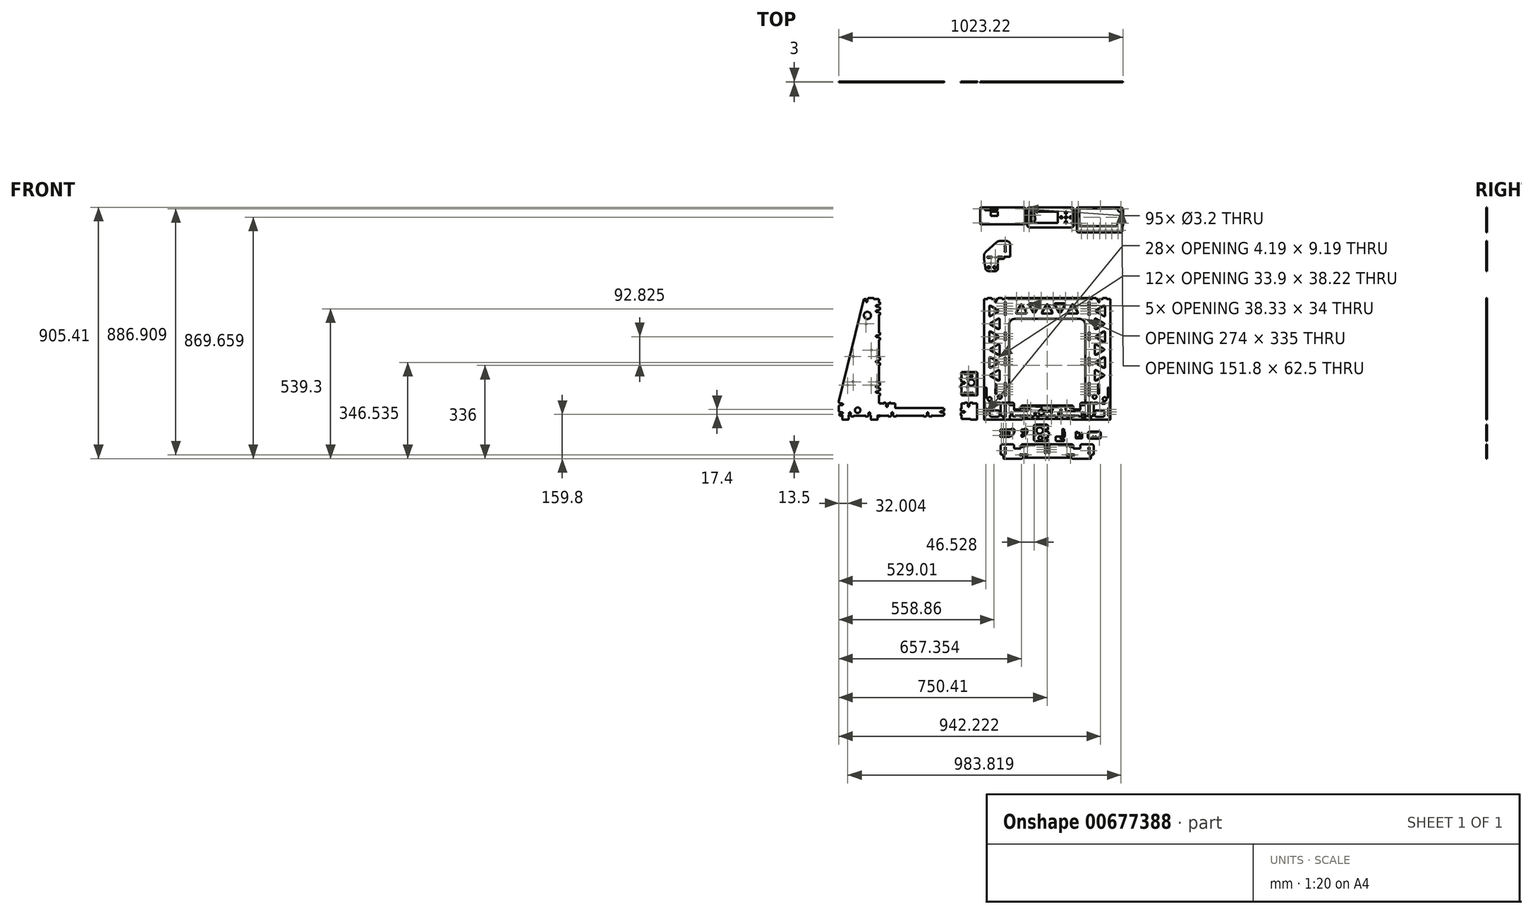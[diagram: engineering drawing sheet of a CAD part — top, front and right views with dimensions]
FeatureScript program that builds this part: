
annotation { "Feature Type Name" : "Feature", "Feature Type Description" : "" }
export const myFeature = defineFeature(function(context is Context, id is Id, definition is map)
    precondition{}
    {
        {
            var Q0;
            Q0=qCreatedBy(makeId("Front.planeOp"),FACE);
            var sketch = newSketch(context, id + "F0", { "sketchPlane" : qUnion([Q0])});
            skLineSegment(sketch, "E0", {"start": v(-153.6, 431.37) * mm, "end": v(-153.6, 433) * mm});
            skLineSegment(sketch, "E1", {"start": v(-177.67, 430.5) * mm, "end": v(-184.25, 430.5) * mm});
            skLineSegment(sketch, "E2", {"start": v(-153.1, 433.5) * mm, "end": v(153.1, 433.5) * mm});
            skLineSegment(sketch, "E3", {"start": v(153.6, 433) * mm, "end": v(153.6, 431.37) * mm});
            skLineSegment(sketch, "E4", {"start": v(177.67, 430.5) * mm, "end": v(184.25, 430.5) * mm});
            skLineSegment(sketch, "E5", {"start": v(-187.75, 430.5) * mm, "end": v(-199.13, 430.5) * mm});
            skLineSegment(sketch, "E6", {"start": v(-200, 433) * mm, "end": v(-200, 431.37) * mm});
            skLineSegment(sketch, "E7", {"start": v(-214.5, 433.5) * mm, "end": v(-200.5, 433.5) * mm});
            skLineSegment(sketch, "E8", {"start": v(187.75, 430.5) * mm, "end": v(199.13, 430.5) * mm});
            skLineSegment(sketch, "E9", {"start": v(-215, 431.37) * mm, "end": v(-215, 433) * mm});
            skLineSegment(sketch, "E10", {"start": v(200, 431.37) * mm, "end": v(200, 433) * mm});
            skLineSegment(sketch, "E11", {"start": v(-227.5, 430.5) * mm, "end": v(-215.87, 430.5) * mm});
            skLineSegment(sketch, "E12", {"start": v(200.5, 433.5) * mm, "end": v(214.5, 433.5) * mm});
            skLineSegment(sketch, "E13", {"start": v(-227.5, -3) * mm, "end": v(-227.5, 430.5) * mm});
            skLineSegment(sketch, "E14", {"start": v(215, 433) * mm, "end": v(215, 431.37) * mm});
            skLineSegment(sketch, "E15", {"start": v(-136.15, -5) * mm, "end": v(-225.5, -5) * mm});
            skLineSegment(sketch, "E16", {"start": v(215.87, 430.5) * mm, "end": v(227.5, 430.5) * mm});
            skLineSegment(sketch, "E17", {"start": v(227.5, 430.5) * mm, "end": v(227.5, -3) * mm});
            skLineSegment(sketch, "E18", {"start": v(112.48, 10) * mm, "end": v(58.52, 10) * mm});
            skLineSegment(sketch, "E19", {"start": v(225.5, -5) * mm, "end": v(136.15, -5) * mm});
            skArc(sketch, "E20", {"start": v(-186.8, 90) * mm, "mid": v(-185, 88.2) * mm, "end": v(-183.2, 90) * mm});
            skLineSegment(sketch, "E21", {"start": v(-183.2, 90) * mm, "end": v(-183.2, 122) * mm});
            skArc(sketch, "E22", {"start": v(-183.2, 122) * mm, "mid": v(-185, 123.8) * mm, "end": v(-186.8, 122) * mm});
            skLineSegment(sketch, "E23", {"start": v(-186.8, 90) * mm, "end": v(-186.8, 122) * mm});
            skCircle(sketch, "E24", {"center": v(-170.5, 78) * mm, "radius": 7 * mm});
            skCircle(sketch, "E25", {"center": v(151, 405.2) * mm, "radius": 1.6 * mm});
            skLineSegment(sketch, "E26", {"start": v(-221.8, 77) * mm, "end": v(-221.8, 109) * mm});
            skArc(sketch, "E27", {"start": v(-221.8, 77) * mm, "mid": v(-220, 75.2) * mm, "end": v(-218.2, 77) * mm});
            skLineSegment(sketch, "E28", {"start": v(-218.2, 77) * mm, "end": v(-218.2, 109) * mm});
            skArc(sketch, "E29", {"start": v(-218.2, 109) * mm, "mid": v(-220, 110.8) * mm, "end": v(-221.8, 109) * mm});
            skCircle(sketch, "E30", {"center": v(-207, 69.5) * mm, "radius": 7 * mm});
            skCircle(sketch, "E31", {"center": v(-54.75, 23) * mm, "radius": 1.6 * mm, "construction": true});
            skLineSegment(sketch, "E32", {"start": v(-137, 52.12) * mm, "end": v(-137, 338.5) * mm});
            skArc(sketch, "E33", {"start": v(-117, 358.5) * mm, "mid": v(-131.14, 352.64) * mm, "end": v(-137, 338.5) * mm});
            skLineSegment(sketch, "E34", {"start": v(-121.9, 47.12) * mm, "end": v(-132, 47.12) * mm});
            skLineSegment(sketch, "E35", {"start": v(-117, 358.5) * mm, "end": v(117, 358.5) * mm});
            skLineSegment(sketch, "E36", {"start": v(-118.9, 44.12) * mm, "end": v(-118.9, 33.5) * mm});
            skArc(sketch, "E37", {"start": v(137, 338.5) * mm, "mid": v(131.14, 352.64) * mm, "end": v(117, 358.5) * mm});
            skArc(sketch, "E38", {"start": v(-118.9, 33.5) * mm, "mid": v(-116.85, 28.55) * mm, "end": v(-111.9, 26.5) * mm});
            skLineSegment(sketch, "E39", {"start": v(137, 338.5) * mm, "end": v(137, 52.12) * mm});
            skLineSegment(sketch, "E40", {"start": v(118.9, 44.12) * mm, "end": v(118.9, 33.5) * mm});
            skArc(sketch, "E41", {"start": v(111.9, 26.5) * mm, "mid": v(116.85, 28.55) * mm, "end": v(118.9, 33.5) * mm});
            skLineSegment(sketch, "E42", {"start": v(-73, 26.5) * mm, "end": v(-111.9, 26.5) * mm});
            skArc(sketch, "E43", {"start": v(-73, 26.5) * mm, "mid": v(-68.05, 28.55) * mm, "end": v(-66, 33.5) * mm});
            skLineSegment(sketch, "E44", {"start": v(-66, 39.5) * mm, "end": v(-66, 33.5) * mm});
            skLineSegment(sketch, "E45", {"start": v(-23, 42.5) * mm, "end": v(-63, 42.5) * mm});
            skLineSegment(sketch, "E46", {"start": v(-20, 31.5) * mm, "end": v(-20, 39.5) * mm});
            skLineSegment(sketch, "E47", {"start": v(73, 26.5) * mm, "end": v(111.9, 26.5) * mm});
            skLineSegment(sketch, "E48", {"start": v(-17, 28.5) * mm, "end": v(-5, 28.5) * mm});
            skArc(sketch, "E49", {"start": v(66, 33.5) * mm, "mid": v(68.05, 28.55) * mm, "end": v(73, 26.5) * mm});
            skLineSegment(sketch, "E50", {"start": v(20, 31.5) * mm, "end": v(20, 39.5) * mm});
            skLineSegment(sketch, "E51", {"start": v(66, 39.5) * mm, "end": v(66, 33.5) * mm});
            skLineSegment(sketch, "E52", {"start": v(23, 42.5) * mm, "end": v(63, 42.5) * mm});
            skCircle(sketch, "E53", {"center": v(54.75, 23) * mm, "radius": 1.6 * mm, "construction": true});
            skCircle(sketch, "E54", {"center": v(-151, 95.5) * mm, "radius": 1.6 * mm});
            skCircle(sketch, "E55", {"center": v(-190.05, 271.15) * mm, "radius": 1.6 * mm});
            skCircle(sketch, "E56", {"center": v(-151, 295.7) * mm, "radius": 1.6 * mm});
            skLineSegment(sketch, "E57", {"start": v(-176.5, 28.4) * mm, "end": v(-201.5, 28.4) * mm});
            skArc(sketch, "E58", {"start": v(-201.5, 28.4) * mm, "mid": v(-205.04, 26.94) * mm, "end": v(-206.5, 23.4) * mm});
            skLineSegment(sketch, "E59", {"start": v(-206.5, 11.4) * mm, "end": v(-206.5, 23.4) * mm});
            skArc(sketch, "E60", {"start": v(-206.5, 11.4) * mm, "mid": v(-205.04, 7.86) * mm, "end": v(-201.5, 6.4) * mm});
            skLineSegment(sketch, "E61", {"start": v(-176.5, 6.4) * mm, "end": v(-201.5, 6.4) * mm});
            skArc(sketch, "E62", {"start": v(-176.5, 6.4) * mm, "mid": v(-172.96, 7.86) * mm, "end": v(-171.5, 11.4) * mm});
            skLineSegment(sketch, "E63", {"start": v(-171.5, 23.4) * mm, "end": v(-171.5, 11.4) * mm});
            skArc(sketch, "E64", {"start": v(-171.5, 23.4) * mm, "mid": v(-172.96, 26.94) * mm, "end": v(-176.5, 28.4) * mm});
            skCircle(sketch, "E65", {"center": v(170.5, 78) * mm, "radius": 7 * mm});
            skCircle(sketch, "E66", {"center": v(151, 247.95) * mm, "radius": 1.6 * mm, "construction": true});
            skCircle(sketch, "E67", {"center": v(-110, 427.5) * mm, "radius": 1.6 * mm});
            skCircle(sketch, "E68", {"center": v(-66, 427.5) * mm, "radius": 1.6 * mm});
            skCircle(sketch, "E69", {"center": v(-22, 427.5) * mm, "radius": 1.6 * mm});
            skCircle(sketch, "E70", {"center": v(110, 427.5) * mm, "radius": 1.6 * mm});
            skCircle(sketch, "E71", {"center": v(22, 427.5) * mm, "radius": 1.6 * mm});
            skCircle(sketch, "E72", {"center": v(66, 427.5) * mm, "radius": 1.6 * mm});
            skLineSegment(sketch, "E73", {"start": v(206.5, 11.4) * mm, "end": v(206.5, 23.4) * mm});
            skArc(sketch, "E74", {"start": v(206.5, 23.4) * mm, "mid": v(205.04, 26.94) * mm, "end": v(201.5, 28.4) * mm});
            skLineSegment(sketch, "E75", {"start": v(201.5, 28.4) * mm, "end": v(176.5, 28.4) * mm});
            skArc(sketch, "E76", {"start": v(176.5, 28.4) * mm, "mid": v(172.96, 26.94) * mm, "end": v(171.5, 23.4) * mm});
            skLineSegment(sketch, "E77", {"start": v(171.5, 23.4) * mm, "end": v(171.5, 11.4) * mm});
            skArc(sketch, "E78", {"start": v(171.5, 11.4) * mm, "mid": v(172.96, 7.86) * mm, "end": v(176.5, 6.4) * mm});
            skLineSegment(sketch, "E79", {"start": v(176.5, 6.4) * mm, "end": v(201.5, 6.4) * mm});
            skArc(sketch, "E80", {"start": v(201.5, 6.4) * mm, "mid": v(205.04, 7.86) * mm, "end": v(206.5, 11.4) * mm});
            skCircle(sketch, "E81", {"center": v(207, 69.5) * mm, "radius": 7 * mm});
            skLineSegment(sketch, "E82", {"start": v(221.8, 77) * mm, "end": v(221.8, 109) * mm});
            skArc(sketch, "E83", {"start": v(221.8, 109) * mm, "mid": v(220, 110.8) * mm, "end": v(218.2, 109) * mm});
            skLineSegment(sketch, "E84", {"start": v(218.2, 77) * mm, "end": v(218.2, 109) * mm});
            skArc(sketch, "E85", {"start": v(218.2, 77) * mm, "mid": v(220, 75.2) * mm, "end": v(221.8, 77) * mm});
            skLineSegment(sketch, "E86", {"start": v(183.2, 90) * mm, "end": v(183.2, 122) * mm});
            skArc(sketch, "E87", {"start": v(183.2, 90) * mm, "mid": v(185, 88.2) * mm, "end": v(186.8, 90) * mm});
            skLineSegment(sketch, "E88", {"start": v(186.8, 90) * mm, "end": v(186.8, 122) * mm});
            skArc(sketch, "E89", {"start": v(186.8, 122) * mm, "mid": v(185, 123.8) * mm, "end": v(183.2, 122) * mm});
            skPoint(sketch, "E90", {"position": v(149.4, 119.6) * mm});
            skPoint(sketch, "E91", {"position": v(149.4, 100.8) * mm});
            skPoint(sketch, "E92", {"position": v(-151, 418.7) * mm});
            skLineSegment(sketch, "E93.bottom", {"start": v(-151.73, 290.4) * mm, "end": v(-150.27, 290.4) * mm});
            skLineSegment(sketch, "E93.top", {"start": v(-151.73, 282.2) * mm, "end": v(-150.27, 282.2) * mm});
            skLineSegment(sketch, "E93.left", {"start": v(-152.6, 289.53) * mm, "end": v(-152.6, 283.07) * mm});
            skLineSegment(sketch, "E93.right", {"start": v(-149.4, 289.53) * mm, "end": v(-149.4, 283.07) * mm});
            skLineSegment(sketch, "E94", {"start": v(0, 526.3) * mm, "end": v(0, -105) * mm, "construction": true});
            skLineSegment(sketch, "E95", {"start": v(-134.15, -3) * mm, "end": v(-134.15, 9.13) * mm});
            skLineSegment(sketch, "E96", {"start": v(134.15, -3) * mm, "end": v(134.15, 9.13) * mm});
            skArc(sketch, "E97", {"start": v(-133, 625.46) * mm, "mid": v(-137.07, 635.28) * mm, "end": v(-146.9, 639.36) * mm});
            skLineSegment(sketch, "E98", {"start": v(-133, 582.36) * mm, "end": v(-133, 625.46) * mm});
            skLineSegment(sketch, "E99", {"start": v(-133, 582.36) * mm, "end": v(-152.84, 582.36) * mm});
            skArc(sketch, "E100", {"start": v(-189.5, 529.87) * mm, "mid": v(-180.7, 533.2) * mm, "end": v(-177, 541.86) * mm});
            skLineSegment(sketch, "E101", {"start": v(-189.5, 529.87) * mm, "end": v(-211.45, 530.76) * mm});
            skArc(sketch, "E102", {"start": v(-221.96, 540.12) * mm, "mid": v(-218.38, 533.56) * mm, "end": v(-211.45, 530.76) * mm});
            skLineSegment(sketch, "E103", {"start": v(-221.96, 540.12) * mm, "end": v(-227.25, 573.53) * mm});
            skArc(sketch, "E104", {"start": v(-227.5, 576.66) * mm, "mid": v(-227.44, 575.09) * mm, "end": v(-227.25, 573.53) * mm});
            skLineSegment(sketch, "E105", {"start": v(-227.5, 584.86) * mm, "end": v(-227.5, 576.66) * mm});
            skArc(sketch, "E106", {"start": v(-220.9, 599.7) * mm, "mid": v(-225.78, 592.98) * mm, "end": v(-227.5, 584.86) * mm});
            skLineSegment(sketch, "E107", {"start": v(-182.71, 634.2) * mm, "end": v(-220.9, 599.7) * mm});
            skArc(sketch, "E108", {"start": v(-169.3, 639.36) * mm, "mid": v(-176.49, 638.02) * mm, "end": v(-182.71, 634.2) * mm});
            skLineSegment(sketch, "E109", {"start": v(-146.9, 639.36) * mm, "end": v(-169.3, 639.36) * mm});
            skLineSegment(sketch, "E110", {"start": v(-149.4, 620.6) * mm, "end": v(-149.4, 601.92) * mm});
            skLineSegment(sketch, "E111", {"start": v(-152.6, 601.92) * mm, "end": v(-152.6, 620.59) * mm});
            skCircle(sketch, "E112", {"center": v(-189, 544.26) * mm, "radius": 5 * mm});
            skCircle(sketch, "E113", {"center": v(-211, 544.26) * mm, "radius": 4.1 * mm});
            skCircle(sketch, "E114", {"center": v(-186, 580.76) * mm, "radius": 1.6 * mm});
            skCircle(sketch, "E115", {"center": v(-151, 626.86) * mm, "radius": 1.6 * mm});
            skCircle(sketch, "E116", {"center": v(-202, 559.26) * mm, "radius": 1.6 * mm});
            skPoint(sketch, "E117", {"position": v(-207.5, 433.5) * mm});
            skLineSegment(sketch, "E118", {"start": v(-214.23, 579.16) * mm, "end": v(-200.77, 579.16) * mm});
            skLineSegment(sketch, "E119", {"start": v(-200.77, 582.36) * mm, "end": v(-214.23, 582.36) * mm});
            skCircle(sketch, "E120.cCircle", {"center": v(-183.9, 155.12) * mm, "radius": 12.3 * mm, "construction": true});
            skLineSegment(sketch, "E120.0", {"start": v(-171.6, 171.23) * mm, "end": v(-171.6, 139.01) * mm});
            skLineSegment(sketch, "E120.1", {"start": v(-176.1, 136.42) * mm, "end": v(-204, 152.52) * mm});
            skLineSegment(sketch, "E120.2", {"start": v(-204, 157.72) * mm, "end": v(-176.1, 173.83) * mm});
            skPoint(sketch, "E120.0.midPoint", {"position": v(-171.6, 155.12) * mm});
            skPoint(sketch, "E121.visualSharp", {"position": v(-208.5, 155.12) * mm});
            skArc(sketch, "E121.filletArc", {"start": v(-204, 157.72) * mm, "mid": v(-205.5, 155.12) * mm, "end": v(-204, 152.52) * mm});
            skPoint(sketch, "E122.visualSharp", {"position": v(-171.6, 176.43) * mm});
            skArc(sketch, "E122.filletArc", {"start": v(-171.6, 171.23) * mm, "mid": v(-173.1, 173.83) * mm, "end": v(-176.1, 173.83) * mm});
            skPoint(sketch, "E123.visualSharp", {"position": v(-171.6, 133.82) * mm});
            skArc(sketch, "E123.filletArc", {"start": v(-176.1, 136.42) * mm, "mid": v(-173.1, 136.42) * mm, "end": v(-171.6, 139.01) * mm});
            skCircle(sketch, "E124.cCircle", {"center": v(0, 389.63) * mm, "radius": 12.33 * mm, "construction": true});
            skLineSegment(sketch, "E124.0", {"start": v(16.17, 377.3) * mm, "end": v(-16.17, 377.3) * mm});
            skLineSegment(sketch, "E124.1", {"start": v(-18.76, 381.8) * mm, "end": v(-2.6, 409.8) * mm});
            skLineSegment(sketch, "E124.2", {"start": v(2.6, 409.8) * mm, "end": v(18.76, 381.8) * mm});
            skPoint(sketch, "E124.0.midPoint", {"position": v(0, 377.3) * mm});
            skCircle(sketch, "E125.cCircle", {"center": v(-196.2, 201.54) * mm, "radius": 12.3 * mm, "construction": true});
            skLineSegment(sketch, "E125.0", {"start": v(-208.5, 185.43) * mm, "end": v(-208.5, 217.64) * mm});
            skLineSegment(sketch, "E125.1", {"start": v(-204, 220.24) * mm, "end": v(-176.1, 204.13) * mm});
            skLineSegment(sketch, "E125.2", {"start": v(-176.1, 198.94) * mm, "end": v(-204, 182.83) * mm});
            skPoint(sketch, "E125.0.midPoint", {"position": v(-208.5, 201.54) * mm});
            skPoint(sketch, "E126.visualSharp", {"position": v(-171.6, 201.54) * mm});
            skArc(sketch, "E126.filletArc", {"start": v(-176.1, 198.94) * mm, "mid": v(-174.6, 201.54) * mm, "end": v(-176.1, 204.13) * mm});
            skPoint(sketch, "E127.visualSharp", {"position": v(-208.5, 180.23) * mm});
            skArc(sketch, "E127.filletArc", {"start": v(-208.5, 185.43) * mm, "mid": v(-207, 182.83) * mm, "end": v(-204, 182.83) * mm});
            skPoint(sketch, "E128.visualSharp", {"position": v(-208.5, 222.84) * mm});
            skArc(sketch, "E128.filletArc", {"start": v(-204, 220.24) * mm, "mid": v(-207, 220.24) * mm, "end": v(-208.5, 217.64) * mm});
            skCircle(sketch, "E129.cCircle", {"center": v(-183.9, 247.95) * mm, "radius": 12.3 * mm, "construction": true});
            skLineSegment(sketch, "E129.0", {"start": v(-171.6, 264.06) * mm, "end": v(-171.6, 231.84) * mm});
            skLineSegment(sketch, "E129.1", {"start": v(-176.1, 229.24) * mm, "end": v(-204, 245.35) * mm});
            skLineSegment(sketch, "E129.2", {"start": v(-204, 250.55) * mm, "end": v(-176.1, 266.65) * mm});
            skPoint(sketch, "E129.0.midPoint", {"position": v(-171.6, 247.95) * mm});
            skPoint(sketch, "E130.visualSharp", {"position": v(-208.5, 247.95) * mm});
            skArc(sketch, "E130.filletArc", {"start": v(-204, 250.55) * mm, "mid": v(-205.5, 247.95) * mm, "end": v(-204, 245.35) * mm});
            skPoint(sketch, "E131.visualSharp", {"position": v(-171.6, 269.25) * mm});
            skArc(sketch, "E131.filletArc", {"start": v(-171.6, 264.06) * mm, "mid": v(-173.1, 266.65) * mm, "end": v(-176.1, 266.65) * mm});
            skPoint(sketch, "E132.visualSharp", {"position": v(-171.6, 226.64) * mm});
            skArc(sketch, "E132.filletArc", {"start": v(-176.1, 229.24) * mm, "mid": v(-173.1, 229.24) * mm, "end": v(-171.6, 231.84) * mm});
            skCircle(sketch, "E133.cCircle", {"center": v(-196.2, 294.36) * mm, "radius": 12.3 * mm, "construction": true});
            skLineSegment(sketch, "E133.0", {"start": v(-208.5, 278.25) * mm, "end": v(-208.5, 310.47) * mm});
            skLineSegment(sketch, "E133.1", {"start": v(-204, 313.07) * mm, "end": v(-176.1, 296.96) * mm});
            skLineSegment(sketch, "E133.2", {"start": v(-176.1, 291.76) * mm, "end": v(-204, 275.65) * mm});
            skPoint(sketch, "E133.0.midPoint", {"position": v(-208.5, 294.36) * mm});
            skPoint(sketch, "E134.visualSharp", {"position": v(-171.6, 294.36) * mm});
            skArc(sketch, "E134.filletArc", {"start": v(-176.1, 291.76) * mm, "mid": v(-174.6, 294.36) * mm, "end": v(-176.1, 296.96) * mm});
            skPoint(sketch, "E135.visualSharp", {"position": v(-208.5, 273.06) * mm});
            skArc(sketch, "E135.filletArc", {"start": v(-208.5, 278.25) * mm, "mid": v(-207, 275.65) * mm, "end": v(-204, 275.65) * mm});
            skPoint(sketch, "E136.visualSharp", {"position": v(-208.5, 315.66) * mm});
            skArc(sketch, "E136.filletArc", {"start": v(-204, 313.07) * mm, "mid": v(-207, 313.07) * mm, "end": v(-208.5, 310.47) * mm});
            skCircle(sketch, "E137.cCircle", {"center": v(-183.9, 340.77) * mm, "radius": 12.3 * mm, "construction": true});
            skLineSegment(sketch, "E137.0", {"start": v(-171.6, 356.88) * mm, "end": v(-171.6, 324.66) * mm});
            skLineSegment(sketch, "E137.1", {"start": v(-176.1, 322.07) * mm, "end": v(-204, 338.17) * mm});
            skLineSegment(sketch, "E137.2", {"start": v(-204, 343.37) * mm, "end": v(-176.1, 359.48) * mm});
            skPoint(sketch, "E137.0.midPoint", {"position": v(-171.6, 340.77) * mm});
            skPoint(sketch, "E138.visualSharp", {"position": v(-208.5, 340.77) * mm});
            skArc(sketch, "E138.filletArc", {"start": v(-204, 343.37) * mm, "mid": v(-205.5, 340.77) * mm, "end": v(-204, 338.17) * mm});
            skPoint(sketch, "E139.visualSharp", {"position": v(-171.6, 362.08) * mm});
            skArc(sketch, "E139.filletArc", {"start": v(-171.6, 356.88) * mm, "mid": v(-173.1, 359.48) * mm, "end": v(-176.1, 359.48) * mm});
            skPoint(sketch, "E140.visualSharp", {"position": v(-171.6, 319.47) * mm});
            skArc(sketch, "E140.filletArc", {"start": v(-176.1, 322.07) * mm, "mid": v(-173.1, 322.07) * mm, "end": v(-171.6, 324.66) * mm});
            skLineSegment(sketch, "E141.0", {"start": v(-176.7, 414.3) * mm, "end": v(176.7, 414.3) * mm, "construction": true});
            skPoint(sketch, "E142.visualSharp", {"position": v(-21.36, 377.3) * mm});
            skArc(sketch, "E142.filletArc", {"start": v(-18.76, 381.8) * mm, "mid": v(-18.76, 378.8) * mm, "end": v(-16.17, 377.3) * mm});
            skPoint(sketch, "E143.visualSharp", {"position": v(0, 414.3) * mm});
            skArc(sketch, "E143.filletArc", {"start": v(2.6, 409.8) * mm, "mid": v(0, 411.3) * mm, "end": v(-2.6, 409.8) * mm});
            skPoint(sketch, "E144.visualSharp", {"position": v(21.36, 377.3) * mm});
            skArc(sketch, "E144.filletArc", {"start": v(16.17, 377.3) * mm, "mid": v(18.76, 378.8) * mm, "end": v(18.76, 381.8) * mm});
            skCircle(sketch, "E145.cCircle", {"center": v(-46.53, 401.97) * mm, "radius": 12.33 * mm, "construction": true});
            skLineSegment(sketch, "E145.0", {"start": v(-62.7, 414.3) * mm, "end": v(-30.36, 414.3) * mm});
            skLineSegment(sketch, "E145.1", {"start": v(-27.76, 409.8) * mm, "end": v(-43.93, 381.8) * mm});
            skLineSegment(sketch, "E145.2", {"start": v(-49.13, 381.8) * mm, "end": v(-65.3, 409.8) * mm});
            skPoint(sketch, "E145.0.midPoint", {"position": v(-46.53, 414.3) * mm});
            skPoint(sketch, "E146.visualSharp", {"position": v(-46.53, 377.3) * mm});
            skArc(sketch, "E146.filletArc", {"start": v(-49.13, 381.8) * mm, "mid": v(-46.53, 380.3) * mm, "end": v(-43.93, 381.8) * mm});
            skPoint(sketch, "E147.visualSharp", {"position": v(-67.89, 414.3) * mm});
            skArc(sketch, "E147.filletArc", {"start": v(-62.7, 414.3) * mm, "mid": v(-65.3, 412.8) * mm, "end": v(-65.3, 409.8) * mm});
            skPoint(sketch, "E148.visualSharp", {"position": v(-25.17, 414.3) * mm});
            skArc(sketch, "E148.filletArc", {"start": v(-27.76, 409.8) * mm, "mid": v(-27.76, 412.8) * mm, "end": v(-30.36, 414.3) * mm});
            skCircle(sketch, "E149.cCircle", {"center": v(45.53, 401.97) * mm, "radius": 12.33 * mm, "construction": true});
            skLineSegment(sketch, "E149.0", {"start": v(29.36, 414.3) * mm, "end": v(61.7, 414.3) * mm});
            skLineSegment(sketch, "E149.1", {"start": v(64.3, 409.8) * mm, "end": v(48.13, 381.8) * mm});
            skLineSegment(sketch, "E149.2", {"start": v(42.93, 381.8) * mm, "end": v(26.76, 409.8) * mm});
            skPoint(sketch, "E149.0.midPoint", {"position": v(45.53, 414.3) * mm});
            skPoint(sketch, "E150.visualSharp", {"position": v(45.53, 377.3) * mm});
            skArc(sketch, "E150.filletArc", {"start": v(42.93, 381.8) * mm, "mid": v(45.53, 380.3) * mm, "end": v(48.13, 381.8) * mm});
            skPoint(sketch, "E151.visualSharp", {"position": v(24.17, 414.3) * mm});
            skArc(sketch, "E151.filletArc", {"start": v(29.36, 414.3) * mm, "mid": v(26.76, 412.8) * mm, "end": v(26.76, 409.8) * mm});
            skPoint(sketch, "E152.visualSharp", {"position": v(66.89, 414.3) * mm});
            skArc(sketch, "E152.filletArc", {"start": v(64.3, 409.8) * mm, "mid": v(64.3, 412.8) * mm, "end": v(61.7, 414.3) * mm});
            skCircle(sketch, "E153.cCircle", {"center": v(92.06, 389.63) * mm, "radius": 12.33 * mm, "construction": true});
            skLineSegment(sketch, "E153.0", {"start": v(108.22, 377.3) * mm, "end": v(75.89, 377.3) * mm});
            skLineSegment(sketch, "E153.1", {"start": v(73.3, 381.8) * mm, "end": v(89.46, 409.8) * mm});
            skLineSegment(sketch, "E153.2", {"start": v(94.65, 409.8) * mm, "end": v(110.82, 381.8) * mm});
            skPoint(sketch, "E153.0.midPoint", {"position": v(92.06, 377.3) * mm});
            skPoint(sketch, "E154.visualSharp", {"position": v(70.7, 377.3) * mm});
            skArc(sketch, "E154.filletArc", {"start": v(73.3, 381.8) * mm, "mid": v(73.3, 378.8) * mm, "end": v(75.89, 377.3) * mm});
            skPoint(sketch, "E155.visualSharp", {"position": v(92.06, 414.3) * mm});
            skArc(sketch, "E155.filletArc", {"start": v(94.65, 409.8) * mm, "mid": v(92.06, 411.3) * mm, "end": v(89.46, 409.8) * mm});
            skPoint(sketch, "E156.visualSharp", {"position": v(113.42, 377.3) * mm});
            skArc(sketch, "E156.filletArc", {"start": v(108.22, 377.3) * mm, "mid": v(110.82, 378.8) * mm, "end": v(110.82, 381.8) * mm});
            skCircle(sketch, "E157.cCircle", {"center": v(-93.06, 389.63) * mm, "radius": 12.33 * mm, "construction": true});
            skLineSegment(sketch, "E157.0", {"start": v(-76.89, 377.3) * mm, "end": v(-109.22, 377.3) * mm});
            skLineSegment(sketch, "E157.1", {"start": v(-111.82, 381.8) * mm, "end": v(-95.65, 409.8) * mm});
            skLineSegment(sketch, "E157.2", {"start": v(-90.46, 409.8) * mm, "end": v(-74.3, 381.8) * mm});
            skPoint(sketch, "E157.0.midPoint", {"position": v(-93.06, 377.3) * mm});
            skPoint(sketch, "E158.visualSharp", {"position": v(-114.42, 377.3) * mm});
            skArc(sketch, "E158.filletArc", {"start": v(-111.82, 381.8) * mm, "mid": v(-111.82, 378.8) * mm, "end": v(-109.22, 377.3) * mm});
            skPoint(sketch, "E159.visualSharp", {"position": v(-93.06, 414.3) * mm});
            skArc(sketch, "E159.filletArc", {"start": v(-90.46, 409.8) * mm, "mid": v(-93.06, 411.3) * mm, "end": v(-95.65, 409.8) * mm});
            skPoint(sketch, "E160.visualSharp", {"position": v(-71.7, 377.3) * mm});
            skArc(sketch, "E160.filletArc", {"start": v(-76.89, 377.3) * mm, "mid": v(-74.3, 378.8) * mm, "end": v(-74.3, 381.8) * mm});
            skLineSegment(sketch, "E161", {"start": v(-294.24, 247.95) * mm, "end": v(257.8, 247.95) * mm, "construction": true});
            skCircle(sketch, "E162.cCircle", {"center": v(196.2, 294.36) * mm, "radius": 12.3 * mm, "construction": true});
            skLineSegment(sketch, "E162.0", {"start": v(208.5, 310.47) * mm, "end": v(208.5, 278.25) * mm});
            skLineSegment(sketch, "E162.1", {"start": v(204, 275.65) * mm, "end": v(176.1, 291.76) * mm});
            skLineSegment(sketch, "E162.2", {"start": v(176.1, 296.96) * mm, "end": v(204, 313.07) * mm});
            skPoint(sketch, "E162.0.midPoint", {"position": v(208.5, 294.36) * mm});
            skPoint(sketch, "E163.visualSharp", {"position": v(171.6, 294.36) * mm});
            skArc(sketch, "E163.filletArc", {"start": v(176.1, 296.96) * mm, "mid": v(174.6, 294.36) * mm, "end": v(176.1, 291.76) * mm});
            skPoint(sketch, "E164.visualSharp", {"position": v(208.5, 315.66) * mm});
            skArc(sketch, "E164.filletArc", {"start": v(208.5, 310.47) * mm, "mid": v(207, 313.07) * mm, "end": v(204, 313.07) * mm});
            skPoint(sketch, "E165.visualSharp", {"position": v(208.5, 273.06) * mm});
            skArc(sketch, "E165.filletArc", {"start": v(204, 275.65) * mm, "mid": v(207, 275.65) * mm, "end": v(208.5, 278.25) * mm});
            skCircle(sketch, "E166.cCircle", {"center": v(183.9, 340.77) * mm, "radius": 12.3 * mm, "construction": true});
            skLineSegment(sketch, "E166.0", {"start": v(171.6, 324.66) * mm, "end": v(171.6, 356.88) * mm});
            skLineSegment(sketch, "E166.1", {"start": v(176.1, 359.48) * mm, "end": v(204, 343.37) * mm});
            skLineSegment(sketch, "E166.2", {"start": v(204, 338.17) * mm, "end": v(176.1, 322.07) * mm});
            skPoint(sketch, "E166.0.midPoint", {"position": v(171.6, 340.77) * mm});
            skPoint(sketch, "E167.visualSharp", {"position": v(208.5, 340.77) * mm});
            skArc(sketch, "E167.filletArc", {"start": v(204, 338.17) * mm, "mid": v(205.5, 340.77) * mm, "end": v(204, 343.37) * mm});
            skPoint(sketch, "E168.visualSharp", {"position": v(171.6, 319.47) * mm});
            skArc(sketch, "E168.filletArc", {"start": v(171.6, 324.66) * mm, "mid": v(173.1, 322.07) * mm, "end": v(176.1, 322.07) * mm});
            skPoint(sketch, "E169.visualSharp", {"position": v(171.6, 362.08) * mm});
            skArc(sketch, "E169.filletArc", {"start": v(176.1, 359.48) * mm, "mid": v(173.1, 359.48) * mm, "end": v(171.6, 356.88) * mm});
            skCircle(sketch, "E170.cCircle", {"center": v(196.2, 201.54) * mm, "radius": 12.3 * mm, "construction": true});
            skLineSegment(sketch, "E170.0", {"start": v(208.5, 217.64) * mm, "end": v(208.5, 185.43) * mm});
            skLineSegment(sketch, "E170.1", {"start": v(204, 182.83) * mm, "end": v(176.1, 198.94) * mm});
            skLineSegment(sketch, "E170.2", {"start": v(176.1, 204.13) * mm, "end": v(204, 220.24) * mm});
            skPoint(sketch, "E170.0.midPoint", {"position": v(208.5, 201.54) * mm});
            skPoint(sketch, "E171.visualSharp", {"position": v(171.6, 201.54) * mm});
            skArc(sketch, "E171.filletArc", {"start": v(176.1, 204.13) * mm, "mid": v(174.6, 201.54) * mm, "end": v(176.1, 198.94) * mm});
            skPoint(sketch, "E172.visualSharp", {"position": v(208.5, 222.84) * mm});
            skArc(sketch, "E172.filletArc", {"start": v(208.5, 217.64) * mm, "mid": v(207, 220.24) * mm, "end": v(204, 220.24) * mm});
            skPoint(sketch, "E173.visualSharp", {"position": v(208.5, 180.23) * mm});
            skArc(sketch, "E173.filletArc", {"start": v(204, 182.83) * mm, "mid": v(207, 182.83) * mm, "end": v(208.5, 185.43) * mm});
            skCircle(sketch, "E174.cCircle", {"center": v(183.9, 247.95) * mm, "radius": 12.3 * mm, "construction": true});
            skLineSegment(sketch, "E174.0", {"start": v(171.6, 231.84) * mm, "end": v(171.6, 264.06) * mm});
            skLineSegment(sketch, "E174.1", {"start": v(176.1, 266.65) * mm, "end": v(204, 250.55) * mm});
            skLineSegment(sketch, "E174.2", {"start": v(204, 245.35) * mm, "end": v(176.1, 229.24) * mm});
            skPoint(sketch, "E174.0.midPoint", {"position": v(171.6, 247.95) * mm});
            skPoint(sketch, "E175.visualSharp", {"position": v(208.5, 247.95) * mm});
            skArc(sketch, "E175.filletArc", {"start": v(204, 245.35) * mm, "mid": v(205.5, 247.95) * mm, "end": v(204, 250.55) * mm});
            skPoint(sketch, "E176.visualSharp", {"position": v(171.6, 226.64) * mm});
            skArc(sketch, "E176.filletArc", {"start": v(171.6, 231.84) * mm, "mid": v(173.1, 229.24) * mm, "end": v(176.1, 229.24) * mm});
            skPoint(sketch, "E177.visualSharp", {"position": v(171.6, 269.25) * mm});
            skArc(sketch, "E177.filletArc", {"start": v(176.1, 266.65) * mm, "mid": v(173.1, 266.65) * mm, "end": v(171.6, 264.06) * mm});
            skCircle(sketch, "E178.cCircle", {"center": v(183.9, 155.12) * mm, "radius": 12.3 * mm, "construction": true});
            skLineSegment(sketch, "E178.0", {"start": v(171.6, 139.01) * mm, "end": v(171.6, 171.23) * mm});
            skLineSegment(sketch, "E178.1", {"start": v(176.1, 173.83) * mm, "end": v(204, 157.72) * mm});
            skLineSegment(sketch, "E178.2", {"start": v(204, 152.52) * mm, "end": v(176.1, 136.42) * mm});
            skPoint(sketch, "E178.0.midPoint", {"position": v(171.6, 155.12) * mm});
            skPoint(sketch, "E179.visualSharp", {"position": v(208.5, 155.12) * mm});
            skArc(sketch, "E179.filletArc", {"start": v(204, 152.52) * mm, "mid": v(205.5, 155.12) * mm, "end": v(204, 157.72) * mm});
            skPoint(sketch, "E180.visualSharp", {"position": v(171.6, 133.82) * mm});
            skArc(sketch, "E180.filletArc", {"start": v(171.6, 139.01) * mm, "mid": v(173.1, 136.42) * mm, "end": v(176.1, 136.42) * mm});
            skPoint(sketch, "E181.visualSharp", {"position": v(171.6, 176.43) * mm});
            skArc(sketch, "E181.filletArc", {"start": v(176.1, 173.83) * mm, "mid": v(173.1, 173.83) * mm, "end": v(171.6, 171.23) * mm});
            skPoint(sketch, "E182.visualSharp", {"position": v(171.6, 387.18) * mm});
            skLineSegment(sketch, "E183", {"start": v(121.9, 47.12) * mm, "end": v(132, 47.12) * mm});
            skArc(sketch, "E184.filletArc", {"start": v(-63, 42.5) * mm, "mid": v(-65.12, 41.62) * mm, "end": v(-66, 39.5) * mm});
            skArc(sketch, "E185.filletArc", {"start": v(-20, 39.5) * mm, "mid": v(-20.88, 41.62) * mm, "end": v(-23, 42.5) * mm});
            skArc(sketch, "E186.filletArc", {"start": v(23, 42.5) * mm, "mid": v(20.88, 41.62) * mm, "end": v(20, 39.5) * mm});
            skArc(sketch, "E187.filletArc", {"start": v(-20, 31.5) * mm, "mid": v(-19.12, 29.38) * mm, "end": v(-17, 28.5) * mm});
            skArc(sketch, "E188.filletArc", {"start": v(17, 28.5) * mm, "mid": v(19.12, 29.38) * mm, "end": v(20, 31.5) * mm});
            skArc(sketch, "E189.filletArc", {"start": v(66, 39.5) * mm, "mid": v(65.12, 41.62) * mm, "end": v(63, 42.5) * mm});
            skArc(sketch, "E190.filletArc", {"start": v(-118.9, 44.12) * mm, "mid": v(-119.78, 46.24) * mm, "end": v(-121.9, 47.12) * mm});
            skArc(sketch, "E191.filletArc", {"start": v(121.9, 47.12) * mm, "mid": v(119.78, 46.24) * mm, "end": v(118.9, 44.12) * mm});
            skLineSegment(sketch, "E192", {"start": v(-610.4, -3) * mm, "end": v(-610.4, 9.13) * mm});
            skLineSegment(sketch, "E193", {"start": v(-605.4, 97.25) * mm, "end": v(-605.4, 100.03) * mm});
            skLineSegment(sketch, "E194", {"start": v(-604.54, 100.9) * mm, "end": v(-602.9, 100.9) * mm});
            skLineSegment(sketch, "E195", {"start": v(-602.4, 101.4) * mm, "end": v(-602.4, 108.4) * mm});
            skLineSegment(sketch, "E196", {"start": v(-602.9, 108.9) * mm, "end": v(-604.54, 108.9) * mm});
            skLineSegment(sketch, "E197", {"start": v(-605.4, 109.76) * mm, "end": v(-605.4, 112.55) * mm});
            skLineSegment(sketch, "E198", {"start": v(-605.4, 116.05) * mm, "end": v(-605.4, 118.83) * mm});
            skLineSegment(sketch, "E199", {"start": v(-604.54, 119.7) * mm, "end": v(-602.9, 119.7) * mm});
            skLineSegment(sketch, "E200", {"start": v(-602.4, 120.2) * mm, "end": v(-602.4, 127.2) * mm});
            skLineSegment(sketch, "E201", {"start": v(-602.9, 127.7) * mm, "end": v(-604.54, 127.7) * mm});
            skLineSegment(sketch, "E202", {"start": v(-605.4, 128.56) * mm, "end": v(-605.4, 190.73) * mm});
            skLineSegment(sketch, "E203", {"start": v(-604.54, 191.6) * mm, "end": v(-602.9, 191.6) * mm});
            skLineSegment(sketch, "E204", {"start": v(-602.4, 192.1) * mm, "end": v(-602.4, 199.1) * mm});
            skLineSegment(sketch, "E205", {"start": v(-602.9, 199.6) * mm, "end": v(-604.54, 199.6) * mm});
            skLineSegment(sketch, "E206", {"start": v(-605.4, 200.46) * mm, "end": v(-605.4, 203.25) * mm});
            skLineSegment(sketch, "E207", {"start": v(-605.4, 206.75) * mm, "end": v(-605.4, 209.53) * mm});
            skLineSegment(sketch, "E208", {"start": v(-604.54, 210.4) * mm, "end": v(-602.9, 210.4) * mm});
            skLineSegment(sketch, "E209", {"start": v(-602.4, 210.9) * mm, "end": v(-602.4, 217.9) * mm});
            skLineSegment(sketch, "E210", {"start": v(-602.9, 218.4) * mm, "end": v(-604.54, 218.4) * mm});
            skLineSegment(sketch, "E211", {"start": v(-605.4, 219.26) * mm, "end": v(-605.4, 281.43) * mm});
            skLineSegment(sketch, "E212", {"start": v(-604.54, 282.3) * mm, "end": v(-602.9, 282.3) * mm});
            skLineSegment(sketch, "E213", {"start": v(-602.4, 282.8) * mm, "end": v(-602.4, 289.8) * mm});
            skLineSegment(sketch, "E214", {"start": v(-602.9, 290.3) * mm, "end": v(-604.54, 290.3) * mm});
            skLineSegment(sketch, "E215", {"start": v(-605.4, 291.16) * mm, "end": v(-605.4, 293.95) * mm});
            skLineSegment(sketch, "E216", {"start": v(-605.4, 297.45) * mm, "end": v(-605.4, 300.23) * mm});
            skLineSegment(sketch, "E217", {"start": v(-604.54, 301.1) * mm, "end": v(-602.9, 301.1) * mm});
            skLineSegment(sketch, "E218", {"start": v(-602.4, 301.6) * mm, "end": v(-602.4, 308.6) * mm});
            skLineSegment(sketch, "E219", {"start": v(-602.9, 309.1) * mm, "end": v(-604.54, 309.1) * mm});
            skLineSegment(sketch, "E220", {"start": v(-605.4, 372.13) * mm, "end": v(-605.4, 309.97) * mm});
            skLineSegment(sketch, "E221", {"start": v(-604.54, 373) * mm, "end": v(-602.9, 373) * mm});
            skLineSegment(sketch, "E222", {"start": v(-602.4, 373.5) * mm, "end": v(-602.4, 380.5) * mm});
            skLineSegment(sketch, "E223", {"start": v(-602.9, 381) * mm, "end": v(-604.54, 381) * mm});
            skLineSegment(sketch, "E224", {"start": v(-605.4, 381.87) * mm, "end": v(-605.4, 384.65) * mm});
            skLineSegment(sketch, "E225", {"start": v(-605.4, 388.15) * mm, "end": v(-605.4, 390.93) * mm});
            skLineSegment(sketch, "E226", {"start": v(-604.54, 391.8) * mm, "end": v(-602.9, 391.8) * mm});
            skLineSegment(sketch, "E227", {"start": v(-602.4, 392.3) * mm, "end": v(-602.4, 399.3) * mm});
            skLineSegment(sketch, "E228", {"start": v(-602.9, 399.8) * mm, "end": v(-604.54, 399.8) * mm});
            skLineSegment(sketch, "E229", {"start": v(-605.4, 400.67) * mm, "end": v(-605.4, 403.45) * mm});
            skLineSegment(sketch, "E230", {"start": v(-605.4, 406.95) * mm, "end": v(-605.4, 409.73) * mm});
            skLineSegment(sketch, "E231", {"start": v(-604.54, 410.6) * mm, "end": v(-602.9, 410.6) * mm});
            skLineSegment(sketch, "E232", {"start": v(-602.4, 411.1) * mm, "end": v(-602.4, 418.1) * mm});
            skLineSegment(sketch, "E233", {"start": v(-602.9, 418.6) * mm, "end": v(-604.54, 418.6) * mm});
            skLineSegment(sketch, "E234", {"start": v(-605.4, 419.47) * mm, "end": v(-605.4, 430.5) * mm});
            skLineSegment(sketch, "E235", {"start": v(-623.54, 430.5) * mm, "end": v(-605.4, 430.5) * mm});
            skLineSegment(sketch, "E236", {"start": v(-624.4, 431.37) * mm, "end": v(-624.4, 433) * mm});
            skLineSegment(sketch, "E237", {"start": v(-624.9, 433.5) * mm, "end": v(-643.9, 433.5) * mm});
            skLineSegment(sketch, "E238", {"start": v(-644.4, 433) * mm, "end": v(-644.4, 431.37) * mm});
            skLineSegment(sketch, "E239", {"start": v(-645.27, 430.5) * mm, "end": v(-648.26, 430.5) * mm});
            skLineSegment(sketch, "E240", {"start": v(-651.76, 430.5) * mm, "end": v(-659.9, 430.5) * mm});
            skLineSegment(sketch, "E241", {"start": v(-748.27, 45.7) * mm, "end": v(-749.9, 45.7) * mm});
            skLineSegment(sketch, "E242", {"start": v(-749.9, 25.3) * mm, "end": v(-748.27, 25.3) * mm});
            skLineSegment(sketch, "E243", {"start": v(-735.4, -5) * mm, "end": v(-717.4, -5) * mm});
            skCircle(sketch, "E244", {"center": v(-647.4, 371) * mm, "radius": 13 * mm});
            skCircle(sketch, "E245", {"center": v(-682.4, 29.5) * mm, "radius": 10 * mm});
            skCircle(sketch, "E246", {"center": v(-698.9, 223.3) * mm, "radius": 1.6 * mm});
            skCircle(sketch, "E247", {"center": v(-698.9, 132) * mm, "radius": 1.6 * mm});
            skCircle(sketch, "E248", {"center": v(-718.4, 120) * mm, "radius": 1.6 * mm});
            skCircle(sketch, "E249", {"center": v(-633.4, 120) * mm, "radius": 1.6 * mm});
            skCircle(sketch, "E250", {"center": v(-612.9, 132) * mm, "radius": 1.6 * mm});
            skCircle(sketch, "E251", {"center": v(-612.9, 223.3) * mm, "radius": 1.6 * mm});
            skCircle(sketch, "E252", {"center": v(-633.4, 246) * mm, "radius": 1.6 * mm});
            skCircle(sketch, "E253", {"center": v(-652.4, 340.5) * mm, "radius": 1.6 * mm});
            skLineSegment(sketch, "E254", {"start": v(-747.4, 57.1) * mm, "end": v(-750.4, 57.1) * mm});
            skLineSegment(sketch, "E255", {"start": v(-747.4, 18.05) * mm, "end": v(-747.4, 10) * mm});
            skLineSegment(sketch, "E256", {"start": v(-747.4, 24.43) * mm, "end": v(-747.4, 21.55) * mm});
            skLineSegment(sketch, "E257", {"start": v(-750.4, 25.8) * mm, "end": v(-750.4, 45.2) * mm});
            skLineSegment(sketch, "E258", {"start": v(-747.4, 52.95) * mm, "end": v(-747.4, 57.1) * mm});
            skLineSegment(sketch, "E259", {"start": v(-747.4, 49.45) * mm, "end": v(-747.4, 46.57) * mm});
            skLineSegment(sketch, "E260", {"start": v(-750.4, 57.1) * mm, "end": v(-750.4, 61.9) * mm});
            skLineSegment(sketch, "E261", {"start": v(-372.54, 12.65) * mm, "end": v(-370.9, 12.65) * mm});
            skLineSegment(sketch, "E262", {"start": v(-370.4, 13.15) * mm, "end": v(-370.4, 18.15) * mm});
            skLineSegment(sketch, "E263", {"start": v(-370.9, 18.65) * mm, "end": v(-372.54, 18.65) * mm});
            skLineSegment(sketch, "E264", {"start": v(-373.4, 19.52) * mm, "end": v(-373.4, 21.75) * mm});
            skLineSegment(sketch, "E265", {"start": v(-373.4, 25.25) * mm, "end": v(-373.4, 27.48) * mm});
            skLineSegment(sketch, "E266", {"start": v(-372.54, 28.35) * mm, "end": v(-370.9, 28.35) * mm});
            skLineSegment(sketch, "E267", {"start": v(-370.4, 28.85) * mm, "end": v(-370.4, 33.85) * mm});
            skLineSegment(sketch, "E268", {"start": v(-370.9, 34.35) * mm, "end": v(-372.54, 34.35) * mm});
            skLineSegment(sketch, "E269", {"start": v(-612.4, -5) * mm, "end": v(-633.2, -5) * mm});
            skLineSegment(sketch, "E270", {"start": v(-373.4, 37) * mm, "end": v(-373.4, 35.22) * mm});
            skLineSegment(sketch, "E271", {"start": v(-373.4, 11.78) * mm, "end": v(-373.4, 10) * mm});
            skLineSegment(sketch, "E272.0", {"start": v(-373.4, 37) * mm, "end": v(-545.4, 37) * mm});
            skLineSegment(sketch, "E273.0", {"start": v(-373.4, 10) * mm, "end": v(-414.9, 10) * mm});
            skLineSegment(sketch, "E274", {"start": v(-255.18, -5) * mm, "end": v(-274.17, -5) * mm});
            skLineSegment(sketch, "E275", {"start": v(-276.68, -2) * mm, "end": v(-308.18, -2) * mm});
            skLineSegment(sketch, "E276", {"start": v(-308.18, -2) * mm, "end": v(-308.18, 9.93) * mm});
            skLineSegment(sketch, "E277", {"start": v(-309.05, 10.8) * mm, "end": v(-310.68, 10.8) * mm});
            skLineSegment(sketch, "E278", {"start": v(-311.18, 11.3) * mm, "end": v(-311.18, 18.3) * mm});
            skLineSegment(sketch, "E279", {"start": v(-310.68, 18.8) * mm, "end": v(-309.05, 18.8) * mm});
            skLineSegment(sketch, "E280", {"start": v(-308.18, 19.67) * mm, "end": v(-308.18, 21.75) * mm});
            skLineSegment(sketch, "E281", {"start": v(-308.18, 25.25) * mm, "end": v(-308.18, 27.33) * mm});
            skLineSegment(sketch, "E282", {"start": v(-309.05, 28.2) * mm, "end": v(-310.68, 28.2) * mm});
            skLineSegment(sketch, "E283", {"start": v(-311.18, 28.7) * mm, "end": v(-311.18, 35.7) * mm});
            skLineSegment(sketch, "E284", {"start": v(-310.68, 36.2) * mm, "end": v(-309.05, 36.2) * mm});
            skLineSegment(sketch, "E285", {"start": v(-308.18, 37.07) * mm, "end": v(-308.18, 53) * mm});
            skLineSegment(sketch, "E286", {"start": v(-307.68, 53.5) * mm, "end": v(-298.45, 53.5) * mm});
            skLineSegment(sketch, "E287", {"start": v(-297.58, 54.37) * mm, "end": v(-297.58, 56) * mm});
            skLineSegment(sketch, "E288", {"start": v(-297.08, 56.5) * mm, "end": v(-288.28, 56.5) * mm});
            skLineSegment(sketch, "E289", {"start": v(-287.78, 56) * mm, "end": v(-287.78, 54.37) * mm});
            skLineSegment(sketch, "E290", {"start": v(-286.92, 53.5) * mm, "end": v(-284.68, 53.5) * mm});
            skLineSegment(sketch, "E291", {"start": v(-281.18, 53.5) * mm, "end": v(-278.95, 53.5) * mm});
            skLineSegment(sketch, "E292", {"start": v(-278.08, 54.37) * mm, "end": v(-278.08, 56) * mm});
            skLineSegment(sketch, "E293", {"start": v(-277.58, 56.5) * mm, "end": v(-268.78, 56.5) * mm});
            skLineSegment(sketch, "E294", {"start": v(-268.28, 56) * mm, "end": v(-268.28, 54.37) * mm});
            skLineSegment(sketch, "E295", {"start": v(-267.42, 53.5) * mm, "end": v(-253.18, 53.5) * mm});
            skLineSegment(sketch, "E296", {"start": v(-253.18, 53.5) * mm, "end": v(-253.18, -3) * mm});
            skArc(sketch, "E297", {"start": v(-255.18, -5) * mm, "mid": v(-253.77, -4.41) * mm, "end": v(-253.18, -3) * mm});
            skLineSegment(sketch, "E298", {"start": v(-602.4, 100.9) * mm, "end": v(-602.4, 7.5) * mm, "construction": true});
            skLineSegment(sketch, "E299", {"start": v(-601.55, 53.5) * mm, "end": v(-589.47, 53.5) * mm});
            skLineSegment(sketch, "E300", {"start": v(-588.6, 54.37) * mm, "end": v(-588.6, 56) * mm});
            skLineSegment(sketch, "E301", {"start": v(-588.1, 56.5) * mm, "end": v(-582.5, 56.5) * mm});
            skLineSegment(sketch, "E302", {"start": v(-582, 56) * mm, "end": v(-582, 54.37) * mm});
            skLineSegment(sketch, "E303", {"start": v(-581.14, 53.5) * mm, "end": v(-578.9, 53.5) * mm});
            skLineSegment(sketch, "E304", {"start": v(-575.4, 53.5) * mm, "end": v(-569.97, 53.5) * mm});
            skLineSegment(sketch, "E305", {"start": v(-569.1, 54.37) * mm, "end": v(-569.1, 56) * mm});
            skLineSegment(sketch, "E306", {"start": v(-568.6, 56.5) * mm, "end": v(-563, 56.5) * mm});
            skLineSegment(sketch, "E307", {"start": v(-562.5, 56) * mm, "end": v(-562.5, 54.36) * mm});
            skLineSegment(sketch, "E308", {"start": v(-561.64, 53.5) * mm, "end": v(-547.4, 53.5) * mm});
            skLineSegment(sketch, "E309", {"start": v(-602.4, 54.37) * mm, "end": v(-602.4, 56) * mm});
            skLineSegment(sketch, "E310", {"start": v(-602.9, 56.5) * mm, "end": v(-604.55, 56.5) * mm});
            skLineSegment(sketch, "E311", {"start": v(-547.4, 53.5) * mm, "end": v(-547.4, 39) * mm});
            skArc(sketch, "E312", {"start": v(-250.93, 161.3) * mm, "mid": v(-252.69, 165.54) * mm, "end": v(-256.93, 167.3) * mm});
            skLineSegment(sketch, "E313", {"start": v(-308.18, 167.3) * mm, "end": v(-256.93, 167.3) * mm});
            skLineSegment(sketch, "E314", {"start": v(-308.18, 148.27) * mm, "end": v(-308.18, 167.3) * mm});
            skLineSegment(sketch, "E315", {"start": v(-310.68, 147.4) * mm, "end": v(-309.05, 147.4) * mm});
            skLineSegment(sketch, "E316", {"start": v(-311.18, 138.1) * mm, "end": v(-311.18, 146.9) * mm});
            skLineSegment(sketch, "E317", {"start": v(-309.05, 137.6) * mm, "end": v(-310.68, 137.6) * mm});
            skLineSegment(sketch, "E318", {"start": v(-308.18, 130.55) * mm, "end": v(-308.18, 136.73) * mm});
            skLineSegment(sketch, "E319", {"start": v(-308.18, 120.87) * mm, "end": v(-308.18, 127.05) * mm});
            skLineSegment(sketch, "E320", {"start": v(-310.68, 120) * mm, "end": v(-309.05, 120) * mm});
            skLineSegment(sketch, "E321", {"start": v(-311.18, 110.7) * mm, "end": v(-311.18, 119.5) * mm});
            skLineSegment(sketch, "E322", {"start": v(-309.05, 110.2) * mm, "end": v(-310.68, 110.2) * mm});
            skLineSegment(sketch, "E323", {"start": v(-308.18, 83.5) * mm, "end": v(-252.93, 83.5) * mm});
            skLineSegment(sketch, "E324", {"start": v(-250.93, 161.3) * mm, "end": v(-250.93, 85.5) * mm});
            skCircle(sketch, "E325", {"center": v(-273.18, 128.8) * mm, "radius": 11.5 * mm});
            skCircle(sketch, "E326", {"center": v(-273.18, 150.8) * mm, "radius": 4.1 * mm});
            skCircle(sketch, "E327", {"center": v(-257.68, 144.3) * mm, "radius": 1.6 * mm});
            skCircle(sketch, "E328", {"center": v(-257.68, 113.3) * mm, "radius": 1.6 * mm});
            skCircle(sketch, "E329", {"center": v(-288.68, 144.3) * mm, "radius": 1.6 * mm});
            skCircle(sketch, "E330", {"center": v(-288.68, 113.3) * mm, "radius": 1.6 * mm});
            skLineSegment(sketch, "E331", {"start": v(-308.18, 83.5) * mm, "end": v(-308.18, 109.33) * mm});
            skLineSegment(sketch, "E332", {"start": v(-149.4, 55.73) * mm, "end": v(-149.4, 7.77) * mm});
            skLineSegment(sketch, "E333", {"start": v(-152.6, 55.73) * mm, "end": v(-152.6, 7.77) * mm});
            skLineSegment(sketch, "E334", {"start": v(-543.1, 9.13) * mm, "end": v(-543.1, 7.5) * mm});
            skLineSegment(sketch, "E335", {"start": v(-543.6, 7) * mm, "end": v(-552.4, 7) * mm});
            skLineSegment(sketch, "E336", {"start": v(-552.9, 7.5) * mm, "end": v(-552.9, 9.13) * mm});
            skLineSegment(sketch, "E337", {"start": v(-553.77, 10) * mm, "end": v(-556, 10) * mm});
            skLineSegment(sketch, "E338", {"start": v(-562.6, 9.13) * mm, "end": v(-562.6, 7.5) * mm});
            skLineSegment(sketch, "E339", {"start": v(-563.1, 7) * mm, "end": v(-571.9, 7) * mm});
            skLineSegment(sketch, "E340", {"start": v(-572.4, 7.5) * mm, "end": v(-572.4, 9.13) * mm});
            skLineSegment(sketch, "E341", {"start": v(-113.35, 9.13) * mm, "end": v(-113.35, 7.5) * mm});
            skLineSegment(sketch, "E342", {"start": v(-113.85, 7) * mm, "end": v(-122.65, 7) * mm});
            skLineSegment(sketch, "E343", {"start": v(-123.15, 7.5) * mm, "end": v(-123.15, 9.13) * mm});
            skLineSegment(sketch, "E344", {"start": v(-715.4, -3) * mm, "end": v(-715.4, 9.13) * mm});
            skLineSegment(sketch, "E345", {"start": v(-635.2, -3) * mm, "end": v(-635.2, 9.13) * mm});
            skLineSegment(sketch, "E346", {"start": v(-636.07, 10) * mm, "end": v(-638.3, 10) * mm});
            skLineSegment(sketch, "E347", {"start": v(-644.9, 9.13) * mm, "end": v(-644.9, 7.5) * mm});
            skLineSegment(sketch, "E348", {"start": v(-645.4, 7) * mm, "end": v(-654.2, 7) * mm});
            skLineSegment(sketch, "E349", {"start": v(-654.7, 7.5) * mm, "end": v(-654.7, 9.13) * mm});
            skLineSegment(sketch, "E350", {"start": v(-644.04, 10) * mm, "end": v(-641.8, 10) * mm});
            skLineSegment(sketch, "E351", {"start": v(-695.9, 9.13) * mm, "end": v(-695.9, 7.5) * mm});
            skLineSegment(sketch, "E352", {"start": v(-696.4, 7) * mm, "end": v(-705.2, 7) * mm});
            skLineSegment(sketch, "E353", {"start": v(-705.7, 7.5) * mm, "end": v(-705.7, 9.13) * mm});
            skLineSegment(sketch, "E354", {"start": v(-706.57, 10) * mm, "end": v(-708.8, 10) * mm});
            skLineSegment(sketch, "E355", {"start": v(-714.54, 10) * mm, "end": v(-712.3, 10) * mm});
            skLineSegment(sketch, "E356", {"start": v(-695.04, 10) * mm, "end": v(-655.57, 10) * mm});
            skLineSegment(sketch, "E357", {"start": v(-415.76, 9.13) * mm, "end": v(-415.76, 7.5) * mm});
            skLineSegment(sketch, "E358", {"start": v(-416.26, 7) * mm, "end": v(-425.06, 7) * mm});
            skLineSegment(sketch, "E359", {"start": v(-425.56, 7.5) * mm, "end": v(-425.56, 9.13) * mm});
            skLineSegment(sketch, "E360", {"start": v(-435.26, 9.13) * mm, "end": v(-435.26, 7.5) * mm});
            skLineSegment(sketch, "E361", {"start": v(-435.76, 7) * mm, "end": v(-444.56, 7) * mm});
            skLineSegment(sketch, "E362", {"start": v(-445.06, 7.5) * mm, "end": v(-445.06, 9.13) * mm});
            skLineSegment(sketch, "E363", {"start": v(-737.4, 9.13) * mm, "end": v(-737.4, -3) * mm});
            skLineSegment(sketch, "E364", {"start": v(-738.27, 10) * mm, "end": v(-747.4, 10) * mm});
            skPoint(sketch, "E365", {"position": v(-128, 22) * mm});
            skLineSegment(sketch, "E366", {"start": v(-28.35, 9.13) * mm, "end": v(-28.35, 7.5) * mm});
            skLineSegment(sketch, "E367", {"start": v(-28.85, 7) * mm, "end": v(-37.65, 7) * mm});
            skLineSegment(sketch, "E368", {"start": v(-38.15, 7.5) * mm, "end": v(-38.15, 9.13) * mm});
            skLineSegment(sketch, "E369", {"start": v(-46.98, 10) * mm, "end": v(-44.75, 10) * mm});
            skPoint(sketch, "E370", {"position": v(-43, 22) * mm});
            skLineSegment(sketch, "E371", {"start": v(-47.85, 9.13) * mm, "end": v(-47.85, 7.5) * mm});
            skLineSegment(sketch, "E372", {"start": v(-48.35, 7) * mm, "end": v(-57.15, 7) * mm});
            skLineSegment(sketch, "E373", {"start": v(-57.65, 7.5) * mm, "end": v(-57.65, 9.13) * mm});
            skLineSegment(sketch, "E374", {"start": v(57.65, 9.13) * mm, "end": v(57.65, 7.5) * mm});
            skLineSegment(sketch, "E375", {"start": v(57.15, 7) * mm, "end": v(48.35, 7) * mm});
            skLineSegment(sketch, "E376", {"start": v(47.85, 7.5) * mm, "end": v(47.85, 9.13) * mm});
            skLineSegment(sketch, "E377", {"start": v(46.98, 10) * mm, "end": v(44.75, 10) * mm});
            skPoint(sketch, "E378", {"position": v(43, 22) * mm});
            skLineSegment(sketch, "E379", {"start": v(38.15, 9.13) * mm, "end": v(38.15, 7.5) * mm});
            skLineSegment(sketch, "E380", {"start": v(37.65, 7) * mm, "end": v(28.85, 7) * mm});
            skLineSegment(sketch, "E381", {"start": v(28.35, 7.5) * mm, "end": v(28.35, 9.13) * mm});
            skArc(sketch, "E382", {"start": v(-150.27, 290.4) * mm, "mid": v(-150.02, 290.47) * mm, "end": v(-149.83, 290.65) * mm});
            skArc(sketch, "E383", {"start": v(-149.15, 289.97) * mm, "mid": v(-149.05, 290.75) * mm, "end": v(-149.83, 290.65) * mm});
            skArc(sketch, "E384", {"start": v(-149.15, 289.97) * mm, "mid": v(-149.33, 289.78) * mm, "end": v(-149.4, 289.53) * mm});
            skArc(sketch, "E385", {"start": v(-152.6, 289.53) * mm, "mid": v(-152.67, 289.78) * mm, "end": v(-152.85, 289.97) * mm});
            skArc(sketch, "E386", {"start": v(-152.17, 290.65) * mm, "mid": v(-152.95, 290.75) * mm, "end": v(-152.85, 289.97) * mm});
            skArc(sketch, "E387", {"start": v(-152.17, 290.65) * mm, "mid": v(-151.98, 290.47) * mm, "end": v(-151.73, 290.4) * mm});
            skArc(sketch, "E388", {"start": v(-149.4, 283.07) * mm, "mid": v(-149.33, 282.82) * mm, "end": v(-149.15, 282.63) * mm});
            skArc(sketch, "E389", {"start": v(-149.83, 281.95) * mm, "mid": v(-149.05, 281.85) * mm, "end": v(-149.15, 282.63) * mm});
            skArc(sketch, "E390", {"start": v(-149.83, 281.95) * mm, "mid": v(-150.02, 282.13) * mm, "end": v(-150.27, 282.2) * mm});
            skArc(sketch, "E391", {"start": v(-151.73, 282.2) * mm, "mid": v(-151.98, 282.13) * mm, "end": v(-152.17, 281.95) * mm});
            skArc(sketch, "E392", {"start": v(-152.85, 282.63) * mm, "mid": v(-152.95, 281.85) * mm, "end": v(-152.17, 281.95) * mm});
            skArc(sketch, "E393", {"start": v(-152.85, 282.63) * mm, "mid": v(-152.67, 282.82) * mm, "end": v(-152.6, 283.07) * mm});
            skLineSegment(sketch, "E394.bottom", {"start": v(-151.73, 309.2) * mm, "end": v(-150.27, 309.2) * mm});
            skLineSegment(sketch, "E394.top", {"start": v(-151.73, 301) * mm, "end": v(-150.27, 301) * mm});
            skLineSegment(sketch, "E394.left", {"start": v(-152.6, 308.33) * mm, "end": v(-152.6, 301.87) * mm});
            skLineSegment(sketch, "E394.right", {"start": v(-149.4, 308.33) * mm, "end": v(-149.4, 301.87) * mm});
            skArc(sketch, "E395", {"start": v(-150.27, 309.2) * mm, "mid": v(-150.02, 309.27) * mm, "end": v(-149.83, 309.45) * mm});
            skArc(sketch, "E396", {"start": v(-149.15, 308.77) * mm, "mid": v(-149.05, 309.55) * mm, "end": v(-149.83, 309.45) * mm});
            skArc(sketch, "E397", {"start": v(-149.15, 308.77) * mm, "mid": v(-149.33, 308.58) * mm, "end": v(-149.4, 308.33) * mm});
            skArc(sketch, "E398", {"start": v(-152.6, 308.33) * mm, "mid": v(-152.67, 308.58) * mm, "end": v(-152.85, 308.77) * mm});
            skArc(sketch, "E399", {"start": v(-152.17, 309.45) * mm, "mid": v(-152.95, 309.55) * mm, "end": v(-152.85, 308.77) * mm});
            skArc(sketch, "E400", {"start": v(-152.17, 309.45) * mm, "mid": v(-151.98, 309.27) * mm, "end": v(-151.73, 309.2) * mm});
            skArc(sketch, "E401", {"start": v(-149.4, 301.87) * mm, "mid": v(-149.33, 301.62) * mm, "end": v(-149.15, 301.43) * mm});
            skArc(sketch, "E402", {"start": v(-149.83, 300.75) * mm, "mid": v(-149.05, 300.65) * mm, "end": v(-149.15, 301.43) * mm});
            skArc(sketch, "E403", {"start": v(-149.83, 300.75) * mm, "mid": v(-150.02, 300.93) * mm, "end": v(-150.27, 301) * mm});
            skArc(sketch, "E404", {"start": v(-151.73, 301) * mm, "mid": v(-151.98, 300.93) * mm, "end": v(-152.17, 300.75) * mm});
            skArc(sketch, "E405", {"start": v(-152.85, 301.43) * mm, "mid": v(-152.95, 300.65) * mm, "end": v(-152.17, 300.75) * mm});
            skArc(sketch, "E406", {"start": v(-152.85, 301.43) * mm, "mid": v(-152.67, 301.62) * mm, "end": v(-152.6, 301.87) * mm});
            skCircle(sketch, "E407", {"center": v(-151, 205) * mm, "radius": 1.6 * mm});
            skLineSegment(sketch, "E408.bottom", {"start": v(-151.73, 199.7) * mm, "end": v(-150.27, 199.7) * mm});
            skLineSegment(sketch, "E408.top", {"start": v(-151.73, 191.5) * mm, "end": v(-150.27, 191.5) * mm});
            skLineSegment(sketch, "E408.left", {"start": v(-152.6, 198.83) * mm, "end": v(-152.6, 192.37) * mm});
            skLineSegment(sketch, "E408.right", {"start": v(-149.4, 198.83) * mm, "end": v(-149.4, 192.37) * mm});
            skArc(sketch, "E409", {"start": v(-150.27, 199.7) * mm, "mid": v(-150.02, 199.77) * mm, "end": v(-149.83, 199.95) * mm});
            skArc(sketch, "E410", {"start": v(-149.15, 199.27) * mm, "mid": v(-149.05, 200.05) * mm, "end": v(-149.83, 199.95) * mm});
            skArc(sketch, "E411", {"start": v(-149.15, 199.27) * mm, "mid": v(-149.33, 199.08) * mm, "end": v(-149.4, 198.83) * mm});
            skArc(sketch, "E412", {"start": v(-152.6, 198.83) * mm, "mid": v(-152.67, 199.08) * mm, "end": v(-152.85, 199.27) * mm});
            skArc(sketch, "E413", {"start": v(-152.17, 199.95) * mm, "mid": v(-152.95, 200.05) * mm, "end": v(-152.85, 199.27) * mm});
            skArc(sketch, "E414", {"start": v(-152.17, 199.95) * mm, "mid": v(-151.98, 199.77) * mm, "end": v(-151.73, 199.7) * mm});
            skArc(sketch, "E415", {"start": v(-149.4, 192.37) * mm, "mid": v(-149.33, 192.12) * mm, "end": v(-149.15, 191.93) * mm});
            skArc(sketch, "E416", {"start": v(-149.83, 191.25) * mm, "mid": v(-149.05, 191.15) * mm, "end": v(-149.15, 191.93) * mm});
            skArc(sketch, "E417", {"start": v(-149.83, 191.25) * mm, "mid": v(-150.02, 191.43) * mm, "end": v(-150.27, 191.5) * mm});
            skArc(sketch, "E418", {"start": v(-151.73, 191.5) * mm, "mid": v(-151.98, 191.43) * mm, "end": v(-152.17, 191.25) * mm});
            skArc(sketch, "E419", {"start": v(-152.85, 191.93) * mm, "mid": v(-152.95, 191.15) * mm, "end": v(-152.17, 191.25) * mm});
            skArc(sketch, "E420", {"start": v(-152.85, 191.93) * mm, "mid": v(-152.67, 192.12) * mm, "end": v(-152.6, 192.37) * mm});
            skLineSegment(sketch, "E421.bottom", {"start": v(-151.73, 218.5) * mm, "end": v(-150.27, 218.5) * mm});
            skLineSegment(sketch, "E421.top", {"start": v(-151.73, 210.3) * mm, "end": v(-150.27, 210.3) * mm});
            skLineSegment(sketch, "E421.left", {"start": v(-152.6, 217.63) * mm, "end": v(-152.6, 211.17) * mm});
            skLineSegment(sketch, "E421.right", {"start": v(-149.4, 217.63) * mm, "end": v(-149.4, 211.17) * mm});
            skArc(sketch, "E422", {"start": v(-150.27, 218.5) * mm, "mid": v(-150.02, 218.57) * mm, "end": v(-149.83, 218.75) * mm});
            skArc(sketch, "E423", {"start": v(-149.15, 218.07) * mm, "mid": v(-149.05, 218.85) * mm, "end": v(-149.83, 218.75) * mm});
            skArc(sketch, "E424", {"start": v(-149.15, 218.07) * mm, "mid": v(-149.33, 217.88) * mm, "end": v(-149.4, 217.63) * mm});
            skArc(sketch, "E425", {"start": v(-152.6, 217.63) * mm, "mid": v(-152.67, 217.88) * mm, "end": v(-152.85, 218.07) * mm});
            skArc(sketch, "E426", {"start": v(-152.17, 218.75) * mm, "mid": v(-152.95, 218.85) * mm, "end": v(-152.85, 218.07) * mm});
            skArc(sketch, "E427", {"start": v(-152.17, 218.75) * mm, "mid": v(-151.98, 218.57) * mm, "end": v(-151.73, 218.5) * mm});
            skArc(sketch, "E428", {"start": v(-149.4, 211.17) * mm, "mid": v(-149.33, 210.92) * mm, "end": v(-149.15, 210.73) * mm});
            skArc(sketch, "E429", {"start": v(-149.83, 210.05) * mm, "mid": v(-149.05, 209.95) * mm, "end": v(-149.15, 210.73) * mm});
            skArc(sketch, "E430", {"start": v(-149.83, 210.05) * mm, "mid": v(-150.02, 210.23) * mm, "end": v(-150.27, 210.3) * mm});
            skArc(sketch, "E431", {"start": v(-151.73, 210.3) * mm, "mid": v(-151.98, 210.23) * mm, "end": v(-152.17, 210.05) * mm});
            skArc(sketch, "E432", {"start": v(-152.85, 210.73) * mm, "mid": v(-152.95, 209.95) * mm, "end": v(-152.17, 210.05) * mm});
            skArc(sketch, "E433", {"start": v(-152.85, 210.73) * mm, "mid": v(-152.67, 210.92) * mm, "end": v(-152.6, 211.17) * mm});
            skCircle(sketch, "E434", {"center": v(-151, 114.3) * mm, "radius": 1.6 * mm});
            skLineSegment(sketch, "E435.bottom", {"start": v(-151.73, 109) * mm, "end": v(-150.27, 109) * mm});
            skLineSegment(sketch, "E435.top", {"start": v(-151.73, 100.8) * mm, "end": v(-150.27, 100.8) * mm});
            skLineSegment(sketch, "E435.left", {"start": v(-152.6, 108.13) * mm, "end": v(-152.6, 101.67) * mm});
            skLineSegment(sketch, "E435.right", {"start": v(-149.4, 108.13) * mm, "end": v(-149.4, 101.67) * mm});
            skArc(sketch, "E436", {"start": v(-150.27, 109) * mm, "mid": v(-150.02, 109.07) * mm, "end": v(-149.83, 109.25) * mm});
            skArc(sketch, "E437", {"start": v(-149.15, 108.57) * mm, "mid": v(-149.05, 109.35) * mm, "end": v(-149.83, 109.25) * mm});
            skArc(sketch, "E438", {"start": v(-149.15, 108.57) * mm, "mid": v(-149.33, 108.38) * mm, "end": v(-149.4, 108.13) * mm});
            skArc(sketch, "E439", {"start": v(-152.6, 108.13) * mm, "mid": v(-152.67, 108.38) * mm, "end": v(-152.85, 108.57) * mm});
            skArc(sketch, "E440", {"start": v(-152.17, 109.25) * mm, "mid": v(-152.95, 109.35) * mm, "end": v(-152.85, 108.57) * mm});
            skArc(sketch, "E441", {"start": v(-152.17, 109.25) * mm, "mid": v(-151.98, 109.07) * mm, "end": v(-151.73, 109) * mm});
            skArc(sketch, "E442", {"start": v(-149.4, 101.67) * mm, "mid": v(-149.33, 101.42) * mm, "end": v(-149.15, 101.23) * mm});
            skArc(sketch, "E443", {"start": v(-149.83, 100.55) * mm, "mid": v(-149.05, 100.45) * mm, "end": v(-149.15, 101.23) * mm});
            skArc(sketch, "E444", {"start": v(-149.83, 100.55) * mm, "mid": v(-150.02, 100.73) * mm, "end": v(-150.27, 100.8) * mm});
            skArc(sketch, "E445", {"start": v(-151.73, 100.8) * mm, "mid": v(-151.98, 100.73) * mm, "end": v(-152.17, 100.55) * mm});
            skArc(sketch, "E446", {"start": v(-152.85, 101.23) * mm, "mid": v(-152.95, 100.45) * mm, "end": v(-152.17, 100.55) * mm});
            skArc(sketch, "E447", {"start": v(-152.85, 101.23) * mm, "mid": v(-152.67, 101.42) * mm, "end": v(-152.6, 101.67) * mm});
            skLineSegment(sketch, "E448.bottom", {"start": v(-151.73, 127.8) * mm, "end": v(-150.27, 127.8) * mm});
            skLineSegment(sketch, "E448.top", {"start": v(-151.73, 119.6) * mm, "end": v(-150.27, 119.6) * mm});
            skLineSegment(sketch, "E448.left", {"start": v(-152.6, 126.93) * mm, "end": v(-152.6, 120.47) * mm});
            skLineSegment(sketch, "E448.right", {"start": v(-149.4, 126.93) * mm, "end": v(-149.4, 120.47) * mm});
            skArc(sketch, "E449", {"start": v(-150.27, 127.8) * mm, "mid": v(-150.02, 127.87) * mm, "end": v(-149.83, 128.05) * mm});
            skArc(sketch, "E450", {"start": v(-149.15, 127.37) * mm, "mid": v(-149.05, 128.15) * mm, "end": v(-149.83, 128.05) * mm});
            skArc(sketch, "E451", {"start": v(-149.15, 127.37) * mm, "mid": v(-149.33, 127.18) * mm, "end": v(-149.4, 126.93) * mm});
            skArc(sketch, "E452", {"start": v(-152.6, 126.93) * mm, "mid": v(-152.67, 127.18) * mm, "end": v(-152.85, 127.37) * mm});
            skArc(sketch, "E453", {"start": v(-152.17, 128.05) * mm, "mid": v(-152.95, 128.15) * mm, "end": v(-152.85, 127.37) * mm});
            skArc(sketch, "E454", {"start": v(-152.17, 128.05) * mm, "mid": v(-151.98, 127.87) * mm, "end": v(-151.73, 127.8) * mm});
            skArc(sketch, "E455", {"start": v(-149.4, 120.47) * mm, "mid": v(-149.33, 120.22) * mm, "end": v(-149.15, 120.03) * mm});
            skArc(sketch, "E456", {"start": v(-149.83, 119.35) * mm, "mid": v(-149.05, 119.25) * mm, "end": v(-149.15, 120.03) * mm});
            skArc(sketch, "E457", {"start": v(-149.83, 119.35) * mm, "mid": v(-150.02, 119.53) * mm, "end": v(-150.27, 119.6) * mm});
            skArc(sketch, "E458", {"start": v(-151.73, 119.6) * mm, "mid": v(-151.98, 119.53) * mm, "end": v(-152.17, 119.35) * mm});
            skArc(sketch, "E459", {"start": v(-152.85, 120.03) * mm, "mid": v(-152.95, 119.25) * mm, "end": v(-152.17, 119.35) * mm});
            skArc(sketch, "E460", {"start": v(-152.85, 120.03) * mm, "mid": v(-152.67, 120.22) * mm, "end": v(-152.6, 120.47) * mm});
            skCircle(sketch, "E461", {"center": v(151, 205) * mm, "radius": 1.6 * mm});
            skLineSegment(sketch, "E462.bottom", {"start": v(150.27, 199.7) * mm, "end": v(151.73, 199.7) * mm});
            skLineSegment(sketch, "E462.top", {"start": v(150.27, 191.5) * mm, "end": v(151.73, 191.5) * mm});
            skLineSegment(sketch, "E462.left", {"start": v(149.4, 198.83) * mm, "end": v(149.4, 192.37) * mm});
            skLineSegment(sketch, "E462.right", {"start": v(152.6, 198.83) * mm, "end": v(152.6, 192.37) * mm});
            skArc(sketch, "E463", {"start": v(151.73, 199.7) * mm, "mid": v(151.98, 199.77) * mm, "end": v(152.17, 199.95) * mm});
            skArc(sketch, "E464", {"start": v(152.85, 199.27) * mm, "mid": v(152.95, 200.05) * mm, "end": v(152.17, 199.95) * mm});
            skArc(sketch, "E465", {"start": v(152.85, 199.27) * mm, "mid": v(152.67, 199.08) * mm, "end": v(152.6, 198.83) * mm});
            skArc(sketch, "E466", {"start": v(149.4, 198.83) * mm, "mid": v(149.33, 199.08) * mm, "end": v(149.15, 199.27) * mm});
            skArc(sketch, "E467", {"start": v(149.83, 199.95) * mm, "mid": v(149.05, 200.05) * mm, "end": v(149.15, 199.27) * mm});
            skArc(sketch, "E468", {"start": v(149.83, 199.95) * mm, "mid": v(150.02, 199.77) * mm, "end": v(150.27, 199.7) * mm});
            skArc(sketch, "E469", {"start": v(152.6, 192.37) * mm, "mid": v(152.67, 192.12) * mm, "end": v(152.85, 191.93) * mm});
            skArc(sketch, "E470", {"start": v(152.17, 191.25) * mm, "mid": v(152.95, 191.15) * mm, "end": v(152.85, 191.93) * mm});
            skArc(sketch, "E471", {"start": v(152.17, 191.25) * mm, "mid": v(151.98, 191.43) * mm, "end": v(151.73, 191.5) * mm});
            skArc(sketch, "E472", {"start": v(150.27, 191.5) * mm, "mid": v(150.02, 191.43) * mm, "end": v(149.83, 191.25) * mm});
            skArc(sketch, "E473", {"start": v(149.15, 191.93) * mm, "mid": v(149.05, 191.15) * mm, "end": v(149.83, 191.25) * mm});
            skArc(sketch, "E474", {"start": v(149.15, 191.93) * mm, "mid": v(149.33, 192.12) * mm, "end": v(149.4, 192.37) * mm});
            skLineSegment(sketch, "E475.bottom", {"start": v(150.27, 218.5) * mm, "end": v(151.73, 218.5) * mm});
            skLineSegment(sketch, "E475.top", {"start": v(150.27, 210.3) * mm, "end": v(151.73, 210.3) * mm});
            skLineSegment(sketch, "E475.left", {"start": v(149.4, 217.63) * mm, "end": v(149.4, 211.17) * mm});
            skLineSegment(sketch, "E475.right", {"start": v(152.6, 217.63) * mm, "end": v(152.6, 211.17) * mm});
            skArc(sketch, "E476", {"start": v(151.73, 218.5) * mm, "mid": v(151.98, 218.57) * mm, "end": v(152.17, 218.75) * mm});
            skArc(sketch, "E477", {"start": v(152.85, 218.07) * mm, "mid": v(152.95, 218.85) * mm, "end": v(152.17, 218.75) * mm});
            skArc(sketch, "E478", {"start": v(152.85, 218.07) * mm, "mid": v(152.67, 217.88) * mm, "end": v(152.6, 217.63) * mm});
            skArc(sketch, "E479", {"start": v(149.4, 217.63) * mm, "mid": v(149.33, 217.88) * mm, "end": v(149.15, 218.07) * mm});
            skArc(sketch, "E480", {"start": v(149.83, 218.75) * mm, "mid": v(149.05, 218.85) * mm, "end": v(149.15, 218.07) * mm});
            skArc(sketch, "E481", {"start": v(149.83, 218.75) * mm, "mid": v(150.02, 218.57) * mm, "end": v(150.27, 218.5) * mm});
            skArc(sketch, "E482", {"start": v(152.6, 211.17) * mm, "mid": v(152.67, 210.92) * mm, "end": v(152.85, 210.73) * mm});
            skArc(sketch, "E483", {"start": v(152.17, 210.05) * mm, "mid": v(152.95, 209.95) * mm, "end": v(152.85, 210.73) * mm});
            skArc(sketch, "E484", {"start": v(152.17, 210.05) * mm, "mid": v(151.98, 210.23) * mm, "end": v(151.73, 210.3) * mm});
            skArc(sketch, "E485", {"start": v(150.27, 210.3) * mm, "mid": v(150.02, 210.23) * mm, "end": v(149.83, 210.05) * mm});
            skArc(sketch, "E486", {"start": v(149.15, 210.73) * mm, "mid": v(149.05, 209.95) * mm, "end": v(149.83, 210.05) * mm});
            skArc(sketch, "E487", {"start": v(149.15, 210.73) * mm, "mid": v(149.33, 210.92) * mm, "end": v(149.4, 211.17) * mm});
            skCircle(sketch, "E488", {"center": v(151, 295.7) * mm, "radius": 1.6 * mm});
            skLineSegment(sketch, "E489.bottom", {"start": v(150.27, 290.4) * mm, "end": v(151.73, 290.4) * mm});
            skLineSegment(sketch, "E489.top", {"start": v(150.27, 282.2) * mm, "end": v(151.73, 282.2) * mm});
            skLineSegment(sketch, "E489.left", {"start": v(149.4, 289.53) * mm, "end": v(149.4, 283.07) * mm});
            skLineSegment(sketch, "E489.right", {"start": v(152.6, 289.53) * mm, "end": v(152.6, 283.07) * mm});
            skArc(sketch, "E490", {"start": v(151.73, 290.4) * mm, "mid": v(151.98, 290.47) * mm, "end": v(152.17, 290.65) * mm});
            skArc(sketch, "E491", {"start": v(152.85, 289.97) * mm, "mid": v(152.95, 290.75) * mm, "end": v(152.17, 290.65) * mm});
            skArc(sketch, "E492", {"start": v(152.85, 289.97) * mm, "mid": v(152.67, 289.78) * mm, "end": v(152.6, 289.53) * mm});
            skArc(sketch, "E493", {"start": v(149.4, 289.53) * mm, "mid": v(149.33, 289.78) * mm, "end": v(149.15, 289.97) * mm});
            skArc(sketch, "E494", {"start": v(149.83, 290.65) * mm, "mid": v(149.05, 290.75) * mm, "end": v(149.15, 289.97) * mm});
            skArc(sketch, "E495", {"start": v(149.83, 290.65) * mm, "mid": v(150.02, 290.47) * mm, "end": v(150.27, 290.4) * mm});
            skArc(sketch, "E496", {"start": v(152.6, 283.07) * mm, "mid": v(152.67, 282.82) * mm, "end": v(152.85, 282.63) * mm});
            skArc(sketch, "E497", {"start": v(152.17, 281.95) * mm, "mid": v(152.95, 281.85) * mm, "end": v(152.85, 282.63) * mm});
            skArc(sketch, "E498", {"start": v(152.17, 281.95) * mm, "mid": v(151.98, 282.13) * mm, "end": v(151.73, 282.2) * mm});
            skArc(sketch, "E499", {"start": v(150.27, 282.2) * mm, "mid": v(150.02, 282.13) * mm, "end": v(149.83, 281.95) * mm});
            skArc(sketch, "E500", {"start": v(149.15, 282.63) * mm, "mid": v(149.05, 281.85) * mm, "end": v(149.83, 281.95) * mm});
            skArc(sketch, "E501", {"start": v(149.15, 282.63) * mm, "mid": v(149.33, 282.82) * mm, "end": v(149.4, 283.07) * mm});
            skLineSegment(sketch, "E502.bottom", {"start": v(150.27, 309.2) * mm, "end": v(151.73, 309.2) * mm});
            skLineSegment(sketch, "E502.top", {"start": v(150.27, 301) * mm, "end": v(151.73, 301) * mm});
            skLineSegment(sketch, "E502.left", {"start": v(149.4, 308.33) * mm, "end": v(149.4, 301.87) * mm});
            skLineSegment(sketch, "E502.right", {"start": v(152.6, 308.33) * mm, "end": v(152.6, 301.87) * mm});
            skArc(sketch, "E503", {"start": v(151.73, 309.2) * mm, "mid": v(151.98, 309.27) * mm, "end": v(152.17, 309.45) * mm});
            skArc(sketch, "E504", {"start": v(152.85, 308.77) * mm, "mid": v(152.95, 309.55) * mm, "end": v(152.17, 309.45) * mm});
            skArc(sketch, "E505", {"start": v(152.85, 308.77) * mm, "mid": v(152.67, 308.58) * mm, "end": v(152.6, 308.33) * mm});
            skArc(sketch, "E506", {"start": v(149.4, 308.33) * mm, "mid": v(149.33, 308.58) * mm, "end": v(149.15, 308.77) * mm});
            skArc(sketch, "E507", {"start": v(149.83, 309.45) * mm, "mid": v(149.05, 309.55) * mm, "end": v(149.15, 308.77) * mm});
            skArc(sketch, "E508", {"start": v(149.83, 309.45) * mm, "mid": v(150.02, 309.27) * mm, "end": v(150.27, 309.2) * mm});
            skArc(sketch, "E509", {"start": v(152.6, 301.87) * mm, "mid": v(152.67, 301.62) * mm, "end": v(152.85, 301.43) * mm});
            skArc(sketch, "E510", {"start": v(152.17, 300.75) * mm, "mid": v(152.95, 300.65) * mm, "end": v(152.85, 301.43) * mm});
            skArc(sketch, "E511", {"start": v(152.17, 300.75) * mm, "mid": v(151.98, 300.93) * mm, "end": v(151.73, 301) * mm});
            skArc(sketch, "E512", {"start": v(150.27, 301) * mm, "mid": v(150.02, 300.93) * mm, "end": v(149.83, 300.75) * mm});
            skArc(sketch, "E513", {"start": v(149.15, 301.43) * mm, "mid": v(149.05, 300.65) * mm, "end": v(149.83, 300.75) * mm});
            skArc(sketch, "E514", {"start": v(149.15, 301.43) * mm, "mid": v(149.33, 301.62) * mm, "end": v(149.4, 301.87) * mm});
            skCircle(sketch, "E515", {"center": v(151, 386.4) * mm, "radius": 1.6 * mm});
            skLineSegment(sketch, "E516.bottom", {"start": v(150.27, 381.1) * mm, "end": v(151.73, 381.1) * mm});
            skLineSegment(sketch, "E516.top", {"start": v(150.27, 372.9) * mm, "end": v(151.73, 372.9) * mm});
            skLineSegment(sketch, "E516.left", {"start": v(149.4, 380.23) * mm, "end": v(149.4, 373.77) * mm});
            skLineSegment(sketch, "E516.right", {"start": v(152.6, 380.23) * mm, "end": v(152.6, 373.77) * mm});
            skArc(sketch, "E517", {"start": v(151.73, 381.1) * mm, "mid": v(151.98, 381.17) * mm, "end": v(152.17, 381.35) * mm});
            skArc(sketch, "E518", {"start": v(152.85, 380.67) * mm, "mid": v(152.95, 381.45) * mm, "end": v(152.17, 381.35) * mm});
            skArc(sketch, "E519", {"start": v(152.85, 380.67) * mm, "mid": v(152.67, 380.48) * mm, "end": v(152.6, 380.23) * mm});
            skArc(sketch, "E520", {"start": v(149.4, 380.23) * mm, "mid": v(149.33, 380.48) * mm, "end": v(149.15, 380.67) * mm});
            skArc(sketch, "E521", {"start": v(149.83, 381.35) * mm, "mid": v(149.05, 381.45) * mm, "end": v(149.15, 380.67) * mm});
            skArc(sketch, "E522", {"start": v(149.83, 381.35) * mm, "mid": v(150.02, 381.17) * mm, "end": v(150.27, 381.1) * mm});
            skArc(sketch, "E523", {"start": v(152.6, 373.77) * mm, "mid": v(152.67, 373.52) * mm, "end": v(152.85, 373.33) * mm});
            skArc(sketch, "E524", {"start": v(152.17, 372.65) * mm, "mid": v(152.95, 372.55) * mm, "end": v(152.85, 373.33) * mm});
            skArc(sketch, "E525", {"start": v(152.17, 372.65) * mm, "mid": v(151.98, 372.83) * mm, "end": v(151.73, 372.9) * mm});
            skArc(sketch, "E526", {"start": v(150.27, 372.9) * mm, "mid": v(150.02, 372.83) * mm, "end": v(149.83, 372.65) * mm});
            skArc(sketch, "E527", {"start": v(149.15, 373.33) * mm, "mid": v(149.05, 372.55) * mm, "end": v(149.83, 372.65) * mm});
            skArc(sketch, "E528", {"start": v(149.15, 373.33) * mm, "mid": v(149.33, 373.52) * mm, "end": v(149.4, 373.77) * mm});
            skLineSegment(sketch, "E529.bottom", {"start": v(150.27, 399.9) * mm, "end": v(151.73, 399.9) * mm});
            skLineSegment(sketch, "E529.top", {"start": v(150.27, 391.7) * mm, "end": v(151.73, 391.7) * mm});
            skLineSegment(sketch, "E529.left", {"start": v(149.4, 399.03) * mm, "end": v(149.4, 392.57) * mm});
            skLineSegment(sketch, "E529.right", {"start": v(152.6, 399.03) * mm, "end": v(152.6, 392.57) * mm});
            skArc(sketch, "E530", {"start": v(151.73, 399.9) * mm, "mid": v(151.98, 399.97) * mm, "end": v(152.17, 400.15) * mm});
            skArc(sketch, "E531", {"start": v(152.85, 399.47) * mm, "mid": v(152.95, 400.25) * mm, "end": v(152.17, 400.15) * mm});
            skArc(sketch, "E532", {"start": v(152.85, 399.47) * mm, "mid": v(152.67, 399.28) * mm, "end": v(152.6, 399.03) * mm});
            skArc(sketch, "E533", {"start": v(149.4, 399.03) * mm, "mid": v(149.33, 399.28) * mm, "end": v(149.15, 399.47) * mm});
            skArc(sketch, "E534", {"start": v(149.83, 400.15) * mm, "mid": v(149.05, 400.25) * mm, "end": v(149.15, 399.47) * mm});
            skArc(sketch, "E535", {"start": v(149.83, 400.15) * mm, "mid": v(150.02, 399.97) * mm, "end": v(150.27, 399.9) * mm});
            skArc(sketch, "E536", {"start": v(152.6, 392.57) * mm, "mid": v(152.67, 392.32) * mm, "end": v(152.85, 392.13) * mm});
            skArc(sketch, "E537", {"start": v(152.17, 391.45) * mm, "mid": v(152.95, 391.35) * mm, "end": v(152.85, 392.13) * mm});
            skArc(sketch, "E538", {"start": v(152.17, 391.45) * mm, "mid": v(151.98, 391.63) * mm, "end": v(151.73, 391.7) * mm});
            skArc(sketch, "E539", {"start": v(150.27, 391.7) * mm, "mid": v(150.02, 391.63) * mm, "end": v(149.83, 391.45) * mm});
            skArc(sketch, "E540", {"start": v(149.15, 392.13) * mm, "mid": v(149.05, 391.35) * mm, "end": v(149.83, 391.45) * mm});
            skArc(sketch, "E541", {"start": v(149.15, 392.13) * mm, "mid": v(149.33, 392.32) * mm, "end": v(149.4, 392.57) * mm});
            skLineSegment(sketch, "E542.bottom", {"start": v(150.27, 418.7) * mm, "end": v(151.73, 418.7) * mm});
            skLineSegment(sketch, "E542.top", {"start": v(150.27, 410.5) * mm, "end": v(151.73, 410.5) * mm});
            skLineSegment(sketch, "E542.left", {"start": v(149.4, 417.83) * mm, "end": v(149.4, 411.37) * mm});
            skLineSegment(sketch, "E542.right", {"start": v(152.6, 417.83) * mm, "end": v(152.6, 411.37) * mm});
            skArc(sketch, "E543", {"start": v(151.73, 418.7) * mm, "mid": v(151.98, 418.77) * mm, "end": v(152.17, 418.95) * mm});
            skArc(sketch, "E544", {"start": v(152.85, 418.27) * mm, "mid": v(152.95, 419.05) * mm, "end": v(152.17, 418.95) * mm});
            skArc(sketch, "E545", {"start": v(152.85, 418.27) * mm, "mid": v(152.67, 418.08) * mm, "end": v(152.6, 417.83) * mm});
            skArc(sketch, "E546", {"start": v(149.4, 417.83) * mm, "mid": v(149.33, 418.08) * mm, "end": v(149.15, 418.27) * mm});
            skArc(sketch, "E547", {"start": v(149.83, 418.95) * mm, "mid": v(149.05, 419.05) * mm, "end": v(149.15, 418.27) * mm});
            skArc(sketch, "E548", {"start": v(149.83, 418.95) * mm, "mid": v(150.02, 418.77) * mm, "end": v(150.27, 418.7) * mm});
            skArc(sketch, "E549", {"start": v(152.6, 411.37) * mm, "mid": v(152.67, 411.12) * mm, "end": v(152.85, 410.93) * mm});
            skArc(sketch, "E550", {"start": v(152.17, 410.25) * mm, "mid": v(152.95, 410.15) * mm, "end": v(152.85, 410.93) * mm});
            skArc(sketch, "E551", {"start": v(152.17, 410.25) * mm, "mid": v(151.98, 410.43) * mm, "end": v(151.73, 410.5) * mm});
            skArc(sketch, "E552", {"start": v(150.27, 410.5) * mm, "mid": v(150.02, 410.43) * mm, "end": v(149.83, 410.25) * mm});
            skArc(sketch, "E553", {"start": v(149.15, 410.93) * mm, "mid": v(149.05, 410.15) * mm, "end": v(149.83, 410.25) * mm});
            skArc(sketch, "E554", {"start": v(149.15, 410.93) * mm, "mid": v(149.33, 411.12) * mm, "end": v(149.4, 411.37) * mm});
            skCircle(sketch, "E555", {"center": v(-151, 405.2) * mm, "radius": 1.6 * mm});
            skCircle(sketch, "E556", {"center": v(-151, 386.4) * mm, "radius": 1.6 * mm});
            skLineSegment(sketch, "E557.bottom", {"start": v(-151.73, 381.1) * mm, "end": v(-150.27, 381.1) * mm});
            skLineSegment(sketch, "E557.top", {"start": v(-151.73, 372.9) * mm, "end": v(-150.27, 372.9) * mm});
            skLineSegment(sketch, "E557.left", {"start": v(-152.6, 380.23) * mm, "end": v(-152.6, 373.77) * mm});
            skLineSegment(sketch, "E557.right", {"start": v(-149.4, 380.23) * mm, "end": v(-149.4, 373.77) * mm});
            skArc(sketch, "E558", {"start": v(-150.27, 381.1) * mm, "mid": v(-150.02, 381.17) * mm, "end": v(-149.83, 381.35) * mm});
            skArc(sketch, "E559", {"start": v(-149.15, 380.67) * mm, "mid": v(-149.05, 381.45) * mm, "end": v(-149.83, 381.35) * mm});
            skArc(sketch, "E560", {"start": v(-149.15, 380.67) * mm, "mid": v(-149.33, 380.48) * mm, "end": v(-149.4, 380.23) * mm});
            skArc(sketch, "E561", {"start": v(-152.6, 380.23) * mm, "mid": v(-152.67, 380.48) * mm, "end": v(-152.85, 380.67) * mm});
            skArc(sketch, "E562", {"start": v(-152.17, 381.35) * mm, "mid": v(-152.95, 381.45) * mm, "end": v(-152.85, 380.67) * mm});
            skArc(sketch, "E563", {"start": v(-152.17, 381.35) * mm, "mid": v(-151.98, 381.17) * mm, "end": v(-151.73, 381.1) * mm});
            skArc(sketch, "E564", {"start": v(-149.4, 373.77) * mm, "mid": v(-149.33, 373.52) * mm, "end": v(-149.15, 373.33) * mm});
            skArc(sketch, "E565", {"start": v(-149.83, 372.65) * mm, "mid": v(-149.05, 372.55) * mm, "end": v(-149.15, 373.33) * mm});
            skArc(sketch, "E566", {"start": v(-149.83, 372.65) * mm, "mid": v(-150.02, 372.83) * mm, "end": v(-150.27, 372.9) * mm});
            skArc(sketch, "E567", {"start": v(-151.73, 372.9) * mm, "mid": v(-151.98, 372.83) * mm, "end": v(-152.17, 372.65) * mm});
            skArc(sketch, "E568", {"start": v(-152.85, 373.33) * mm, "mid": v(-152.95, 372.55) * mm, "end": v(-152.17, 372.65) * mm});
            skArc(sketch, "E569", {"start": v(-152.85, 373.33) * mm, "mid": v(-152.67, 373.52) * mm, "end": v(-152.6, 373.77) * mm});
            skLineSegment(sketch, "E570.bottom", {"start": v(-151.73, 399.9) * mm, "end": v(-150.27, 399.9) * mm});
            skLineSegment(sketch, "E570.top", {"start": v(-151.73, 391.7) * mm, "end": v(-150.27, 391.7) * mm});
            skLineSegment(sketch, "E570.left", {"start": v(-152.6, 399.03) * mm, "end": v(-152.6, 392.57) * mm});
            skLineSegment(sketch, "E570.right", {"start": v(-149.4, 399.03) * mm, "end": v(-149.4, 392.57) * mm});
            skArc(sketch, "E571", {"start": v(-150.27, 399.9) * mm, "mid": v(-150.02, 399.97) * mm, "end": v(-149.83, 400.15) * mm});
            skArc(sketch, "E572", {"start": v(-149.15, 399.47) * mm, "mid": v(-149.05, 400.25) * mm, "end": v(-149.83, 400.15) * mm});
            skArc(sketch, "E573", {"start": v(-149.15, 399.47) * mm, "mid": v(-149.33, 399.28) * mm, "end": v(-149.4, 399.03) * mm});
            skArc(sketch, "E574", {"start": v(-152.6, 399.03) * mm, "mid": v(-152.67, 399.28) * mm, "end": v(-152.85, 399.47) * mm});
            skArc(sketch, "E575", {"start": v(-152.17, 400.15) * mm, "mid": v(-152.95, 400.25) * mm, "end": v(-152.85, 399.47) * mm});
            skArc(sketch, "E576", {"start": v(-152.17, 400.15) * mm, "mid": v(-151.98, 399.97) * mm, "end": v(-151.73, 399.9) * mm});
            skArc(sketch, "E577", {"start": v(-149.4, 392.57) * mm, "mid": v(-149.33, 392.32) * mm, "end": v(-149.15, 392.13) * mm});
            skArc(sketch, "E578", {"start": v(-149.83, 391.45) * mm, "mid": v(-149.05, 391.35) * mm, "end": v(-149.15, 392.13) * mm});
            skArc(sketch, "E579", {"start": v(-149.83, 391.45) * mm, "mid": v(-150.02, 391.63) * mm, "end": v(-150.27, 391.7) * mm});
            skArc(sketch, "E580", {"start": v(-151.73, 391.7) * mm, "mid": v(-151.98, 391.63) * mm, "end": v(-152.17, 391.45) * mm});
            skArc(sketch, "E581", {"start": v(-152.85, 392.13) * mm, "mid": v(-152.95, 391.35) * mm, "end": v(-152.17, 391.45) * mm});
            skArc(sketch, "E582", {"start": v(-152.85, 392.13) * mm, "mid": v(-152.67, 392.32) * mm, "end": v(-152.6, 392.57) * mm});
            skLineSegment(sketch, "E583.bottom", {"start": v(-151.73, 418.7) * mm, "end": v(-150.27, 418.7) * mm});
            skLineSegment(sketch, "E583.top", {"start": v(-151.73, 410.5) * mm, "end": v(-150.27, 410.5) * mm});
            skLineSegment(sketch, "E583.left", {"start": v(-152.6, 417.83) * mm, "end": v(-152.6, 411.37) * mm});
            skLineSegment(sketch, "E583.right", {"start": v(-149.4, 417.83) * mm, "end": v(-149.4, 411.37) * mm});
            skArc(sketch, "E584", {"start": v(-150.27, 418.7) * mm, "mid": v(-150.02, 418.77) * mm, "end": v(-149.83, 418.95) * mm});
            skArc(sketch, "E585", {"start": v(-149.15, 418.27) * mm, "mid": v(-149.05, 419.05) * mm, "end": v(-149.83, 418.95) * mm});
            skArc(sketch, "E586", {"start": v(-149.15, 418.27) * mm, "mid": v(-149.33, 418.08) * mm, "end": v(-149.4, 417.83) * mm});
            skArc(sketch, "E587", {"start": v(-152.6, 417.83) * mm, "mid": v(-152.67, 418.08) * mm, "end": v(-152.85, 418.27) * mm});
            skArc(sketch, "E588", {"start": v(-152.17, 418.95) * mm, "mid": v(-152.95, 419.05) * mm, "end": v(-152.85, 418.27) * mm});
            skArc(sketch, "E589", {"start": v(-152.17, 418.95) * mm, "mid": v(-151.98, 418.77) * mm, "end": v(-151.73, 418.7) * mm});
            skArc(sketch, "E590", {"start": v(-149.4, 411.37) * mm, "mid": v(-149.33, 411.12) * mm, "end": v(-149.15, 410.93) * mm});
            skArc(sketch, "E591", {"start": v(-149.83, 410.25) * mm, "mid": v(-149.05, 410.15) * mm, "end": v(-149.15, 410.93) * mm});
            skArc(sketch, "E592", {"start": v(-149.83, 410.25) * mm, "mid": v(-150.02, 410.43) * mm, "end": v(-150.27, 410.5) * mm});
            skArc(sketch, "E593", {"start": v(-151.73, 410.5) * mm, "mid": v(-151.98, 410.43) * mm, "end": v(-152.17, 410.25) * mm});
            skArc(sketch, "E594", {"start": v(-152.85, 410.93) * mm, "mid": v(-152.95, 410.15) * mm, "end": v(-152.17, 410.25) * mm});
            skArc(sketch, "E595", {"start": v(-152.85, 410.93) * mm, "mid": v(-152.67, 411.12) * mm, "end": v(-152.6, 411.37) * mm});
            skCircle(sketch, "E596", {"center": v(-221.4, 23.5) * mm, "radius": 1.6 * mm});
            skLineSegment(sketch, "E597.bottom", {"start": v(-222.13, 18.9) * mm, "end": v(-220.67, 18.9) * mm});
            skLineSegment(sketch, "E597.top", {"start": v(-222.13, 10.7) * mm, "end": v(-220.67, 10.7) * mm});
            skLineSegment(sketch, "E597.left", {"start": v(-223, 18.03) * mm, "end": v(-223, 11.57) * mm});
            skLineSegment(sketch, "E597.right", {"start": v(-219.8, 18.03) * mm, "end": v(-219.8, 11.57) * mm});
            skArc(sketch, "E598", {"start": v(-220.67, 18.9) * mm, "mid": v(-220.42, 18.97) * mm, "end": v(-220.23, 19.15) * mm});
            skArc(sketch, "E599", {"start": v(-219.55, 18.47) * mm, "mid": v(-219.45, 19.25) * mm, "end": v(-220.23, 19.15) * mm});
            skArc(sketch, "E600", {"start": v(-219.55, 18.47) * mm, "mid": v(-219.73, 18.28) * mm, "end": v(-219.8, 18.03) * mm});
            skArc(sketch, "E601", {"start": v(-223, 18.03) * mm, "mid": v(-223.07, 18.28) * mm, "end": v(-223.25, 18.47) * mm});
            skArc(sketch, "E602", {"start": v(-222.57, 19.15) * mm, "mid": v(-223.35, 19.25) * mm, "end": v(-223.25, 18.47) * mm});
            skArc(sketch, "E603", {"start": v(-222.57, 19.15) * mm, "mid": v(-222.38, 18.97) * mm, "end": v(-222.13, 18.9) * mm});
            skArc(sketch, "E604", {"start": v(-219.8, 11.57) * mm, "mid": v(-219.73, 11.32) * mm, "end": v(-219.55, 11.13) * mm});
            skArc(sketch, "E605", {"start": v(-220.23, 10.45) * mm, "mid": v(-219.45, 10.35) * mm, "end": v(-219.55, 11.13) * mm});
            skArc(sketch, "E606", {"start": v(-220.23, 10.45) * mm, "mid": v(-220.42, 10.63) * mm, "end": v(-220.67, 10.7) * mm});
            skArc(sketch, "E607", {"start": v(-222.13, 10.7) * mm, "mid": v(-222.38, 10.63) * mm, "end": v(-222.57, 10.45) * mm});
            skArc(sketch, "E608", {"start": v(-223.25, 11.13) * mm, "mid": v(-223.35, 10.35) * mm, "end": v(-222.57, 10.45) * mm});
            skArc(sketch, "E609", {"start": v(-223.25, 11.13) * mm, "mid": v(-223.07, 11.32) * mm, "end": v(-223, 11.57) * mm});
            skLineSegment(sketch, "E610.bottom", {"start": v(-222.13, 36.3) * mm, "end": v(-220.67, 36.3) * mm});
            skLineSegment(sketch, "E610.top", {"start": v(-222.13, 28.1) * mm, "end": v(-220.67, 28.1) * mm});
            skLineSegment(sketch, "E610.left", {"start": v(-223, 35.58) * mm, "end": v(-223, 28.97) * mm});
            skLineSegment(sketch, "E610.right", {"start": v(-219.8, 35.58) * mm, "end": v(-219.8, 28.97) * mm});
            skArc(sketch, "E611", {"start": v(-220.67, 36.3) * mm, "mid": v(-220.42, 36.37) * mm, "end": v(-220.23, 36.55) * mm});
            skArc(sketch, "E612", {"start": v(-219.55, 35.87) * mm, "mid": v(-219.45, 36.65) * mm, "end": v(-220.23, 36.55) * mm});
            skArc(sketch, "E613", {"start": v(-219.55, 35.87) * mm, "mid": v(-219.73, 35.68) * mm, "end": v(-219.8, 35.43) * mm});
            skArc(sketch, "E614", {"start": v(-223, 35.43) * mm, "mid": v(-223.07, 35.68) * mm, "end": v(-223.25, 35.87) * mm});
            skArc(sketch, "E615", {"start": v(-222.57, 36.55) * mm, "mid": v(-223.35, 36.65) * mm, "end": v(-223.25, 35.87) * mm});
            skArc(sketch, "E616", {"start": v(-222.57, 36.55) * mm, "mid": v(-222.38, 36.37) * mm, "end": v(-222.13, 36.3) * mm});
            skArc(sketch, "E617", {"start": v(-219.8, 28.97) * mm, "mid": v(-219.73, 28.72) * mm, "end": v(-219.55, 28.53) * mm});
            skArc(sketch, "E618", {"start": v(-220.23, 27.85) * mm, "mid": v(-219.45, 27.75) * mm, "end": v(-219.55, 28.53) * mm});
            skArc(sketch, "E619", {"start": v(-220.23, 27.85) * mm, "mid": v(-220.42, 28.03) * mm, "end": v(-220.67, 28.1) * mm});
            skArc(sketch, "E620", {"start": v(-222.13, 28.1) * mm, "mid": v(-222.38, 28.03) * mm, "end": v(-222.57, 27.85) * mm});
            skArc(sketch, "E621", {"start": v(-223.25, 28.53) * mm, "mid": v(-223.35, 27.75) * mm, "end": v(-222.57, 27.85) * mm});
            skArc(sketch, "E622", {"start": v(-223.25, 28.53) * mm, "mid": v(-223.07, 28.72) * mm, "end": v(-223, 28.97) * mm});
            skCircle(sketch, "E623", {"center": v(151, 95.5) * mm, "radius": 1.6 * mm});
            skCircle(sketch, "E624", {"center": v(151, 114.3) * mm, "radius": 1.6 * mm});
            skLineSegment(sketch, "E625.bottom", {"start": v(150.27, 109) * mm, "end": v(151.73, 109) * mm});
            skLineSegment(sketch, "E625.top", {"start": v(150.27, 100.8) * mm, "end": v(151.73, 100.8) * mm});
            skLineSegment(sketch, "E625.left", {"start": v(149.4, 108.13) * mm, "end": v(149.4, 101.67) * mm});
            skLineSegment(sketch, "E625.right", {"start": v(152.6, 108.13) * mm, "end": v(152.6, 101.67) * mm});
            skArc(sketch, "E626", {"start": v(151.73, 109) * mm, "mid": v(151.98, 109.07) * mm, "end": v(152.17, 109.25) * mm});
            skArc(sketch, "E627", {"start": v(152.85, 108.57) * mm, "mid": v(152.95, 109.35) * mm, "end": v(152.17, 109.25) * mm});
            skArc(sketch, "E628", {"start": v(152.85, 108.57) * mm, "mid": v(152.67, 108.38) * mm, "end": v(152.6, 108.13) * mm});
            skArc(sketch, "E629", {"start": v(149.4, 108.13) * mm, "mid": v(149.33, 108.38) * mm, "end": v(149.15, 108.57) * mm});
            skArc(sketch, "E630", {"start": v(149.83, 109.25) * mm, "mid": v(149.05, 109.35) * mm, "end": v(149.15, 108.57) * mm});
            skArc(sketch, "E631", {"start": v(149.83, 109.25) * mm, "mid": v(150.02, 109.07) * mm, "end": v(150.27, 109) * mm});
            skArc(sketch, "E632", {"start": v(152.6, 101.67) * mm, "mid": v(152.67, 101.42) * mm, "end": v(152.85, 101.23) * mm});
            skArc(sketch, "E633", {"start": v(152.17, 100.55) * mm, "mid": v(152.95, 100.45) * mm, "end": v(152.85, 101.23) * mm});
            skArc(sketch, "E634", {"start": v(152.17, 100.55) * mm, "mid": v(151.98, 100.73) * mm, "end": v(151.73, 100.8) * mm});
            skArc(sketch, "E635", {"start": v(150.27, 100.8) * mm, "mid": v(150.02, 100.73) * mm, "end": v(149.83, 100.55) * mm});
            skArc(sketch, "E636", {"start": v(149.15, 101.23) * mm, "mid": v(149.05, 100.45) * mm, "end": v(149.83, 100.55) * mm});
            skArc(sketch, "E637", {"start": v(149.15, 101.23) * mm, "mid": v(149.33, 101.42) * mm, "end": v(149.4, 101.67) * mm});
            skLineSegment(sketch, "E638.bottom", {"start": v(150.27, 127.8) * mm, "end": v(151.73, 127.8) * mm});
            skLineSegment(sketch, "E638.top", {"start": v(150.27, 119.6) * mm, "end": v(151.73, 119.6) * mm});
            skLineSegment(sketch, "E638.left", {"start": v(149.4, 126.93) * mm, "end": v(149.4, 120.47) * mm});
            skLineSegment(sketch, "E638.right", {"start": v(152.6, 126.93) * mm, "end": v(152.6, 120.47) * mm});
            skArc(sketch, "E639", {"start": v(151.73, 127.8) * mm, "mid": v(151.98, 127.87) * mm, "end": v(152.17, 128.05) * mm});
            skArc(sketch, "E640", {"start": v(152.85, 127.37) * mm, "mid": v(152.95, 128.15) * mm, "end": v(152.17, 128.05) * mm});
            skArc(sketch, "E641", {"start": v(152.85, 127.37) * mm, "mid": v(152.67, 127.18) * mm, "end": v(152.6, 126.93) * mm});
            skArc(sketch, "E642", {"start": v(149.4, 126.93) * mm, "mid": v(149.33, 127.18) * mm, "end": v(149.15, 127.37) * mm});
            skArc(sketch, "E643", {"start": v(149.83, 128.05) * mm, "mid": v(149.05, 128.15) * mm, "end": v(149.15, 127.37) * mm});
            skArc(sketch, "E644", {"start": v(149.83, 128.05) * mm, "mid": v(150.02, 127.87) * mm, "end": v(150.27, 127.8) * mm});
            skArc(sketch, "E645", {"start": v(152.6, 120.47) * mm, "mid": v(152.67, 120.22) * mm, "end": v(152.85, 120.03) * mm});
            skArc(sketch, "E646", {"start": v(152.17, 119.35) * mm, "mid": v(152.95, 119.25) * mm, "end": v(152.85, 120.03) * mm});
            skArc(sketch, "E647", {"start": v(152.17, 119.35) * mm, "mid": v(151.98, 119.53) * mm, "end": v(151.73, 119.6) * mm});
            skArc(sketch, "E648", {"start": v(150.27, 119.6) * mm, "mid": v(150.02, 119.53) * mm, "end": v(149.83, 119.35) * mm});
            skArc(sketch, "E649", {"start": v(149.15, 120.03) * mm, "mid": v(149.05, 119.25) * mm, "end": v(149.83, 119.35) * mm});
            skArc(sketch, "E650", {"start": v(149.15, 120.03) * mm, "mid": v(149.33, 120.22) * mm, "end": v(149.4, 120.47) * mm});
            skLineSegment(sketch, "E651.trimOffspring", {"start": v(-129.75, 10) * mm, "end": v(-133.28, 10) * mm});
            skLineSegment(sketch, "E652.trimOffspring", {"start": v(-124.02, 10) * mm, "end": v(-126.25, 10) * mm});
            skLineSegment(sketch, "E653.trimOffspring", {"start": v(-58.52, 10) * mm, "end": v(-112.48, 10) * mm});
            skLineSegment(sketch, "E654.trimOffspring", {"start": v(-39.02, 10) * mm, "end": v(-41.25, 10) * mm});
            skLineSegment(sketch, "E655.trimOffspring", {"start": v(27.48, 10) * mm, "end": v(5.37, 10) * mm});
            skLineSegment(sketch, "E656.trimOffspring", {"start": v(41.25, 10) * mm, "end": v(39.02, 10) * mm});
            skCircle(sketch, "E657", {"center": v(-189, 55) * mm, "radius": 1.6 * mm});
            skLineSegment(sketch, "E658.bottom", {"start": v(-180.3, 54.27) * mm, "end": v(-180.3, 55.73) * mm});
            skLineSegment(sketch, "E658.top", {"start": v(-170.3, 54.27) * mm, "end": v(-170.3, 55.73) * mm});
            skLineSegment(sketch, "E658.left", {"start": v(-179.43, 53.4) * mm, "end": v(-171.17, 53.4) * mm});
            skLineSegment(sketch, "E658.right", {"start": v(-179.43, 56.6) * mm, "end": v(-171.17, 56.6) * mm});
            skArc(sketch, "E659", {"start": v(-180.3, 55.73) * mm, "mid": v(-180.37, 55.98) * mm, "end": v(-180.55, 56.17) * mm});
            skArc(sketch, "E660", {"start": v(-179.87, 56.85) * mm, "mid": v(-180.65, 56.95) * mm, "end": v(-180.55, 56.17) * mm});
            skArc(sketch, "E661", {"start": v(-179.87, 56.85) * mm, "mid": v(-179.68, 56.67) * mm, "end": v(-179.43, 56.6) * mm});
            skArc(sketch, "E662", {"start": v(-179.43, 53.4) * mm, "mid": v(-179.68, 53.33) * mm, "end": v(-179.87, 53.15) * mm});
            skArc(sketch, "E663", {"start": v(-180.55, 53.83) * mm, "mid": v(-180.65, 53.05) * mm, "end": v(-179.87, 53.15) * mm});
            skArc(sketch, "E664", {"start": v(-180.55, 53.83) * mm, "mid": v(-180.37, 54.02) * mm, "end": v(-180.3, 54.27) * mm});
            skArc(sketch, "E665", {"start": v(-171.17, 56.6) * mm, "mid": v(-170.92, 56.67) * mm, "end": v(-170.73, 56.85) * mm});
            skArc(sketch, "E666", {"start": v(-170.05, 56.17) * mm, "mid": v(-169.95, 56.95) * mm, "end": v(-170.73, 56.85) * mm});
            skArc(sketch, "E667", {"start": v(-170.05, 56.17) * mm, "mid": v(-170.23, 55.98) * mm, "end": v(-170.3, 55.73) * mm});
            skArc(sketch, "E668", {"start": v(-170.3, 54.27) * mm, "mid": v(-170.23, 54.02) * mm, "end": v(-170.05, 53.83) * mm});
            skArc(sketch, "E669", {"start": v(-170.73, 53.15) * mm, "mid": v(-169.95, 53.05) * mm, "end": v(-170.05, 53.83) * mm});
            skArc(sketch, "E670", {"start": v(-170.73, 53.15) * mm, "mid": v(-170.92, 53.33) * mm, "end": v(-171.17, 53.4) * mm});
            skLineSegment(sketch, "E671.bottom", {"start": v(-207.7, 54.27) * mm, "end": v(-207.7, 55.73) * mm});
            skLineSegment(sketch, "E671.top", {"start": v(-197.7, 54.27) * mm, "end": v(-197.7, 55.73) * mm});
            skLineSegment(sketch, "E671.left", {"start": v(-206.83, 53.4) * mm, "end": v(-198.57, 53.4) * mm});
            skLineSegment(sketch, "E671.right", {"start": v(-206.83, 56.6) * mm, "end": v(-198.57, 56.6) * mm});
            skArc(sketch, "E672", {"start": v(-207.7, 55.73) * mm, "mid": v(-207.77, 55.98) * mm, "end": v(-207.95, 56.17) * mm});
            skArc(sketch, "E673", {"start": v(-207.27, 56.85) * mm, "mid": v(-208.05, 56.95) * mm, "end": v(-207.95, 56.17) * mm});
            skArc(sketch, "E674", {"start": v(-207.27, 56.85) * mm, "mid": v(-207.08, 56.67) * mm, "end": v(-206.83, 56.6) * mm});
            skArc(sketch, "E675", {"start": v(-206.83, 53.4) * mm, "mid": v(-207.08, 53.33) * mm, "end": v(-207.27, 53.15) * mm});
            skArc(sketch, "E676", {"start": v(-207.95, 53.83) * mm, "mid": v(-208.05, 53.05) * mm, "end": v(-207.27, 53.15) * mm});
            skArc(sketch, "E677", {"start": v(-207.95, 53.83) * mm, "mid": v(-207.77, 54.02) * mm, "end": v(-207.7, 54.27) * mm});
            skArc(sketch, "E678", {"start": v(-198.57, 56.6) * mm, "mid": v(-198.32, 56.67) * mm, "end": v(-198.13, 56.85) * mm});
            skArc(sketch, "E679", {"start": v(-197.45, 56.17) * mm, "mid": v(-197.35, 56.95) * mm, "end": v(-198.13, 56.85) * mm});
            skArc(sketch, "E680", {"start": v(-197.45, 56.17) * mm, "mid": v(-197.63, 55.98) * mm, "end": v(-197.7, 55.73) * mm});
            skArc(sketch, "E681", {"start": v(-197.7, 54.27) * mm, "mid": v(-197.63, 54.02) * mm, "end": v(-197.45, 53.83) * mm});
            skArc(sketch, "E682", {"start": v(-198.13, 53.15) * mm, "mid": v(-197.35, 53.05) * mm, "end": v(-197.45, 53.83) * mm});
            skArc(sketch, "E683", {"start": v(-198.13, 53.15) * mm, "mid": v(-198.32, 53.33) * mm, "end": v(-198.57, 53.4) * mm});
            skPoint(sketch, "E684", {"position": v(-221.4, 28.1) * mm});
            skLineSegment(sketch, "E685", {"start": v(-221.4, 28.25) * mm, "end": v(-221.4, 20.71) * mm, "construction": true});
            skCircle(sketch, "E686", {"center": v(189, 55) * mm, "radius": 1.6 * mm});
            skCircle(sketch, "E687", {"center": v(221.4, 23.5) * mm, "radius": 1.6 * mm});
            skLineSegment(sketch, "E688.bottom", {"start": v(220.67, 18.9) * mm, "end": v(222.13, 18.9) * mm});
            skLineSegment(sketch, "E688.top", {"start": v(220.67, 10.7) * mm, "end": v(222.13, 10.7) * mm});
            skLineSegment(sketch, "E688.left", {"start": v(219.8, 18.03) * mm, "end": v(219.8, 11.57) * mm});
            skLineSegment(sketch, "E688.right", {"start": v(223, 18.03) * mm, "end": v(223, 11.57) * mm});
            skArc(sketch, "E689", {"start": v(222.13, 18.9) * mm, "mid": v(222.38, 18.97) * mm, "end": v(222.57, 19.15) * mm});
            skArc(sketch, "E690", {"start": v(223.25, 18.47) * mm, "mid": v(223.35, 19.25) * mm, "end": v(222.57, 19.15) * mm});
            skArc(sketch, "E691", {"start": v(223.25, 18.47) * mm, "mid": v(223.07, 18.28) * mm, "end": v(223, 18.03) * mm});
            skArc(sketch, "E692", {"start": v(219.8, 18.03) * mm, "mid": v(219.73, 18.28) * mm, "end": v(219.55, 18.47) * mm});
            skArc(sketch, "E693", {"start": v(220.23, 19.15) * mm, "mid": v(219.45, 19.25) * mm, "end": v(219.55, 18.47) * mm});
            skArc(sketch, "E694", {"start": v(220.23, 19.15) * mm, "mid": v(220.42, 18.97) * mm, "end": v(220.67, 18.9) * mm});
            skArc(sketch, "E695", {"start": v(223, 11.57) * mm, "mid": v(223.07, 11.32) * mm, "end": v(223.25, 11.13) * mm});
            skArc(sketch, "E696", {"start": v(222.57, 10.45) * mm, "mid": v(223.35, 10.35) * mm, "end": v(223.25, 11.13) * mm});
            skArc(sketch, "E697", {"start": v(222.57, 10.45) * mm, "mid": v(222.38, 10.63) * mm, "end": v(222.13, 10.7) * mm});
            skArc(sketch, "E698", {"start": v(220.67, 10.7) * mm, "mid": v(220.42, 10.63) * mm, "end": v(220.23, 10.45) * mm});
            skArc(sketch, "E699", {"start": v(219.55, 11.13) * mm, "mid": v(219.45, 10.35) * mm, "end": v(220.23, 10.45) * mm});
            skArc(sketch, "E700", {"start": v(219.55, 11.13) * mm, "mid": v(219.73, 11.32) * mm, "end": v(219.8, 11.57) * mm});
            skLineSegment(sketch, "E701.bottom", {"start": v(220.67, 36.3) * mm, "end": v(222.13, 36.3) * mm});
            skLineSegment(sketch, "E701.top", {"start": v(220.67, 28.1) * mm, "end": v(222.13, 28.1) * mm});
            skLineSegment(sketch, "E701.left", {"start": v(219.8, 35.58) * mm, "end": v(219.8, 28.97) * mm});
            skLineSegment(sketch, "E701.right", {"start": v(223, 35.58) * mm, "end": v(223, 28.97) * mm});
            skArc(sketch, "E702", {"start": v(222.13, 36.3) * mm, "mid": v(222.38, 36.37) * mm, "end": v(222.57, 36.55) * mm});
            skArc(sketch, "E703", {"start": v(223.25, 35.87) * mm, "mid": v(223.35, 36.65) * mm, "end": v(222.57, 36.55) * mm});
            skArc(sketch, "E704", {"start": v(223.25, 35.87) * mm, "mid": v(223.07, 35.68) * mm, "end": v(223, 35.43) * mm});
            skArc(sketch, "E705", {"start": v(219.8, 35.43) * mm, "mid": v(219.73, 35.68) * mm, "end": v(219.55, 35.87) * mm});
            skArc(sketch, "E706", {"start": v(220.23, 36.55) * mm, "mid": v(219.45, 36.65) * mm, "end": v(219.55, 35.87) * mm});
            skArc(sketch, "E707", {"start": v(220.23, 36.55) * mm, "mid": v(220.42, 36.37) * mm, "end": v(220.67, 36.3) * mm});
            skArc(sketch, "E708", {"start": v(223, 28.97) * mm, "mid": v(223.07, 28.72) * mm, "end": v(223.25, 28.53) * mm});
            skArc(sketch, "E709", {"start": v(222.57, 27.85) * mm, "mid": v(223.35, 27.75) * mm, "end": v(223.25, 28.53) * mm});
            skArc(sketch, "E710", {"start": v(222.57, 27.85) * mm, "mid": v(222.38, 28.03) * mm, "end": v(222.13, 28.1) * mm});
            skArc(sketch, "E711", {"start": v(220.67, 28.1) * mm, "mid": v(220.42, 28.03) * mm, "end": v(220.23, 27.85) * mm});
            skArc(sketch, "E712", {"start": v(219.55, 28.53) * mm, "mid": v(219.45, 27.75) * mm, "end": v(220.23, 27.85) * mm});
            skArc(sketch, "E713", {"start": v(219.55, 28.53) * mm, "mid": v(219.73, 28.72) * mm, "end": v(219.8, 28.97) * mm});
            skCircle(sketch, "E714", {"center": v(-282.93, 90.8) * mm, "radius": 1.6 * mm});
            skLineSegment(sketch, "E715.bottom", {"start": v(-287.68, 91.53) * mm, "end": v(-287.68, 90.07) * mm});
            skLineSegment(sketch, "E715.top", {"start": v(-297.68, 91.53) * mm, "end": v(-297.68, 90.07) * mm});
            skLineSegment(sketch, "E715.left", {"start": v(-288.55, 92.4) * mm, "end": v(-296.82, 92.4) * mm});
            skLineSegment(sketch, "E715.right", {"start": v(-288.55, 89.2) * mm, "end": v(-296.82, 89.2) * mm});
            skArc(sketch, "E716", {"start": v(-287.68, 90.07) * mm, "mid": v(-287.62, 89.82) * mm, "end": v(-287.43, 89.63) * mm});
            skArc(sketch, "E717", {"start": v(-288.12, 88.95) * mm, "mid": v(-287.33, 88.85) * mm, "end": v(-287.43, 89.63) * mm});
            skArc(sketch, "E718", {"start": v(-288.12, 88.95) * mm, "mid": v(-288.3, 89.13) * mm, "end": v(-288.55, 89.2) * mm});
            skArc(sketch, "E719", {"start": v(-288.55, 92.4) * mm, "mid": v(-288.3, 92.47) * mm, "end": v(-288.12, 92.65) * mm});
            skArc(sketch, "E720", {"start": v(-287.43, 91.97) * mm, "mid": v(-287.33, 92.75) * mm, "end": v(-288.12, 92.65) * mm});
            skArc(sketch, "E721", {"start": v(-287.43, 91.97) * mm, "mid": v(-287.62, 91.78) * mm, "end": v(-287.68, 91.53) * mm});
            skArc(sketch, "E722", {"start": v(-296.82, 89.2) * mm, "mid": v(-297.07, 89.13) * mm, "end": v(-297.25, 88.95) * mm});
            skArc(sketch, "E723", {"start": v(-297.93, 89.63) * mm, "mid": v(-298.04, 88.85) * mm, "end": v(-297.25, 88.95) * mm});
            skArc(sketch, "E724", {"start": v(-297.93, 89.63) * mm, "mid": v(-297.75, 89.82) * mm, "end": v(-297.68, 90.07) * mm});
            skArc(sketch, "E725", {"start": v(-297.68, 91.53) * mm, "mid": v(-297.75, 91.78) * mm, "end": v(-297.93, 91.97) * mm});
            skArc(sketch, "E726", {"start": v(-297.25, 92.65) * mm, "mid": v(-298.04, 92.75) * mm, "end": v(-297.93, 91.97) * mm});
            skArc(sketch, "E727", {"start": v(-297.25, 92.65) * mm, "mid": v(-297.07, 92.47) * mm, "end": v(-296.82, 92.4) * mm});
            skLineSegment(sketch, "E728.bottom", {"start": v(-268.18, 91.53) * mm, "end": v(-268.18, 90.07) * mm});
            skLineSegment(sketch, "E728.top", {"start": v(-278.18, 91.53) * mm, "end": v(-278.18, 90.07) * mm});
            skLineSegment(sketch, "E728.left", {"start": v(-269.05, 92.4) * mm, "end": v(-277.32, 92.4) * mm});
            skLineSegment(sketch, "E728.right", {"start": v(-269.05, 89.2) * mm, "end": v(-277.32, 89.2) * mm});
            skArc(sketch, "E729", {"start": v(-268.18, 90.07) * mm, "mid": v(-268.12, 89.82) * mm, "end": v(-267.93, 89.63) * mm});
            skArc(sketch, "E730", {"start": v(-268.62, 88.95) * mm, "mid": v(-267.83, 88.85) * mm, "end": v(-267.93, 89.63) * mm});
            skArc(sketch, "E731", {"start": v(-268.62, 88.95) * mm, "mid": v(-268.8, 89.13) * mm, "end": v(-269.05, 89.2) * mm});
            skArc(sketch, "E732", {"start": v(-269.05, 92.4) * mm, "mid": v(-268.8, 92.47) * mm, "end": v(-268.62, 92.65) * mm});
            skArc(sketch, "E733", {"start": v(-267.93, 91.97) * mm, "mid": v(-267.83, 92.75) * mm, "end": v(-268.62, 92.65) * mm});
            skArc(sketch, "E734", {"start": v(-267.93, 91.97) * mm, "mid": v(-268.12, 91.78) * mm, "end": v(-268.18, 91.53) * mm});
            skArc(sketch, "E735", {"start": v(-277.32, 89.2) * mm, "mid": v(-277.57, 89.13) * mm, "end": v(-277.75, 88.95) * mm});
            skArc(sketch, "E736", {"start": v(-278.43, 89.63) * mm, "mid": v(-278.54, 88.85) * mm, "end": v(-277.75, 88.95) * mm});
            skArc(sketch, "E737", {"start": v(-278.43, 89.63) * mm, "mid": v(-278.25, 89.82) * mm, "end": v(-278.18, 90.07) * mm});
            skArc(sketch, "E738", {"start": v(-278.18, 91.53) * mm, "mid": v(-278.25, 91.78) * mm, "end": v(-278.43, 91.97) * mm});
            skArc(sketch, "E739", {"start": v(-277.75, 92.65) * mm, "mid": v(-278.54, 92.75) * mm, "end": v(-278.43, 91.97) * mm});
            skArc(sketch, "E740", {"start": v(-277.75, 92.65) * mm, "mid": v(-277.57, 92.47) * mm, "end": v(-277.32, 92.4) * mm});
            skPoint(sketch, "E741", {"position": v(-278.18, 90.8) * mm});
            skPoint(sketch, "E742", {"position": v(-296.18, 128.8) * mm});
            skLineSegment(sketch, "E743.bottom", {"start": v(197.7, 54.27) * mm, "end": v(197.7, 55.73) * mm});
            skLineSegment(sketch, "E743.top", {"start": v(207.7, 54.27) * mm, "end": v(207.7, 55.73) * mm});
            skLineSegment(sketch, "E743.left", {"start": v(198.57, 53.4) * mm, "end": v(206.83, 53.4) * mm});
            skLineSegment(sketch, "E743.right", {"start": v(198.57, 56.6) * mm, "end": v(206.83, 56.6) * mm});
            skArc(sketch, "E744", {"start": v(197.7, 55.73) * mm, "mid": v(197.63, 55.98) * mm, "end": v(197.45, 56.17) * mm});
            skArc(sketch, "E745", {"start": v(198.13, 56.85) * mm, "mid": v(197.35, 56.95) * mm, "end": v(197.45, 56.17) * mm});
            skArc(sketch, "E746", {"start": v(198.13, 56.85) * mm, "mid": v(198.32, 56.67) * mm, "end": v(198.57, 56.6) * mm});
            skArc(sketch, "E747", {"start": v(198.57, 53.4) * mm, "mid": v(198.32, 53.33) * mm, "end": v(198.13, 53.15) * mm});
            skArc(sketch, "E748", {"start": v(197.45, 53.83) * mm, "mid": v(197.35, 53.05) * mm, "end": v(198.13, 53.15) * mm});
            skArc(sketch, "E749", {"start": v(197.45, 53.83) * mm, "mid": v(197.63, 54.02) * mm, "end": v(197.7, 54.27) * mm});
            skArc(sketch, "E750", {"start": v(206.83, 56.6) * mm, "mid": v(207.08, 56.67) * mm, "end": v(207.27, 56.85) * mm});
            skArc(sketch, "E751", {"start": v(207.95, 56.17) * mm, "mid": v(208.05, 56.95) * mm, "end": v(207.27, 56.85) * mm});
            skArc(sketch, "E752", {"start": v(207.95, 56.17) * mm, "mid": v(207.77, 55.98) * mm, "end": v(207.7, 55.73) * mm});
            skArc(sketch, "E753", {"start": v(207.7, 54.27) * mm, "mid": v(207.77, 54.02) * mm, "end": v(207.95, 53.83) * mm});
            skArc(sketch, "E754", {"start": v(207.27, 53.15) * mm, "mid": v(208.05, 53.05) * mm, "end": v(207.95, 53.83) * mm});
            skArc(sketch, "E755", {"start": v(207.27, 53.15) * mm, "mid": v(207.08, 53.33) * mm, "end": v(206.83, 53.4) * mm});
            skLineSegment(sketch, "E756.bottom", {"start": v(170.3, 54.27) * mm, "end": v(170.3, 55.73) * mm});
            skLineSegment(sketch, "E756.top", {"start": v(180.3, 54.27) * mm, "end": v(180.3, 55.73) * mm});
            skLineSegment(sketch, "E756.left", {"start": v(171.17, 53.4) * mm, "end": v(179.43, 53.4) * mm});
            skLineSegment(sketch, "E756.right", {"start": v(171.17, 56.6) * mm, "end": v(179.43, 56.6) * mm});
            skArc(sketch, "E757", {"start": v(170.3, 55.73) * mm, "mid": v(170.23, 55.98) * mm, "end": v(170.05, 56.17) * mm});
            skArc(sketch, "E758", {"start": v(170.73, 56.85) * mm, "mid": v(169.95, 56.95) * mm, "end": v(170.05, 56.17) * mm});
            skArc(sketch, "E759", {"start": v(170.73, 56.85) * mm, "mid": v(170.92, 56.67) * mm, "end": v(171.17, 56.6) * mm});
            skArc(sketch, "E760", {"start": v(171.17, 53.4) * mm, "mid": v(170.92, 53.33) * mm, "end": v(170.73, 53.15) * mm});
            skArc(sketch, "E761", {"start": v(170.05, 53.83) * mm, "mid": v(169.95, 53.05) * mm, "end": v(170.73, 53.15) * mm});
            skArc(sketch, "E762", {"start": v(170.05, 53.83) * mm, "mid": v(170.23, 54.02) * mm, "end": v(170.3, 54.27) * mm});
            skArc(sketch, "E763", {"start": v(179.43, 56.6) * mm, "mid": v(179.68, 56.67) * mm, "end": v(179.87, 56.85) * mm});
            skArc(sketch, "E764", {"start": v(180.55, 56.17) * mm, "mid": v(180.65, 56.95) * mm, "end": v(179.87, 56.85) * mm});
            skArc(sketch, "E765", {"start": v(180.55, 56.17) * mm, "mid": v(180.37, 55.98) * mm, "end": v(180.3, 55.73) * mm});
            skArc(sketch, "E766", {"start": v(180.3, 54.27) * mm, "mid": v(180.37, 54.02) * mm, "end": v(180.55, 53.83) * mm});
            skArc(sketch, "E767", {"start": v(179.87, 53.15) * mm, "mid": v(180.65, 53.05) * mm, "end": v(180.55, 53.83) * mm});
            skArc(sketch, "E768", {"start": v(179.87, 53.15) * mm, "mid": v(179.68, 53.33) * mm, "end": v(179.43, 53.4) * mm});
            skCircle(sketch, "E769", {"center": v(-282.93, 161.2) * mm, "radius": 1.6 * mm});
            skLineSegment(sketch, "E770.bottom", {"start": v(-287.68, 161.93) * mm, "end": v(-287.68, 160.47) * mm});
            skLineSegment(sketch, "E770.top", {"start": v(-297.68, 161.93) * mm, "end": v(-297.68, 160.47) * mm});
            skLineSegment(sketch, "E770.left", {"start": v(-288.55, 162.8) * mm, "end": v(-296.82, 162.8) * mm});
            skLineSegment(sketch, "E770.right", {"start": v(-288.55, 159.6) * mm, "end": v(-296.82, 159.6) * mm});
            skArc(sketch, "E771", {"start": v(-287.68, 160.47) * mm, "mid": v(-287.62, 160.22) * mm, "end": v(-287.43, 160.03) * mm});
            skArc(sketch, "E772", {"start": v(-288.12, 159.35) * mm, "mid": v(-287.33, 159.25) * mm, "end": v(-287.43, 160.03) * mm});
            skArc(sketch, "E773", {"start": v(-288.12, 159.35) * mm, "mid": v(-288.3, 159.53) * mm, "end": v(-288.55, 159.6) * mm});
            skArc(sketch, "E774", {"start": v(-288.55, 162.8) * mm, "mid": v(-288.3, 162.87) * mm, "end": v(-288.12, 163.05) * mm});
            skArc(sketch, "E775", {"start": v(-287.43, 162.37) * mm, "mid": v(-287.33, 163.15) * mm, "end": v(-288.12, 163.05) * mm});
            skArc(sketch, "E776", {"start": v(-287.43, 162.37) * mm, "mid": v(-287.62, 162.18) * mm, "end": v(-287.68, 161.93) * mm});
            skArc(sketch, "E777", {"start": v(-296.82, 159.6) * mm, "mid": v(-297.07, 159.53) * mm, "end": v(-297.25, 159.35) * mm});
            skArc(sketch, "E778", {"start": v(-297.93, 160.03) * mm, "mid": v(-298.04, 159.25) * mm, "end": v(-297.25, 159.35) * mm});
            skArc(sketch, "E779", {"start": v(-297.93, 160.03) * mm, "mid": v(-297.75, 160.22) * mm, "end": v(-297.68, 160.47) * mm});
            skArc(sketch, "E780", {"start": v(-297.68, 161.93) * mm, "mid": v(-297.75, 162.18) * mm, "end": v(-297.93, 162.37) * mm});
            skArc(sketch, "E781", {"start": v(-297.25, 163.05) * mm, "mid": v(-298.04, 163.15) * mm, "end": v(-297.93, 162.37) * mm});
            skArc(sketch, "E782", {"start": v(-297.25, 163.05) * mm, "mid": v(-297.07, 162.87) * mm, "end": v(-296.82, 162.8) * mm});
            skLineSegment(sketch, "E783.bottom", {"start": v(-268.18, 161.93) * mm, "end": v(-268.18, 160.47) * mm});
            skLineSegment(sketch, "E783.top", {"start": v(-278.18, 161.93) * mm, "end": v(-278.18, 160.47) * mm});
            skLineSegment(sketch, "E783.left", {"start": v(-269.05, 162.8) * mm, "end": v(-277.32, 162.8) * mm});
            skLineSegment(sketch, "E783.right", {"start": v(-269.05, 159.6) * mm, "end": v(-277.32, 159.6) * mm});
            skArc(sketch, "E784", {"start": v(-268.18, 160.47) * mm, "mid": v(-268.12, 160.22) * mm, "end": v(-267.93, 160.03) * mm});
            skArc(sketch, "E785", {"start": v(-268.62, 159.35) * mm, "mid": v(-267.83, 159.25) * mm, "end": v(-267.93, 160.03) * mm});
            skArc(sketch, "E786", {"start": v(-268.62, 159.35) * mm, "mid": v(-268.8, 159.53) * mm, "end": v(-269.05, 159.6) * mm});
            skArc(sketch, "E787", {"start": v(-269.05, 162.8) * mm, "mid": v(-268.8, 162.87) * mm, "end": v(-268.62, 163.05) * mm});
            skArc(sketch, "E788", {"start": v(-267.93, 162.37) * mm, "mid": v(-267.83, 163.15) * mm, "end": v(-268.62, 163.05) * mm});
            skArc(sketch, "E789", {"start": v(-267.93, 162.37) * mm, "mid": v(-268.12, 162.18) * mm, "end": v(-268.18, 161.93) * mm});
            skArc(sketch, "E790", {"start": v(-277.32, 159.6) * mm, "mid": v(-277.57, 159.53) * mm, "end": v(-277.75, 159.35) * mm});
            skArc(sketch, "E791", {"start": v(-278.43, 160.03) * mm, "mid": v(-278.54, 159.25) * mm, "end": v(-277.75, 159.35) * mm});
            skArc(sketch, "E792", {"start": v(-278.43, 160.03) * mm, "mid": v(-278.25, 160.22) * mm, "end": v(-278.18, 160.47) * mm});
            skArc(sketch, "E793", {"start": v(-278.18, 161.93) * mm, "mid": v(-278.25, 162.18) * mm, "end": v(-278.43, 162.37) * mm});
            skArc(sketch, "E794", {"start": v(-277.75, 163.05) * mm, "mid": v(-278.54, 163.15) * mm, "end": v(-278.43, 162.37) * mm});
            skArc(sketch, "E795", {"start": v(-277.75, 163.05) * mm, "mid": v(-277.57, 162.87) * mm, "end": v(-277.32, 162.8) * mm});
            skPoint(sketch, "E796", {"position": v(-278.18, 161.2) * mm});
            skLineSegment(sketch, "E797", {"start": v(123.15, 9.13) * mm, "end": v(123.15, 7.5) * mm});
            skLineSegment(sketch, "E798", {"start": v(122.65, 7) * mm, "end": v(113.85, 7) * mm});
            skLineSegment(sketch, "E799", {"start": v(113.35, 7.5) * mm, "end": v(113.35, 9.13) * mm});
            skPoint(sketch, "E800", {"position": v(128, 22) * mm});
            skLineSegment(sketch, "E801.trimOffspring", {"start": v(133.28, 10) * mm, "end": v(129.75, 10) * mm});
            skLineSegment(sketch, "E802.trimOffspring", {"start": v(126.25, 10) * mm, "end": v(124.02, 10) * mm});
            skLineSegment(sketch, "E803.bottom", {"start": v(-151.73, 621.46) * mm, "end": v(-150.27, 621.46) * mm});
            skLineSegment(sketch, "E803.top", {"start": v(-151.73, 601.06) * mm, "end": v(-150.27, 601.06) * mm});
            skArc(sketch, "E804", {"start": v(-150.27, 621.46) * mm, "mid": v(-150.02, 621.52) * mm, "end": v(-149.83, 621.7) * mm});
            skArc(sketch, "E805", {"start": v(-149.15, 621.02) * mm, "mid": v(-149.05, 621.8) * mm, "end": v(-149.83, 621.7) * mm});
            skArc(sketch, "E806", {"start": v(-149.15, 621.02) * mm, "mid": v(-149.33, 620.84) * mm, "end": v(-149.4, 620.59) * mm});
            skArc(sketch, "E807", {"start": v(-152.6, 620.59) * mm, "mid": v(-152.67, 620.84) * mm, "end": v(-152.85, 621.02) * mm});
            skArc(sketch, "E808", {"start": v(-152.17, 621.7) * mm, "mid": v(-152.95, 621.8) * mm, "end": v(-152.85, 621.02) * mm});
            skArc(sketch, "E809", {"start": v(-152.17, 621.7) * mm, "mid": v(-151.98, 621.52) * mm, "end": v(-151.73, 621.46) * mm});
            skArc(sketch, "E810", {"start": v(-149.4, 601.92) * mm, "mid": v(-149.33, 601.67) * mm, "end": v(-149.15, 601.49) * mm});
            skArc(sketch, "E811", {"start": v(-149.83, 600.8) * mm, "mid": v(-149.05, 600.7) * mm, "end": v(-149.15, 601.49) * mm});
            skArc(sketch, "E812", {"start": v(-149.83, 600.8) * mm, "mid": v(-150.02, 600.99) * mm, "end": v(-150.27, 601.06) * mm});
            skArc(sketch, "E813", {"start": v(-151.73, 601.06) * mm, "mid": v(-151.98, 600.99) * mm, "end": v(-152.17, 600.8) * mm});
            skArc(sketch, "E814", {"start": v(-152.85, 601.49) * mm, "mid": v(-152.95, 600.7) * mm, "end": v(-152.17, 600.8) * mm});
            skArc(sketch, "E815", {"start": v(-152.85, 601.49) * mm, "mid": v(-152.67, 601.67) * mm, "end": v(-152.6, 601.92) * mm});
            skLineSegment(sketch, "E816.bottom", {"start": v(-199.9, 581.49) * mm, "end": v(-199.9, 580.02) * mm});
            skLineSegment(sketch, "E816.top", {"start": v(-215.1, 581.49) * mm, "end": v(-215.1, 580.02) * mm});
            skArc(sketch, "E817", {"start": v(-199.9, 580.02) * mm, "mid": v(-199.83, 579.77) * mm, "end": v(-199.65, 579.59) * mm});
            skArc(sketch, "E818", {"start": v(-200.33, 578.9) * mm, "mid": v(-199.55, 578.8) * mm, "end": v(-199.65, 579.59) * mm});
            skArc(sketch, "E819", {"start": v(-200.33, 578.9) * mm, "mid": v(-200.52, 579.09) * mm, "end": v(-200.77, 579.16) * mm});
            skArc(sketch, "E820", {"start": v(-200.77, 582.36) * mm, "mid": v(-200.52, 582.42) * mm, "end": v(-200.33, 582.6) * mm});
            skArc(sketch, "E821", {"start": v(-199.65, 581.92) * mm, "mid": v(-199.55, 582.7) * mm, "end": v(-200.33, 582.6) * mm});
            skArc(sketch, "E822", {"start": v(-199.65, 581.92) * mm, "mid": v(-199.83, 581.74) * mm, "end": v(-199.9, 581.49) * mm});
            skArc(sketch, "E823", {"start": v(-214.23, 579.16) * mm, "mid": v(-214.48, 579.09) * mm, "end": v(-214.67, 578.9) * mm});
            skArc(sketch, "E824", {"start": v(-215.35, 579.59) * mm, "mid": v(-215.45, 578.8) * mm, "end": v(-214.67, 578.9) * mm});
            skArc(sketch, "E825", {"start": v(-215.35, 579.59) * mm, "mid": v(-215.17, 579.77) * mm, "end": v(-215.1, 580.02) * mm});
            skArc(sketch, "E826", {"start": v(-215.1, 581.49) * mm, "mid": v(-215.17, 581.74) * mm, "end": v(-215.35, 581.92) * mm});
            skArc(sketch, "E827", {"start": v(-214.67, 582.6) * mm, "mid": v(-215.45, 582.7) * mm, "end": v(-215.35, 581.92) * mm});
            skArc(sketch, "E828", {"start": v(-214.67, 582.6) * mm, "mid": v(-214.48, 582.42) * mm, "end": v(-214.23, 582.36) * mm});
            skLineSegment(sketch, "E829", {"start": v(-297.58, 56.5) * mm, "end": v(-559.8, 56.5) * mm, "construction": true});
            skLineSegment(sketch, "E830", {"start": v(-602.4, 9.14) * mm, "end": v(-602.4, 7.5) * mm});
            skLineSegment(sketch, "E831.trimOffspring", {"start": v(-432.16, 10) * mm, "end": v(-434.4, 10) * mm});
            skLineSegment(sketch, "E832.trimOffspring", {"start": v(-559.5, 10) * mm, "end": v(-561.74, 10) * mm});
            skLineSegment(sketch, "E833.trimOffspring", {"start": v(-445.92, 10) * mm, "end": v(-542.24, 10) * mm});
            skLineSegment(sketch, "E834.trimOffspring", {"start": v(-426.42, 10) * mm, "end": v(-428.66, 10) * mm});
            skLineSegment(sketch, "E835", {"start": v(-276.18, -2.5) * mm, "end": v(-276.17, -3.02) * mm});
            skPoint(sketch, "E836.visualSharp", {"position": v(-276.15, -5) * mm});
            skArc(sketch, "E836.filletArc", {"start": v(-276.17, -3.02) * mm, "mid": v(-275.58, -4.42) * mm, "end": v(-274.17, -5) * mm});
            skPoint(sketch, "E837.visualSharp", {"position": v(-737.4, -5) * mm});
            skArc(sketch, "E837.filletArc", {"start": v(-737.4, -3) * mm, "mid": v(-736.82, -4.41) * mm, "end": v(-735.4, -5) * mm});
            skPoint(sketch, "E838.visualSharp", {"position": v(-715.4, -5) * mm});
            skArc(sketch, "E838.filletArc", {"start": v(-717.4, -5) * mm, "mid": v(-716, -4.41) * mm, "end": v(-715.4, -3) * mm});
            skPoint(sketch, "E839.visualSharp", {"position": v(-635.2, -5) * mm});
            skArc(sketch, "E839.filletArc", {"start": v(-635.2, -3) * mm, "mid": v(-634.62, -4.41) * mm, "end": v(-633.2, -5) * mm});
            skPoint(sketch, "E840.visualSharp", {"position": v(-605.4, -5) * mm});
            skArc(sketch, "E840.filletArc", {"start": v(-612.4, -5) * mm, "mid": v(-611, -4.41) * mm, "end": v(-610.4, -3) * mm});
            skPoint(sketch, "E841.visualSharp", {"position": v(-227.5, -5) * mm});
            skArc(sketch, "E841.filletArc", {"start": v(-227.5, -3) * mm, "mid": v(-226.91, -4.41) * mm, "end": v(-225.5, -5) * mm});
            skPoint(sketch, "E842.visualSharp", {"position": v(-134.15, -5) * mm});
            skArc(sketch, "E842.filletArc", {"start": v(-136.15, -5) * mm, "mid": v(-134.74, -4.41) * mm, "end": v(-134.15, -3) * mm});
            skPoint(sketch, "E843.visualSharp", {"position": v(134.15, -5) * mm});
            skArc(sketch, "E843.filletArc", {"start": v(134.15, -3) * mm, "mid": v(134.74, -4.41) * mm, "end": v(136.15, -5) * mm});
            skPoint(sketch, "E844.visualSharp", {"position": v(227.5, -5) * mm});
            skArc(sketch, "E844.filletArc", {"start": v(225.5, -5) * mm, "mid": v(226.91, -4.41) * mm, "end": v(227.5, -3) * mm});
            skPoint(sketch, "E845.visualSharp", {"position": v(-250.93, 83.5) * mm});
            skArc(sketch, "E845.filletArc", {"start": v(-252.93, 83.5) * mm, "mid": v(-251.52, 84.09) * mm, "end": v(-250.93, 85.5) * mm});
            skLineSegment(sketch, "E846.bottom", {"start": v(-151.73, 56.6) * mm, "end": v(-150.27, 56.6) * mm});
            skArc(sketch, "E847", {"start": v(-150.27, 56.6) * mm, "mid": v(-150.02, 56.67) * mm, "end": v(-149.83, 56.85) * mm});
            skArc(sketch, "E848", {"start": v(-149.15, 56.17) * mm, "mid": v(-149.05, 56.95) * mm, "end": v(-149.83, 56.85) * mm});
            skArc(sketch, "E849", {"start": v(-149.15, 56.17) * mm, "mid": v(-149.33, 55.98) * mm, "end": v(-149.4, 55.73) * mm});
            skArc(sketch, "E850", {"start": v(-152.6, 55.73) * mm, "mid": v(-152.67, 55.98) * mm, "end": v(-152.85, 56.17) * mm});
            skArc(sketch, "E851", {"start": v(-152.17, 56.85) * mm, "mid": v(-152.95, 56.95) * mm, "end": v(-152.85, 56.17) * mm});
            skArc(sketch, "E852", {"start": v(-152.17, 56.85) * mm, "mid": v(-151.98, 56.67) * mm, "end": v(-151.73, 56.6) * mm});
            skLineSegment(sketch, "E853.top", {"start": v(-151.73, 6.9) * mm, "end": v(-150.27, 6.9) * mm});
            skArc(sketch, "E854", {"start": v(-149.4, 7.77) * mm, "mid": v(-149.33, 7.52) * mm, "end": v(-149.15, 7.33) * mm});
            skArc(sketch, "E855", {"start": v(-149.83, 6.65) * mm, "mid": v(-149.05, 6.55) * mm, "end": v(-149.15, 7.33) * mm});
            skArc(sketch, "E856", {"start": v(-149.83, 6.65) * mm, "mid": v(-150.02, 6.83) * mm, "end": v(-150.27, 6.9) * mm});
            skArc(sketch, "E857", {"start": v(-151.73, 6.9) * mm, "mid": v(-151.98, 6.83) * mm, "end": v(-152.17, 6.65) * mm});
            skArc(sketch, "E858", {"start": v(-152.85, 7.33) * mm, "mid": v(-152.95, 6.55) * mm, "end": v(-152.17, 6.65) * mm});
            skArc(sketch, "E859", {"start": v(-152.85, 7.33) * mm, "mid": v(-152.67, 7.52) * mm, "end": v(-152.6, 7.77) * mm});
            skLineSegment(sketch, "E860", {"start": v(152.6, 55.73) * mm, "end": v(152.6, 7.77) * mm});
            skLineSegment(sketch, "E861", {"start": v(149.4, 55.73) * mm, "end": v(149.4, 7.77) * mm});
            skLineSegment(sketch, "E862.bottom", {"start": v(150.27, 56.6) * mm, "end": v(151.73, 56.6) * mm});
            skArc(sketch, "E863", {"start": v(151.73, 56.6) * mm, "mid": v(151.98, 56.67) * mm, "end": v(152.17, 56.85) * mm});
            skArc(sketch, "E864", {"start": v(152.85, 56.17) * mm, "mid": v(152.95, 56.95) * mm, "end": v(152.17, 56.85) * mm});
            skArc(sketch, "E865", {"start": v(152.85, 56.17) * mm, "mid": v(152.67, 55.98) * mm, "end": v(152.6, 55.73) * mm});
            skArc(sketch, "E866", {"start": v(149.4, 55.73) * mm, "mid": v(149.33, 55.98) * mm, "end": v(149.15, 56.17) * mm});
            skArc(sketch, "E867", {"start": v(149.83, 56.85) * mm, "mid": v(149.05, 56.95) * mm, "end": v(149.15, 56.17) * mm});
            skArc(sketch, "E868", {"start": v(149.83, 56.85) * mm, "mid": v(150.02, 56.67) * mm, "end": v(150.27, 56.6) * mm});
            skLineSegment(sketch, "E869.top", {"start": v(150.27, 6.9) * mm, "end": v(151.73, 6.9) * mm});
            skArc(sketch, "E870", {"start": v(152.6, 7.77) * mm, "mid": v(152.67, 7.52) * mm, "end": v(152.85, 7.33) * mm});
            skArc(sketch, "E871", {"start": v(152.17, 6.65) * mm, "mid": v(152.95, 6.55) * mm, "end": v(152.85, 7.33) * mm});
            skArc(sketch, "E872", {"start": v(152.17, 6.65) * mm, "mid": v(151.98, 6.83) * mm, "end": v(151.73, 6.9) * mm});
            skArc(sketch, "E873", {"start": v(150.27, 6.9) * mm, "mid": v(150.02, 6.83) * mm, "end": v(149.83, 6.65) * mm});
            skArc(sketch, "E874", {"start": v(149.15, 7.33) * mm, "mid": v(149.05, 6.55) * mm, "end": v(149.83, 6.65) * mm});
            skArc(sketch, "E875", {"start": v(149.15, 7.33) * mm, "mid": v(149.33, 7.52) * mm, "end": v(149.4, 7.77) * mm});
            skCircle(sketch, "E876", {"center": v(190.05, 271.15) * mm, "radius": 1.6 * mm});
            skLineSegment(sketch, "E877", {"start": v(-605.4, 57.37) * mm, "end": v(-605.4, 81.23) * mm});
            skLineSegment(sketch, "E878.trimOffspring", {"start": v(-573.27, 10) * mm, "end": v(-601.54, 10) * mm});
            skLineSegment(sketch, "E879", {"start": v(-605.4, 9.13) * mm, "end": v(-605.4, 7.5) * mm});
            skLineSegment(sketch, "E880", {"start": v(-609.54, 10) * mm, "end": v(-606.27, 10) * mm});
            skLineSegment(sketch, "E881", {"start": v(-604.9, 7) * mm, "end": v(-602.9, 7) * mm});
            skPoint(sketch, "E882.visualSharp", {"position": v(-123.15, 7) * mm});
            skArc(sketch, "E882.filletArc", {"start": v(-123.15, 7.5) * mm, "mid": v(-123, 7.15) * mm, "end": v(-122.65, 7) * mm});
            skPoint(sketch, "E883.visualSharp", {"position": v(-113.35, 7) * mm});
            skArc(sketch, "E883.filletArc", {"start": v(-113.85, 7) * mm, "mid": v(-113.5, 7.15) * mm, "end": v(-113.35, 7.5) * mm});
            skPoint(sketch, "E884.visualSharp", {"position": v(-47.85, 7) * mm});
            skArc(sketch, "E884.filletArc", {"start": v(-48.35, 7) * mm, "mid": v(-48, 7.15) * mm, "end": v(-47.85, 7.5) * mm});
            skPoint(sketch, "E885.visualSharp", {"position": v(-57.65, 7) * mm});
            skArc(sketch, "E885.filletArc", {"start": v(-57.65, 7.5) * mm, "mid": v(-57.5, 7.15) * mm, "end": v(-57.15, 7) * mm});
            skPoint(sketch, "E886.visualSharp", {"position": v(-38.15, 7) * mm});
            skArc(sketch, "E886.filletArc", {"start": v(-38.15, 7.5) * mm, "mid": v(-38, 7.15) * mm, "end": v(-37.65, 7) * mm});
            skPoint(sketch, "E887.visualSharp", {"position": v(-28.35, 7) * mm});
            skArc(sketch, "E887.filletArc", {"start": v(-28.85, 7) * mm, "mid": v(-28.5, 7.15) * mm, "end": v(-28.35, 7.5) * mm});
            skPoint(sketch, "E888.visualSharp", {"position": v(28.35, 7) * mm});
            skArc(sketch, "E888.filletArc", {"start": v(28.35, 7.5) * mm, "mid": v(28.5, 7.15) * mm, "end": v(28.85, 7) * mm});
            skPoint(sketch, "E889.visualSharp", {"position": v(38.15, 7) * mm});
            skArc(sketch, "E889.filletArc", {"start": v(37.65, 7) * mm, "mid": v(38, 7.15) * mm, "end": v(38.15, 7.5) * mm});
            skPoint(sketch, "E890.visualSharp", {"position": v(47.85, 7) * mm});
            skArc(sketch, "E890.filletArc", {"start": v(47.85, 7.5) * mm, "mid": v(48, 7.15) * mm, "end": v(48.35, 7) * mm});
            skPoint(sketch, "E891.visualSharp", {"position": v(57.65, 7) * mm});
            skArc(sketch, "E891.filletArc", {"start": v(57.15, 7) * mm, "mid": v(57.5, 7.15) * mm, "end": v(57.65, 7.5) * mm});
            skPoint(sketch, "E892.visualSharp", {"position": v(113.35, 7) * mm});
            skArc(sketch, "E892.filletArc", {"start": v(113.35, 7.5) * mm, "mid": v(113.5, 7.15) * mm, "end": v(113.85, 7) * mm});
            skPoint(sketch, "E893.visualSharp", {"position": v(123.15, 7) * mm});
            skArc(sketch, "E893.filletArc", {"start": v(122.65, 7) * mm, "mid": v(123, 7.15) * mm, "end": v(123.15, 7.5) * mm});
            skPoint(sketch, "E894.visualSharp", {"position": v(-215, 433.5) * mm});
            skArc(sketch, "E894.filletArc", {"start": v(-214.5, 433.5) * mm, "mid": v(-214.85, 433.35) * mm, "end": v(-215, 433) * mm});
            skPoint(sketch, "E895.visualSharp", {"position": v(-200, 433.5) * mm});
            skArc(sketch, "E895.filletArc", {"start": v(-200, 433) * mm, "mid": v(-200.15, 433.35) * mm, "end": v(-200.5, 433.5) * mm});
            skPoint(sketch, "E896.visualSharp", {"position": v(-176.8, 433.5) * mm});
            skArc(sketch, "E896.filletArc", {"start": v(-153.1, 433.5) * mm, "mid": v(-153.45, 433.35) * mm, "end": v(-153.6, 433) * mm});
            skPoint(sketch, "E897.visualSharp", {"position": v(153.6, 433.5) * mm});
            skArc(sketch, "E897.filletArc", {"start": v(153.6, 433) * mm, "mid": v(153.45, 433.35) * mm, "end": v(153.1, 433.5) * mm});
            skPoint(sketch, "E898.visualSharp", {"position": v(200, 433.5) * mm});
            skArc(sketch, "E898.filletArc", {"start": v(200.5, 433.5) * mm, "mid": v(200.15, 433.35) * mm, "end": v(200, 433) * mm});
            skPoint(sketch, "E899.visualSharp", {"position": v(215, 433.5) * mm});
            skArc(sketch, "E899.filletArc", {"start": v(215, 433) * mm, "mid": v(214.85, 433.35) * mm, "end": v(214.5, 433.5) * mm});
            skArc(sketch, "E900", {"start": v(-112.92, 10.25) * mm, "mid": v(-112.73, 10.07) * mm, "end": v(-112.48, 10) * mm});
            skArc(sketch, "E901", {"start": v(-112.92, 10.25) * mm, "mid": v(-113.7, 10.35) * mm, "end": v(-113.6, 9.57) * mm});
            skArc(sketch, "E902", {"start": v(-113.35, 9.13) * mm, "mid": v(-113.42, 9.38) * mm, "end": v(-113.6, 9.57) * mm});
            skArc(sketch, "E903", {"start": v(-122.9, 9.57) * mm, "mid": v(-123.08, 9.38) * mm, "end": v(-123.15, 9.13) * mm});
            skArc(sketch, "E904", {"start": v(-122.9, 9.57) * mm, "mid": v(-122.8, 10.35) * mm, "end": v(-123.58, 10.25) * mm});
            skArc(sketch, "E905", {"start": v(-124.02, 10) * mm, "mid": v(-123.77, 10.07) * mm, "end": v(-123.58, 10.25) * mm});
            skArc(sketch, "E906", {"start": v(-47.42, 10.25) * mm, "mid": v(-47.23, 10.07) * mm, "end": v(-46.98, 10) * mm});
            skArc(sketch, "E907", {"start": v(-47.42, 10.25) * mm, "mid": v(-48.2, 10.35) * mm, "end": v(-48.1, 9.57) * mm});
            skArc(sketch, "E908", {"start": v(-47.85, 9.13) * mm, "mid": v(-47.92, 9.38) * mm, "end": v(-48.1, 9.57) * mm});
            skArc(sketch, "E909", {"start": v(-57.4, 9.57) * mm, "mid": v(-57.58, 9.38) * mm, "end": v(-57.65, 9.13) * mm});
            skArc(sketch, "E910", {"start": v(-57.4, 9.57) * mm, "mid": v(-57.3, 10.35) * mm, "end": v(-58.08, 10.25) * mm});
            skArc(sketch, "E911", {"start": v(-58.52, 10) * mm, "mid": v(-58.27, 10.07) * mm, "end": v(-58.08, 10.25) * mm});
            skArc(sketch, "E912", {"start": v(-133.72, 10.25) * mm, "mid": v(-133.53, 10.07) * mm, "end": v(-133.28, 10) * mm});
            skArc(sketch, "E913", {"start": v(-133.72, 10.25) * mm, "mid": v(-134.5, 10.35) * mm, "end": v(-134.4, 9.57) * mm});
            skArc(sketch, "E914", {"start": v(-134.15, 9.13) * mm, "mid": v(-134.22, 9.38) * mm, "end": v(-134.4, 9.57) * mm});
            skArc(sketch, "E915", {"start": v(-27.92, 10.25) * mm, "mid": v(-27.73, 10.07) * mm, "end": v(-27.48, 10) * mm});
            skArc(sketch, "E916", {"start": v(-27.92, 10.25) * mm, "mid": v(-28.7, 10.35) * mm, "end": v(-28.6, 9.57) * mm});
            skArc(sketch, "E917", {"start": v(-28.35, 9.13) * mm, "mid": v(-28.42, 9.38) * mm, "end": v(-28.6, 9.57) * mm});
            skArc(sketch, "E918", {"start": v(38.58, 10.25) * mm, "mid": v(38.77, 10.07) * mm, "end": v(39.02, 10) * mm});
            skArc(sketch, "E919", {"start": v(38.58, 10.25) * mm, "mid": v(37.8, 10.35) * mm, "end": v(37.9, 9.57) * mm});
            skArc(sketch, "E920", {"start": v(38.15, 9.13) * mm, "mid": v(38.08, 9.38) * mm, "end": v(37.9, 9.57) * mm});
            skArc(sketch, "E921", {"start": v(28.6, 9.57) * mm, "mid": v(28.42, 9.38) * mm, "end": v(28.35, 9.13) * mm});
            skArc(sketch, "E922", {"start": v(28.6, 9.57) * mm, "mid": v(28.7, 10.35) * mm, "end": v(27.92, 10.25) * mm});
            skArc(sketch, "E923", {"start": v(27.48, 10) * mm, "mid": v(27.73, 10.07) * mm, "end": v(27.92, 10.25) * mm});
            skArc(sketch, "E924", {"start": v(58.08, 10.25) * mm, "mid": v(58.27, 10.07) * mm, "end": v(58.52, 10) * mm});
            skArc(sketch, "E925", {"start": v(58.08, 10.25) * mm, "mid": v(57.3, 10.35) * mm, "end": v(57.4, 9.57) * mm});
            skArc(sketch, "E926", {"start": v(57.65, 9.13) * mm, "mid": v(57.58, 9.38) * mm, "end": v(57.4, 9.57) * mm});
            skArc(sketch, "E927", {"start": v(48.1, 9.57) * mm, "mid": v(47.92, 9.38) * mm, "end": v(47.85, 9.13) * mm});
            skArc(sketch, "E928", {"start": v(48.1, 9.57) * mm, "mid": v(48.2, 10.35) * mm, "end": v(47.42, 10.25) * mm});
            skArc(sketch, "E929", {"start": v(46.98, 10) * mm, "mid": v(47.23, 10.07) * mm, "end": v(47.42, 10.25) * mm});
            skArc(sketch, "E930", {"start": v(-37.9, 9.57) * mm, "mid": v(-38.08, 9.38) * mm, "end": v(-38.15, 9.13) * mm});
            skArc(sketch, "E931", {"start": v(-37.9, 9.57) * mm, "mid": v(-37.8, 10.35) * mm, "end": v(-38.58, 10.25) * mm});
            skArc(sketch, "E932", {"start": v(-39.02, 10) * mm, "mid": v(-38.77, 10.07) * mm, "end": v(-38.58, 10.25) * mm});
            skArc(sketch, "E933", {"start": v(134.4, 9.57) * mm, "mid": v(134.22, 9.38) * mm, "end": v(134.15, 9.13) * mm});
            skArc(sketch, "E934", {"start": v(134.4, 9.57) * mm, "mid": v(134.5, 10.35) * mm, "end": v(133.72, 10.25) * mm});
            skArc(sketch, "E935", {"start": v(133.28, 10) * mm, "mid": v(133.53, 10.07) * mm, "end": v(133.72, 10.25) * mm});
            skArc(sketch, "E936", {"start": v(123.58, 10.25) * mm, "mid": v(123.77, 10.07) * mm, "end": v(124.02, 10) * mm});
            skArc(sketch, "E937", {"start": v(123.58, 10.25) * mm, "mid": v(122.8, 10.35) * mm, "end": v(122.9, 9.57) * mm});
            skArc(sketch, "E938", {"start": v(123.15, 9.13) * mm, "mid": v(123.08, 9.38) * mm, "end": v(122.9, 9.57) * mm});
            skArc(sketch, "E939", {"start": v(113.6, 9.57) * mm, "mid": v(113.42, 9.38) * mm, "end": v(113.35, 9.13) * mm});
            skArc(sketch, "E940", {"start": v(113.6, 9.57) * mm, "mid": v(113.7, 10.35) * mm, "end": v(112.92, 10.25) * mm});
            skArc(sketch, "E941", {"start": v(112.48, 10) * mm, "mid": v(112.73, 10.07) * mm, "end": v(112.92, 10.25) * mm});
            skArc(sketch, "E942", {"start": v(199.57, 430.25) * mm, "mid": v(199.38, 430.43) * mm, "end": v(199.13, 430.5) * mm});
            skArc(sketch, "E943", {"start": v(199.57, 430.25) * mm, "mid": v(200.35, 430.15) * mm, "end": v(200.25, 430.93) * mm});
            skArc(sketch, "E944", {"start": v(200, 431.37) * mm, "mid": v(200.07, 431.12) * mm, "end": v(200.25, 430.93) * mm});
            skArc(sketch, "E945", {"start": v(214.75, 430.93) * mm, "mid": v(214.93, 431.12) * mm, "end": v(215, 431.37) * mm});
            skArc(sketch, "E946", {"start": v(214.75, 430.93) * mm, "mid": v(214.65, 430.15) * mm, "end": v(215.43, 430.25) * mm});
            skArc(sketch, "E947", {"start": v(215.87, 430.5) * mm, "mid": v(215.62, 430.43) * mm, "end": v(215.43, 430.25) * mm});
            skArc(sketch, "E948", {"start": v(-154.03, 430.25) * mm, "mid": v(-154.22, 430.43) * mm, "end": v(-154.47, 430.5) * mm});
            skArc(sketch, "E949", {"start": v(-154.03, 430.25) * mm, "mid": v(-153.25, 430.15) * mm, "end": v(-153.35, 430.93) * mm});
            skArc(sketch, "E950", {"start": v(-153.6, 431.37) * mm, "mid": v(-153.53, 431.12) * mm, "end": v(-153.35, 430.93) * mm});
            skArc(sketch, "E951", {"start": v(153.35, 430.93) * mm, "mid": v(153.53, 431.12) * mm, "end": v(153.6, 431.37) * mm});
            skArc(sketch, "E952", {"start": v(153.35, 430.93) * mm, "mid": v(153.25, 430.15) * mm, "end": v(154.03, 430.25) * mm});
            skArc(sketch, "E953", {"start": v(154.47, 430.5) * mm, "mid": v(154.22, 430.43) * mm, "end": v(154.03, 430.25) * mm});
            skArc(sketch, "E954", {"start": v(-215.43, 430.25) * mm, "mid": v(-215.62, 430.43) * mm, "end": v(-215.87, 430.5) * mm});
            skArc(sketch, "E955", {"start": v(-215.43, 430.25) * mm, "mid": v(-214.65, 430.15) * mm, "end": v(-214.75, 430.93) * mm});
            skArc(sketch, "E956", {"start": v(-215, 431.37) * mm, "mid": v(-214.93, 431.12) * mm, "end": v(-214.75, 430.93) * mm});
            skArc(sketch, "E957", {"start": v(-200.25, 430.93) * mm, "mid": v(-200.07, 431.12) * mm, "end": v(-200, 431.37) * mm});
            skArc(sketch, "E958", {"start": v(-200.25, 430.93) * mm, "mid": v(-200.35, 430.15) * mm, "end": v(-199.57, 430.25) * mm});
            skArc(sketch, "E959", {"start": v(-199.13, 430.5) * mm, "mid": v(-199.38, 430.43) * mm, "end": v(-199.57, 430.25) * mm});
            skPoint(sketch, "E960.visualSharp", {"position": v(-370.4, 34.35) * mm});
            skArc(sketch, "E960.filletArc", {"start": v(-370.4, 33.85) * mm, "mid": v(-370.55, 34.2) * mm, "end": v(-370.9, 34.35) * mm});
            skPoint(sketch, "E961.visualSharp", {"position": v(-370.4, 28.35) * mm});
            skArc(sketch, "E961.filletArc", {"start": v(-370.9, 28.35) * mm, "mid": v(-370.55, 28.5) * mm, "end": v(-370.4, 28.85) * mm});
            skPoint(sketch, "E962.visualSharp", {"position": v(-370.4, 12.65) * mm});
            skArc(sketch, "E962.filletArc", {"start": v(-370.9, 12.65) * mm, "mid": v(-370.55, 12.8) * mm, "end": v(-370.4, 13.15) * mm});
            skPoint(sketch, "E963.visualSharp", {"position": v(-370.4, 18.65) * mm});
            skArc(sketch, "E963.filletArc", {"start": v(-370.4, 18.15) * mm, "mid": v(-370.55, 18.5) * mm, "end": v(-370.9, 18.65) * mm});
            skPoint(sketch, "E964.visualSharp", {"position": v(-425.56, 7) * mm});
            skArc(sketch, "E964.filletArc", {"start": v(-425.56, 7.5) * mm, "mid": v(-425.4, 7.15) * mm, "end": v(-425.06, 7) * mm});
            skPoint(sketch, "E965.visualSharp", {"position": v(-435.26, 7) * mm});
            skArc(sketch, "E965.filletArc", {"start": v(-435.76, 7) * mm, "mid": v(-435.4, 7.15) * mm, "end": v(-435.26, 7.5) * mm});
            skPoint(sketch, "E966.visualSharp", {"position": v(-445.06, 7) * mm});
            skArc(sketch, "E966.filletArc", {"start": v(-445.06, 7.5) * mm, "mid": v(-444.9, 7.15) * mm, "end": v(-444.56, 7) * mm});
            skPoint(sketch, "E967.visualSharp", {"position": v(-415.76, 7) * mm});
            skArc(sketch, "E967.filletArc", {"start": v(-416.26, 7) * mm, "mid": v(-415.9, 7.15) * mm, "end": v(-415.76, 7.5) * mm});
            skPoint(sketch, "E968.visualSharp", {"position": v(-572.4, 7) * mm});
            skArc(sketch, "E968.filletArc", {"start": v(-572.4, 7.5) * mm, "mid": v(-572.26, 7.15) * mm, "end": v(-571.9, 7) * mm});
            skPoint(sketch, "E969.visualSharp", {"position": v(-562.6, 7) * mm});
            skArc(sketch, "E969.filletArc", {"start": v(-563.1, 7) * mm, "mid": v(-562.75, 7.15) * mm, "end": v(-562.6, 7.5) * mm});
            skPoint(sketch, "E970.visualSharp", {"position": v(-552.9, 7) * mm});
            skArc(sketch, "E970.filletArc", {"start": v(-552.9, 7.5) * mm, "mid": v(-552.76, 7.15) * mm, "end": v(-552.4, 7) * mm});
            skPoint(sketch, "E971.visualSharp", {"position": v(-543.1, 7) * mm});
            skArc(sketch, "E971.filletArc", {"start": v(-543.6, 7) * mm, "mid": v(-543.25, 7.15) * mm, "end": v(-543.1, 7.5) * mm});
            skPoint(sketch, "E972.visualSharp", {"position": v(-705.7, 7) * mm});
            skArc(sketch, "E972.filletArc", {"start": v(-705.7, 7.5) * mm, "mid": v(-705.56, 7.15) * mm, "end": v(-705.2, 7) * mm});
            skPoint(sketch, "E973.visualSharp", {"position": v(-695.9, 7) * mm});
            skArc(sketch, "E973.filletArc", {"start": v(-696.4, 7) * mm, "mid": v(-696.05, 7.15) * mm, "end": v(-695.9, 7.5) * mm});
            skPoint(sketch, "E974.visualSharp", {"position": v(-654.7, 7) * mm});
            skArc(sketch, "E974.filletArc", {"start": v(-654.7, 7.5) * mm, "mid": v(-654.56, 7.15) * mm, "end": v(-654.2, 7) * mm});
            skPoint(sketch, "E975.visualSharp", {"position": v(-644.9, 7) * mm});
            skArc(sketch, "E975.filletArc", {"start": v(-645.4, 7) * mm, "mid": v(-645.05, 7.15) * mm, "end": v(-644.9, 7.5) * mm});
            skPoint(sketch, "E976.visualSharp", {"position": v(-750.4, 45.7) * mm});
            skArc(sketch, "E976.filletArc", {"start": v(-749.9, 45.7) * mm, "mid": v(-750.26, 45.55) * mm, "end": v(-750.4, 45.2) * mm});
            skPoint(sketch, "E977.newPointA", {"position": v(-750.4, 25.3) * mm});
            skArc(sketch, "E977.filletArc", {"start": v(-750.4, 25.8) * mm, "mid": v(-750.26, 25.45) * mm, "end": v(-749.9, 25.3) * mm});
            skPoint(sketch, "E978.visualSharp", {"position": v(-644.4, 433.5) * mm});
            skArc(sketch, "E978.filletArc", {"start": v(-643.9, 433.5) * mm, "mid": v(-644.26, 433.35) * mm, "end": v(-644.4, 433) * mm});
            skPoint(sketch, "E979.visualSharp", {"position": v(-624.4, 433.5) * mm});
            skArc(sketch, "E979.filletArc", {"start": v(-624.4, 433) * mm, "mid": v(-624.55, 433.35) * mm, "end": v(-624.9, 433.5) * mm});
            skPoint(sketch, "E980.visualSharp", {"position": v(-602.4, 418.6) * mm});
            skArc(sketch, "E980.filletArc", {"start": v(-602.4, 418.1) * mm, "mid": v(-602.55, 418.45) * mm, "end": v(-602.9, 418.6) * mm});
            skPoint(sketch, "E981.visualSharp", {"position": v(-602.4, 410.6) * mm});
            skArc(sketch, "E981.filletArc", {"start": v(-602.9, 410.6) * mm, "mid": v(-602.55, 410.75) * mm, "end": v(-602.4, 411.1) * mm});
            skPoint(sketch, "E982.visualSharp", {"position": v(-602.4, 399.8) * mm});
            skArc(sketch, "E982.filletArc", {"start": v(-602.4, 399.3) * mm, "mid": v(-602.55, 399.65) * mm, "end": v(-602.9, 399.8) * mm});
            skPoint(sketch, "E983.visualSharp", {"position": v(-602.4, 373) * mm});
            skArc(sketch, "E983.filletArc", {"start": v(-602.9, 373) * mm, "mid": v(-602.55, 373.15) * mm, "end": v(-602.4, 373.5) * mm});
            skPoint(sketch, "E984.visualSharp", {"position": v(-602.4, 391.8) * mm});
            skArc(sketch, "E984.filletArc", {"start": v(-602.9, 391.8) * mm, "mid": v(-602.55, 391.95) * mm, "end": v(-602.4, 392.3) * mm});
            skPoint(sketch, "E985.visualSharp", {"position": v(-602.4, 381) * mm});
            skArc(sketch, "E985.filletArc", {"start": v(-602.4, 380.5) * mm, "mid": v(-602.55, 380.85) * mm, "end": v(-602.9, 381) * mm});
            skPoint(sketch, "E986.visualSharp", {"position": v(-602.4, 309.1) * mm});
            skArc(sketch, "E986.filletArc", {"start": v(-602.4, 308.6) * mm, "mid": v(-602.55, 308.95) * mm, "end": v(-602.9, 309.1) * mm});
            skPoint(sketch, "E987.visualSharp", {"position": v(-602.4, 301.1) * mm});
            skArc(sketch, "E987.filletArc", {"start": v(-602.9, 301.1) * mm, "mid": v(-602.55, 301.25) * mm, "end": v(-602.4, 301.6) * mm});
            skPoint(sketch, "E988.visualSharp", {"position": v(-602.4, 290.3) * mm});
            skArc(sketch, "E988.filletArc", {"start": v(-602.4, 289.8) * mm, "mid": v(-602.55, 290.15) * mm, "end": v(-602.9, 290.3) * mm});
            skPoint(sketch, "E989.visualSharp", {"position": v(-602.4, 282.3) * mm});
            skArc(sketch, "E989.filletArc", {"start": v(-602.9, 282.3) * mm, "mid": v(-602.55, 282.45) * mm, "end": v(-602.4, 282.8) * mm});
            skPoint(sketch, "E990.visualSharp", {"position": v(-602.4, 218.4) * mm});
            skArc(sketch, "E990.filletArc", {"start": v(-602.4, 217.9) * mm, "mid": v(-602.55, 218.25) * mm, "end": v(-602.9, 218.4) * mm});
            skPoint(sketch, "E991.visualSharp", {"position": v(-602.4, 199.6) * mm});
            skArc(sketch, "E991.filletArc", {"start": v(-602.4, 199.1) * mm, "mid": v(-602.55, 199.45) * mm, "end": v(-602.9, 199.6) * mm});
            skPoint(sketch, "E992.visualSharp", {"position": v(-602.4, 210.4) * mm});
            skArc(sketch, "E992.filletArc", {"start": v(-602.9, 210.4) * mm, "mid": v(-602.55, 210.55) * mm, "end": v(-602.4, 210.9) * mm});
            skPoint(sketch, "E993.visualSharp", {"position": v(-602.4, 191.6) * mm});
            skArc(sketch, "E993.filletArc", {"start": v(-602.9, 191.6) * mm, "mid": v(-602.55, 191.75) * mm, "end": v(-602.4, 192.1) * mm});
            skPoint(sketch, "E994.visualSharp", {"position": v(-602.4, 127.7) * mm});
            skArc(sketch, "E994.filletArc", {"start": v(-602.4, 127.2) * mm, "mid": v(-602.55, 127.55) * mm, "end": v(-602.9, 127.7) * mm});
            skPoint(sketch, "E995.visualSharp", {"position": v(-602.4, 108.9) * mm});
            skArc(sketch, "E995.filletArc", {"start": v(-602.4, 108.4) * mm, "mid": v(-602.55, 108.75) * mm, "end": v(-602.9, 108.9) * mm});
            skPoint(sketch, "E996.visualSharp", {"position": v(-602.4, 119.7) * mm});
            skArc(sketch, "E996.filletArc", {"start": v(-602.9, 119.7) * mm, "mid": v(-602.55, 119.85) * mm, "end": v(-602.4, 120.2) * mm});
            skPoint(sketch, "E997.visualSharp", {"position": v(-602.4, 100.9) * mm});
            skArc(sketch, "E997.filletArc", {"start": v(-602.9, 100.9) * mm, "mid": v(-602.55, 101.05) * mm, "end": v(-602.4, 101.4) * mm});
            skPoint(sketch, "E998.visualSharp", {"position": v(-588.6, 56.5) * mm});
            skArc(sketch, "E998.filletArc", {"start": v(-588.1, 56.5) * mm, "mid": v(-588.46, 56.35) * mm, "end": v(-588.6, 56) * mm});
            skPoint(sketch, "E999.visualSharp", {"position": v(-569.1, 56.5) * mm});
            skArc(sketch, "E999.filletArc", {"start": v(-568.6, 56.5) * mm, "mid": v(-568.96, 56.35) * mm, "end": v(-569.1, 56) * mm});
            skArc(sketch, "E1000.filletArc", {"start": v(-562.5, 56) * mm, "mid": v(-562.65, 56.35) * mm, "end": v(-563, 56.5) * mm});
            skArc(sketch, "E1001.filletArc", {"start": v(-582, 56) * mm, "mid": v(-582.15, 56.35) * mm, "end": v(-582.5, 56.5) * mm});
            skArc(sketch, "E1002", {"start": v(-562.17, 10.25) * mm, "mid": v(-562, 10.07) * mm, "end": v(-561.74, 10) * mm});
            skArc(sketch, "E1003", {"start": v(-562.17, 10.25) * mm, "mid": v(-562.96, 10.35) * mm, "end": v(-562.86, 9.57) * mm});
            skArc(sketch, "E1004", {"start": v(-562.6, 9.13) * mm, "mid": v(-562.67, 9.38) * mm, "end": v(-562.86, 9.57) * mm});
            skArc(sketch, "E1005", {"start": v(-572.16, 9.57) * mm, "mid": v(-572.34, 9.38) * mm, "end": v(-572.4, 9.13) * mm});
            skArc(sketch, "E1006", {"start": v(-572.16, 9.57) * mm, "mid": v(-572.05, 10.35) * mm, "end": v(-572.84, 10.25) * mm});
            skArc(sketch, "E1007", {"start": v(-573.27, 10) * mm, "mid": v(-573.02, 10.07) * mm, "end": v(-572.84, 10.25) * mm});
            skArc(sketch, "E1008", {"start": v(-542.67, 10.25) * mm, "mid": v(-542.5, 10.07) * mm, "end": v(-542.24, 10) * mm});
            skArc(sketch, "E1009", {"start": v(-542.67, 10.25) * mm, "mid": v(-543.46, 10.35) * mm, "end": v(-543.36, 9.57) * mm});
            skArc(sketch, "E1010", {"start": v(-543.1, 9.13) * mm, "mid": v(-543.17, 9.38) * mm, "end": v(-543.36, 9.57) * mm});
            skArc(sketch, "E1011", {"start": v(-552.66, 9.57) * mm, "mid": v(-552.84, 9.38) * mm, "end": v(-552.9, 9.13) * mm});
            skArc(sketch, "E1012", {"start": v(-552.66, 9.57) * mm, "mid": v(-552.55, 10.35) * mm, "end": v(-553.34, 10.25) * mm});
            skArc(sketch, "E1013", {"start": v(-553.77, 10) * mm, "mid": v(-553.52, 10.07) * mm, "end": v(-553.34, 10.25) * mm});
            skArc(sketch, "E1014", {"start": v(-434.82, 10.25) * mm, "mid": v(-434.64, 10.07) * mm, "end": v(-434.4, 10) * mm});
            skArc(sketch, "E1015", {"start": v(-434.82, 10.25) * mm, "mid": v(-435.6, 10.35) * mm, "end": v(-435.5, 9.57) * mm});
            skArc(sketch, "E1016", {"start": v(-435.26, 9.13) * mm, "mid": v(-435.32, 9.38) * mm, "end": v(-435.5, 9.57) * mm});
            skArc(sketch, "E1017", {"start": v(-444.8, 9.57) * mm, "mid": v(-444.99, 9.38) * mm, "end": v(-445.06, 9.13) * mm});
            skArc(sketch, "E1018", {"start": v(-444.8, 9.57) * mm, "mid": v(-444.7, 10.35) * mm, "end": v(-445.49, 10.25) * mm});
            skArc(sketch, "E1019", {"start": v(-445.92, 10) * mm, "mid": v(-445.67, 10.07) * mm, "end": v(-445.49, 10.25) * mm});
            skArc(sketch, "E1020", {"start": v(-415.32, 10.25) * mm, "mid": v(-415.14, 10.07) * mm, "end": v(-414.9, 10) * mm});
            skArc(sketch, "E1021", {"start": v(-415.32, 10.25) * mm, "mid": v(-416.1, 10.35) * mm, "end": v(-416, 9.57) * mm});
            skArc(sketch, "E1022", {"start": v(-415.76, 9.13) * mm, "mid": v(-415.82, 9.38) * mm, "end": v(-416, 9.57) * mm});
            skArc(sketch, "E1023", {"start": v(-425.3, 9.57) * mm, "mid": v(-425.49, 9.38) * mm, "end": v(-425.56, 9.13) * mm});
            skArc(sketch, "E1024", {"start": v(-425.3, 9.57) * mm, "mid": v(-425.2, 10.35) * mm, "end": v(-425.99, 10.25) * mm});
            skArc(sketch, "E1025", {"start": v(-426.42, 10) * mm, "mid": v(-426.17, 10.07) * mm, "end": v(-425.99, 10.25) * mm});
            skArc(sketch, "E1026", {"start": v(-695.47, 10.25) * mm, "mid": v(-695.3, 10.07) * mm, "end": v(-695.04, 10) * mm});
            skArc(sketch, "E1027", {"start": v(-695.47, 10.25) * mm, "mid": v(-696.26, 10.35) * mm, "end": v(-696.16, 9.57) * mm});
            skArc(sketch, "E1028", {"start": v(-695.9, 9.13) * mm, "mid": v(-695.97, 9.38) * mm, "end": v(-696.16, 9.57) * mm});
            skArc(sketch, "E1029", {"start": v(-705.46, 9.57) * mm, "mid": v(-705.64, 9.38) * mm, "end": v(-705.7, 9.13) * mm});
            skArc(sketch, "E1030", {"start": v(-705.46, 9.57) * mm, "mid": v(-705.35, 10.35) * mm, "end": v(-706.14, 10.25) * mm});
            skArc(sketch, "E1031", {"start": v(-706.57, 10) * mm, "mid": v(-706.32, 10.07) * mm, "end": v(-706.14, 10.25) * mm});
            skArc(sketch, "E1032", {"start": v(-644.47, 10.25) * mm, "mid": v(-644.3, 10.07) * mm, "end": v(-644.04, 10) * mm});
            skArc(sketch, "E1033", {"start": v(-644.47, 10.25) * mm, "mid": v(-645.26, 10.35) * mm, "end": v(-645.16, 9.57) * mm});
            skArc(sketch, "E1034", {"start": v(-644.9, 9.13) * mm, "mid": v(-644.97, 9.38) * mm, "end": v(-645.16, 9.57) * mm});
            skArc(sketch, "E1035", {"start": v(-654.46, 9.57) * mm, "mid": v(-654.64, 9.38) * mm, "end": v(-654.7, 9.13) * mm});
            skArc(sketch, "E1036", {"start": v(-654.46, 9.57) * mm, "mid": v(-654.35, 10.35) * mm, "end": v(-655.14, 10.25) * mm});
            skArc(sketch, "E1037", {"start": v(-655.57, 10) * mm, "mid": v(-655.32, 10.07) * mm, "end": v(-655.14, 10.25) * mm});
            skArc(sketch, "E1038", {"start": v(-714.97, 10.25) * mm, "mid": v(-714.8, 10.07) * mm, "end": v(-714.54, 10) * mm});
            skArc(sketch, "E1039", {"start": v(-714.97, 10.25) * mm, "mid": v(-715.76, 10.35) * mm, "end": v(-715.66, 9.57) * mm});
            skArc(sketch, "E1040", {"start": v(-715.4, 9.13) * mm, "mid": v(-715.47, 9.38) * mm, "end": v(-715.66, 9.57) * mm});
            skArc(sketch, "E1041", {"start": v(-634.96, 9.57) * mm, "mid": v(-635.14, 9.38) * mm, "end": v(-635.2, 9.13) * mm});
            skArc(sketch, "E1042", {"start": v(-634.96, 9.57) * mm, "mid": v(-634.85, 10.35) * mm, "end": v(-635.64, 10.25) * mm});
            skArc(sketch, "E1043", {"start": v(-636.07, 10) * mm, "mid": v(-635.82, 10.07) * mm, "end": v(-635.64, 10.25) * mm});
            skArc(sketch, "E1044", {"start": v(-609.97, 10.25) * mm, "mid": v(-609.8, 10.07) * mm, "end": v(-609.54, 10) * mm});
            skArc(sketch, "E1045", {"start": v(-609.97, 10.25) * mm, "mid": v(-610.76, 10.35) * mm, "end": v(-610.66, 9.57) * mm});
            skArc(sketch, "E1046", {"start": v(-610.4, 9.13) * mm, "mid": v(-610.47, 9.38) * mm, "end": v(-610.66, 9.57) * mm});
            skArc(sketch, "E1047", {"start": v(-737.16, 9.57) * mm, "mid": v(-737.34, 9.38) * mm, "end": v(-737.4, 9.13) * mm});
            skArc(sketch, "E1048", {"start": v(-737.16, 9.57) * mm, "mid": v(-737.05, 10.35) * mm, "end": v(-737.84, 10.25) * mm});
            skArc(sketch, "E1049", {"start": v(-738.27, 10) * mm, "mid": v(-738.02, 10.07) * mm, "end": v(-737.84, 10.25) * mm});
            skArc(sketch, "E1050", {"start": v(-747.16, 24.87) * mm, "mid": v(-747.34, 24.68) * mm, "end": v(-747.4, 24.43) * mm});
            skArc(sketch, "E1051", {"start": v(-747.16, 24.87) * mm, "mid": v(-747.05, 25.65) * mm, "end": v(-747.84, 25.55) * mm});
            skArc(sketch, "E1052", {"start": v(-748.27, 25.3) * mm, "mid": v(-748.02, 25.37) * mm, "end": v(-747.84, 25.55) * mm});
            skArc(sketch, "E1053", {"start": v(-747.84, 45.45) * mm, "mid": v(-748.02, 45.63) * mm, "end": v(-748.27, 45.7) * mm});
            skArc(sketch, "E1054", {"start": v(-747.84, 45.45) * mm, "mid": v(-747.05, 45.35) * mm, "end": v(-747.16, 46.13) * mm});
            skArc(sketch, "E1055", {"start": v(-747.4, 46.57) * mm, "mid": v(-747.34, 46.32) * mm, "end": v(-747.16, 46.13) * mm});
            skArc(sketch, "E1056", {"start": v(-747.16, 56.67) * mm, "mid": v(-747.34, 56.48) * mm, "end": v(-747.4, 56.23) * mm});
            skArc(sketch, "E1057", {"start": v(-747.16, 56.67) * mm, "mid": v(-747.05, 57.45) * mm, "end": v(-747.84, 57.35) * mm});
            skArc(sketch, "E1058", {"start": v(-748.27, 57.1) * mm, "mid": v(-748.02, 57.17) * mm, "end": v(-747.84, 57.35) * mm});
            skArc(sketch, "E1059", {"start": v(-644.84, 430.25) * mm, "mid": v(-645.02, 430.43) * mm, "end": v(-645.27, 430.5) * mm});
            skArc(sketch, "E1060", {"start": v(-644.84, 430.25) * mm, "mid": v(-644.05, 430.15) * mm, "end": v(-644.16, 430.93) * mm});
            skArc(sketch, "E1061", {"start": v(-644.4, 431.37) * mm, "mid": v(-644.34, 431.12) * mm, "end": v(-644.16, 430.93) * mm});
            skArc(sketch, "E1062", {"start": v(-624.66, 430.93) * mm, "mid": v(-624.47, 431.12) * mm, "end": v(-624.4, 431.37) * mm});
            skArc(sketch, "E1063", {"start": v(-624.66, 430.93) * mm, "mid": v(-624.76, 430.15) * mm, "end": v(-623.97, 430.25) * mm});
            skArc(sketch, "E1064", {"start": v(-623.54, 430.5) * mm, "mid": v(-623.8, 430.43) * mm, "end": v(-623.97, 430.25) * mm});
            skArc(sketch, "E1065", {"start": v(-605.66, 419.03) * mm, "mid": v(-605.47, 419.22) * mm, "end": v(-605.4, 419.47) * mm});
            skArc(sketch, "E1066", {"start": v(-605.66, 419.03) * mm, "mid": v(-605.76, 418.25) * mm, "end": v(-604.97, 418.35) * mm});
            skArc(sketch, "E1067", {"start": v(-604.54, 418.6) * mm, "mid": v(-604.8, 418.53) * mm, "end": v(-604.97, 418.35) * mm});
            skArc(sketch, "E1068", {"start": v(-604.97, 410.85) * mm, "mid": v(-604.8, 410.67) * mm, "end": v(-604.54, 410.6) * mm});
            skArc(sketch, "E1069", {"start": v(-604.97, 410.85) * mm, "mid": v(-605.76, 410.95) * mm, "end": v(-605.66, 410.17) * mm});
            skArc(sketch, "E1070", {"start": v(-605.4, 409.73) * mm, "mid": v(-605.47, 409.98) * mm, "end": v(-605.66, 410.17) * mm});
            skArc(sketch, "E1071", {"start": v(-605.66, 400.23) * mm, "mid": v(-605.47, 400.42) * mm, "end": v(-605.4, 400.67) * mm});
            skArc(sketch, "E1072", {"start": v(-605.66, 400.23) * mm, "mid": v(-605.76, 399.45) * mm, "end": v(-604.97, 399.55) * mm});
            skArc(sketch, "E1073", {"start": v(-604.54, 399.8) * mm, "mid": v(-604.8, 399.73) * mm, "end": v(-604.97, 399.55) * mm});
            skArc(sketch, "E1074", {"start": v(-604.97, 392.05) * mm, "mid": v(-604.8, 391.87) * mm, "end": v(-604.54, 391.8) * mm});
            skArc(sketch, "E1075", {"start": v(-604.97, 392.05) * mm, "mid": v(-605.76, 392.15) * mm, "end": v(-605.66, 391.37) * mm});
            skArc(sketch, "E1076", {"start": v(-605.4, 390.93) * mm, "mid": v(-605.47, 391.18) * mm, "end": v(-605.66, 391.37) * mm});
            skArc(sketch, "E1077", {"start": v(-605.66, 381.43) * mm, "mid": v(-605.47, 381.62) * mm, "end": v(-605.4, 381.87) * mm});
            skArc(sketch, "E1078", {"start": v(-605.66, 381.43) * mm, "mid": v(-605.76, 380.65) * mm, "end": v(-604.97, 380.75) * mm});
            skArc(sketch, "E1079", {"start": v(-604.54, 381) * mm, "mid": v(-604.8, 380.93) * mm, "end": v(-604.97, 380.75) * mm});
            skArc(sketch, "E1080", {"start": v(-604.97, 373.25) * mm, "mid": v(-604.8, 373.07) * mm, "end": v(-604.54, 373) * mm});
            skArc(sketch, "E1081", {"start": v(-604.97, 373.25) * mm, "mid": v(-605.76, 373.35) * mm, "end": v(-605.66, 372.57) * mm});
            skArc(sketch, "E1082", {"start": v(-605.4, 372.13) * mm, "mid": v(-605.47, 372.38) * mm, "end": v(-605.66, 372.57) * mm});
            skArc(sketch, "E1083", {"start": v(-605.66, 309.53) * mm, "mid": v(-605.47, 309.72) * mm, "end": v(-605.4, 309.97) * mm});
            skArc(sketch, "E1084", {"start": v(-605.66, 309.53) * mm, "mid": v(-605.76, 308.75) * mm, "end": v(-604.97, 308.85) * mm});
            skArc(sketch, "E1085", {"start": v(-604.54, 309.1) * mm, "mid": v(-604.8, 309.03) * mm, "end": v(-604.97, 308.85) * mm});
            skArc(sketch, "E1086", {"start": v(-604.97, 301.35) * mm, "mid": v(-604.8, 301.17) * mm, "end": v(-604.54, 301.1) * mm});
            skArc(sketch, "E1087", {"start": v(-604.97, 301.35) * mm, "mid": v(-605.76, 301.45) * mm, "end": v(-605.66, 300.67) * mm});
            skArc(sketch, "E1088", {"start": v(-605.4, 300.23) * mm, "mid": v(-605.47, 300.48) * mm, "end": v(-605.66, 300.67) * mm});
            skArc(sketch, "E1089", {"start": v(-605.66, 290.73) * mm, "mid": v(-605.47, 290.92) * mm, "end": v(-605.4, 291.17) * mm});
            skArc(sketch, "E1090", {"start": v(-605.66, 290.73) * mm, "mid": v(-605.76, 289.95) * mm, "end": v(-604.97, 290.05) * mm});
            skArc(sketch, "E1091", {"start": v(-604.54, 290.3) * mm, "mid": v(-604.8, 290.23) * mm, "end": v(-604.97, 290.05) * mm});
            skArc(sketch, "E1092", {"start": v(-604.97, 282.55) * mm, "mid": v(-604.8, 282.37) * mm, "end": v(-604.54, 282.3) * mm});
            skArc(sketch, "E1093", {"start": v(-604.97, 282.55) * mm, "mid": v(-605.76, 282.65) * mm, "end": v(-605.66, 281.87) * mm});
            skArc(sketch, "E1094", {"start": v(-605.4, 281.43) * mm, "mid": v(-605.47, 281.68) * mm, "end": v(-605.66, 281.87) * mm});
            skArc(sketch, "E1095", {"start": v(-605.66, 218.83) * mm, "mid": v(-605.47, 219.02) * mm, "end": v(-605.4, 219.27) * mm});
            skArc(sketch, "E1096", {"start": v(-605.66, 218.83) * mm, "mid": v(-605.76, 218.05) * mm, "end": v(-604.97, 218.15) * mm});
            skArc(sketch, "E1097", {"start": v(-604.54, 218.4) * mm, "mid": v(-604.8, 218.33) * mm, "end": v(-604.97, 218.15) * mm});
            skArc(sketch, "E1098", {"start": v(-604.97, 210.65) * mm, "mid": v(-604.8, 210.47) * mm, "end": v(-604.54, 210.4) * mm});
            skArc(sketch, "E1099", {"start": v(-604.97, 210.65) * mm, "mid": v(-605.76, 210.75) * mm, "end": v(-605.66, 209.97) * mm});
            skArc(sketch, "E1100", {"start": v(-605.4, 209.53) * mm, "mid": v(-605.47, 209.78) * mm, "end": v(-605.66, 209.97) * mm});
            skArc(sketch, "E1101", {"start": v(-605.66, 200.03) * mm, "mid": v(-605.47, 200.22) * mm, "end": v(-605.4, 200.47) * mm});
            skArc(sketch, "E1102", {"start": v(-605.66, 200.03) * mm, "mid": v(-605.76, 199.25) * mm, "end": v(-604.97, 199.35) * mm});
            skArc(sketch, "E1103", {"start": v(-604.54, 199.6) * mm, "mid": v(-604.8, 199.53) * mm, "end": v(-604.97, 199.35) * mm});
            skArc(sketch, "E1104", {"start": v(-604.97, 191.85) * mm, "mid": v(-604.8, 191.67) * mm, "end": v(-604.54, 191.6) * mm});
            skArc(sketch, "E1105", {"start": v(-604.97, 191.85) * mm, "mid": v(-605.76, 191.95) * mm, "end": v(-605.66, 191.17) * mm});
            skArc(sketch, "E1106", {"start": v(-605.4, 190.73) * mm, "mid": v(-605.47, 190.98) * mm, "end": v(-605.66, 191.17) * mm});
            skArc(sketch, "E1107", {"start": v(-605.66, 128.13) * mm, "mid": v(-605.47, 128.32) * mm, "end": v(-605.4, 128.57) * mm});
            skArc(sketch, "E1108", {"start": v(-605.66, 128.13) * mm, "mid": v(-605.76, 127.35) * mm, "end": v(-604.97, 127.45) * mm});
            skArc(sketch, "E1109", {"start": v(-604.54, 127.7) * mm, "mid": v(-604.8, 127.63) * mm, "end": v(-604.97, 127.45) * mm});
            skArc(sketch, "E1110", {"start": v(-604.97, 119.95) * mm, "mid": v(-604.8, 119.77) * mm, "end": v(-604.54, 119.7) * mm});
            skArc(sketch, "E1111", {"start": v(-604.97, 119.95) * mm, "mid": v(-605.76, 120.05) * mm, "end": v(-605.66, 119.27) * mm});
            skArc(sketch, "E1112", {"start": v(-605.4, 118.83) * mm, "mid": v(-605.47, 119.08) * mm, "end": v(-605.66, 119.27) * mm});
            skArc(sketch, "E1113", {"start": v(-605.66, 109.33) * mm, "mid": v(-605.47, 109.52) * mm, "end": v(-605.4, 109.77) * mm});
            skArc(sketch, "E1114", {"start": v(-605.66, 109.33) * mm, "mid": v(-605.76, 108.55) * mm, "end": v(-604.97, 108.65) * mm});
            skArc(sketch, "E1115", {"start": v(-604.54, 108.9) * mm, "mid": v(-604.8, 108.83) * mm, "end": v(-604.97, 108.65) * mm});
            skArc(sketch, "E1116", {"start": v(-604.97, 101.15) * mm, "mid": v(-604.8, 100.97) * mm, "end": v(-604.54, 100.9) * mm});
            skArc(sketch, "E1117", {"start": v(-604.97, 101.15) * mm, "mid": v(-605.76, 101.25) * mm, "end": v(-605.66, 100.47) * mm});
            skArc(sketch, "E1118", {"start": v(-605.4, 100.03) * mm, "mid": v(-605.47, 100.28) * mm, "end": v(-605.66, 100.47) * mm});
            skArc(sketch, "E1119", {"start": v(-569.54, 53.25) * mm, "mid": v(-569.72, 53.43) * mm, "end": v(-569.97, 53.5) * mm});
            skArc(sketch, "E1120", {"start": v(-569.54, 53.25) * mm, "mid": v(-568.75, 53.15) * mm, "end": v(-568.86, 53.93) * mm});
            skArc(sketch, "E1121", {"start": v(-569.1, 54.37) * mm, "mid": v(-569.04, 54.12) * mm, "end": v(-568.86, 53.93) * mm});
            skArc(sketch, "E1122", {"start": v(-562.76, 53.93) * mm, "mid": v(-562.57, 54.12) * mm, "end": v(-562.5, 54.37) * mm});
            skArc(sketch, "E1123", {"start": v(-562.76, 53.93) * mm, "mid": v(-562.86, 53.15) * mm, "end": v(-562.07, 53.25) * mm});
            skArc(sketch, "E1124", {"start": v(-561.64, 53.5) * mm, "mid": v(-561.9, 53.43) * mm, "end": v(-562.07, 53.25) * mm});
            skArc(sketch, "E1125", {"start": v(-373.66, 34.78) * mm, "mid": v(-373.47, 34.97) * mm, "end": v(-373.4, 35.22) * mm});
            skArc(sketch, "E1126", {"start": v(-373.66, 34.78) * mm, "mid": v(-373.76, 34) * mm, "end": v(-372.97, 34.1) * mm});
            skArc(sketch, "E1127", {"start": v(-372.54, 34.35) * mm, "mid": v(-372.8, 34.28) * mm, "end": v(-372.97, 34.1) * mm});
            skArc(sketch, "E1128", {"start": v(-372.97, 28.6) * mm, "mid": v(-372.8, 28.42) * mm, "end": v(-372.54, 28.35) * mm});
            skArc(sketch, "E1129", {"start": v(-372.97, 28.6) * mm, "mid": v(-373.76, 28.7) * mm, "end": v(-373.66, 27.92) * mm});
            skArc(sketch, "E1130", {"start": v(-373.4, 27.48) * mm, "mid": v(-373.47, 27.73) * mm, "end": v(-373.66, 27.92) * mm});
            skArc(sketch, "E1131", {"start": v(-373.66, 19.08) * mm, "mid": v(-373.47, 19.27) * mm, "end": v(-373.4, 19.52) * mm});
            skArc(sketch, "E1132", {"start": v(-373.66, 19.08) * mm, "mid": v(-373.76, 18.3) * mm, "end": v(-372.97, 18.4) * mm});
            skArc(sketch, "E1133", {"start": v(-372.54, 18.65) * mm, "mid": v(-372.8, 18.58) * mm, "end": v(-372.97, 18.4) * mm});
            skArc(sketch, "E1134", {"start": v(-372.97, 12.9) * mm, "mid": v(-372.8, 12.72) * mm, "end": v(-372.54, 12.65) * mm});
            skArc(sketch, "E1135", {"start": v(-372.97, 12.9) * mm, "mid": v(-373.76, 13) * mm, "end": v(-373.66, 12.22) * mm});
            skArc(sketch, "E1136", {"start": v(-373.4, 11.78) * mm, "mid": v(-373.47, 12.03) * mm, "end": v(-373.66, 12.22) * mm});
            skArc(sketch, "E1137", {"start": v(-589.04, 53.25) * mm, "mid": v(-589.22, 53.43) * mm, "end": v(-589.47, 53.5) * mm});
            skArc(sketch, "E1138", {"start": v(-589.04, 53.25) * mm, "mid": v(-588.25, 53.15) * mm, "end": v(-588.36, 53.93) * mm});
            skArc(sketch, "E1139", {"start": v(-588.6, 54.37) * mm, "mid": v(-588.54, 54.12) * mm, "end": v(-588.36, 53.93) * mm});
            skArc(sketch, "E1140", {"start": v(-582.26, 53.93) * mm, "mid": v(-582.07, 54.12) * mm, "end": v(-582, 54.37) * mm});
            skArc(sketch, "E1141", {"start": v(-582.26, 53.93) * mm, "mid": v(-582.36, 53.15) * mm, "end": v(-581.57, 53.25) * mm});
            skArc(sketch, "E1142", {"start": v(-581.14, 53.5) * mm, "mid": v(-581.4, 53.43) * mm, "end": v(-581.57, 53.25) * mm});
            skArc(sketch, "E1143.filletArc", {"start": v(-547.4, 39) * mm, "mid": v(-546.82, 37.59) * mm, "end": v(-545.4, 37) * mm});
            skArc(sketch, "E1144", {"start": v(-307.93, 10.37) * mm, "mid": v(-308.12, 10.18) * mm, "end": v(-308.18, 9.93) * mm});
            skArc(sketch, "E1145", {"start": v(-307.93, 10.37) * mm, "mid": v(-307.83, 11.15) * mm, "end": v(-308.62, 11.05) * mm});
            skArc(sketch, "E1146", {"start": v(-309.05, 10.8) * mm, "mid": v(-308.8, 10.87) * mm, "end": v(-308.62, 11.05) * mm});
            skArc(sketch, "E1147", {"start": v(-308.62, 18.55) * mm, "mid": v(-308.8, 18.73) * mm, "end": v(-309.05, 18.8) * mm});
            skArc(sketch, "E1148", {"start": v(-308.62, 18.55) * mm, "mid": v(-307.83, 18.45) * mm, "end": v(-307.93, 19.23) * mm});
            skArc(sketch, "E1149", {"start": v(-308.18, 19.67) * mm, "mid": v(-308.12, 19.42) * mm, "end": v(-307.93, 19.23) * mm});
            skArc(sketch, "E1150", {"start": v(-307.93, 27.77) * mm, "mid": v(-308.12, 27.58) * mm, "end": v(-308.18, 27.33) * mm});
            skArc(sketch, "E1151", {"start": v(-307.93, 27.77) * mm, "mid": v(-307.83, 28.55) * mm, "end": v(-308.62, 28.45) * mm});
            skArc(sketch, "E1152", {"start": v(-309.05, 28.2) * mm, "mid": v(-308.8, 28.27) * mm, "end": v(-308.62, 28.45) * mm});
            skArc(sketch, "E1153", {"start": v(-308.62, 35.95) * mm, "mid": v(-308.8, 36.13) * mm, "end": v(-309.05, 36.2) * mm});
            skArc(sketch, "E1154", {"start": v(-308.62, 35.95) * mm, "mid": v(-307.83, 35.85) * mm, "end": v(-307.93, 36.63) * mm});
            skArc(sketch, "E1155", {"start": v(-308.18, 37.07) * mm, "mid": v(-308.12, 36.82) * mm, "end": v(-307.93, 36.63) * mm});
            skArc(sketch, "E1156", {"start": v(-307.93, 109.77) * mm, "mid": v(-308.12, 109.58) * mm, "end": v(-308.18, 109.33) * mm});
            skArc(sketch, "E1157", {"start": v(-307.93, 109.77) * mm, "mid": v(-307.83, 110.55) * mm, "end": v(-308.62, 110.45) * mm});
            skArc(sketch, "E1158", {"start": v(-309.05, 110.2) * mm, "mid": v(-308.8, 110.27) * mm, "end": v(-308.62, 110.45) * mm});
            skArc(sketch, "E1159", {"start": v(-308.62, 119.75) * mm, "mid": v(-308.8, 119.93) * mm, "end": v(-309.05, 120) * mm});
            skArc(sketch, "E1160", {"start": v(-308.62, 119.75) * mm, "mid": v(-307.83, 119.65) * mm, "end": v(-307.93, 120.43) * mm});
            skArc(sketch, "E1161", {"start": v(-308.18, 120.87) * mm, "mid": v(-308.12, 120.62) * mm, "end": v(-307.93, 120.43) * mm});
            skArc(sketch, "E1162", {"start": v(-307.93, 137.17) * mm, "mid": v(-308.12, 136.98) * mm, "end": v(-308.18, 136.73) * mm});
            skArc(sketch, "E1163", {"start": v(-307.93, 137.17) * mm, "mid": v(-307.83, 137.95) * mm, "end": v(-308.62, 137.85) * mm});
            skArc(sketch, "E1164", {"start": v(-309.05, 137.6) * mm, "mid": v(-308.8, 137.67) * mm, "end": v(-308.62, 137.85) * mm});
            skArc(sketch, "E1165", {"start": v(-308.62, 147.15) * mm, "mid": v(-308.8, 147.33) * mm, "end": v(-309.05, 147.4) * mm});
            skArc(sketch, "E1166", {"start": v(-308.62, 147.15) * mm, "mid": v(-307.83, 147.05) * mm, "end": v(-307.93, 147.83) * mm});
            skArc(sketch, "E1167", {"start": v(-308.18, 148.27) * mm, "mid": v(-308.12, 148.02) * mm, "end": v(-307.93, 147.83) * mm});
            skArc(sketch, "E1168", {"start": v(-298.02, 53.25) * mm, "mid": v(-298.2, 53.43) * mm, "end": v(-298.45, 53.5) * mm});
            skArc(sketch, "E1169", {"start": v(-298.02, 53.25) * mm, "mid": v(-297.23, 53.15) * mm, "end": v(-297.33, 53.93) * mm});
            skArc(sketch, "E1170", {"start": v(-297.58, 54.37) * mm, "mid": v(-297.52, 54.12) * mm, "end": v(-297.33, 53.93) * mm});
            skArc(sketch, "E1171", {"start": v(-288.03, 53.93) * mm, "mid": v(-287.85, 54.12) * mm, "end": v(-287.78, 54.37) * mm});
            skArc(sketch, "E1172", {"start": v(-288.03, 53.93) * mm, "mid": v(-288.14, 53.15) * mm, "end": v(-287.35, 53.25) * mm});
            skArc(sketch, "E1173", {"start": v(-286.92, 53.5) * mm, "mid": v(-287.17, 53.43) * mm, "end": v(-287.35, 53.25) * mm});
            skArc(sketch, "E1174", {"start": v(-278.52, 53.25) * mm, "mid": v(-278.7, 53.43) * mm, "end": v(-278.95, 53.5) * mm});
            skArc(sketch, "E1175", {"start": v(-278.52, 53.25) * mm, "mid": v(-277.73, 53.15) * mm, "end": v(-277.83, 53.93) * mm});
            skArc(sketch, "E1176", {"start": v(-278.08, 54.37) * mm, "mid": v(-278.02, 54.12) * mm, "end": v(-277.83, 53.93) * mm});
            skArc(sketch, "E1177", {"start": v(-268.53, 53.93) * mm, "mid": v(-268.35, 54.12) * mm, "end": v(-268.28, 54.37) * mm});
            skArc(sketch, "E1178", {"start": v(-268.53, 53.93) * mm, "mid": v(-268.64, 53.15) * mm, "end": v(-267.85, 53.25) * mm});
            skArc(sketch, "E1179", {"start": v(-267.42, 53.5) * mm, "mid": v(-267.67, 53.43) * mm, "end": v(-267.85, 53.25) * mm});
            skPoint(sketch, "E1180.visualSharp", {"position": v(-278.08, 56.5) * mm});
            skArc(sketch, "E1180.filletArc", {"start": v(-277.58, 56.5) * mm, "mid": v(-277.94, 56.35) * mm, "end": v(-278.08, 56) * mm});
            skPoint(sketch, "E1181.visualSharp", {"position": v(-287.78, 56.5) * mm});
            skArc(sketch, "E1181.filletArc", {"start": v(-287.78, 56) * mm, "mid": v(-287.93, 56.35) * mm, "end": v(-288.28, 56.5) * mm});
            skPoint(sketch, "E1182.visualSharp", {"position": v(-268.28, 56.5) * mm});
            skArc(sketch, "E1182.filletArc", {"start": v(-268.28, 56) * mm, "mid": v(-268.43, 56.35) * mm, "end": v(-268.78, 56.5) * mm});
            skPoint(sketch, "E1183.visualSharp", {"position": v(-297.58, 56.5) * mm});
            skArc(sketch, "E1183.filletArc", {"start": v(-297.08, 56.5) * mm, "mid": v(-297.44, 56.35) * mm, "end": v(-297.58, 56) * mm});
            skPoint(sketch, "E1184.visualSharp", {"position": v(-311.18, 120) * mm});
            skArc(sketch, "E1184.filletArc", {"start": v(-310.68, 120) * mm, "mid": v(-311.04, 119.85) * mm, "end": v(-311.18, 119.5) * mm});
            skPoint(sketch, "E1185.visualSharp", {"position": v(-311.18, 110.2) * mm});
            skArc(sketch, "E1185.filletArc", {"start": v(-311.18, 110.7) * mm, "mid": v(-311.04, 110.35) * mm, "end": v(-310.68, 110.2) * mm});
            skPoint(sketch, "E1186.visualSharp", {"position": v(-311.18, 147.4) * mm});
            skArc(sketch, "E1186.filletArc", {"start": v(-310.68, 147.4) * mm, "mid": v(-311.04, 147.25) * mm, "end": v(-311.18, 146.9) * mm});
            skPoint(sketch, "E1187.visualSharp", {"position": v(-311.18, 137.6) * mm});
            skArc(sketch, "E1187.filletArc", {"start": v(-311.18, 138.1) * mm, "mid": v(-311.04, 137.75) * mm, "end": v(-310.68, 137.6) * mm});
            skPoint(sketch, "E1188.visualSharp", {"position": v(-276.18, -2) * mm});
            skArc(sketch, "E1188.filletArc", {"start": v(-276.18, -2.5) * mm, "mid": v(-276.33, -2.14) * mm, "end": v(-276.68, -2) * mm});
            skPoint(sketch, "E1189.visualSharp", {"position": v(-311.18, 10.8) * mm});
            skArc(sketch, "E1189.filletArc", {"start": v(-311.18, 11.3) * mm, "mid": v(-311.04, 10.95) * mm, "end": v(-310.68, 10.8) * mm});
            skPoint(sketch, "E1190.visualSharp", {"position": v(-311.18, 18.8) * mm});
            skArc(sketch, "E1190.filletArc", {"start": v(-310.68, 18.8) * mm, "mid": v(-311.04, 18.65) * mm, "end": v(-311.18, 18.3) * mm});
            skPoint(sketch, "E1191.visualSharp", {"position": v(-311.18, 28.2) * mm});
            skArc(sketch, "E1191.filletArc", {"start": v(-311.18, 28.7) * mm, "mid": v(-311.04, 28.35) * mm, "end": v(-310.68, 28.2) * mm});
            skPoint(sketch, "E1192.visualSharp", {"position": v(-311.18, 36.2) * mm});
            skArc(sketch, "E1192.filletArc", {"start": v(-310.68, 36.2) * mm, "mid": v(-311.04, 36.05) * mm, "end": v(-311.18, 35.7) * mm});
            skPoint(sketch, "E1193.visualSharp", {"position": v(-137, 47.12) * mm});
            skArc(sketch, "E1193.filletArc", {"start": v(-137, 52.12) * mm, "mid": v(-135.54, 48.59) * mm, "end": v(-132, 47.12) * mm});
            skPoint(sketch, "E1194.visualSharp", {"position": v(137, 47.12) * mm});
            skArc(sketch, "E1194.filletArc", {"start": v(132, 47.12) * mm, "mid": v(135.54, 48.59) * mm, "end": v(137, 52.12) * mm});
            skCircle(sketch, "E1195.cCircle", {"center": v(-196.2, 387.18) * mm, "radius": 12.3 * mm, "construction": true});
            skLineSegment(sketch, "E1195.0", {"start": v(-208.5, 371.08) * mm, "end": v(-208.5, 403.3) * mm});
            skLineSegment(sketch, "E1195.1", {"start": v(-204, 405.9) * mm, "end": v(-176.1, 389.78) * mm});
            skLineSegment(sketch, "E1195.2", {"start": v(-176.1, 384.59) * mm, "end": v(-204, 368.48) * mm});
            skPoint(sketch, "E1195.0.midPoint", {"position": v(-208.5, 387.18) * mm});
            skPoint(sketch, "E1196.visualSharp", {"position": v(-171.6, 387.18) * mm});
            skArc(sketch, "E1196.filletArc", {"start": v(-176.1, 384.59) * mm, "mid": v(-174.6, 387.18) * mm, "end": v(-176.1, 389.78) * mm});
            skPoint(sketch, "E1197.visualSharp", {"position": v(-208.5, 365.88) * mm});
            skArc(sketch, "E1197.filletArc", {"start": v(-208.5, 371.08) * mm, "mid": v(-207, 368.48) * mm, "end": v(-204, 368.48) * mm});
            skPoint(sketch, "E1198.visualSharp", {"position": v(-208.5, 408.49) * mm});
            skArc(sketch, "E1198.filletArc", {"start": v(-204, 405.9) * mm, "mid": v(-207, 405.9) * mm, "end": v(-208.5, 403.3) * mm});
            skLineSegment(sketch, "E1199", {"start": v(332.58, 365.88) * mm, "end": v(-286.85, 365.88) * mm, "construction": true});
            skCircle(sketch, "E1200.cCircle", {"center": v(196.2, 387.18) * mm, "radius": 12.3 * mm, "construction": true});
            skLineSegment(sketch, "E1200.0", {"start": v(208.5, 403.3) * mm, "end": v(208.5, 371.08) * mm});
            skLineSegment(sketch, "E1200.1", {"start": v(204, 368.48) * mm, "end": v(176.1, 384.59) * mm});
            skLineSegment(sketch, "E1200.2", {"start": v(176.1, 389.78) * mm, "end": v(204, 405.9) * mm});
            skPoint(sketch, "E1200.0.midPoint", {"position": v(208.5, 387.18) * mm});
            skArc(sketch, "E1201.filletArc", {"start": v(176.1, 389.78) * mm, "mid": v(174.6, 387.18) * mm, "end": v(176.1, 384.59) * mm});
            skPoint(sketch, "E1202.visualSharp", {"position": v(208.5, 408.49) * mm});
            skArc(sketch, "E1202.filletArc", {"start": v(208.5, 403.3) * mm, "mid": v(207, 405.9) * mm, "end": v(204, 405.9) * mm});
            skPoint(sketch, "E1203.visualSharp", {"position": v(208.5, 365.88) * mm});
            skArc(sketch, "E1203.filletArc", {"start": v(204, 368.48) * mm, "mid": v(207, 368.48) * mm, "end": v(208.5, 371.08) * mm});
            skLineSegment(sketch, "E1204", {"start": v(-750.4, 61.9) * mm, "end": v(-659.9, 430.5) * mm});
            skArc(sketch, "E1205", {"start": v(-602.66, 53.93) * mm, "mid": v(-602.47, 54.12) * mm, "end": v(-602.4, 54.37) * mm});
            skArc(sketch, "E1206", {"start": v(-602.66, 53.93) * mm, "mid": v(-602.76, 53.15) * mm, "end": v(-601.97, 53.25) * mm});
            skArc(sketch, "E1207", {"start": v(-601.54, 53.5) * mm, "mid": v(-601.8, 53.43) * mm, "end": v(-601.97, 53.25) * mm});
            skArc(sketch, "E1208", {"start": v(-605.66, 56.93) * mm, "mid": v(-605.47, 57.12) * mm, "end": v(-605.4, 57.37) * mm});
            skArc(sketch, "E1209", {"start": v(-605.66, 56.93) * mm, "mid": v(-605.76, 56.15) * mm, "end": v(-604.97, 56.25) * mm});
            skArc(sketch, "E1210", {"start": v(-604.54, 56.5) * mm, "mid": v(-604.8, 56.43) * mm, "end": v(-604.97, 56.25) * mm});
            skArc(sketch, "E1211", {"start": v(-605.16, 9.57) * mm, "mid": v(-605.34, 9.38) * mm, "end": v(-605.4, 9.13) * mm});
            skArc(sketch, "E1212", {"start": v(-605.16, 9.57) * mm, "mid": v(-605.05, 10.35) * mm, "end": v(-605.84, 10.25) * mm});
            skArc(sketch, "E1213", {"start": v(-606.27, 10) * mm, "mid": v(-606.02, 10.07) * mm, "end": v(-605.84, 10.25) * mm});
            skArc(sketch, "E1214", {"start": v(-601.97, 10.25) * mm, "mid": v(-601.8, 10.07) * mm, "end": v(-601.54, 10) * mm});
            skArc(sketch, "E1215", {"start": v(-601.97, 10.25) * mm, "mid": v(-602.76, 10.35) * mm, "end": v(-602.66, 9.57) * mm});
            skArc(sketch, "E1216", {"start": v(-602.4, 9.13) * mm, "mid": v(-602.47, 9.38) * mm, "end": v(-602.66, 9.57) * mm});
            skPoint(sketch, "E1217.visualSharp", {"position": v(-605.4, 7) * mm});
            skArc(sketch, "E1217.filletArc", {"start": v(-605.4, 7.5) * mm, "mid": v(-605.26, 7.15) * mm, "end": v(-604.9, 7) * mm});
            skArc(sketch, "E1218.filletArc", {"start": v(-602.9, 7) * mm, "mid": v(-602.55, 7.15) * mm, "end": v(-602.4, 7.5) * mm});
            skPoint(sketch, "E1219.visualSharp", {"position": v(-602.4, 56.5) * mm});
            skArc(sketch, "E1219.filletArc", {"start": v(-602.4, 56) * mm, "mid": v(-602.55, 56.35) * mm, "end": v(-602.9, 56.5) * mm});
            skLineSegment(sketch, "E1220", {"start": v(-4, 23.5) * mm, "end": v(4, 23.5) * mm});
            skPoint(sketch, "E1221", {"position": v(0, 23.5) * mm});
            skLineSegment(sketch, "E1222", {"start": v(-4, 7) * mm, "end": v(4, 7) * mm});
            skPoint(sketch, "E1223", {"position": v(0, 7) * mm});
            skLineSegment(sketch, "E1224", {"start": v(-4.5, 24) * mm, "end": v(-4.5, 28) * mm});
            skLineSegment(sketch, "E1225", {"start": v(-4.5, 7.5) * mm, "end": v(-4.5, 9.13) * mm});
            skLineSegment(sketch, "E1226", {"start": v(4.5, 7.5) * mm, "end": v(4.5, 9.13) * mm});
            skLineSegment(sketch, "E1227", {"start": v(4.5, 24) * mm, "end": v(4.5, 28) * mm});
            skLineSegment(sketch, "E1228.trimOffspring", {"start": v(5, 28.5) * mm, "end": v(17, 28.5) * mm});
            skLineSegment(sketch, "E1229.trimOffspring", {"start": v(-5.37, 10) * mm, "end": v(-27.48, 10) * mm});
            skPoint(sketch, "E1230.visualSharp", {"position": v(-4.5, 28.5) * mm});
            skArc(sketch, "E1230.filletArc", {"start": v(-4.5, 28) * mm, "mid": v(-4.65, 28.35) * mm, "end": v(-5, 28.5) * mm});
            skPoint(sketch, "E1231.visualSharp", {"position": v(-4.5, 23.5) * mm});
            skArc(sketch, "E1231.filletArc", {"start": v(-4.5, 24) * mm, "mid": v(-4.35, 23.65) * mm, "end": v(-4, 23.5) * mm});
            skPoint(sketch, "E1232.visualSharp", {"position": v(4.5, 23.5) * mm});
            skArc(sketch, "E1232.filletArc", {"start": v(4, 23.5) * mm, "mid": v(4.35, 23.65) * mm, "end": v(4.5, 24) * mm});
            skPoint(sketch, "E1233.visualSharp", {"position": v(4.5, 28.5) * mm});
            skArc(sketch, "E1233.filletArc", {"start": v(5, 28.5) * mm, "mid": v(4.65, 28.35) * mm, "end": v(4.5, 28) * mm});
            skPoint(sketch, "E1234.visualSharp", {"position": v(4.5, 7) * mm});
            skArc(sketch, "E1234.filletArc", {"start": v(4, 7) * mm, "mid": v(4.35, 7.15) * mm, "end": v(4.5, 7.5) * mm});
            skPoint(sketch, "E1235.visualSharp", {"position": v(-4.5, 7) * mm});
            skArc(sketch, "E1235.filletArc", {"start": v(-4.5, 7.5) * mm, "mid": v(-4.35, 7.15) * mm, "end": v(-4, 7) * mm});
            skArc(sketch, "E1236", {"start": v(4.93, 10.25) * mm, "mid": v(5.12, 10.07) * mm, "end": v(5.37, 10) * mm});
            skArc(sketch, "E1237", {"start": v(4.93, 10.25) * mm, "mid": v(4.15, 10.35) * mm, "end": v(4.25, 9.57) * mm});
            skArc(sketch, "E1238", {"start": v(4.5, 9.13) * mm, "mid": v(4.43, 9.38) * mm, "end": v(4.25, 9.57) * mm});
            skArc(sketch, "E1239", {"start": v(-4.25, 9.57) * mm, "mid": v(-4.43, 9.38) * mm, "end": v(-4.5, 9.13) * mm});
            skArc(sketch, "E1240", {"start": v(-4.25, 9.57) * mm, "mid": v(-4.15, 10.35) * mm, "end": v(-4.93, 10.25) * mm});
            skArc(sketch, "E1241", {"start": v(-5.37, 10) * mm, "mid": v(-5.12, 10.07) * mm, "end": v(-4.93, 10.25) * mm});
            skArc(sketch, "E1242", {"start": v(-176.9, 581.49) * mm, "mid": v(-176.97, 581.74) * mm, "end": v(-177.15, 581.92) * mm});
            skArc(sketch, "E1243", {"start": v(-176.47, 582.6) * mm, "mid": v(-177.25, 582.7) * mm, "end": v(-177.15, 581.92) * mm});
            skArc(sketch, "E1244", {"start": v(-176.47, 582.6) * mm, "mid": v(-176.28, 582.42) * mm, "end": v(-176.03, 582.36) * mm});
            skPoint(sketch, "E1245.visualSharp", {"position": v(-308.18, 53.5) * mm});
            skArc(sketch, "E1245.filletArc", {"start": v(-307.68, 53.5) * mm, "mid": v(-308.04, 53.35) * mm, "end": v(-308.18, 53) * mm});
            skLineSegment(sketch, "E1246", {"start": v(-373.4, 25.25) * mm, "end": v(-377.7, 25.25) * mm});
            skLineSegment(sketch, "E1247", {"start": v(-377.7, 25.25) * mm, "end": v(-377.7, 26.5) * mm});
            skLineSegment(sketch, "E1248", {"start": v(-377.7, 26.5) * mm, "end": v(-382.7, 26.5) * mm});
            skLineSegment(sketch, "E1249", {"start": v(-382.7, 26.5) * mm, "end": v(-382.7, 25.25) * mm});
            skLineSegment(sketch, "E1250", {"start": v(-382.7, 25.25) * mm, "end": v(-385.4, 25.25) * mm});
            skLineSegment(sketch, "E1251", {"start": v(-385.4, 25.25) * mm, "end": v(-385.4, 21.75) * mm});
            skLineSegment(sketch, "E1252", {"start": v(-385.4, 21.75) * mm, "end": v(-382.7, 21.75) * mm});
            skLineSegment(sketch, "E1253", {"start": v(-382.7, 21.75) * mm, "end": v(-382.7, 20.5) * mm});
            skLineSegment(sketch, "E1254", {"start": v(-382.7, 20.5) * mm, "end": v(-377.7, 20.5) * mm});
            skLineSegment(sketch, "E1255", {"start": v(-377.7, 20.5) * mm, "end": v(-377.7, 21.75) * mm});
            skLineSegment(sketch, "E1256", {"start": v(-377.7, 21.75) * mm, "end": v(-373.4, 21.75) * mm});
            skLineSegment(sketch, "E1257", {"start": v(-605.4, 406.95) * mm, "end": v(-609.7, 406.95) * mm});
            skLineSegment(sketch, "E1258", {"start": v(-609.7, 406.95) * mm, "end": v(-609.7, 408.2) * mm});
            skLineSegment(sketch, "E1259", {"start": v(-609.7, 408.2) * mm, "end": v(-614.7, 408.2) * mm});
            skLineSegment(sketch, "E1260", {"start": v(-614.7, 408.2) * mm, "end": v(-614.7, 406.95) * mm});
            skLineSegment(sketch, "E1261", {"start": v(-614.7, 406.95) * mm, "end": v(-617.4, 406.95) * mm});
            skLineSegment(sketch, "E1262", {"start": v(-617.4, 406.95) * mm, "end": v(-617.4, 403.45) * mm});
            skLineSegment(sketch, "E1263", {"start": v(-617.4, 403.45) * mm, "end": v(-614.7, 403.45) * mm});
            skLineSegment(sketch, "E1264", {"start": v(-614.7, 403.45) * mm, "end": v(-614.7, 402.2) * mm});
            skLineSegment(sketch, "E1265", {"start": v(-614.7, 402.2) * mm, "end": v(-609.7, 402.2) * mm});
            skLineSegment(sketch, "E1266", {"start": v(-609.7, 402.2) * mm, "end": v(-609.7, 403.45) * mm});
            skLineSegment(sketch, "E1267", {"start": v(-609.7, 403.45) * mm, "end": v(-605.4, 403.45) * mm});
            skLineSegment(sketch, "E1268", {"start": v(-605.4, 388.15) * mm, "end": v(-609.7, 388.15) * mm});
            skLineSegment(sketch, "E1269", {"start": v(-609.7, 388.15) * mm, "end": v(-609.7, 389.4) * mm});
            skLineSegment(sketch, "E1270", {"start": v(-609.7, 389.4) * mm, "end": v(-614.7, 389.4) * mm});
            skLineSegment(sketch, "E1271", {"start": v(-614.7, 389.4) * mm, "end": v(-614.7, 388.15) * mm});
            skLineSegment(sketch, "E1272", {"start": v(-614.7, 388.15) * mm, "end": v(-617.4, 388.15) * mm});
            skLineSegment(sketch, "E1273", {"start": v(-617.4, 388.15) * mm, "end": v(-617.4, 384.65) * mm});
            skLineSegment(sketch, "E1274", {"start": v(-617.4, 384.65) * mm, "end": v(-614.7, 384.65) * mm});
            skLineSegment(sketch, "E1275", {"start": v(-614.7, 384.65) * mm, "end": v(-614.7, 383.4) * mm});
            skLineSegment(sketch, "E1276", {"start": v(-614.7, 383.4) * mm, "end": v(-609.7, 383.4) * mm});
            skLineSegment(sketch, "E1277", {"start": v(-609.7, 383.4) * mm, "end": v(-609.7, 384.65) * mm});
            skLineSegment(sketch, "E1278", {"start": v(-609.7, 384.65) * mm, "end": v(-605.4, 384.65) * mm});
            skLineSegment(sketch, "E1279", {"start": v(-605.4, 297.45) * mm, "end": v(-609.7, 297.45) * mm});
            skLineSegment(sketch, "E1280", {"start": v(-609.7, 297.45) * mm, "end": v(-609.7, 298.7) * mm});
            skLineSegment(sketch, "E1281", {"start": v(-609.7, 298.7) * mm, "end": v(-614.7, 298.7) * mm});
            skLineSegment(sketch, "E1282", {"start": v(-614.7, 298.7) * mm, "end": v(-614.7, 297.45) * mm});
            skLineSegment(sketch, "E1283", {"start": v(-614.7, 297.45) * mm, "end": v(-617.4, 297.45) * mm});
            skLineSegment(sketch, "E1284", {"start": v(-617.4, 297.45) * mm, "end": v(-617.4, 293.95) * mm});
            skLineSegment(sketch, "E1285", {"start": v(-617.4, 293.95) * mm, "end": v(-614.7, 293.95) * mm});
            skLineSegment(sketch, "E1286", {"start": v(-614.7, 293.95) * mm, "end": v(-614.7, 292.7) * mm});
            skLineSegment(sketch, "E1287", {"start": v(-614.7, 292.7) * mm, "end": v(-609.7, 292.7) * mm});
            skLineSegment(sketch, "E1288", {"start": v(-609.7, 292.7) * mm, "end": v(-609.7, 293.95) * mm});
            skLineSegment(sketch, "E1289", {"start": v(-609.7, 293.95) * mm, "end": v(-605.4, 293.95) * mm});
            skLineSegment(sketch, "E1290", {"start": v(-605.4, 206.75) * mm, "end": v(-609.7, 206.75) * mm});
            skLineSegment(sketch, "E1291", {"start": v(-609.7, 206.75) * mm, "end": v(-609.7, 208) * mm});
            skLineSegment(sketch, "E1292", {"start": v(-609.7, 208) * mm, "end": v(-614.7, 208) * mm});
            skLineSegment(sketch, "E1293", {"start": v(-614.7, 208) * mm, "end": v(-614.7, 206.75) * mm});
            skLineSegment(sketch, "E1294", {"start": v(-614.7, 206.75) * mm, "end": v(-617.4, 206.75) * mm});
            skLineSegment(sketch, "E1295", {"start": v(-617.4, 206.75) * mm, "end": v(-617.4, 203.25) * mm});
            skLineSegment(sketch, "E1296", {"start": v(-617.4, 203.25) * mm, "end": v(-614.7, 203.25) * mm});
            skLineSegment(sketch, "E1297", {"start": v(-614.7, 203.25) * mm, "end": v(-614.7, 202) * mm});
            skLineSegment(sketch, "E1298", {"start": v(-614.7, 202) * mm, "end": v(-609.7, 202) * mm});
            skLineSegment(sketch, "E1299", {"start": v(-609.7, 202) * mm, "end": v(-609.7, 203.25) * mm});
            skLineSegment(sketch, "E1300", {"start": v(-609.7, 203.25) * mm, "end": v(-605.4, 203.25) * mm});
            skLineSegment(sketch, "E1301", {"start": v(-605.4, 116.05) * mm, "end": v(-609.7, 116.05) * mm});
            skLineSegment(sketch, "E1302", {"start": v(-609.7, 116.05) * mm, "end": v(-609.7, 117.3) * mm});
            skLineSegment(sketch, "E1303", {"start": v(-609.7, 117.3) * mm, "end": v(-614.7, 117.3) * mm});
            skLineSegment(sketch, "E1304", {"start": v(-614.7, 117.3) * mm, "end": v(-614.7, 116.05) * mm});
            skLineSegment(sketch, "E1305", {"start": v(-614.7, 116.05) * mm, "end": v(-617.4, 116.05) * mm});
            skLineSegment(sketch, "E1306", {"start": v(-617.4, 116.05) * mm, "end": v(-617.4, 112.55) * mm});
            skLineSegment(sketch, "E1307", {"start": v(-617.4, 112.55) * mm, "end": v(-614.7, 112.55) * mm});
            skLineSegment(sketch, "E1308", {"start": v(-614.7, 112.55) * mm, "end": v(-614.7, 111.3) * mm});
            skLineSegment(sketch, "E1309", {"start": v(-614.7, 111.3) * mm, "end": v(-609.7, 111.3) * mm});
            skLineSegment(sketch, "E1310", {"start": v(-609.7, 111.3) * mm, "end": v(-609.7, 112.55) * mm});
            skLineSegment(sketch, "E1311", {"start": v(-609.7, 112.55) * mm, "end": v(-605.4, 112.55) * mm});
            skLineSegment(sketch, "E1312", {"start": v(-605.4, 97.25) * mm, "end": v(-609.7, 97.25) * mm});
            skLineSegment(sketch, "E1313", {"start": v(-609.7, 97.25) * mm, "end": v(-609.7, 98.5) * mm});
            skLineSegment(sketch, "E1314", {"start": v(-609.7, 98.5) * mm, "end": v(-614.7, 98.5) * mm});
            skLineSegment(sketch, "E1315", {"start": v(-614.7, 98.5) * mm, "end": v(-614.7, 97.25) * mm});
            skLineSegment(sketch, "E1316", {"start": v(-614.7, 97.25) * mm, "end": v(-617.4, 97.25) * mm});
            skLineSegment(sketch, "E1317", {"start": v(-617.4, 97.25) * mm, "end": v(-617.4, 93.75) * mm});
            skLineSegment(sketch, "E1318", {"start": v(-617.4, 93.75) * mm, "end": v(-614.7, 93.75) * mm});
            skLineSegment(sketch, "E1319", {"start": v(-614.7, 93.75) * mm, "end": v(-614.7, 92.5) * mm});
            skLineSegment(sketch, "E1320", {"start": v(-614.7, 92.5) * mm, "end": v(-609.7, 92.5) * mm});
            skLineSegment(sketch, "E1321", {"start": v(-609.7, 92.5) * mm, "end": v(-609.7, 93.75) * mm});
            skLineSegment(sketch, "E1322", {"start": v(-609.7, 93.75) * mm, "end": v(-605.4, 93.75) * mm});
            skLineSegment(sketch, "E1323", {"start": v(-428.66, 10) * mm, "end": v(-428.66, 14.3) * mm});
            skLineSegment(sketch, "E1324", {"start": v(-428.66, 14.3) * mm, "end": v(-427.4, 14.3) * mm});
            skLineSegment(sketch, "E1325", {"start": v(-427.4, 14.3) * mm, "end": v(-427.4, 19.3) * mm});
            skLineSegment(sketch, "E1326", {"start": v(-427.4, 19.3) * mm, "end": v(-428.66, 19.3) * mm});
            skLineSegment(sketch, "E1327", {"start": v(-428.66, 19.3) * mm, "end": v(-428.66, 22) * mm});
            skLineSegment(sketch, "E1328", {"start": v(-428.66, 22) * mm, "end": v(-432.16, 22) * mm});
            skLineSegment(sketch, "E1329", {"start": v(-432.16, 22) * mm, "end": v(-432.16, 19.3) * mm});
            skLineSegment(sketch, "E1330", {"start": v(-432.16, 19.3) * mm, "end": v(-433.4, 19.3) * mm});
            skLineSegment(sketch, "E1331", {"start": v(-433.4, 19.3) * mm, "end": v(-433.4, 14.3) * mm});
            skLineSegment(sketch, "E1332", {"start": v(-433.4, 14.3) * mm, "end": v(-432.16, 14.3) * mm});
            skLineSegment(sketch, "E1333", {"start": v(-432.16, 14.3) * mm, "end": v(-432.16, 10) * mm});
            skLineSegment(sketch, "E1334", {"start": v(-556, 10) * mm, "end": v(-556, 14.3) * mm});
            skLineSegment(sketch, "E1335", {"start": v(-556, 14.3) * mm, "end": v(-554.76, 14.3) * mm});
            skLineSegment(sketch, "E1336", {"start": v(-554.76, 14.3) * mm, "end": v(-554.76, 19.3) * mm});
            skLineSegment(sketch, "E1337", {"start": v(-554.76, 19.3) * mm, "end": v(-556, 19.3) * mm});
            skLineSegment(sketch, "E1338", {"start": v(-556, 19.3) * mm, "end": v(-556, 22) * mm});
            skLineSegment(sketch, "E1339", {"start": v(-556, 22) * mm, "end": v(-559.5, 22) * mm});
            skLineSegment(sketch, "E1340", {"start": v(-559.5, 22) * mm, "end": v(-559.5, 19.3) * mm});
            skLineSegment(sketch, "E1341", {"start": v(-559.5, 19.3) * mm, "end": v(-560.76, 19.3) * mm});
            skLineSegment(sketch, "E1342", {"start": v(-560.76, 19.3) * mm, "end": v(-560.76, 14.3) * mm});
            skLineSegment(sketch, "E1343", {"start": v(-560.76, 14.3) * mm, "end": v(-559.5, 14.3) * mm});
            skLineSegment(sketch, "E1344", {"start": v(-559.5, 14.3) * mm, "end": v(-559.5, 10) * mm});
            skLineSegment(sketch, "E1345", {"start": v(-578.9, 53.5) * mm, "end": v(-578.9, 49.2) * mm});
            skLineSegment(sketch, "E1346", {"start": v(-578.9, 49.2) * mm, "end": v(-580.16, 49.2) * mm});
            skLineSegment(sketch, "E1347", {"start": v(-580.16, 49.2) * mm, "end": v(-580.16, 44.2) * mm});
            skLineSegment(sketch, "E1348", {"start": v(-580.16, 44.2) * mm, "end": v(-578.9, 44.2) * mm});
            skLineSegment(sketch, "E1349", {"start": v(-578.9, 44.2) * mm, "end": v(-578.9, 41.5) * mm});
            skLineSegment(sketch, "E1350", {"start": v(-578.9, 41.5) * mm, "end": v(-575.4, 41.5) * mm});
            skLineSegment(sketch, "E1351", {"start": v(-575.4, 41.5) * mm, "end": v(-575.4, 44.2) * mm});
            skLineSegment(sketch, "E1352", {"start": v(-575.4, 44.2) * mm, "end": v(-574.16, 44.2) * mm});
            skLineSegment(sketch, "E1353", {"start": v(-574.16, 44.2) * mm, "end": v(-574.16, 49.2) * mm});
            skLineSegment(sketch, "E1354", {"start": v(-574.16, 49.2) * mm, "end": v(-575.4, 49.2) * mm});
            skLineSegment(sketch, "E1355", {"start": v(-575.4, 49.2) * mm, "end": v(-575.4, 53.5) * mm});
            skLineSegment(sketch, "E1356", {"start": v(-708.8, 10) * mm, "end": v(-708.8, 14.3) * mm});
            skLineSegment(sketch, "E1357", {"start": v(-708.8, 14.3) * mm, "end": v(-707.56, 14.3) * mm});
            skLineSegment(sketch, "E1358", {"start": v(-707.56, 14.3) * mm, "end": v(-707.56, 19.3) * mm});
            skLineSegment(sketch, "E1359", {"start": v(-707.56, 19.3) * mm, "end": v(-708.8, 19.3) * mm});
            skLineSegment(sketch, "E1360", {"start": v(-708.8, 19.3) * mm, "end": v(-708.8, 22) * mm});
            skLineSegment(sketch, "E1361", {"start": v(-708.8, 22) * mm, "end": v(-712.3, 22) * mm});
            skLineSegment(sketch, "E1362", {"start": v(-712.3, 22) * mm, "end": v(-712.3, 19.3) * mm});
            skLineSegment(sketch, "E1363", {"start": v(-712.3, 19.3) * mm, "end": v(-713.56, 19.3) * mm});
            skLineSegment(sketch, "E1364", {"start": v(-713.56, 19.3) * mm, "end": v(-713.56, 14.3) * mm});
            skLineSegment(sketch, "E1365", {"start": v(-713.56, 14.3) * mm, "end": v(-712.3, 14.3) * mm});
            skLineSegment(sketch, "E1366", {"start": v(-712.3, 14.3) * mm, "end": v(-712.3, 10) * mm});
            skLineSegment(sketch, "E1367", {"start": v(-638.3, 10) * mm, "end": v(-638.3, 14.3) * mm});
            skLineSegment(sketch, "E1368", {"start": v(-638.3, 14.3) * mm, "end": v(-637.06, 14.3) * mm});
            skLineSegment(sketch, "E1369", {"start": v(-637.06, 14.3) * mm, "end": v(-637.06, 19.3) * mm});
            skLineSegment(sketch, "E1370", {"start": v(-637.06, 19.3) * mm, "end": v(-638.3, 19.3) * mm});
            skLineSegment(sketch, "E1371", {"start": v(-638.3, 19.3) * mm, "end": v(-638.3, 22) * mm});
            skLineSegment(sketch, "E1372", {"start": v(-638.3, 22) * mm, "end": v(-641.8, 22) * mm});
            skLineSegment(sketch, "E1373", {"start": v(-641.8, 22) * mm, "end": v(-641.8, 19.3) * mm});
            skLineSegment(sketch, "E1374", {"start": v(-641.8, 19.3) * mm, "end": v(-643.06, 19.3) * mm});
            skLineSegment(sketch, "E1375", {"start": v(-643.06, 19.3) * mm, "end": v(-643.06, 14.3) * mm});
            skLineSegment(sketch, "E1376", {"start": v(-643.06, 14.3) * mm, "end": v(-641.8, 14.3) * mm});
            skLineSegment(sketch, "E1377", {"start": v(-641.8, 14.3) * mm, "end": v(-641.8, 10) * mm});
            skLineSegment(sketch, "E1378", {"start": v(-126.25, 10) * mm, "end": v(-126.25, 14.3) * mm});
            skLineSegment(sketch, "E1379", {"start": v(-126.25, 14.3) * mm, "end": v(-125, 14.3) * mm});
            skLineSegment(sketch, "E1380", {"start": v(-125, 14.3) * mm, "end": v(-125, 19.3) * mm});
            skLineSegment(sketch, "E1381", {"start": v(-125, 19.3) * mm, "end": v(-126.25, 19.3) * mm});
            skLineSegment(sketch, "E1382", {"start": v(-126.25, 19.3) * mm, "end": v(-126.25, 22) * mm});
            skLineSegment(sketch, "E1383", {"start": v(-126.25, 22) * mm, "end": v(-129.75, 22) * mm});
            skLineSegment(sketch, "E1384", {"start": v(-129.75, 22) * mm, "end": v(-129.75, 19.3) * mm});
            skLineSegment(sketch, "E1385", {"start": v(-129.75, 19.3) * mm, "end": v(-131, 19.3) * mm});
            skLineSegment(sketch, "E1386", {"start": v(-131, 19.3) * mm, "end": v(-131, 14.3) * mm});
            skLineSegment(sketch, "E1387", {"start": v(-131, 14.3) * mm, "end": v(-129.75, 14.3) * mm});
            skLineSegment(sketch, "E1388", {"start": v(-129.75, 14.3) * mm, "end": v(-129.75, 10) * mm});
            skLineSegment(sketch, "E1389", {"start": v(-41.25, 10) * mm, "end": v(-41.25, 14.3) * mm});
            skLineSegment(sketch, "E1390", {"start": v(-41.25, 14.3) * mm, "end": v(-40, 14.3) * mm});
            skLineSegment(sketch, "E1391", {"start": v(-40, 14.3) * mm, "end": v(-40, 19.3) * mm});
            skLineSegment(sketch, "E1392", {"start": v(-40, 19.3) * mm, "end": v(-41.25, 19.3) * mm});
            skLineSegment(sketch, "E1393", {"start": v(-41.25, 19.3) * mm, "end": v(-41.25, 22) * mm});
            skLineSegment(sketch, "E1394", {"start": v(-41.25, 22) * mm, "end": v(-44.75, 22) * mm});
            skLineSegment(sketch, "E1395", {"start": v(-44.75, 22) * mm, "end": v(-44.75, 19.3) * mm});
            skLineSegment(sketch, "E1396", {"start": v(-44.75, 19.3) * mm, "end": v(-46, 19.3) * mm});
            skLineSegment(sketch, "E1397", {"start": v(-46, 19.3) * mm, "end": v(-46, 14.3) * mm});
            skLineSegment(sketch, "E1398", {"start": v(-46, 14.3) * mm, "end": v(-44.75, 14.3) * mm});
            skLineSegment(sketch, "E1399", {"start": v(-44.75, 14.3) * mm, "end": v(-44.75, 10) * mm});
            skLineSegment(sketch, "E1400", {"start": v(44.75, 10) * mm, "end": v(44.75, 14.3) * mm});
            skLineSegment(sketch, "E1401", {"start": v(44.75, 14.3) * mm, "end": v(46, 14.3) * mm});
            skLineSegment(sketch, "E1402", {"start": v(46, 14.3) * mm, "end": v(46, 19.3) * mm});
            skLineSegment(sketch, "E1403", {"start": v(46, 19.3) * mm, "end": v(44.75, 19.3) * mm});
            skLineSegment(sketch, "E1404", {"start": v(44.75, 19.3) * mm, "end": v(44.75, 22) * mm});
            skLineSegment(sketch, "E1405", {"start": v(44.75, 22) * mm, "end": v(41.25, 22) * mm});
            skLineSegment(sketch, "E1406", {"start": v(41.25, 22) * mm, "end": v(41.25, 19.3) * mm});
            skLineSegment(sketch, "E1407", {"start": v(41.25, 19.3) * mm, "end": v(40, 19.3) * mm});
            skLineSegment(sketch, "E1408", {"start": v(40, 19.3) * mm, "end": v(40, 14.3) * mm});
            skLineSegment(sketch, "E1409", {"start": v(40, 14.3) * mm, "end": v(41.25, 14.3) * mm});
            skLineSegment(sketch, "E1410", {"start": v(41.25, 14.3) * mm, "end": v(41.25, 10) * mm});
            skLineSegment(sketch, "E1411", {"start": v(129.75, 10) * mm, "end": v(129.75, 14.3) * mm});
            skLineSegment(sketch, "E1412", {"start": v(129.75, 14.3) * mm, "end": v(131, 14.3) * mm});
            skLineSegment(sketch, "E1413", {"start": v(131, 14.3) * mm, "end": v(131, 19.3) * mm});
            skLineSegment(sketch, "E1414", {"start": v(131, 19.3) * mm, "end": v(129.75, 19.3) * mm});
            skLineSegment(sketch, "E1415", {"start": v(129.75, 19.3) * mm, "end": v(129.75, 22) * mm});
            skLineSegment(sketch, "E1416", {"start": v(129.75, 22) * mm, "end": v(126.25, 22) * mm});
            skLineSegment(sketch, "E1417", {"start": v(126.25, 22) * mm, "end": v(126.25, 19.3) * mm});
            skLineSegment(sketch, "E1418", {"start": v(126.25, 19.3) * mm, "end": v(125, 19.3) * mm});
            skLineSegment(sketch, "E1419", {"start": v(125, 19.3) * mm, "end": v(125, 14.3) * mm});
            skLineSegment(sketch, "E1420", {"start": v(125, 14.3) * mm, "end": v(126.25, 14.3) * mm});
            skLineSegment(sketch, "E1421", {"start": v(126.25, 14.3) * mm, "end": v(126.25, 10) * mm});
            skLineSegment(sketch, "E1422", {"start": v(-187.75, 430.5) * mm, "end": v(-187.75, 426.2) * mm});
            skLineSegment(sketch, "E1423", {"start": v(-187.75, 426.2) * mm, "end": v(-189, 426.2) * mm});
            skLineSegment(sketch, "E1424", {"start": v(-189, 426.2) * mm, "end": v(-189, 421.2) * mm});
            skLineSegment(sketch, "E1425", {"start": v(-189, 421.2) * mm, "end": v(-187.75, 421.2) * mm});
            skLineSegment(sketch, "E1426", {"start": v(-187.75, 421.2) * mm, "end": v(-187.75, 418.5) * mm});
            skLineSegment(sketch, "E1427", {"start": v(-187.75, 418.5) * mm, "end": v(-184.25, 418.5) * mm});
            skLineSegment(sketch, "E1428", {"start": v(-184.25, 418.5) * mm, "end": v(-184.25, 421.2) * mm});
            skLineSegment(sketch, "E1429", {"start": v(-184.25, 421.2) * mm, "end": v(-183, 421.2) * mm});
            skLineSegment(sketch, "E1430", {"start": v(-183, 421.2) * mm, "end": v(-183, 426.2) * mm});
            skLineSegment(sketch, "E1431", {"start": v(-183, 426.2) * mm, "end": v(-184.25, 426.2) * mm});
            skLineSegment(sketch, "E1432", {"start": v(-184.25, 426.2) * mm, "end": v(-184.25, 430.5) * mm});
            skLineSegment(sketch, "E1433", {"start": v(184.25, 430.5) * mm, "end": v(184.25, 426.2) * mm});
            skLineSegment(sketch, "E1434", {"start": v(184.25, 426.2) * mm, "end": v(183, 426.2) * mm});
            skLineSegment(sketch, "E1435", {"start": v(183, 426.2) * mm, "end": v(183, 421.2) * mm});
            skLineSegment(sketch, "E1436", {"start": v(183, 421.2) * mm, "end": v(184.25, 421.2) * mm});
            skLineSegment(sketch, "E1437", {"start": v(184.25, 421.2) * mm, "end": v(184.25, 418.5) * mm});
            skLineSegment(sketch, "E1438", {"start": v(184.25, 418.5) * mm, "end": v(187.75, 418.5) * mm});
            skLineSegment(sketch, "E1439", {"start": v(187.75, 418.5) * mm, "end": v(187.75, 421.2) * mm});
            skLineSegment(sketch, "E1440", {"start": v(187.75, 421.2) * mm, "end": v(189, 421.2) * mm});
            skLineSegment(sketch, "E1441", {"start": v(189, 421.2) * mm, "end": v(189, 426.2) * mm});
            skLineSegment(sketch, "E1442", {"start": v(189, 426.2) * mm, "end": v(187.75, 426.2) * mm});
            skLineSegment(sketch, "E1443", {"start": v(187.75, 426.2) * mm, "end": v(187.75, 430.5) * mm});
            skLineSegment(sketch, "E1444", {"start": v(-651.76, 430.5) * mm, "end": v(-651.76, 426.2) * mm});
            skLineSegment(sketch, "E1445", {"start": v(-651.76, 426.2) * mm, "end": v(-653, 426.2) * mm});
            skLineSegment(sketch, "E1446", {"start": v(-653, 426.2) * mm, "end": v(-653, 421.2) * mm});
            skLineSegment(sketch, "E1447", {"start": v(-653, 421.2) * mm, "end": v(-651.76, 421.2) * mm});
            skLineSegment(sketch, "E1448", {"start": v(-651.76, 421.2) * mm, "end": v(-651.76, 418.5) * mm});
            skLineSegment(sketch, "E1449", {"start": v(-651.76, 418.5) * mm, "end": v(-648.26, 418.5) * mm});
            skLineSegment(sketch, "E1450", {"start": v(-648.26, 418.5) * mm, "end": v(-648.26, 421.2) * mm});
            skLineSegment(sketch, "E1451", {"start": v(-648.26, 421.2) * mm, "end": v(-647, 421.2) * mm});
            skLineSegment(sketch, "E1452", {"start": v(-647, 421.2) * mm, "end": v(-647, 426.2) * mm});
            skLineSegment(sketch, "E1453", {"start": v(-647, 426.2) * mm, "end": v(-648.26, 426.2) * mm});
            skLineSegment(sketch, "E1454", {"start": v(-648.26, 426.2) * mm, "end": v(-648.26, 430.5) * mm});
            skLineSegment(sketch, "E1455", {"start": v(-747.4, 18.05) * mm, "end": v(-743.1, 18.05) * mm});
            skLineSegment(sketch, "E1456", {"start": v(-743.1, 18.05) * mm, "end": v(-743.1, 16.8) * mm});
            skLineSegment(sketch, "E1457", {"start": v(-743.1, 16.8) * mm, "end": v(-738.1, 16.8) * mm});
            skLineSegment(sketch, "E1458", {"start": v(-738.1, 16.8) * mm, "end": v(-738.1, 18.05) * mm});
            skLineSegment(sketch, "E1459", {"start": v(-738.1, 18.05) * mm, "end": v(-735.4, 18.05) * mm});
            skLineSegment(sketch, "E1460", {"start": v(-735.4, 18.05) * mm, "end": v(-735.4, 21.55) * mm});
            skLineSegment(sketch, "E1461", {"start": v(-735.4, 21.55) * mm, "end": v(-738.1, 21.55) * mm});
            skLineSegment(sketch, "E1462", {"start": v(-738.1, 21.55) * mm, "end": v(-738.1, 22.8) * mm});
            skLineSegment(sketch, "E1463", {"start": v(-738.1, 22.8) * mm, "end": v(-743.1, 22.8) * mm});
            skLineSegment(sketch, "E1464", {"start": v(-743.1, 22.8) * mm, "end": v(-743.1, 21.55) * mm});
            skLineSegment(sketch, "E1465", {"start": v(-743.1, 21.55) * mm, "end": v(-747.4, 21.55) * mm});
            skLineSegment(sketch, "E1466", {"start": v(-747.4, 49.45) * mm, "end": v(-743.1, 49.45) * mm});
            skLineSegment(sketch, "E1467", {"start": v(-743.1, 49.45) * mm, "end": v(-743.1, 48.2) * mm});
            skLineSegment(sketch, "E1468", {"start": v(-743.1, 48.2) * mm, "end": v(-738.1, 48.2) * mm});
            skLineSegment(sketch, "E1469", {"start": v(-738.1, 48.2) * mm, "end": v(-738.1, 49.45) * mm});
            skLineSegment(sketch, "E1470", {"start": v(-738.1, 49.45) * mm, "end": v(-735.4, 49.45) * mm});
            skLineSegment(sketch, "E1471", {"start": v(-735.4, 49.45) * mm, "end": v(-735.4, 52.95) * mm});
            skLineSegment(sketch, "E1472", {"start": v(-735.4, 52.95) * mm, "end": v(-738.1, 52.95) * mm});
            skLineSegment(sketch, "E1473", {"start": v(-738.1, 52.95) * mm, "end": v(-738.1, 54.2) * mm});
            skLineSegment(sketch, "E1474", {"start": v(-738.1, 54.2) * mm, "end": v(-743.1, 54.2) * mm});
            skLineSegment(sketch, "E1475", {"start": v(-743.1, 54.2) * mm, "end": v(-743.1, 52.95) * mm});
            skLineSegment(sketch, "E1476", {"start": v(-743.1, 52.95) * mm, "end": v(-747.4, 52.95) * mm});
            skLineSegment(sketch, "E1477", {"start": v(-284.68, 53.5) * mm, "end": v(-284.68, 49.2) * mm});
            skLineSegment(sketch, "E1478", {"start": v(-284.68, 49.2) * mm, "end": v(-285.93, 49.2) * mm});
            skLineSegment(sketch, "E1479", {"start": v(-285.93, 49.2) * mm, "end": v(-285.93, 44.2) * mm});
            skLineSegment(sketch, "E1480", {"start": v(-285.93, 44.2) * mm, "end": v(-284.68, 44.2) * mm});
            skLineSegment(sketch, "E1481", {"start": v(-284.68, 44.2) * mm, "end": v(-284.68, 41.5) * mm});
            skLineSegment(sketch, "E1482", {"start": v(-284.68, 41.5) * mm, "end": v(-281.18, 41.5) * mm});
            skLineSegment(sketch, "E1483", {"start": v(-281.18, 41.5) * mm, "end": v(-281.18, 44.2) * mm});
            skLineSegment(sketch, "E1484", {"start": v(-281.18, 44.2) * mm, "end": v(-279.93, 44.2) * mm});
            skLineSegment(sketch, "E1485", {"start": v(-279.93, 44.2) * mm, "end": v(-279.93, 49.2) * mm});
            skLineSegment(sketch, "E1486", {"start": v(-279.93, 49.2) * mm, "end": v(-281.18, 49.2) * mm});
            skLineSegment(sketch, "E1487", {"start": v(-281.18, 49.2) * mm, "end": v(-281.18, 53.5) * mm});
            skLineSegment(sketch, "E1488", {"start": v(-308.18, 127.05) * mm, "end": v(-303.88, 127.05) * mm});
            skLineSegment(sketch, "E1489", {"start": v(-303.88, 127.05) * mm, "end": v(-303.88, 125.8) * mm});
            skLineSegment(sketch, "E1490", {"start": v(-303.88, 125.8) * mm, "end": v(-298.88, 125.8) * mm});
            skLineSegment(sketch, "E1491", {"start": v(-298.88, 125.8) * mm, "end": v(-298.88, 127.05) * mm});
            skLineSegment(sketch, "E1492", {"start": v(-298.88, 127.05) * mm, "end": v(-296.18, 127.05) * mm});
            skLineSegment(sketch, "E1493", {"start": v(-296.18, 127.05) * mm, "end": v(-296.18, 130.55) * mm});
            skLineSegment(sketch, "E1494", {"start": v(-296.18, 130.55) * mm, "end": v(-298.88, 130.55) * mm});
            skLineSegment(sketch, "E1495", {"start": v(-298.88, 130.55) * mm, "end": v(-298.88, 131.8) * mm});
            skLineSegment(sketch, "E1496", {"start": v(-298.88, 131.8) * mm, "end": v(-303.88, 131.8) * mm});
            skLineSegment(sketch, "E1497", {"start": v(-303.88, 131.8) * mm, "end": v(-303.88, 130.55) * mm});
            skLineSegment(sketch, "E1498", {"start": v(-303.88, 130.55) * mm, "end": v(-308.18, 130.55) * mm});
            skLineSegment(sketch, "E1499", {"start": v(-308.18, 21.75) * mm, "end": v(-303.88, 21.75) * mm});
            skLineSegment(sketch, "E1500", {"start": v(-303.88, 21.75) * mm, "end": v(-303.88, 20.5) * mm});
            skLineSegment(sketch, "E1501", {"start": v(-303.88, 20.5) * mm, "end": v(-298.88, 20.5) * mm});
            skLineSegment(sketch, "E1502", {"start": v(-298.88, 20.5) * mm, "end": v(-298.88, 21.75) * mm});
            skLineSegment(sketch, "E1503", {"start": v(-298.88, 21.75) * mm, "end": v(-296.18, 21.75) * mm});
            skLineSegment(sketch, "E1504", {"start": v(-296.18, 21.75) * mm, "end": v(-296.18, 25.25) * mm});
            skLineSegment(sketch, "E1505", {"start": v(-296.18, 25.25) * mm, "end": v(-298.88, 25.25) * mm});
            skLineSegment(sketch, "E1506", {"start": v(-298.88, 25.25) * mm, "end": v(-298.88, 26.5) * mm});
            skLineSegment(sketch, "E1507", {"start": v(-298.88, 26.5) * mm, "end": v(-303.88, 26.5) * mm});
            skLineSegment(sketch, "E1508", {"start": v(-303.88, 26.5) * mm, "end": v(-303.88, 25.25) * mm});
            skLineSegment(sketch, "E1509", {"start": v(-303.88, 25.25) * mm, "end": v(-308.18, 25.25) * mm});
            skLineSegment(sketch, "E1510", {"start": v(-172, 574.16) * mm, "end": v(-158.7, 574.16) * mm});
            skLineSegment(sketch, "E1511", {"start": v(-176.03, 579.16) * mm, "end": v(-162.57, 579.16) * mm});
            skLineSegment(sketch, "E1512.bottom", {"start": v(-161.7, 581.49) * mm, "end": v(-161.7, 580.02) * mm});
            skLineSegment(sketch, "E1512.top", {"start": v(-176.9, 581.49) * mm, "end": v(-176.9, 580.02) * mm});
            skArc(sketch, "E1513", {"start": v(-161.7, 580.02) * mm, "mid": v(-161.63, 579.77) * mm, "end": v(-161.45, 579.59) * mm});
            skArc(sketch, "E1514", {"start": v(-162.13, 578.9) * mm, "mid": v(-161.35, 578.8) * mm, "end": v(-161.45, 579.59) * mm});
            skArc(sketch, "E1515", {"start": v(-162.13, 578.9) * mm, "mid": v(-162.32, 579.09) * mm, "end": v(-162.57, 579.16) * mm});
            skArc(sketch, "E1516", {"start": v(-176.03, 579.16) * mm, "mid": v(-176.28, 579.09) * mm, "end": v(-176.47, 578.9) * mm});
            skArc(sketch, "E1517", {"start": v(-177.15, 579.59) * mm, "mid": v(-177.25, 578.8) * mm, "end": v(-176.47, 578.9) * mm});
            skArc(sketch, "E1518", {"start": v(-177.15, 579.59) * mm, "mid": v(-176.97, 579.77) * mm, "end": v(-176.9, 580.02) * mm});
            skArc(sketch, "E1519", {"start": v(-162.57, 582.36) * mm, "mid": v(-162.32, 582.42) * mm, "end": v(-162.13, 582.6) * mm});
            skArc(sketch, "E1520", {"start": v(-161.45, 581.92) * mm, "mid": v(-161.35, 582.7) * mm, "end": v(-162.13, 582.6) * mm});
            skArc(sketch, "E1521", {"start": v(-161.45, 581.92) * mm, "mid": v(-161.63, 581.74) * mm, "end": v(-161.7, 581.49) * mm});
            skLineSegment(sketch, "E1522", {"start": v(-153.7, 581.49) * mm, "end": v(-153.7, 579.16) * mm});
            skArc(sketch, "E1523", {"start": v(-153.7, 581.49) * mm, "mid": v(-153.77, 581.74) * mm, "end": v(-153.95, 581.92) * mm});
            skArc(sketch, "E1524", {"start": v(-153.27, 582.6) * mm, "mid": v(-154.05, 582.7) * mm, "end": v(-153.95, 581.92) * mm});
            skArc(sketch, "E1525", {"start": v(-153.27, 582.6) * mm, "mid": v(-153.08, 582.42) * mm, "end": v(-152.83, 582.36) * mm});
            skLineSegment(sketch, "E1526", {"start": v(-177, 569.16) * mm, "end": v(-177, 541.86) * mm});
            skLineSegment(sketch, "E1527", {"start": v(-162.57, 582.36) * mm, "end": v(-176.03, 582.36) * mm});
            skArc(sketch, "E1528.filletArc", {"start": v(-172, 574.16) * mm, "mid": v(-175.54, 572.7) * mm, "end": v(-177, 569.16) * mm});
            skPoint(sketch, "E1529.visualSharp", {"position": v(-153.7, 574.16) * mm});
            skArc(sketch, "E1529.filletArc", {"start": v(-158.7, 574.16) * mm, "mid": v(-155.16, 575.62) * mm, "end": v(-153.7, 579.16) * mm});
            skLineSegment(sketch, "E1530", {"start": v(-161.8, 433) * mm, "end": v(-161.8, 431.37) * mm});
            skLineSegment(sketch, "E1531", {"start": v(-176.3, 433.5) * mm, "end": v(-162.3, 433.5) * mm});
            skLineSegment(sketch, "E1532", {"start": v(-176.8, 431.37) * mm, "end": v(-176.8, 433) * mm});
            skPoint(sketch, "E1533", {"position": v(-169.3, 433.5) * mm});
            skArc(sketch, "E1534.filletArc", {"start": v(-176.3, 433.5) * mm, "mid": v(-176.65, 433.35) * mm, "end": v(-176.8, 433) * mm});
            skPoint(sketch, "E1535.visualSharp", {"position": v(-161.8, 433.5) * mm});
            skArc(sketch, "E1535.filletArc", {"start": v(-161.8, 433) * mm, "mid": v(-161.95, 433.35) * mm, "end": v(-162.3, 433.5) * mm});
            skArc(sketch, "E1536", {"start": v(-177.23, 430.25) * mm, "mid": v(-177.42, 430.43) * mm, "end": v(-177.67, 430.5) * mm});
            skArc(sketch, "E1537", {"start": v(-177.23, 430.25) * mm, "mid": v(-176.45, 430.15) * mm, "end": v(-176.55, 430.93) * mm});
            skArc(sketch, "E1538", {"start": v(-176.8, 431.37) * mm, "mid": v(-176.73, 431.12) * mm, "end": v(-176.55, 430.93) * mm});
            skArc(sketch, "E1539", {"start": v(-162.05, 430.93) * mm, "mid": v(-161.87, 431.12) * mm, "end": v(-161.8, 431.37) * mm});
            skArc(sketch, "E1540", {"start": v(-162.05, 430.93) * mm, "mid": v(-162.15, 430.15) * mm, "end": v(-161.37, 430.25) * mm});
            skArc(sketch, "E1541", {"start": v(-160.93, 430.5) * mm, "mid": v(-161.18, 430.43) * mm, "end": v(-161.37, 430.25) * mm});
            skLineSegment(sketch, "E1542", {"start": v(-160.93, 430.5) * mm, "end": v(-154.47, 430.5) * mm});
            skLineSegment(sketch, "E1543", {"start": v(161.8, 431.37) * mm, "end": v(161.8, 433) * mm});
            skLineSegment(sketch, "E1544", {"start": v(162.3, 433.5) * mm, "end": v(176.3, 433.5) * mm});
            skLineSegment(sketch, "E1545", {"start": v(176.8, 433) * mm, "end": v(176.8, 431.37) * mm});
            skPoint(sketch, "E1546.visualSharp", {"position": v(161.8, 433.5) * mm});
            skArc(sketch, "E1546.filletArc", {"start": v(162.3, 433.5) * mm, "mid": v(161.95, 433.35) * mm, "end": v(161.8, 433) * mm});
            skPoint(sketch, "E1547.visualSharp", {"position": v(176.8, 433.5) * mm});
            skArc(sketch, "E1547.filletArc", {"start": v(176.8, 433) * mm, "mid": v(176.65, 433.35) * mm, "end": v(176.3, 433.5) * mm});
            skArc(sketch, "E1548", {"start": v(161.37, 430.25) * mm, "mid": v(161.18, 430.43) * mm, "end": v(160.93, 430.5) * mm});
            skArc(sketch, "E1549", {"start": v(161.37, 430.25) * mm, "mid": v(162.15, 430.15) * mm, "end": v(162.05, 430.93) * mm});
            skArc(sketch, "E1550", {"start": v(161.8, 431.37) * mm, "mid": v(161.87, 431.12) * mm, "end": v(162.05, 430.93) * mm});
            skArc(sketch, "E1551", {"start": v(176.55, 430.93) * mm, "mid": v(176.73, 431.12) * mm, "end": v(176.8, 431.37) * mm});
            skArc(sketch, "E1552", {"start": v(176.55, 430.93) * mm, "mid": v(176.45, 430.15) * mm, "end": v(177.23, 430.25) * mm});
            skArc(sketch, "E1553", {"start": v(177.67, 430.5) * mm, "mid": v(177.42, 430.43) * mm, "end": v(177.23, 430.25) * mm});
            skLineSegment(sketch, "E1554", {"start": v(154.47, 430.5) * mm, "end": v(160.93, 430.5) * mm});
            skLineSegment(sketch, "E1555", {"start": v(-171.6, 224.74) * mm, "end": v(-208.5, 224.74) * mm, "construction": true});
            skPoint(sketch, "E1556", {"position": v(-190.05, 224.74) * mm});
            skLineSegment(sketch, "E1557", {"start": v(-604.54, 82.1) * mm, "end": v(-602.9, 82.1) * mm});
            skLineSegment(sketch, "E1558", {"start": v(-602.4, 82.6) * mm, "end": v(-602.4, 89.6) * mm});
            skLineSegment(sketch, "E1559", {"start": v(-602.9, 90.1) * mm, "end": v(-604.54, 90.1) * mm});
            skLineSegment(sketch, "E1560", {"start": v(-605.4, 90.96) * mm, "end": v(-605.4, 93.75) * mm});
            skPoint(sketch, "E1561.visualSharp", {"position": v(-602.4, 90.1) * mm});
            skArc(sketch, "E1561.filletArc", {"start": v(-602.4, 89.6) * mm, "mid": v(-602.55, 89.95) * mm, "end": v(-602.9, 90.1) * mm});
            skPoint(sketch, "E1562.visualSharp", {"position": v(-602.4, 82.1) * mm});
            skArc(sketch, "E1562.filletArc", {"start": v(-602.9, 82.1) * mm, "mid": v(-602.55, 82.25) * mm, "end": v(-602.4, 82.6) * mm});
            skArc(sketch, "E1563", {"start": v(-605.66, 90.53) * mm, "mid": v(-605.47, 90.72) * mm, "end": v(-605.4, 90.97) * mm});
            skArc(sketch, "E1564", {"start": v(-605.66, 90.53) * mm, "mid": v(-605.76, 89.75) * mm, "end": v(-604.97, 89.85) * mm});
            skArc(sketch, "E1565", {"start": v(-604.54, 90.1) * mm, "mid": v(-604.8, 90.03) * mm, "end": v(-604.97, 89.85) * mm});
            skArc(sketch, "E1566", {"start": v(-604.97, 82.35) * mm, "mid": v(-604.8, 82.17) * mm, "end": v(-604.54, 82.1) * mm});
            skArc(sketch, "E1567", {"start": v(-604.97, 82.35) * mm, "mid": v(-605.76, 82.45) * mm, "end": v(-605.66, 81.67) * mm});
            skArc(sketch, "E1568", {"start": v(-605.4, 81.23) * mm, "mid": v(-605.47, 81.48) * mm, "end": v(-605.66, 81.67) * mm});
            skLineSegment(sketch, "E1569.bottom", {"start": v(-151.73, 90.2) * mm, "end": v(-150.27, 90.2) * mm});
            skLineSegment(sketch, "E1569.top", {"start": v(-151.73, 82) * mm, "end": v(-150.27, 82) * mm});
            skLineSegment(sketch, "E1569.left", {"start": v(-152.6, 89.33) * mm, "end": v(-152.6, 82.87) * mm});
            skLineSegment(sketch, "E1569.right", {"start": v(-149.4, 89.33) * mm, "end": v(-149.4, 82.87) * mm});
            skArc(sketch, "E1570", {"start": v(-150.27, 90.2) * mm, "mid": v(-150.02, 90.27) * mm, "end": v(-149.83, 90.45) * mm});
            skArc(sketch, "E1571", {"start": v(-149.15, 89.77) * mm, "mid": v(-149.05, 90.55) * mm, "end": v(-149.83, 90.45) * mm});
            skArc(sketch, "E1572", {"start": v(-149.15, 89.77) * mm, "mid": v(-149.33, 89.58) * mm, "end": v(-149.4, 89.33) * mm});
            skArc(sketch, "E1573", {"start": v(-152.6, 89.33) * mm, "mid": v(-152.67, 89.58) * mm, "end": v(-152.85, 89.77) * mm});
            skArc(sketch, "E1574", {"start": v(-152.17, 90.45) * mm, "mid": v(-152.95, 90.55) * mm, "end": v(-152.85, 89.77) * mm});
            skArc(sketch, "E1575", {"start": v(-152.17, 90.45) * mm, "mid": v(-151.98, 90.27) * mm, "end": v(-151.73, 90.2) * mm});
            skArc(sketch, "E1576", {"start": v(-149.4, 82.87) * mm, "mid": v(-149.33, 82.62) * mm, "end": v(-149.15, 82.43) * mm});
            skArc(sketch, "E1577", {"start": v(-149.83, 81.75) * mm, "mid": v(-149.05, 81.65) * mm, "end": v(-149.15, 82.43) * mm});
            skArc(sketch, "E1578", {"start": v(-149.83, 81.75) * mm, "mid": v(-150.02, 81.93) * mm, "end": v(-150.27, 82) * mm});
            skArc(sketch, "E1579", {"start": v(-151.73, 82) * mm, "mid": v(-151.98, 81.93) * mm, "end": v(-152.17, 81.75) * mm});
            skArc(sketch, "E1580", {"start": v(-152.85, 82.43) * mm, "mid": v(-152.95, 81.65) * mm, "end": v(-152.17, 81.75) * mm});
            skArc(sketch, "E1581", {"start": v(-152.85, 82.43) * mm, "mid": v(-152.67, 82.62) * mm, "end": v(-152.6, 82.87) * mm});
            skLineSegment(sketch, "E1582.bottom", {"start": v(150.27, 90.2) * mm, "end": v(151.73, 90.2) * mm});
            skLineSegment(sketch, "E1582.top", {"start": v(150.27, 82) * mm, "end": v(151.73, 82) * mm});
            skLineSegment(sketch, "E1582.left", {"start": v(149.4, 89.33) * mm, "end": v(149.4, 82.87) * mm});
            skLineSegment(sketch, "E1582.right", {"start": v(152.6, 89.33) * mm, "end": v(152.6, 82.87) * mm});
            skArc(sketch, "E1583", {"start": v(151.73, 90.2) * mm, "mid": v(151.98, 90.27) * mm, "end": v(152.17, 90.45) * mm});
            skArc(sketch, "E1584", {"start": v(152.85, 89.77) * mm, "mid": v(152.95, 90.55) * mm, "end": v(152.17, 90.45) * mm});
            skArc(sketch, "E1585", {"start": v(152.85, 89.77) * mm, "mid": v(152.67, 89.58) * mm, "end": v(152.6, 89.33) * mm});
            skArc(sketch, "E1586", {"start": v(149.4, 89.33) * mm, "mid": v(149.33, 89.58) * mm, "end": v(149.15, 89.77) * mm});
            skArc(sketch, "E1587", {"start": v(149.83, 90.45) * mm, "mid": v(149.05, 90.55) * mm, "end": v(149.15, 89.77) * mm});
            skArc(sketch, "E1588", {"start": v(149.83, 90.45) * mm, "mid": v(150.02, 90.27) * mm, "end": v(150.27, 90.2) * mm});
            skArc(sketch, "E1589", {"start": v(152.6, 82.87) * mm, "mid": v(152.67, 82.62) * mm, "end": v(152.85, 82.43) * mm});
            skArc(sketch, "E1590", {"start": v(152.17, 81.75) * mm, "mid": v(152.95, 81.65) * mm, "end": v(152.85, 82.43) * mm});
            skArc(sketch, "E1591", {"start": v(152.17, 81.75) * mm, "mid": v(151.98, 81.93) * mm, "end": v(151.73, 82) * mm});
            skArc(sketch, "E1592", {"start": v(150.27, 82) * mm, "mid": v(150.02, 81.93) * mm, "end": v(149.83, 81.75) * mm});
            skArc(sketch, "E1593", {"start": v(149.15, 82.43) * mm, "mid": v(149.05, 81.65) * mm, "end": v(149.83, 81.75) * mm});
            skArc(sketch, "E1594", {"start": v(149.15, 82.43) * mm, "mid": v(149.33, 82.62) * mm, "end": v(149.4, 82.87) * mm});
            skSolve(sketch);
        }
        {
            var Q0;
            Q0=makeQuery(id+"F0.imprint","IMPRINT",FACE,{"disambiguationData":[TD([[makeQuery(id+"F0.imprint","IMPRINT",EDGE,{"derivedFrom":sQuery(id+"F0.wireOp",EDGE,"E0")}),-1.0]])]});
            var Q1;
            Q1=makeQuery(id+"F0.imprint","IMPRINT",FACE,{"disambiguationData":[TD([[makeQuery(id+"F0.imprint","IMPRINT",EDGE,{"derivedFrom":sQuery(id+"F0.wireOp",EDGE,"5d550f00-80d9-469a-a7fc-ca4ec24a9726")}),1.0]])]});
            var Q2;
            {var subQ6=sQuery(id+"F0.wireOp",EDGE,"1d93fe10-1353-476f-b682-283b72ef0e5a");Q2=makeQuery(id+"F0.imprint","IMPRINT",FACE,{"disambiguationData":[TD([[makeQuery(id+"F0.imprint","IMPRINT",EDGE,{"derivedFrom":subQ6}),-1.0]])]});}
            var Q3;
            {var subQ1=sQuery(id+"F0.wireOp",EDGE,"ee58186b-7652-4365-8662-7ea5ae6ba753");Q3=makeQuery(id+"F0.imprint","IMPRINT",FACE,{"disambiguationData":[TD([[makeQuery(id+"F0.imprint","IMPRINT",EDGE,{"derivedFrom":subQ1}),1.0]])]});}
            var Q4;
            Q4=makeQuery(id+"F0.imprint","IMPRINT",FACE,{"disambiguationData":[TD([[makeQuery(id+"F0.imprint","IMPRINT",EDGE,{"derivedFrom":sQuery(id+"F0.wireOp",EDGE,"4fdb3b29-39ac-43bd-bc66-8669c954de1c")}),1.0]])]});
            var Q5;
            Q5=makeQuery(id+"F0.imprint","IMPRINT",FACE,{"disambiguationData":[TD([[makeQuery(id+"F0.imprint","IMPRINT",EDGE,{"derivedFrom":sQuery(id+"F0.wireOp",EDGE,"808e690d-e3d5-4ff9-83cc-650897d1485f")}),-1.0]])]});
            var Q6;
            Q6=makeQuery(id+"F0.imprint","IMPRINT",FACE,{"disambiguationData":[TD([[makeQuery(id+"F0.imprint","IMPRINT",EDGE,{"derivedFrom":sQuery(id+"F0.wireOp",EDGE,"9b794eef-439e-4c34-9578-145f99b61c1a")}),-1.0]])]});
            var Q7;
            Q7=makeQuery(id+"F0.imprint","IMPRINT",FACE,{"disambiguationData":[TD([[makeQuery(id+"F0.imprint","IMPRINT",EDGE,{"derivedFrom":sQuery(id+"F0.wireOp",EDGE,"922c2041-e443-459e-83bf-41d0fe6fea8c")}),1.0]])]});
            var Q8;
            Q8=makeQuery(id+"F0.imprint","IMPRINT",FACE,{"disambiguationData":[TD([[makeQuery(id+"F0.imprint","IMPRINT",EDGE,{"derivedFrom":sQuery(id+"F0.wireOp",EDGE,"4334b9ef-0248-4e8d-a057-bc4742b6b903")}),1.0]])]});
            var Q9;
            Q9=makeQuery(id+"F0.imprint","IMPRINT",FACE,{"disambiguationData":[TD([[makeQuery(id+"F0.imprint","IMPRINT",EDGE,{"derivedFrom":sQuery(id+"F0.wireOp",EDGE,"cfa602e6-6e54-4bc0-9183-750d8819c109")}),1.0]])]});
            var Q10;
            Q10=makeQuery(id+"F0.imprint","IMPRINT",FACE,{"disambiguationData":[TD([[makeQuery(id+"F0.imprint","IMPRINT",EDGE,{"derivedFrom":sQuery(id+"F0.wireOp",EDGE,"506e52ac-4282-4965-a5fa-a03b34fe30a4")}),1.0]])]});
            var Q11;
            Q11=makeQuery(id+"F0.imprint","IMPRINT",FACE,{"disambiguationData":[TD([[makeQuery(id+"F0.imprint","IMPRINT",EDGE,{"derivedFrom":sQuery(id+"F0.wireOp",EDGE,"00019dc6-2a15-4ac2-a90f-bbf23ca46eec")}),-1.0]])]});
            var Q12;
            Q12=makeQuery(id+"F0.imprint","IMPRINT",FACE,{"disambiguationData":[TD([[makeQuery(id+"F0.imprint","IMPRINT",EDGE,{"derivedFrom":sQuery(id+"F0.wireOp",EDGE,"e483f996-d0c0-4b86-9525-90ddbaabdf2b")}),1.0]])]});
            var Q13;
            Q13=makeQuery(id+"F0.imprint","IMPRINT",FACE,{"disambiguationData":[TD([[makeQuery(id+"F0.imprint","IMPRINT",EDGE,{"derivedFrom":sQuery(id+"F0.wireOp",EDGE,"f84b8053-0fb6-4cb8-87b0-85ed06d30a1c")}),1.0]])]});
            var Q14;
            Q14=makeQuery(id+"F0.imprint","IMPRINT",FACE,{"disambiguationData":[TD([[makeQuery(id+"F0.imprint","IMPRINT",EDGE,{"derivedFrom":sQuery(id+"F0.wireOp",EDGE,"6837fe33-94b3-4554-b4cb-3039e83b973c")}),-1.0]])]});
            var Q15;
            {var subQ0=sQuery(id+"F0.wireOp",EDGE,"31528dcd-4179-4bcd-8357-7a5a1e418587");var subQ1=sQuery(id+"F0.wireOp",EDGE,"E18");var subQ2=makeQuery(id+"F0.imprint","INTERSECT",VERTEX,{"disambiguationData":[OD(0.0)],"derivedFrom":[subQ1,subQ0]});Q15=makeQuery(id+"F0.imprint","IMPRINT",FACE,{"disambiguationData":[TD([[makeQuery(id+"F0.imprint","IMPRINT",EDGE,{"disambiguationData":[TD([[subQ2,-1.0]])],"derivedFrom":subQ1}),-1.0]])]});}
            var Q16;
            {var subQ0=sQuery(id+"F0.wireOp",EDGE,"22335ca1-3f14-41f1-93af-506780826147");var subQ1=sQuery(id+"F0.wireOp",EDGE,"E18");var subQ2=makeQuery(id+"F0.imprint","INTERSECT",VERTEX,{"disambiguationData":[OD(0.0)],"derivedFrom":[subQ1,subQ0]});Q16=makeQuery(id+"F0.imprint","IMPRINT",FACE,{"disambiguationData":[TD([[makeQuery(id+"F0.imprint","IMPRINT",EDGE,{"disambiguationData":[TD([[subQ2,-1.0]])],"derivedFrom":subQ1}),-1.0]])]});}
            var Q17;
            {var subQ0=sQuery(id+"F0.wireOp",EDGE,"c03cf5a4-eea6-4ff4-8c67-c4a602e81abb");Q17=makeQuery(id+"F0.imprint","IMPRINT",FACE,{"disambiguationData":[TD([[makeQuery(id+"F0.imprint","IMPRINT",EDGE,{"derivedFrom":subQ0}),-1.0]])]});}
            var Q18;
            {var subQ0=sQuery(id+"F0.wireOp",EDGE,"E341");Q18=makeQuery(id+"F0.imprint","IMPRINT",FACE,{"disambiguationData":[TD([[makeQuery(id+"F0.imprint","IMPRINT",EDGE,{"derivedFrom":subQ0}),-1.0]])]});}
            var Q19;
            {var subQ0=sQuery(id+"F0.wireOp",EDGE,"E371");Q19=makeQuery(id+"F0.imprint","IMPRINT",FACE,{"disambiguationData":[TD([[makeQuery(id+"F0.imprint","IMPRINT",EDGE,{"derivedFrom":subQ0}),-1.0]])]});}
            var Q20;
            {var subQ0=sQuery(id+"F0.wireOp",EDGE,"E366");Q20=makeQuery(id+"F0.imprint","IMPRINT",FACE,{"disambiguationData":[TD([[makeQuery(id+"F0.imprint","IMPRINT",EDGE,{"derivedFrom":subQ0}),-1.0]])]});}
            var Q21;
            {var subQ0=sQuery(id+"F0.wireOp",EDGE,"E379");Q21=makeQuery(id+"F0.imprint","IMPRINT",FACE,{"disambiguationData":[TD([[makeQuery(id+"F0.imprint","IMPRINT",EDGE,{"derivedFrom":subQ0}),-1.0]])]});}
            var Q22;
            {var subQ0=sQuery(id+"F0.wireOp",EDGE,"E374");Q22=makeQuery(id+"F0.imprint","IMPRINT",FACE,{"disambiguationData":[TD([[makeQuery(id+"F0.imprint","IMPRINT",EDGE,{"derivedFrom":subQ0}),-1.0]])]});}
            var Q23;
            Q23=makeQuery(id+"F0.imprint","IMPRINT",FACE,{"disambiguationData":[TD([[makeQuery(id+"F0.imprint","IMPRINT",EDGE,{"derivedFrom":sQuery(id+"F0.wireOp",EDGE,"b9211f3b-afcf-4a0f-b91a-374bdd5e92ba.left")}),-1.0]])]});
            var Q24;
            Q24=makeQuery(id+"F0.imprint","IMPRINT",FACE,{"disambiguationData":[TD([[makeQuery(id+"F0.imprint","IMPRINT",EDGE,{"derivedFrom":sQuery(id+"F0.wireOp",EDGE,"fae31054-c315-4c31-bef9-0af093c6613f13.MirrorC")}),1.0]])]});
            var Q25;
            Q25=makeQuery(id+"F0.imprint","IMPRINT",FACE,{"disambiguationData":[TD([[makeQuery(id+"F0.imprint","IMPRINT",EDGE,{"derivedFrom":sQuery(id+"F0.wireOp",EDGE,"c16c1ed4-bd36-417a-a700-b7283e2a66766.MirrorCS")}),-1.0]])]});
            var Q26;
            Q26=makeQuery(id+"F0.imprint","IMPRINT",FACE,{"disambiguationData":[TD([[makeQuery(id+"F0.imprint","IMPRINT",EDGE,{"derivedFrom":sQuery(id+"F0.wireOp",EDGE,"dde74ec5-f8ce-49ca-b409-a50cd4ad9429.bottom")}),-1.0]])]});
            var Q27;
            Q27=makeQuery(id+"F0.imprint","IMPRINT",FACE,{"disambiguationData":[TD([[makeQuery(id+"F0.imprint","IMPRINT",EDGE,{"derivedFrom":sQuery(id+"F0.wireOp",EDGE,"63a18769-f30f-4872-98cb-53cc1980e498")}),-1.0]])]});
            var Q28;
            Q28=makeQuery(id+"F0.imprint","IMPRINT",FACE,{"disambiguationData":[TD([[makeQuery(id+"F0.imprint","IMPRINT",EDGE,{"derivedFrom":sQuery(id+"F0.wireOp",EDGE,"6f27b000-6735-4138-b63e-69c4e938d01e.bottom")}),-1.0]])]});
            extrude(context, id + "F1", {"entities" : qUnion([Q0, Q1, Q2, Q3, Q4, Q5, Q6, Q7, Q8, Q9, Q10, Q11, Q12, Q13, Q14, Q15, Q16, Q17, Q18, Q19, Q20, Q21, Q22, Q23, Q24, Q25, Q26, Q27, Q28]), "depth" : 3 * mm, "offsetDistance" : 25 * mm});
        }
        {
            var Q0;
            {var subQ0=sQuery(id+"F0.wireOp",EDGE,"E192");Q0=makeQuery(id+"F0.imprint","IMPRINT",FACE,{"disambiguationData":[TD([[makeQuery(id+"F0.imprint","IMPRINT",EDGE,{"derivedFrom":subQ0}),1.0]])]});}
            var Q1;
            {var subQ1=sQuery(id+"F0.wireOp",EDGE,"E261");Q1=makeQuery(id+"F0.imprint","IMPRINT",FACE,{"disambiguationData":[TD([[makeQuery(id+"F0.imprint","IMPRINT",EDGE,{"derivedFrom":subQ1}),1.0]])]});}
            var Q2;
            {var subQ0=sQuery(id+"F0.wireOp",EDGE,"E338");Q2=makeQuery(id+"F0.imprint","IMPRINT",FACE,{"disambiguationData":[TD([[makeQuery(id+"F0.imprint","IMPRINT",EDGE,{"derivedFrom":subQ0}),-1.0]])]});}
            var Q3;
            {var subQ0=sQuery(id+"F0.wireOp",EDGE,"E334");Q3=makeQuery(id+"F0.imprint","IMPRINT",FACE,{"disambiguationData":[TD([[makeQuery(id+"F0.imprint","IMPRINT",EDGE,{"derivedFrom":subQ0}),-1.0]])]});}
            var Q4;
            {var subQ0=sQuery(id+"F0.wireOp",EDGE,"E360");Q4=makeQuery(id+"F0.imprint","IMPRINT",FACE,{"disambiguationData":[TD([[makeQuery(id+"F0.imprint","IMPRINT",EDGE,{"derivedFrom":subQ0}),-1.0]])]});}
            var Q5;
            {var subQ0=sQuery(id+"F0.wireOp",EDGE,"E357");Q5=makeQuery(id+"F0.imprint","IMPRINT",FACE,{"disambiguationData":[TD([[makeQuery(id+"F0.imprint","IMPRINT",EDGE,{"derivedFrom":subQ0}),-1.0]])]});}
            extrude(context, id + "F2", {"entities" : qUnion([Q0, Q1, Q2, Q3, Q4, Q5]), "depth" : 3 * mm, "offsetDistance" : 25 * mm});
        }
        {
            var Q0;
            Q0=makeQuery(id+"F0.imprint","IMPRINT",FACE,{"disambiguationData":[TD([[makeQuery(id+"F0.imprint","IMPRINT",EDGE,{"derivedFrom":sQuery(id+"F0.wireOp",EDGE,"E312")}),1.0]])]});
            extrude(context, id + "F3", {"entities" : qUnion([Q0]), "depth" : 3 * mm, "offsetDistance" : 25 * mm});
        }
        {
            var Q0;
            Q0=makeQuery(id+"F0.imprint","IMPRINT",FACE,{"disambiguationData":[TD([[makeQuery(id+"F0.imprint","IMPRINT",EDGE,{"derivedFrom":sQuery(id+"F0.wireOp",EDGE,"E274")}),-1.0]])]});
            extrude(context, id + "F4", {"entities" : qUnion([Q0]), "depth" : 3 * mm, "offsetDistance" : 25 * mm});
        }
        {
            var Q0;
            Q0=makeQuery(id+"F0.imprint","IMPRINT",FACE,{"disambiguationData":[TD([[makeQuery(id+"F0.imprint","IMPRINT",EDGE,{"derivedFrom":sQuery(id+"F0.wireOp",EDGE,"E97")}),1.0]])]});
            extrude(context, id + "F5", {"entities" : qUnion([Q0]), "depth" : 3 * mm, "offsetDistance" : 25 * mm});
        }
        {
            var Q0;
            Q0=qCreatedBy(makeId("Front.planeOp"),FACE);
            var sketch = newSketch(context, id + "F6", { "sketchPlane" : qUnion([Q0])});
            skLineSegment(sketch, "E1595", {"start": v(-90, -142) * mm, "end": v(90, -142) * mm});
            skLineSegment(sketch, "E1596", {"start": v(160.5, -93) * mm, "end": v(125.9, -93) * mm});
            skCircle(sketch, "E1597", {"center": v(-85, -100) * mm, "radius": 4.1 * mm});
            skCircle(sketch, "E1598", {"center": v(85, -100) * mm, "radius": 4.1 * mm});
            skCircle(sketch, "E1599", {"center": v(71, -100) * mm, "radius": 1.6 * mm});
            skCircle(sketch, "E1600", {"center": v(-71, -100) * mm, "radius": 1.6 * mm});
            skLineSegment(sketch, "E1601", {"start": v(-155.6, -5) * mm, "end": v(-92, -5) * mm});
            skLineSegment(sketch, "E1602", {"start": v(-90, -2) * mm, "end": v(90, -2) * mm});
            skLineSegment(sketch, "E1603", {"start": v(92, -5) * mm, "end": v(155.6, -5) * mm});
            skLineSegment(sketch, "E1604", {"start": v(167.5, 10.1) * mm, "end": v(167.5, 50) * mm});
            skArc(sketch, "E1605", {"start": v(167.5, 50) * mm, "mid": v(165.45, 54.95) * mm, "end": v(160.5, 57) * mm});
            skLineSegment(sketch, "E1606", {"start": v(160.5, 57) * mm, "end": v(125.9, 57) * mm});
            skArc(sketch, "E1607", {"start": v(125.9, 57) * mm, "mid": v(120.95, 54.95) * mm, "end": v(118.9, 50) * mm});
            skLineSegment(sketch, "E1608", {"start": v(118.9, 50) * mm, "end": v(118.9, 32) * mm});
            skLineSegment(sketch, "E1609", {"start": v(118.9, 32) * mm, "end": v(94.5, 32) * mm});
            skLineSegment(sketch, "E1610", {"start": v(94.5, 32) * mm, "end": v(94.5, 40) * mm});
            skArc(sketch, "E1611", {"start": v(94.5, 40) * mm, "mid": v(92.45, 44.95) * mm, "end": v(87.5, 47) * mm});
            skLineSegment(sketch, "E1612", {"start": v(87.5, 47) * mm, "end": v(-87.5, 47) * mm});
            skArc(sketch, "E1613", {"start": v(-87.5, 47) * mm, "mid": v(-92.45, 44.95) * mm, "end": v(-94.5, 40) * mm});
            skLineSegment(sketch, "E1614", {"start": v(-94.5, 40) * mm, "end": v(-94.5, 32) * mm});
            skLineSegment(sketch, "E1615", {"start": v(-94.5, 32) * mm, "end": v(-118.9, 32) * mm});
            skLineSegment(sketch, "E1616", {"start": v(-118.9, 32) * mm, "end": v(-118.9, 50) * mm});
            skArc(sketch, "E1617", {"start": v(-118.9, 50) * mm, "mid": v(-120.95, 54.95) * mm, "end": v(-125.9, 57) * mm});
            skLineSegment(sketch, "E1618", {"start": v(-125.9, 57) * mm, "end": v(-160.5, 57) * mm});
            skArc(sketch, "E1619", {"start": v(-160.5, 57) * mm, "mid": v(-165.45, 54.95) * mm, "end": v(-167.5, 50) * mm});
            skLineSegment(sketch, "E1620", {"start": v(-167.5, 50) * mm, "end": v(-167.5, 10.1) * mm});
            skCircle(sketch, "E1621", {"center": v(-21, 22) * mm, "radius": 10 * mm});
            skCircle(sketch, "E1622", {"center": v(131.75, 8.5) * mm, "radius": 8 * mm});
            skLineSegment(sketch, "E1623", {"start": v(-149.4, 26.07) * mm, "end": v(-149.4, 44.93) * mm});
            skLineSegment(sketch, "E1624", {"start": v(-152.6, 44.93) * mm, "end": v(-152.6, 26.07) * mm});
            skLineSegment(sketch, "E1625", {"start": v(149.4, 44.93) * mm, "end": v(149.4, 26.07) * mm});
            skLineSegment(sketch, "E1626", {"start": v(152.6, 26.07) * mm, "end": v(152.6, 44.93) * mm});
            skLineSegment(sketch, "E1627", {"start": v(51.2, 30.83) * mm, "end": v(51.2, 17.17) * mm});
            skLineSegment(sketch, "E1628", {"start": v(48, 17.17) * mm, "end": v(48, 30.83) * mm});
            skLineSegment(sketch, "E1629", {"start": v(13.4, 30.63) * mm, "end": v(13.4, 20.37) * mm});
            skLineSegment(sketch, "E1630", {"start": v(16.6, 20.37) * mm, "end": v(16.6, 30.63) * mm});
            skCircle(sketch, "E1631", {"center": v(-109, 23) * mm, "radius": 4.1 * mm, "construction": true});
            skCircle(sketch, "E1632", {"center": v(109, 23) * mm, "radius": 4.1 * mm, "construction": true});
            skCircle(sketch, "E1633", {"center": v(85, 40) * mm, "radius": 4.1 * mm});
            skCircle(sketch, "E1634", {"center": v(-85, 40) * mm, "radius": 4.1 * mm});
            skCircle(sketch, "E1635", {"center": v(151, 19.8) * mm, "radius": 1.6 * mm});
            skCircle(sketch, "E1636", {"center": v(-151, 19.8) * mm, "radius": 1.6 * mm});
            skCircle(sketch, "E1637", {"center": v(49.6, 9) * mm, "radius": 1.6 * mm});
            skCircle(sketch, "E1638", {"center": v(15, 9) * mm, "radius": 1.6 * mm});
            skCircle(sketch, "E1639", {"center": v(71, 40) * mm, "radius": 1.6 * mm});
            skCircle(sketch, "E1640", {"center": v(-71, 40) * mm, "radius": 1.6 * mm});
            skCircle(sketch, "E1641", {"center": v(-59.5, 30.5) * mm, "radius": 1.6 * mm});
            skCircle(sketch, "E1642", {"center": v(15, 38) * mm, "radius": 1.6 * mm});
            skCircle(sketch, "E1643", {"center": v(151, 51.2) * mm, "radius": 1.6 * mm});
            skCircle(sketch, "E1644", {"center": v(-151, 51.2) * mm, "radius": 1.6 * mm});
            skLineSegment(sketch, "E1645", {"start": v(0, -218.39) * mm, "end": v(0, 203.5) * mm, "construction": true});
            skLineSegment(sketch, "E1646", {"start": v(167.5, -100) * mm, "end": v(167.5, -129.9) * mm});
            skLineSegment(sketch, "E1647", {"start": v(-167.5, -100) * mm, "end": v(-167.5, -129.9) * mm});
            skLineSegment(sketch, "E1648", {"start": v(-92, -145) * mm, "end": v(-155.6, -145) * mm});
            skLineSegment(sketch, "E1649", {"start": v(92, -145) * mm, "end": v(155.6, -145) * mm});
            skCircle(sketch, "E1650", {"center": v(6.1, -111.95) * mm, "radius": 1.6 * mm});
            skCircle(sketch, "E1651", {"center": v(-6.1, -111.95) * mm, "radius": 1.6 * mm});
            skCircle(sketch, "E1652", {"center": v(83.75, -131.5) * mm, "radius": 1.6 * mm});
            skArc(sketch, "E1653.filletArc", {"start": v(-160.5, -93) * mm, "mid": v(-165.45, -95.05) * mm, "end": v(-167.5, -100) * mm});
            skArc(sketch, "E1654.filletArc", {"start": v(167.5, -100) * mm, "mid": v(165.45, -95.05) * mm, "end": v(160.5, -93) * mm});
            skLineSegment(sketch, "E1655.bottom", {"start": v(79, -130.77) * mm, "end": v(79, -132.23) * mm});
            skLineSegment(sketch, "E1655.top", {"start": v(70.6, -130.77) * mm, "end": v(70.6, -132.23) * mm});
            skLineSegment(sketch, "E1655.left", {"start": v(78.13, -129.9) * mm, "end": v(71.47, -129.9) * mm});
            skLineSegment(sketch, "E1655.right", {"start": v(78.13, -133.1) * mm, "end": v(71.47, -133.1) * mm});
            skArc(sketch, "E1656", {"start": v(79, -132.23) * mm, "mid": v(79.07, -132.48) * mm, "end": v(79.25, -132.67) * mm});
            skArc(sketch, "E1657", {"start": v(78.57, -133.35) * mm, "mid": v(79.35, -133.45) * mm, "end": v(79.25, -132.67) * mm});
            skArc(sketch, "E1658", {"start": v(78.57, -133.35) * mm, "mid": v(78.38, -133.17) * mm, "end": v(78.13, -133.1) * mm});
            skArc(sketch, "E1659", {"start": v(78.13, -129.9) * mm, "mid": v(78.38, -129.83) * mm, "end": v(78.57, -129.65) * mm});
            skArc(sketch, "E1660", {"start": v(79.25, -130.33) * mm, "mid": v(79.35, -129.55) * mm, "end": v(78.57, -129.65) * mm});
            skArc(sketch, "E1661", {"start": v(79.25, -130.33) * mm, "mid": v(79.07, -130.52) * mm, "end": v(79, -130.77) * mm});
            skArc(sketch, "E1662", {"start": v(71.47, -133.1) * mm, "mid": v(71.22, -133.17) * mm, "end": v(71.03, -133.35) * mm});
            skArc(sketch, "E1663", {"start": v(70.35, -132.67) * mm, "mid": v(70.25, -133.45) * mm, "end": v(71.03, -133.35) * mm});
            skArc(sketch, "E1664", {"start": v(70.35, -132.67) * mm, "mid": v(70.53, -132.48) * mm, "end": v(70.6, -132.23) * mm});
            skArc(sketch, "E1665", {"start": v(70.6, -130.77) * mm, "mid": v(70.53, -130.52) * mm, "end": v(70.35, -130.33) * mm});
            skArc(sketch, "E1666", {"start": v(71.03, -129.65) * mm, "mid": v(70.25, -129.55) * mm, "end": v(70.35, -130.33) * mm});
            skArc(sketch, "E1667", {"start": v(71.03, -129.65) * mm, "mid": v(71.22, -129.83) * mm, "end": v(71.47, -129.9) * mm});
            skLineSegment(sketch, "E1668.bottom", {"start": v(96.9, -130.77) * mm, "end": v(96.9, -132.23) * mm});
            skLineSegment(sketch, "E1668.top", {"start": v(88.5, -130.77) * mm, "end": v(88.5, -132.23) * mm});
            skLineSegment(sketch, "E1668.left", {"start": v(96.03, -129.9) * mm, "end": v(89.37, -129.9) * mm});
            skLineSegment(sketch, "E1668.right", {"start": v(96.03, -133.1) * mm, "end": v(89.37, -133.1) * mm});
            skArc(sketch, "E1669", {"start": v(96.9, -132.23) * mm, "mid": v(96.97, -132.48) * mm, "end": v(97.15, -132.67) * mm});
            skArc(sketch, "E1670", {"start": v(96.47, -133.35) * mm, "mid": v(97.25, -133.45) * mm, "end": v(97.15, -132.67) * mm});
            skArc(sketch, "E1671", {"start": v(96.47, -133.35) * mm, "mid": v(96.28, -133.17) * mm, "end": v(96.03, -133.1) * mm});
            skArc(sketch, "E1672", {"start": v(96.03, -129.9) * mm, "mid": v(96.28, -129.83) * mm, "end": v(96.47, -129.65) * mm});
            skArc(sketch, "E1673", {"start": v(97.15, -130.33) * mm, "mid": v(97.25, -129.55) * mm, "end": v(96.47, -129.65) * mm});
            skArc(sketch, "E1674", {"start": v(97.15, -130.33) * mm, "mid": v(96.97, -130.52) * mm, "end": v(96.9, -130.77) * mm});
            skArc(sketch, "E1675", {"start": v(89.37, -133.1) * mm, "mid": v(89.12, -133.17) * mm, "end": v(88.93, -133.35) * mm});
            skArc(sketch, "E1676", {"start": v(88.25, -132.67) * mm, "mid": v(88.15, -133.45) * mm, "end": v(88.93, -133.35) * mm});
            skArc(sketch, "E1677", {"start": v(88.25, -132.67) * mm, "mid": v(88.43, -132.48) * mm, "end": v(88.5, -132.23) * mm});
            skArc(sketch, "E1678", {"start": v(88.5, -130.77) * mm, "mid": v(88.43, -130.52) * mm, "end": v(88.25, -130.33) * mm});
            skArc(sketch, "E1679", {"start": v(88.93, -129.65) * mm, "mid": v(88.15, -129.55) * mm, "end": v(88.25, -130.33) * mm});
            skArc(sketch, "E1680", {"start": v(88.93, -129.65) * mm, "mid": v(89.12, -129.83) * mm, "end": v(89.37, -129.9) * mm});
            skCircle(sketch, "E1681", {"center": v(-83.75, -131.5) * mm, "radius": 1.6 * mm});
            skLineSegment(sketch, "E1682.bottom", {"start": v(-88.5, -130.77) * mm, "end": v(-88.5, -132.23) * mm});
            skLineSegment(sketch, "E1682.top", {"start": v(-96.9, -130.77) * mm, "end": v(-96.9, -132.23) * mm});
            skLineSegment(sketch, "E1682.left", {"start": v(-89.37, -129.9) * mm, "end": v(-96.03, -129.9) * mm});
            skLineSegment(sketch, "E1682.right", {"start": v(-89.37, -133.1) * mm, "end": v(-96.03, -133.1) * mm});
            skArc(sketch, "E1683", {"start": v(-88.5, -132.23) * mm, "mid": v(-88.43, -132.48) * mm, "end": v(-88.25, -132.67) * mm});
            skArc(sketch, "E1684", {"start": v(-88.93, -133.35) * mm, "mid": v(-88.15, -133.45) * mm, "end": v(-88.25, -132.67) * mm});
            skArc(sketch, "E1685", {"start": v(-88.93, -133.35) * mm, "mid": v(-89.12, -133.17) * mm, "end": v(-89.37, -133.1) * mm});
            skArc(sketch, "E1686", {"start": v(-89.37, -129.9) * mm, "mid": v(-89.12, -129.83) * mm, "end": v(-88.93, -129.65) * mm});
            skArc(sketch, "E1687", {"start": v(-88.25, -130.33) * mm, "mid": v(-88.15, -129.55) * mm, "end": v(-88.93, -129.65) * mm});
            skArc(sketch, "E1688", {"start": v(-88.25, -130.33) * mm, "mid": v(-88.43, -130.52) * mm, "end": v(-88.5, -130.77) * mm});
            skArc(sketch, "E1689", {"start": v(-96.03, -133.1) * mm, "mid": v(-96.28, -133.17) * mm, "end": v(-96.47, -133.35) * mm});
            skArc(sketch, "E1690", {"start": v(-97.15, -132.67) * mm, "mid": v(-97.25, -133.45) * mm, "end": v(-96.47, -133.35) * mm});
            skArc(sketch, "E1691", {"start": v(-97.15, -132.67) * mm, "mid": v(-96.97, -132.48) * mm, "end": v(-96.9, -132.23) * mm});
            skArc(sketch, "E1692", {"start": v(-96.9, -130.77) * mm, "mid": v(-96.97, -130.52) * mm, "end": v(-97.15, -130.33) * mm});
            skArc(sketch, "E1693", {"start": v(-96.47, -129.65) * mm, "mid": v(-97.25, -129.55) * mm, "end": v(-97.15, -130.33) * mm});
            skArc(sketch, "E1694", {"start": v(-96.47, -129.65) * mm, "mid": v(-96.28, -129.83) * mm, "end": v(-96.03, -129.9) * mm});
            skLineSegment(sketch, "E1695.bottom", {"start": v(-70.6, -130.77) * mm, "end": v(-70.6, -132.23) * mm});
            skLineSegment(sketch, "E1695.top", {"start": v(-79, -130.77) * mm, "end": v(-79, -132.23) * mm});
            skLineSegment(sketch, "E1695.left", {"start": v(-71.47, -129.9) * mm, "end": v(-78.13, -129.9) * mm});
            skLineSegment(sketch, "E1695.right", {"start": v(-71.47, -133.1) * mm, "end": v(-78.13, -133.1) * mm});
            skArc(sketch, "E1696", {"start": v(-70.6, -132.23) * mm, "mid": v(-70.53, -132.48) * mm, "end": v(-70.35, -132.67) * mm});
            skArc(sketch, "E1697", {"start": v(-71.03, -133.35) * mm, "mid": v(-70.25, -133.45) * mm, "end": v(-70.35, -132.67) * mm});
            skArc(sketch, "E1698", {"start": v(-71.03, -133.35) * mm, "mid": v(-71.22, -133.17) * mm, "end": v(-71.47, -133.1) * mm});
            skArc(sketch, "E1699", {"start": v(-71.47, -129.9) * mm, "mid": v(-71.22, -129.83) * mm, "end": v(-71.03, -129.65) * mm});
            skArc(sketch, "E1700", {"start": v(-70.35, -130.33) * mm, "mid": v(-70.25, -129.55) * mm, "end": v(-71.03, -129.65) * mm});
            skArc(sketch, "E1701", {"start": v(-70.35, -130.33) * mm, "mid": v(-70.53, -130.52) * mm, "end": v(-70.6, -130.77) * mm});
            skArc(sketch, "E1702", {"start": v(-78.13, -133.1) * mm, "mid": v(-78.38, -133.17) * mm, "end": v(-78.57, -133.35) * mm});
            skArc(sketch, "E1703", {"start": v(-79.25, -132.67) * mm, "mid": v(-79.35, -133.45) * mm, "end": v(-78.57, -133.35) * mm});
            skArc(sketch, "E1704", {"start": v(-79.25, -132.67) * mm, "mid": v(-79.07, -132.48) * mm, "end": v(-79, -132.23) * mm});
            skArc(sketch, "E1705", {"start": v(-79, -130.77) * mm, "mid": v(-79.07, -130.52) * mm, "end": v(-79.25, -130.33) * mm});
            skArc(sketch, "E1706", {"start": v(-78.57, -129.65) * mm, "mid": v(-79.35, -129.55) * mm, "end": v(-79.25, -130.33) * mm});
            skArc(sketch, "E1707", {"start": v(-78.57, -129.65) * mm, "mid": v(-78.38, -129.83) * mm, "end": v(-78.13, -129.9) * mm});
            skCircle(sketch, "E1708", {"center": v(-151, -116.5) * mm, "radius": 1.6 * mm});
            skLineSegment(sketch, "E1709.bottom", {"start": v(-150.27, -111.75) * mm, "end": v(-151.73, -111.75) * mm});
            skLineSegment(sketch, "E1709.top", {"start": v(-150.27, -105.55) * mm, "end": v(-151.73, -105.55) * mm});
            skLineSegment(sketch, "E1709.left", {"start": v(-149.4, -110.88) * mm, "end": v(-149.4, -106.42) * mm});
            skLineSegment(sketch, "E1709.right", {"start": v(-152.6, -110.88) * mm, "end": v(-152.6, -106.42) * mm});
            skArc(sketch, "E1710", {"start": v(-151.73, -111.75) * mm, "mid": v(-151.98, -111.82) * mm, "end": v(-152.17, -112) * mm});
            skArc(sketch, "E1711", {"start": v(-152.85, -111.32) * mm, "mid": v(-152.95, -112.1) * mm, "end": v(-152.17, -112) * mm});
            skArc(sketch, "E1712", {"start": v(-152.85, -111.32) * mm, "mid": v(-152.67, -111.13) * mm, "end": v(-152.6, -110.88) * mm});
            skArc(sketch, "E1713", {"start": v(-149.4, -110.88) * mm, "mid": v(-149.33, -111.13) * mm, "end": v(-149.15, -111.32) * mm});
            skArc(sketch, "E1714", {"start": v(-149.83, -112) * mm, "mid": v(-149.05, -112.1) * mm, "end": v(-149.15, -111.32) * mm});
            skArc(sketch, "E1715", {"start": v(-149.83, -112) * mm, "mid": v(-150.02, -111.82) * mm, "end": v(-150.27, -111.75) * mm});
            skArc(sketch, "E1716", {"start": v(-152.6, -106.42) * mm, "mid": v(-152.67, -106.17) * mm, "end": v(-152.85, -105.98) * mm});
            skArc(sketch, "E1717", {"start": v(-152.17, -105.3) * mm, "mid": v(-152.95, -105.2) * mm, "end": v(-152.85, -105.98) * mm});
            skArc(sketch, "E1718", {"start": v(-152.17, -105.3) * mm, "mid": v(-151.98, -105.48) * mm, "end": v(-151.73, -105.55) * mm});
            skArc(sketch, "E1719", {"start": v(-150.27, -105.55) * mm, "mid": v(-150.02, -105.48) * mm, "end": v(-149.83, -105.3) * mm});
            skArc(sketch, "E1720", {"start": v(-149.15, -105.98) * mm, "mid": v(-149.05, -105.2) * mm, "end": v(-149.83, -105.3) * mm});
            skArc(sketch, "E1721", {"start": v(-149.15, -105.98) * mm, "mid": v(-149.33, -106.17) * mm, "end": v(-149.4, -106.42) * mm});
            skLineSegment(sketch, "E1722.bottom", {"start": v(-150.27, -127.45) * mm, "end": v(-151.73, -127.45) * mm});
            skLineSegment(sketch, "E1722.top", {"start": v(-150.27, -121.25) * mm, "end": v(-151.73, -121.25) * mm});
            skLineSegment(sketch, "E1722.left", {"start": v(-149.4, -126.58) * mm, "end": v(-149.4, -122.12) * mm});
            skLineSegment(sketch, "E1722.right", {"start": v(-152.6, -126.58) * mm, "end": v(-152.6, -122.12) * mm});
            skArc(sketch, "E1723", {"start": v(-151.73, -127.45) * mm, "mid": v(-151.98, -127.52) * mm, "end": v(-152.17, -127.7) * mm});
            skArc(sketch, "E1724", {"start": v(-152.85, -127.02) * mm, "mid": v(-152.95, -127.8) * mm, "end": v(-152.17, -127.7) * mm});
            skArc(sketch, "E1725", {"start": v(-152.85, -127.02) * mm, "mid": v(-152.67, -126.83) * mm, "end": v(-152.6, -126.58) * mm});
            skArc(sketch, "E1726", {"start": v(-149.4, -126.58) * mm, "mid": v(-149.33, -126.83) * mm, "end": v(-149.15, -127.02) * mm});
            skArc(sketch, "E1727", {"start": v(-149.83, -127.7) * mm, "mid": v(-149.05, -127.8) * mm, "end": v(-149.15, -127.02) * mm});
            skArc(sketch, "E1728", {"start": v(-149.83, -127.7) * mm, "mid": v(-150.02, -127.52) * mm, "end": v(-150.27, -127.45) * mm});
            skArc(sketch, "E1729", {"start": v(-152.6, -122.12) * mm, "mid": v(-152.67, -121.87) * mm, "end": v(-152.85, -121.68) * mm});
            skArc(sketch, "E1730", {"start": v(-152.17, -121) * mm, "mid": v(-152.95, -120.9) * mm, "end": v(-152.85, -121.68) * mm});
            skArc(sketch, "E1731", {"start": v(-152.17, -121) * mm, "mid": v(-151.98, -121.18) * mm, "end": v(-151.73, -121.25) * mm});
            skArc(sketch, "E1732", {"start": v(-150.27, -121.25) * mm, "mid": v(-150.02, -121.18) * mm, "end": v(-149.83, -121) * mm});
            skArc(sketch, "E1733", {"start": v(-149.15, -121.68) * mm, "mid": v(-149.05, -120.9) * mm, "end": v(-149.83, -121) * mm});
            skArc(sketch, "E1734", {"start": v(-149.15, -121.68) * mm, "mid": v(-149.33, -121.87) * mm, "end": v(-149.4, -122.12) * mm});
            skCircle(sketch, "E1735", {"center": v(151, -116.5) * mm, "radius": 1.6 * mm});
            skLineSegment(sketch, "E1736.bottom", {"start": v(151.73, -111.75) * mm, "end": v(150.27, -111.75) * mm});
            skLineSegment(sketch, "E1736.top", {"start": v(151.73, -105.55) * mm, "end": v(150.27, -105.55) * mm});
            skLineSegment(sketch, "E1736.left", {"start": v(152.6, -110.88) * mm, "end": v(152.6, -106.42) * mm});
            skLineSegment(sketch, "E1736.right", {"start": v(149.4, -110.88) * mm, "end": v(149.4, -106.42) * mm});
            skArc(sketch, "E1737", {"start": v(150.27, -111.75) * mm, "mid": v(150.02, -111.82) * mm, "end": v(149.83, -112) * mm});
            skArc(sketch, "E1738", {"start": v(149.15, -111.32) * mm, "mid": v(149.05, -112.1) * mm, "end": v(149.83, -112) * mm});
            skArc(sketch, "E1739", {"start": v(149.15, -111.32) * mm, "mid": v(149.33, -111.13) * mm, "end": v(149.4, -110.88) * mm});
            skArc(sketch, "E1740", {"start": v(152.6, -110.88) * mm, "mid": v(152.67, -111.13) * mm, "end": v(152.85, -111.32) * mm});
            skArc(sketch, "E1741", {"start": v(152.17, -112) * mm, "mid": v(152.95, -112.1) * mm, "end": v(152.85, -111.32) * mm});
            skArc(sketch, "E1742", {"start": v(152.17, -112) * mm, "mid": v(151.98, -111.82) * mm, "end": v(151.73, -111.75) * mm});
            skArc(sketch, "E1743", {"start": v(149.4, -106.42) * mm, "mid": v(149.33, -106.17) * mm, "end": v(149.15, -105.98) * mm});
            skArc(sketch, "E1744", {"start": v(149.83, -105.3) * mm, "mid": v(149.05, -105.2) * mm, "end": v(149.15, -105.98) * mm});
            skArc(sketch, "E1745", {"start": v(149.83, -105.3) * mm, "mid": v(150.02, -105.48) * mm, "end": v(150.27, -105.55) * mm});
            skArc(sketch, "E1746", {"start": v(151.73, -105.55) * mm, "mid": v(151.98, -105.48) * mm, "end": v(152.17, -105.3) * mm});
            skArc(sketch, "E1747", {"start": v(152.85, -105.98) * mm, "mid": v(152.95, -105.2) * mm, "end": v(152.17, -105.3) * mm});
            skArc(sketch, "E1748", {"start": v(152.85, -105.98) * mm, "mid": v(152.67, -106.17) * mm, "end": v(152.6, -106.42) * mm});
            skLineSegment(sketch, "E1749.bottom", {"start": v(151.73, -127.45) * mm, "end": v(150.27, -127.45) * mm});
            skLineSegment(sketch, "E1749.top", {"start": v(151.73, -121.25) * mm, "end": v(150.27, -121.25) * mm});
            skLineSegment(sketch, "E1749.left", {"start": v(152.6, -126.58) * mm, "end": v(152.6, -122.12) * mm});
            skLineSegment(sketch, "E1749.right", {"start": v(149.4, -126.58) * mm, "end": v(149.4, -122.12) * mm});
            skArc(sketch, "E1750", {"start": v(150.27, -127.45) * mm, "mid": v(150.02, -127.52) * mm, "end": v(149.83, -127.7) * mm});
            skArc(sketch, "E1751", {"start": v(149.15, -127.02) * mm, "mid": v(149.05, -127.8) * mm, "end": v(149.83, -127.7) * mm});
            skArc(sketch, "E1752", {"start": v(149.15, -127.02) * mm, "mid": v(149.33, -126.83) * mm, "end": v(149.4, -126.58) * mm});
            skArc(sketch, "E1753", {"start": v(152.6, -126.58) * mm, "mid": v(152.67, -126.83) * mm, "end": v(152.85, -127.02) * mm});
            skArc(sketch, "E1754", {"start": v(152.17, -127.7) * mm, "mid": v(152.95, -127.8) * mm, "end": v(152.85, -127.02) * mm});
            skArc(sketch, "E1755", {"start": v(152.17, -127.7) * mm, "mid": v(151.98, -127.52) * mm, "end": v(151.73, -127.45) * mm});
            skArc(sketch, "E1756", {"start": v(149.4, -122.12) * mm, "mid": v(149.33, -121.87) * mm, "end": v(149.15, -121.68) * mm});
            skArc(sketch, "E1757", {"start": v(149.83, -121) * mm, "mid": v(149.05, -120.9) * mm, "end": v(149.15, -121.68) * mm});
            skArc(sketch, "E1758", {"start": v(149.83, -121) * mm, "mid": v(150.02, -121.18) * mm, "end": v(150.27, -121.25) * mm});
            skArc(sketch, "E1759", {"start": v(151.73, -121.25) * mm, "mid": v(151.98, -121.18) * mm, "end": v(152.17, -121) * mm});
            skArc(sketch, "E1760", {"start": v(152.85, -121.68) * mm, "mid": v(152.95, -120.9) * mm, "end": v(152.17, -121) * mm});
            skArc(sketch, "E1761", {"start": v(152.85, -121.68) * mm, "mid": v(152.67, -121.87) * mm, "end": v(152.6, -122.12) * mm});
            skLineSegment(sketch, "E1762.bottom", {"start": v(151.73, 25.2) * mm, "end": v(150.27, 25.2) * mm});
            skLineSegment(sketch, "E1762.top", {"start": v(151.73, 45.8) * mm, "end": v(150.27, 45.8) * mm});
            skArc(sketch, "E1763", {"start": v(150.27, 25.2) * mm, "mid": v(150.02, 25.13) * mm, "end": v(149.83, 24.95) * mm});
            skArc(sketch, "E1764", {"start": v(149.15, 25.63) * mm, "mid": v(149.05, 24.85) * mm, "end": v(149.83, 24.95) * mm});
            skArc(sketch, "E1765", {"start": v(149.15, 25.63) * mm, "mid": v(149.33, 25.82) * mm, "end": v(149.4, 26.07) * mm});
            skArc(sketch, "E1766", {"start": v(152.6, 26.07) * mm, "mid": v(152.67, 25.82) * mm, "end": v(152.85, 25.63) * mm});
            skArc(sketch, "E1767", {"start": v(152.17, 24.95) * mm, "mid": v(152.95, 24.85) * mm, "end": v(152.85, 25.63) * mm});
            skArc(sketch, "E1768", {"start": v(152.17, 24.95) * mm, "mid": v(151.98, 25.13) * mm, "end": v(151.73, 25.2) * mm});
            skArc(sketch, "E1769", {"start": v(149.4, 44.93) * mm, "mid": v(149.33, 45.18) * mm, "end": v(149.15, 45.37) * mm});
            skArc(sketch, "E1770", {"start": v(149.83, 46.05) * mm, "mid": v(149.05, 46.15) * mm, "end": v(149.15, 45.37) * mm});
            skArc(sketch, "E1771", {"start": v(149.83, 46.05) * mm, "mid": v(150.02, 45.87) * mm, "end": v(150.27, 45.8) * mm});
            skArc(sketch, "E1772", {"start": v(151.73, 45.8) * mm, "mid": v(151.98, 45.87) * mm, "end": v(152.17, 46.05) * mm});
            skArc(sketch, "E1773", {"start": v(152.85, 45.37) * mm, "mid": v(152.95, 46.15) * mm, "end": v(152.17, 46.05) * mm});
            skArc(sketch, "E1774", {"start": v(152.85, 45.37) * mm, "mid": v(152.67, 45.18) * mm, "end": v(152.6, 44.93) * mm});
            skLineSegment(sketch, "E1775.bottom", {"start": v(50.33, 16.3) * mm, "end": v(48.87, 16.3) * mm});
            skLineSegment(sketch, "E1775.top", {"start": v(50.33, 31.7) * mm, "end": v(48.87, 31.7) * mm});
            skArc(sketch, "E1776", {"start": v(48.87, 16.3) * mm, "mid": v(48.62, 16.23) * mm, "end": v(48.43, 16.05) * mm});
            skArc(sketch, "E1777", {"start": v(47.75, 16.73) * mm, "mid": v(47.65, 15.95) * mm, "end": v(48.43, 16.05) * mm});
            skArc(sketch, "E1778", {"start": v(47.75, 16.73) * mm, "mid": v(47.93, 16.92) * mm, "end": v(48, 17.17) * mm});
            skArc(sketch, "E1779", {"start": v(51.2, 17.17) * mm, "mid": v(51.27, 16.92) * mm, "end": v(51.45, 16.73) * mm});
            skArc(sketch, "E1780", {"start": v(50.77, 16.05) * mm, "mid": v(51.55, 15.95) * mm, "end": v(51.45, 16.73) * mm});
            skArc(sketch, "E1781", {"start": v(50.77, 16.05) * mm, "mid": v(50.58, 16.23) * mm, "end": v(50.33, 16.3) * mm});
            skArc(sketch, "E1782", {"start": v(48, 30.83) * mm, "mid": v(47.93, 31.08) * mm, "end": v(47.75, 31.27) * mm});
            skArc(sketch, "E1783", {"start": v(48.43, 31.95) * mm, "mid": v(47.65, 32.05) * mm, "end": v(47.75, 31.27) * mm});
            skArc(sketch, "E1784", {"start": v(48.43, 31.95) * mm, "mid": v(48.62, 31.77) * mm, "end": v(48.87, 31.7) * mm});
            skArc(sketch, "E1785", {"start": v(50.33, 31.7) * mm, "mid": v(50.58, 31.77) * mm, "end": v(50.77, 31.95) * mm});
            skArc(sketch, "E1786", {"start": v(51.45, 31.27) * mm, "mid": v(51.55, 32.05) * mm, "end": v(50.77, 31.95) * mm});
            skArc(sketch, "E1787", {"start": v(51.45, 31.27) * mm, "mid": v(51.27, 31.08) * mm, "end": v(51.2, 30.83) * mm});
            skLineSegment(sketch, "E1788.bottom", {"start": v(15.73, 19.5) * mm, "end": v(14.27, 19.5) * mm});
            skLineSegment(sketch, "E1788.top", {"start": v(15.73, 31.5) * mm, "end": v(14.27, 31.5) * mm});
            skArc(sketch, "E1789", {"start": v(14.27, 19.5) * mm, "mid": v(14.02, 19.43) * mm, "end": v(13.83, 19.25) * mm});
            skArc(sketch, "E1790", {"start": v(13.15, 19.93) * mm, "mid": v(13.05, 19.15) * mm, "end": v(13.83, 19.25) * mm});
            skArc(sketch, "E1791", {"start": v(13.15, 19.93) * mm, "mid": v(13.33, 20.12) * mm, "end": v(13.4, 20.37) * mm});
            skArc(sketch, "E1792", {"start": v(16.6, 20.37) * mm, "mid": v(16.67, 20.12) * mm, "end": v(16.85, 19.93) * mm});
            skArc(sketch, "E1793", {"start": v(16.17, 19.25) * mm, "mid": v(16.95, 19.15) * mm, "end": v(16.85, 19.93) * mm});
            skArc(sketch, "E1794", {"start": v(16.17, 19.25) * mm, "mid": v(15.98, 19.43) * mm, "end": v(15.73, 19.5) * mm});
            skArc(sketch, "E1795", {"start": v(13.4, 30.63) * mm, "mid": v(13.33, 30.88) * mm, "end": v(13.15, 31.07) * mm});
            skArc(sketch, "E1796", {"start": v(13.83, 31.75) * mm, "mid": v(13.05, 31.85) * mm, "end": v(13.15, 31.07) * mm});
            skArc(sketch, "E1797", {"start": v(13.83, 31.75) * mm, "mid": v(14.02, 31.57) * mm, "end": v(14.27, 31.5) * mm});
            skArc(sketch, "E1798", {"start": v(15.73, 31.5) * mm, "mid": v(15.98, 31.57) * mm, "end": v(16.17, 31.75) * mm});
            skArc(sketch, "E1799", {"start": v(16.85, 31.07) * mm, "mid": v(16.95, 31.85) * mm, "end": v(16.17, 31.75) * mm});
            skArc(sketch, "E1800", {"start": v(16.85, 31.07) * mm, "mid": v(16.67, 30.88) * mm, "end": v(16.6, 30.63) * mm});
            skLineSegment(sketch, "E1801.bottom", {"start": v(-69.1, 31.23) * mm, "end": v(-69.1, 29.77) * mm});
            skLineSegment(sketch, "E1801.top", {"start": v(-76.9, 31.23) * mm, "end": v(-76.9, 29.77) * mm});
            skLineSegment(sketch, "E1801.left", {"start": v(-69.97, 32.1) * mm, "end": v(-76.03, 32.1) * mm});
            skLineSegment(sketch, "E1801.right", {"start": v(-69.97, 28.9) * mm, "end": v(-76.03, 28.9) * mm});
            skArc(sketch, "E1802", {"start": v(-69.1, 29.77) * mm, "mid": v(-69.03, 29.52) * mm, "end": v(-68.85, 29.33) * mm});
            skArc(sketch, "E1803", {"start": v(-69.53, 28.65) * mm, "mid": v(-68.75, 28.55) * mm, "end": v(-68.85, 29.33) * mm});
            skArc(sketch, "E1804", {"start": v(-69.53, 28.65) * mm, "mid": v(-69.72, 28.83) * mm, "end": v(-69.97, 28.9) * mm});
            skArc(sketch, "E1805", {"start": v(-69.97, 32.1) * mm, "mid": v(-69.72, 32.17) * mm, "end": v(-69.53, 32.35) * mm});
            skArc(sketch, "E1806", {"start": v(-68.85, 31.67) * mm, "mid": v(-68.75, 32.45) * mm, "end": v(-69.53, 32.35) * mm});
            skArc(sketch, "E1807", {"start": v(-68.85, 31.67) * mm, "mid": v(-69.03, 31.48) * mm, "end": v(-69.1, 31.23) * mm});
            skArc(sketch, "E1808", {"start": v(-76.03, 28.9) * mm, "mid": v(-76.28, 28.83) * mm, "end": v(-76.47, 28.65) * mm});
            skArc(sketch, "E1809", {"start": v(-77.15, 29.33) * mm, "mid": v(-77.25, 28.55) * mm, "end": v(-76.47, 28.65) * mm});
            skArc(sketch, "E1810", {"start": v(-77.15, 29.33) * mm, "mid": v(-76.97, 29.52) * mm, "end": v(-76.9, 29.77) * mm});
            skArc(sketch, "E1811", {"start": v(-76.9, 31.23) * mm, "mid": v(-76.97, 31.48) * mm, "end": v(-77.15, 31.67) * mm});
            skArc(sketch, "E1812", {"start": v(-76.47, 32.35) * mm, "mid": v(-77.25, 32.45) * mm, "end": v(-77.15, 31.67) * mm});
            skArc(sketch, "E1813", {"start": v(-76.47, 32.35) * mm, "mid": v(-76.28, 32.17) * mm, "end": v(-76.03, 32.1) * mm});
            skLineSegment(sketch, "E1814.bottom", {"start": v(-150.27, 25.2) * mm, "end": v(-151.73, 25.2) * mm});
            skLineSegment(sketch, "E1814.top", {"start": v(-150.27, 45.8) * mm, "end": v(-151.73, 45.8) * mm});
            skArc(sketch, "E1815", {"start": v(-151.73, 25.2) * mm, "mid": v(-151.98, 25.13) * mm, "end": v(-152.17, 24.95) * mm});
            skArc(sketch, "E1816", {"start": v(-152.85, 25.63) * mm, "mid": v(-152.95, 24.85) * mm, "end": v(-152.17, 24.95) * mm});
            skArc(sketch, "E1817", {"start": v(-152.85, 25.63) * mm, "mid": v(-152.67, 25.82) * mm, "end": v(-152.6, 26.07) * mm});
            skArc(sketch, "E1818", {"start": v(-149.4, 26.07) * mm, "mid": v(-149.33, 25.82) * mm, "end": v(-149.15, 25.63) * mm});
            skArc(sketch, "E1819", {"start": v(-149.83, 24.95) * mm, "mid": v(-149.05, 24.85) * mm, "end": v(-149.15, 25.63) * mm});
            skArc(sketch, "E1820", {"start": v(-149.83, 24.95) * mm, "mid": v(-150.02, 25.13) * mm, "end": v(-150.27, 25.2) * mm});
            skArc(sketch, "E1821", {"start": v(-152.6, 44.93) * mm, "mid": v(-152.67, 45.18) * mm, "end": v(-152.85, 45.37) * mm});
            skArc(sketch, "E1822", {"start": v(-152.17, 46.05) * mm, "mid": v(-152.95, 46.15) * mm, "end": v(-152.85, 45.37) * mm});
            skArc(sketch, "E1823", {"start": v(-152.17, 46.05) * mm, "mid": v(-151.98, 45.87) * mm, "end": v(-151.73, 45.8) * mm});
            skArc(sketch, "E1824", {"start": v(-150.27, 45.8) * mm, "mid": v(-150.02, 45.87) * mm, "end": v(-149.83, 46.05) * mm});
            skArc(sketch, "E1825", {"start": v(-149.15, 45.37) * mm, "mid": v(-149.05, 46.15) * mm, "end": v(-149.83, 46.05) * mm});
            skArc(sketch, "E1826", {"start": v(-149.15, 45.37) * mm, "mid": v(-149.33, 45.18) * mm, "end": v(-149.4, 44.93) * mm});
            skLineSegment(sketch, "E1827.bottom", {"start": v(-5.37, -107.2) * mm, "end": v(-6.83, -107.2) * mm});
            skLineSegment(sketch, "E1827.top", {"start": v(-5.37, -99) * mm, "end": v(-6.83, -99) * mm});
            skLineSegment(sketch, "E1827.left", {"start": v(-4.5, -106.33) * mm, "end": v(-4.5, -99.87) * mm});
            skLineSegment(sketch, "E1827.right", {"start": v(-7.7, -106.33) * mm, "end": v(-7.7, -99.87) * mm});
            skArc(sketch, "E1828", {"start": v(-6.83, -107.2) * mm, "mid": v(-7.08, -107.27) * mm, "end": v(-7.27, -107.45) * mm});
            skArc(sketch, "E1829", {"start": v(-7.95, -106.77) * mm, "mid": v(-8.05, -107.55) * mm, "end": v(-7.27, -107.45) * mm});
            skArc(sketch, "E1830", {"start": v(-7.95, -106.77) * mm, "mid": v(-7.77, -106.58) * mm, "end": v(-7.7, -106.33) * mm});
            skArc(sketch, "E1831", {"start": v(-4.5, -106.33) * mm, "mid": v(-4.43, -106.58) * mm, "end": v(-4.25, -106.77) * mm});
            skArc(sketch, "E1832", {"start": v(-4.93, -107.45) * mm, "mid": v(-4.15, -107.55) * mm, "end": v(-4.25, -106.77) * mm});
            skArc(sketch, "E1833", {"start": v(-4.93, -107.45) * mm, "mid": v(-5.12, -107.27) * mm, "end": v(-5.37, -107.2) * mm});
            skArc(sketch, "E1834", {"start": v(-7.7, -99.87) * mm, "mid": v(-7.77, -99.62) * mm, "end": v(-7.95, -99.43) * mm});
            skArc(sketch, "E1835", {"start": v(-7.27, -98.75) * mm, "mid": v(-8.05, -98.65) * mm, "end": v(-7.95, -99.43) * mm});
            skArc(sketch, "E1836", {"start": v(-7.27, -98.75) * mm, "mid": v(-7.08, -98.93) * mm, "end": v(-6.83, -99) * mm});
            skArc(sketch, "E1837", {"start": v(-5.37, -99) * mm, "mid": v(-5.12, -98.93) * mm, "end": v(-4.93, -98.75) * mm});
            skArc(sketch, "E1838", {"start": v(-4.25, -99.43) * mm, "mid": v(-4.15, -98.65) * mm, "end": v(-4.93, -98.75) * mm});
            skArc(sketch, "E1839", {"start": v(-4.25, -99.43) * mm, "mid": v(-4.43, -99.62) * mm, "end": v(-4.5, -99.87) * mm});
            skLineSegment(sketch, "E1840.bottom", {"start": v(-5.37, -124.9) * mm, "end": v(-6.83, -124.9) * mm});
            skLineSegment(sketch, "E1840.top", {"start": v(-5.37, -116.7) * mm, "end": v(-6.83, -116.7) * mm});
            skLineSegment(sketch, "E1840.left", {"start": v(-4.5, -124.03) * mm, "end": v(-4.5, -117.57) * mm});
            skLineSegment(sketch, "E1840.right", {"start": v(-7.7, -124.03) * mm, "end": v(-7.7, -117.57) * mm});
            skArc(sketch, "E1841", {"start": v(-6.83, -124.9) * mm, "mid": v(-7.08, -124.97) * mm, "end": v(-7.27, -125.15) * mm});
            skArc(sketch, "E1842", {"start": v(-7.95, -124.47) * mm, "mid": v(-8.05, -125.25) * mm, "end": v(-7.27, -125.15) * mm});
            skArc(sketch, "E1843", {"start": v(-7.95, -124.47) * mm, "mid": v(-7.77, -124.28) * mm, "end": v(-7.7, -124.03) * mm});
            skArc(sketch, "E1844", {"start": v(-4.5, -124.03) * mm, "mid": v(-4.43, -124.28) * mm, "end": v(-4.25, -124.47) * mm});
            skArc(sketch, "E1845", {"start": v(-4.93, -125.15) * mm, "mid": v(-4.15, -125.25) * mm, "end": v(-4.25, -124.47) * mm});
            skArc(sketch, "E1846", {"start": v(-4.93, -125.15) * mm, "mid": v(-5.12, -124.97) * mm, "end": v(-5.37, -124.9) * mm});
            skArc(sketch, "E1847", {"start": v(-7.7, -117.57) * mm, "mid": v(-7.77, -117.32) * mm, "end": v(-7.95, -117.13) * mm});
            skArc(sketch, "E1848", {"start": v(-7.27, -116.45) * mm, "mid": v(-8.05, -116.35) * mm, "end": v(-7.95, -117.13) * mm});
            skArc(sketch, "E1849", {"start": v(-7.27, -116.45) * mm, "mid": v(-7.08, -116.63) * mm, "end": v(-6.83, -116.7) * mm});
            skArc(sketch, "E1850", {"start": v(-5.37, -116.7) * mm, "mid": v(-5.12, -116.63) * mm, "end": v(-4.93, -116.45) * mm});
            skArc(sketch, "E1851", {"start": v(-4.25, -117.13) * mm, "mid": v(-4.15, -116.35) * mm, "end": v(-4.93, -116.45) * mm});
            skArc(sketch, "E1852", {"start": v(-4.25, -117.13) * mm, "mid": v(-4.43, -117.32) * mm, "end": v(-4.5, -117.57) * mm});
            skLineSegment(sketch, "E1853.bottom", {"start": v(6.83, -107.2) * mm, "end": v(5.37, -107.2) * mm});
            skLineSegment(sketch, "E1853.top", {"start": v(6.83, -99) * mm, "end": v(5.37, -99) * mm});
            skLineSegment(sketch, "E1853.left", {"start": v(7.7, -106.33) * mm, "end": v(7.7, -99.87) * mm});
            skLineSegment(sketch, "E1853.right", {"start": v(4.5, -106.33) * mm, "end": v(4.5, -99.87) * mm});
            skArc(sketch, "E1854", {"start": v(5.37, -107.2) * mm, "mid": v(5.12, -107.27) * mm, "end": v(4.93, -107.45) * mm});
            skArc(sketch, "E1855", {"start": v(4.25, -106.77) * mm, "mid": v(4.15, -107.55) * mm, "end": v(4.93, -107.45) * mm});
            skArc(sketch, "E1856", {"start": v(4.25, -106.77) * mm, "mid": v(4.43, -106.58) * mm, "end": v(4.5, -106.33) * mm});
            skArc(sketch, "E1857", {"start": v(7.7, -106.33) * mm, "mid": v(7.77, -106.58) * mm, "end": v(7.95, -106.77) * mm});
            skArc(sketch, "E1858", {"start": v(7.27, -107.45) * mm, "mid": v(8.05, -107.55) * mm, "end": v(7.95, -106.77) * mm});
            skArc(sketch, "E1859", {"start": v(7.27, -107.45) * mm, "mid": v(7.08, -107.27) * mm, "end": v(6.83, -107.2) * mm});
            skArc(sketch, "E1860", {"start": v(4.5, -99.87) * mm, "mid": v(4.43, -99.62) * mm, "end": v(4.25, -99.43) * mm});
            skArc(sketch, "E1861", {"start": v(4.93, -98.75) * mm, "mid": v(4.15, -98.65) * mm, "end": v(4.25, -99.43) * mm});
            skArc(sketch, "E1862", {"start": v(4.93, -98.75) * mm, "mid": v(5.12, -98.93) * mm, "end": v(5.37, -99) * mm});
            skArc(sketch, "E1863", {"start": v(6.83, -99) * mm, "mid": v(7.08, -98.93) * mm, "end": v(7.27, -98.75) * mm});
            skArc(sketch, "E1864", {"start": v(7.95, -99.43) * mm, "mid": v(8.05, -98.65) * mm, "end": v(7.27, -98.75) * mm});
            skArc(sketch, "E1865", {"start": v(7.95, -99.43) * mm, "mid": v(7.77, -99.62) * mm, "end": v(7.7, -99.87) * mm});
            skLineSegment(sketch, "E1866.bottom", {"start": v(6.83, -124.9) * mm, "end": v(5.37, -124.9) * mm});
            skLineSegment(sketch, "E1866.top", {"start": v(6.83, -116.7) * mm, "end": v(5.37, -116.7) * mm});
            skLineSegment(sketch, "E1866.left", {"start": v(7.7, -124.03) * mm, "end": v(7.7, -117.57) * mm});
            skLineSegment(sketch, "E1866.right", {"start": v(4.5, -124.03) * mm, "end": v(4.5, -117.57) * mm});
            skArc(sketch, "E1867", {"start": v(5.37, -124.9) * mm, "mid": v(5.12, -124.97) * mm, "end": v(4.93, -125.15) * mm});
            skArc(sketch, "E1868", {"start": v(4.25, -124.47) * mm, "mid": v(4.15, -125.25) * mm, "end": v(4.93, -125.15) * mm});
            skArc(sketch, "E1869", {"start": v(4.25, -124.47) * mm, "mid": v(4.43, -124.28) * mm, "end": v(4.5, -124.03) * mm});
            skArc(sketch, "E1870", {"start": v(7.7, -124.03) * mm, "mid": v(7.77, -124.28) * mm, "end": v(7.95, -124.47) * mm});
            skArc(sketch, "E1871", {"start": v(7.27, -125.15) * mm, "mid": v(8.05, -125.25) * mm, "end": v(7.95, -124.47) * mm});
            skArc(sketch, "E1872", {"start": v(7.27, -125.15) * mm, "mid": v(7.08, -124.97) * mm, "end": v(6.83, -124.9) * mm});
            skArc(sketch, "E1873", {"start": v(4.5, -117.57) * mm, "mid": v(4.43, -117.32) * mm, "end": v(4.25, -117.13) * mm});
            skArc(sketch, "E1874", {"start": v(4.93, -116.45) * mm, "mid": v(4.15, -116.35) * mm, "end": v(4.25, -117.13) * mm});
            skArc(sketch, "E1875", {"start": v(4.93, -116.45) * mm, "mid": v(5.12, -116.63) * mm, "end": v(5.37, -116.7) * mm});
            skArc(sketch, "E1876", {"start": v(6.83, -116.7) * mm, "mid": v(7.08, -116.63) * mm, "end": v(7.27, -116.45) * mm});
            skArc(sketch, "E1877", {"start": v(7.95, -117.13) * mm, "mid": v(8.05, -116.35) * mm, "end": v(7.27, -116.45) * mm});
            skArc(sketch, "E1878", {"start": v(7.95, -117.13) * mm, "mid": v(7.77, -117.32) * mm, "end": v(7.7, -117.57) * mm});
            skCircle(sketch, "E1879", {"center": v(-83.75, 8.5) * mm, "radius": 1.6 * mm});
            skLineSegment(sketch, "E1880.bottom", {"start": v(-88.5, 9.23) * mm, "end": v(-88.5, 7.77) * mm});
            skLineSegment(sketch, "E1880.top", {"start": v(-96.9, 9.23) * mm, "end": v(-96.9, 7.77) * mm});
            skLineSegment(sketch, "E1880.left", {"start": v(-89.37, 10.1) * mm, "end": v(-96.03, 10.1) * mm});
            skLineSegment(sketch, "E1880.right", {"start": v(-89.37, 6.9) * mm, "end": v(-96.03, 6.9) * mm});
            skArc(sketch, "E1881", {"start": v(-88.5, 7.77) * mm, "mid": v(-88.43, 7.52) * mm, "end": v(-88.25, 7.33) * mm});
            skArc(sketch, "E1882", {"start": v(-88.93, 6.65) * mm, "mid": v(-88.15, 6.55) * mm, "end": v(-88.25, 7.33) * mm});
            skArc(sketch, "E1883", {"start": v(-88.93, 6.65) * mm, "mid": v(-89.12, 6.83) * mm, "end": v(-89.37, 6.9) * mm});
            skArc(sketch, "E1884", {"start": v(-89.37, 10.1) * mm, "mid": v(-89.12, 10.17) * mm, "end": v(-88.93, 10.35) * mm});
            skArc(sketch, "E1885", {"start": v(-88.25, 9.67) * mm, "mid": v(-88.15, 10.45) * mm, "end": v(-88.93, 10.35) * mm});
            skArc(sketch, "E1886", {"start": v(-88.25, 9.67) * mm, "mid": v(-88.43, 9.48) * mm, "end": v(-88.5, 9.23) * mm});
            skArc(sketch, "E1887", {"start": v(-96.03, 6.9) * mm, "mid": v(-96.28, 6.83) * mm, "end": v(-96.47, 6.65) * mm});
            skArc(sketch, "E1888", {"start": v(-97.15, 7.33) * mm, "mid": v(-97.25, 6.55) * mm, "end": v(-96.47, 6.65) * mm});
            skArc(sketch, "E1889", {"start": v(-97.15, 7.33) * mm, "mid": v(-96.97, 7.52) * mm, "end": v(-96.9, 7.77) * mm});
            skArc(sketch, "E1890", {"start": v(-96.9, 9.23) * mm, "mid": v(-96.97, 9.48) * mm, "end": v(-97.15, 9.67) * mm});
            skArc(sketch, "E1891", {"start": v(-96.47, 10.35) * mm, "mid": v(-97.25, 10.45) * mm, "end": v(-97.15, 9.67) * mm});
            skArc(sketch, "E1892", {"start": v(-96.47, 10.35) * mm, "mid": v(-96.28, 10.17) * mm, "end": v(-96.03, 10.1) * mm});
            skLineSegment(sketch, "E1893.bottom", {"start": v(-70.6, 9.23) * mm, "end": v(-70.6, 7.77) * mm});
            skLineSegment(sketch, "E1893.top", {"start": v(-79, 9.23) * mm, "end": v(-79, 7.77) * mm});
            skLineSegment(sketch, "E1893.left", {"start": v(-71.47, 10.1) * mm, "end": v(-78.13, 10.1) * mm});
            skLineSegment(sketch, "E1893.right", {"start": v(-71.47, 6.9) * mm, "end": v(-78.13, 6.9) * mm});
            skArc(sketch, "E1894", {"start": v(-70.6, 7.77) * mm, "mid": v(-70.53, 7.52) * mm, "end": v(-70.35, 7.33) * mm});
            skArc(sketch, "E1895", {"start": v(-71.03, 6.65) * mm, "mid": v(-70.25, 6.55) * mm, "end": v(-70.35, 7.33) * mm});
            skArc(sketch, "E1896", {"start": v(-71.03, 6.65) * mm, "mid": v(-71.22, 6.83) * mm, "end": v(-71.47, 6.9) * mm});
            skArc(sketch, "E1897", {"start": v(-71.47, 10.1) * mm, "mid": v(-71.22, 10.17) * mm, "end": v(-71.03, 10.35) * mm});
            skArc(sketch, "E1898", {"start": v(-70.35, 9.67) * mm, "mid": v(-70.25, 10.45) * mm, "end": v(-71.03, 10.35) * mm});
            skArc(sketch, "E1899", {"start": v(-70.35, 9.67) * mm, "mid": v(-70.53, 9.48) * mm, "end": v(-70.6, 9.23) * mm});
            skArc(sketch, "E1900", {"start": v(-78.13, 6.9) * mm, "mid": v(-78.38, 6.83) * mm, "end": v(-78.57, 6.65) * mm});
            skArc(sketch, "E1901", {"start": v(-79.25, 7.33) * mm, "mid": v(-79.35, 6.55) * mm, "end": v(-78.57, 6.65) * mm});
            skArc(sketch, "E1902", {"start": v(-79.25, 7.33) * mm, "mid": v(-79.07, 7.52) * mm, "end": v(-79, 7.77) * mm});
            skArc(sketch, "E1903", {"start": v(-79, 9.23) * mm, "mid": v(-79.07, 9.48) * mm, "end": v(-79.25, 9.67) * mm});
            skArc(sketch, "E1904", {"start": v(-78.57, 10.35) * mm, "mid": v(-79.35, 10.45) * mm, "end": v(-79.25, 9.67) * mm});
            skArc(sketch, "E1905", {"start": v(-78.57, 10.35) * mm, "mid": v(-78.38, 10.17) * mm, "end": v(-78.13, 10.1) * mm});
            skCircle(sketch, "E1906", {"center": v(83.75, 8.5) * mm, "radius": 1.6 * mm});
            skLineSegment(sketch, "E1907.bottom", {"start": v(79, 9.23) * mm, "end": v(79, 7.77) * mm});
            skLineSegment(sketch, "E1907.top", {"start": v(70.6, 9.23) * mm, "end": v(70.6, 7.77) * mm});
            skLineSegment(sketch, "E1907.left", {"start": v(78.13, 10.1) * mm, "end": v(71.47, 10.1) * mm});
            skLineSegment(sketch, "E1907.right", {"start": v(78.13, 6.9) * mm, "end": v(71.47, 6.9) * mm});
            skArc(sketch, "E1908", {"start": v(79, 7.77) * mm, "mid": v(79.07, 7.52) * mm, "end": v(79.25, 7.33) * mm});
            skArc(sketch, "E1909", {"start": v(78.57, 6.65) * mm, "mid": v(79.35, 6.55) * mm, "end": v(79.25, 7.33) * mm});
            skArc(sketch, "E1910", {"start": v(78.57, 6.65) * mm, "mid": v(78.38, 6.83) * mm, "end": v(78.13, 6.9) * mm});
            skArc(sketch, "E1911", {"start": v(78.13, 10.1) * mm, "mid": v(78.38, 10.17) * mm, "end": v(78.57, 10.35) * mm});
            skArc(sketch, "E1912", {"start": v(79.25, 9.67) * mm, "mid": v(79.35, 10.45) * mm, "end": v(78.57, 10.35) * mm});
            skArc(sketch, "E1913", {"start": v(79.25, 9.67) * mm, "mid": v(79.07, 9.48) * mm, "end": v(79, 9.23) * mm});
            skArc(sketch, "E1914", {"start": v(71.47, 6.9) * mm, "mid": v(71.22, 6.83) * mm, "end": v(71.03, 6.65) * mm});
            skArc(sketch, "E1915", {"start": v(70.35, 7.33) * mm, "mid": v(70.25, 6.55) * mm, "end": v(71.03, 6.65) * mm});
            skArc(sketch, "E1916", {"start": v(70.35, 7.33) * mm, "mid": v(70.53, 7.52) * mm, "end": v(70.6, 7.77) * mm});
            skArc(sketch, "E1917", {"start": v(70.6, 9.23) * mm, "mid": v(70.53, 9.48) * mm, "end": v(70.35, 9.67) * mm});
            skArc(sketch, "E1918", {"start": v(71.03, 10.35) * mm, "mid": v(70.25, 10.45) * mm, "end": v(70.35, 9.67) * mm});
            skArc(sketch, "E1919", {"start": v(71.03, 10.35) * mm, "mid": v(71.22, 10.17) * mm, "end": v(71.47, 10.1) * mm});
            skLineSegment(sketch, "E1920.bottom", {"start": v(96.9, 9.23) * mm, "end": v(96.9, 7.77) * mm});
            skLineSegment(sketch, "E1920.top", {"start": v(88.5, 9.23) * mm, "end": v(88.5, 7.77) * mm});
            skLineSegment(sketch, "E1920.left", {"start": v(96.03, 10.1) * mm, "end": v(89.37, 10.1) * mm});
            skLineSegment(sketch, "E1920.right", {"start": v(96.03, 6.9) * mm, "end": v(89.37, 6.9) * mm});
            skArc(sketch, "E1921", {"start": v(96.9, 7.77) * mm, "mid": v(96.97, 7.52) * mm, "end": v(97.15, 7.33) * mm});
            skArc(sketch, "E1922", {"start": v(96.47, 6.65) * mm, "mid": v(97.25, 6.55) * mm, "end": v(97.15, 7.33) * mm});
            skArc(sketch, "E1923", {"start": v(96.47, 6.65) * mm, "mid": v(96.28, 6.83) * mm, "end": v(96.03, 6.9) * mm});
            skArc(sketch, "E1924", {"start": v(96.03, 10.1) * mm, "mid": v(96.28, 10.17) * mm, "end": v(96.47, 10.35) * mm});
            skArc(sketch, "E1925", {"start": v(97.15, 9.67) * mm, "mid": v(97.25, 10.45) * mm, "end": v(96.47, 10.35) * mm});
            skArc(sketch, "E1926", {"start": v(97.15, 9.67) * mm, "mid": v(96.97, 9.48) * mm, "end": v(96.9, 9.23) * mm});
            skArc(sketch, "E1927", {"start": v(89.37, 6.9) * mm, "mid": v(89.12, 6.83) * mm, "end": v(88.93, 6.65) * mm});
            skArc(sketch, "E1928", {"start": v(88.25, 7.33) * mm, "mid": v(88.15, 6.55) * mm, "end": v(88.93, 6.65) * mm});
            skArc(sketch, "E1929", {"start": v(88.25, 7.33) * mm, "mid": v(88.43, 7.52) * mm, "end": v(88.5, 7.77) * mm});
            skArc(sketch, "E1930", {"start": v(88.5, 9.23) * mm, "mid": v(88.43, 9.48) * mm, "end": v(88.25, 9.67) * mm});
            skArc(sketch, "E1931", {"start": v(88.93, 10.35) * mm, "mid": v(88.15, 10.45) * mm, "end": v(88.25, 9.67) * mm});
            skArc(sketch, "E1932", {"start": v(88.93, 10.35) * mm, "mid": v(89.12, 10.17) * mm, "end": v(89.37, 10.1) * mm});
            skLineSegment(sketch, "E1933", {"start": v(-157.6, 6.9) * mm, "end": v(-157.6, -3) * mm});
            skLineSegment(sketch, "E1934", {"start": v(-162.4, 9.23) * mm, "end": v(-162.4, 6.9) * mm});
            skLineSegment(sketch, "E1935", {"start": v(-163.27, 10.1) * mm, "end": v(-167.5, 10.1) * mm});
            skLineSegment(sketch, "E1936", {"start": v(-162.4, 6.9) * mm, "end": v(-157.6, 6.9) * mm});
            skLineSegment(sketch, "E1937", {"start": v(-157.6, -133.1) * mm, "end": v(-157.6, -143) * mm});
            skLineSegment(sketch, "E1938", {"start": v(-162.4, -130.77) * mm, "end": v(-162.4, -133.1) * mm});
            skLineSegment(sketch, "E1939", {"start": v(-163.27, -129.9) * mm, "end": v(-167.5, -129.9) * mm});
            skLineSegment(sketch, "E1940", {"start": v(-162.4, -133.1) * mm, "end": v(-157.6, -133.1) * mm});
            skLineSegment(sketch, "E1941.MirrorCS", {"start": v(162.4, 9.23) * mm, "end": v(162.4, 6.9) * mm});
            skLineSegment(sketch, "E1942.MirrorCS", {"start": v(162.4, 6.9) * mm, "end": v(157.6, 6.9) * mm});
            skLineSegment(sketch, "E1943.MirrorCS", {"start": v(163.27, 10.1) * mm, "end": v(167.5, 10.1) * mm});
            skLineSegment(sketch, "E1944.MirrorCS", {"start": v(157.6, 6.9) * mm, "end": v(157.6, -3) * mm});
            skLineSegment(sketch, "E1945.MirrorCS", {"start": v(162.4, -130.77) * mm, "end": v(162.4, -133.1) * mm});
            skLineSegment(sketch, "E1946.MirrorCS", {"start": v(162.4, -133.1) * mm, "end": v(157.6, -133.1) * mm});
            skLineSegment(sketch, "E1947.MirrorCS", {"start": v(163.27, -129.9) * mm, "end": v(167.5, -129.9) * mm});
            skLineSegment(sketch, "E1948.MirrorCS", {"start": v(157.6, -133.1) * mm, "end": v(157.6, -143) * mm});
            skArc(sketch, "E1949", {"start": v(162.4, 9.23) * mm, "mid": v(162.33, 9.48) * mm, "end": v(162.15, 9.67) * mm});
            skArc(sketch, "E1950", {"start": v(162.83, 10.35) * mm, "mid": v(162.05, 10.45) * mm, "end": v(162.15, 9.67) * mm});
            skArc(sketch, "E1951", {"start": v(162.83, 10.35) * mm, "mid": v(163.02, 10.17) * mm, "end": v(163.27, 10.1) * mm});
            skArc(sketch, "E1952", {"start": v(162.4, -130.77) * mm, "mid": v(162.33, -130.52) * mm, "end": v(162.15, -130.33) * mm});
            skArc(sketch, "E1953", {"start": v(162.83, -129.65) * mm, "mid": v(162.05, -129.55) * mm, "end": v(162.15, -130.33) * mm});
            skArc(sketch, "E1954", {"start": v(162.83, -129.65) * mm, "mid": v(163.02, -129.83) * mm, "end": v(163.27, -129.9) * mm});
            skArc(sketch, "E1955", {"start": v(-163.27, -129.9) * mm, "mid": v(-163.02, -129.83) * mm, "end": v(-162.83, -129.65) * mm});
            skArc(sketch, "E1956", {"start": v(-162.15, -130.33) * mm, "mid": v(-162.05, -129.55) * mm, "end": v(-162.83, -129.65) * mm});
            skArc(sketch, "E1957", {"start": v(-162.15, -130.33) * mm, "mid": v(-162.33, -130.52) * mm, "end": v(-162.4, -130.77) * mm});
            skArc(sketch, "E1958", {"start": v(-163.27, 10.1) * mm, "mid": v(-163.02, 10.17) * mm, "end": v(-162.83, 10.35) * mm});
            skArc(sketch, "E1959", {"start": v(-162.15, 9.67) * mm, "mid": v(-162.05, 10.45) * mm, "end": v(-162.83, 10.35) * mm});
            skArc(sketch, "E1960", {"start": v(-162.15, 9.67) * mm, "mid": v(-162.33, 9.48) * mm, "end": v(-162.4, 9.23) * mm});
            skLineSegment(sketch, "E1961", {"start": v(-90, -3) * mm, "end": v(-90, -2) * mm});
            skLineSegment(sketch, "E1962", {"start": v(-90, -143) * mm, "end": v(-90, -142) * mm});
            skLineSegment(sketch, "E1963", {"start": v(90, -143) * mm, "end": v(90, -142) * mm});
            skLineSegment(sketch, "E1964", {"start": v(90, -3) * mm, "end": v(90, -2) * mm});
            skPoint(sketch, "E1965.visualSharp", {"position": v(157.6, -5) * mm});
            skArc(sketch, "E1965.filletArc", {"start": v(155.6, -5) * mm, "mid": v(157.01, -4.41) * mm, "end": v(157.6, -3) * mm});
            skPoint(sketch, "E1966.visualSharp", {"position": v(90, -5) * mm});
            skArc(sketch, "E1966.filletArc", {"start": v(90, -3) * mm, "mid": v(90.59, -4.41) * mm, "end": v(92, -5) * mm});
            skPoint(sketch, "E1967.visualSharp", {"position": v(157.6, -145) * mm});
            skArc(sketch, "E1967.filletArc", {"start": v(155.6, -145) * mm, "mid": v(157.01, -144.41) * mm, "end": v(157.6, -143) * mm});
            skPoint(sketch, "E1968.visualSharp", {"position": v(90, -145) * mm});
            skArc(sketch, "E1968.filletArc", {"start": v(90, -143) * mm, "mid": v(90.59, -144.41) * mm, "end": v(92, -145) * mm});
            skPoint(sketch, "E1969.visualSharp", {"position": v(-90, -145) * mm});
            skArc(sketch, "E1969.filletArc", {"start": v(-92, -145) * mm, "mid": v(-90.59, -144.41) * mm, "end": v(-90, -143) * mm});
            skPoint(sketch, "E1970.visualSharp", {"position": v(-157.6, -145) * mm});
            skArc(sketch, "E1970.filletArc", {"start": v(-157.6, -143) * mm, "mid": v(-157.01, -144.41) * mm, "end": v(-155.6, -145) * mm});
            skPoint(sketch, "E1971.visualSharp", {"position": v(-157.6, -5) * mm});
            skArc(sketch, "E1971.filletArc", {"start": v(-157.6, -3) * mm, "mid": v(-157.01, -4.41) * mm, "end": v(-155.6, -5) * mm});
            skPoint(sketch, "E1972.visualSharp", {"position": v(-90, -5) * mm});
            skArc(sketch, "E1972.filletArc", {"start": v(-92, -5) * mm, "mid": v(-90.59, -4.41) * mm, "end": v(-90, -3) * mm});
            skLineSegment(sketch, "E1973.top", {"start": v(94.5, -108) * mm, "end": v(118.9, -108) * mm});
            skLineSegment(sketch, "E1973.left", {"start": v(94.5, -100) * mm, "end": v(94.5, -108) * mm});
            skLineSegment(sketch, "E1973.right", {"start": v(118.9, -100) * mm, "end": v(118.9, -108) * mm});
            skArc(sketch, "E1974", {"start": v(94.5, -100) * mm, "mid": v(92.45, -95.05) * mm, "end": v(87.5, -93) * mm});
            skLineSegment(sketch, "E1975.trimOffspring", {"start": v(87.5, -93) * mm, "end": v(-87.5, -93) * mm});
            skArc(sketch, "E1976", {"start": v(125.9, -93) * mm, "mid": v(120.95, -95.05) * mm, "end": v(118.9, -100) * mm});
            skArc(sketch, "E1977", {"start": v(-87.5, -93) * mm, "mid": v(-92.45, -95.05) * mm, "end": v(-94.5, -100) * mm});
            skLineSegment(sketch, "E1978.bottom", {"start": v(-94.5, -108) * mm, "end": v(-118.9, -108) * mm});
            skLineSegment(sketch, "E1978.left", {"start": v(-94.5, -108) * mm, "end": v(-94.5, -100) * mm});
            skLineSegment(sketch, "E1978.right", {"start": v(-118.9, -108) * mm, "end": v(-118.9, -100) * mm});
            skArc(sketch, "E1979", {"start": v(-118.9, -100) * mm, "mid": v(-120.95, -95.05) * mm, "end": v(-125.9, -93) * mm});
            skLineSegment(sketch, "E1980.trimOffspring", {"start": v(-125.9, -93) * mm, "end": v(-160.5, -93) * mm});
            skLineSegment(sketch, "E1981", {"start": v(83.75, 8.5) * mm, "end": v(145.03, 8.5) * mm, "construction": true});
            skSolve(sketch);
        }
        {
            var Q0;
            Q0=makeQuery(id+"F6.imprint","IMPRINT",FACE,{"disambiguationData":[TD([[makeQuery(id+"F6.imprint","IMPRINT",EDGE,{"derivedFrom":sQuery(id+"F6.wireOp",EDGE,"E1595")}),1.0]])]});
            var Q1;
            Q1=makeQuery(id+"F6.imprint","IMPRINT",FACE,{"disambiguationData":[TD([[makeQuery(id+"F6.imprint","IMPRINT",EDGE,{"derivedFrom":sQuery(id+"F6.wireOp",EDGE,"E1601")}),1.0]])]});
            extrude(context, id + "F7", {"entities" : qUnion([Q0, Q1]), "depth" : 3 * mm, "offsetDistance" : 25 * mm});
        }
        {
            var Q0;
            Q0=qCreatedBy(makeId("Front.planeOp"),FACE);
            var sketch = newSketch(context, id + "F8", { "sketchPlane" : qUnion([Q0])});
            skLineSegment(sketch, "E1982", {"start": v(-236.79, 760.4) * mm, "end": v(-83.79, 760.4) * mm});
            skArc(sketch, "E1983", {"start": v(-78.79, 755.4) * mm, "mid": v(-80.25, 758.95) * mm, "end": v(-83.79, 760.4) * mm});
            skLineSegment(sketch, "E1984", {"start": v(-78.79, 755.4) * mm, "end": v(-78.79, 703.9) * mm});
            skArc(sketch, "E1985", {"start": v(-83.79, 698.9) * mm, "mid": v(-80.25, 700.37) * mm, "end": v(-78.79, 703.9) * mm});
            skLineSegment(sketch, "E1986", {"start": v(-83.79, 698.9) * mm, "end": v(-236.79, 698.9) * mm});
            skArc(sketch, "E1987", {"start": v(-241.79, 703.9) * mm, "mid": v(-240.32, 700.37) * mm, "end": v(-236.79, 698.9) * mm});
            skLineSegment(sketch, "E1988", {"start": v(-241.79, 703.9) * mm, "end": v(-241.79, 755.4) * mm});
            skArc(sketch, "E1989", {"start": v(-236.79, 760.4) * mm, "mid": v(-240.32, 758.95) * mm, "end": v(-241.79, 755.4) * mm});
            skLineSegment(sketch, "E1990", {"start": v(-224.79, 756.5) * mm, "end": v(-179.29, 756.5) * mm});
            skLineSegment(sketch, "E1991", {"start": v(-179.29, 756.5) * mm, "end": v(-179.29, 750) * mm});
            skLineSegment(sketch, "E1992", {"start": v(-179.29, 750) * mm, "end": v(-224.79, 750) * mm});
            skLineSegment(sketch, "E1993", {"start": v(-224.79, 750) * mm, "end": v(-224.79, 756.5) * mm});
            skLineSegment(sketch, "E1994", {"start": v(-203.29, 744.9) * mm, "end": v(-177.29, 744.9) * mm});
            skLineSegment(sketch, "E1995", {"start": v(-177.29, 744.9) * mm, "end": v(-177.29, 729.4) * mm});
            skLineSegment(sketch, "E1996", {"start": v(-177.29, 729.4) * mm, "end": v(-203.29, 729.4) * mm});
            skLineSegment(sketch, "E1997", {"start": v(-203.29, 729.4) * mm, "end": v(-203.29, 744.9) * mm});
            skCircle(sketch, "E1998", {"center": v(-236.79, 703.9) * mm, "radius": 1.6 * mm});
            skCircle(sketch, "E1999", {"center": v(-83.79, 703.9) * mm, "radius": 1.6 * mm});
            skCircle(sketch, "E2000", {"center": v(-236.79, 755.4) * mm, "radius": 1.6 * mm});
            skCircle(sketch, "E2001", {"center": v(-83.79, 755.4) * mm, "radius": 1.6 * mm});
            skArc(sketch, "E2002", {"start": v(-63.79, 760.4) * mm, "mid": v(-69.44, 758.07) * mm, "end": v(-71.79, 752.4) * mm});
            skLineSegment(sketch, "E2003", {"start": v(-71.79, 752.4) * mm, "end": v(-71.79, 696.4) * mm});
            skArc(sketch, "E2004", {"start": v(-71.79, 696.4) * mm, "mid": v(-69.44, 690.75) * mm, "end": v(-63.79, 688.4) * mm});
            skLineSegment(sketch, "E2005", {"start": v(-63.79, 688.4) * mm, "end": v(88.01, 688.4) * mm});
            skArc(sketch, "E2006", {"start": v(88.01, 688.4) * mm, "mid": v(93.67, 690.75) * mm, "end": v(96.01, 696.4) * mm});
            skLineSegment(sketch, "E2007", {"start": v(96.01, 752.4) * mm, "end": v(96.01, 696.4) * mm});
            skArc(sketch, "E2008", {"start": v(96.01, 752.4) * mm, "mid": v(93.67, 758.07) * mm, "end": v(88.01, 760.4) * mm});
            skLineSegment(sketch, "E2009", {"start": v(88.01, 760.4) * mm, "end": v(-63.79, 760.4) * mm});
            skLineSegment(sketch, "E2010", {"start": v(-60.39, 744.9) * mm, "end": v(38.11, 744.9) * mm});
            skLineSegment(sketch, "E2011", {"start": v(38.11, 744.9) * mm, "end": v(38.11, 703.9) * mm});
            skLineSegment(sketch, "E2012", {"start": v(38.11, 703.9) * mm, "end": v(-60.39, 703.9) * mm});
            skLineSegment(sketch, "E2013", {"start": v(-60.39, 703.9) * mm, "end": v(-60.39, 744.9) * mm});
            skCircle(sketch, "E2014", {"center": v(67.61, 724.4) * mm, "radius": 4 * mm});
            skCircle(sketch, "E2015", {"center": v(67.61, 707.4) * mm, "radius": 4 * mm});
            skCircle(sketch, "E2016", {"center": v(50.61, 724.4) * mm, "radius": 4 * mm});
            skCircle(sketch, "E2017", {"center": v(67.61, 741.4) * mm, "radius": 4 * mm});
            skCircle(sketch, "E2018", {"center": v(84.61, 724.4) * mm, "radius": 4 * mm});
            skCircle(sketch, "E2019", {"center": v(88.61, 703.4) * mm, "radius": 1.6 * mm});
            skCircle(sketch, "E2020", {"center": v(88.61, 754.9) * mm, "radius": 1.6 * mm});
            skCircle(sketch, "E2021", {"center": v(-64.39, 754.9) * mm, "radius": 1.6 * mm});
            skCircle(sketch, "E2022", {"center": v(-64.39, 703.4) * mm, "radius": 1.6 * mm});
            skArc(sketch, "E2023", {"start": v(113.01, 760.4) * mm, "mid": v(107.36, 758.07) * mm, "end": v(105.01, 752.4) * mm});
            skLineSegment(sketch, "E2024", {"start": v(105.01, 752.4) * mm, "end": v(105.01, 696.4) * mm});
            skArc(sketch, "E2025", {"start": v(105.01, 696.4) * mm, "mid": v(105.5, 693.65) * mm, "end": v(106.91, 691.23) * mm});
            skLineSegment(sketch, "E2026", {"start": v(106.91, 691.23) * mm, "end": v(106.91, 677.4) * mm});
            skArc(sketch, "E2027", {"start": v(106.91, 677.4) * mm, "mid": v(109.26, 671.75) * mm, "end": v(114.91, 669.4) * mm});
            skLineSegment(sketch, "E2028", {"start": v(114.91, 669.4) * mm, "end": v(262.91, 669.4) * mm});
            skArc(sketch, "E2029", {"start": v(262.91, 669.4) * mm, "mid": v(268.57, 671.75) * mm, "end": v(270.91, 677.4) * mm});
            skLineSegment(sketch, "E2030", {"start": v(270.91, 677.4) * mm, "end": v(270.91, 691.23) * mm});
            skArc(sketch, "E2031", {"start": v(270.91, 691.23) * mm, "mid": v(272.32, 693.65) * mm, "end": v(272.81, 696.4) * mm});
            skLineSegment(sketch, "E2032", {"start": v(272.81, 752.4) * mm, "end": v(272.81, 696.4) * mm});
            skArc(sketch, "E2033", {"start": v(272.81, 752.4) * mm, "mid": v(270.47, 758.07) * mm, "end": v(264.81, 760.4) * mm});
            skLineSegment(sketch, "E2034", {"start": v(264.81, 760.4) * mm, "end": v(113.01, 760.4) * mm});
            skLineSegment(sketch, "E2035", {"start": v(116.91, 755.9) * mm, "end": v(252.41, 755.9) * mm});
            skArc(sketch, "E2036", {"start": v(253.41, 754.9) * mm, "mid": v(253.12, 755.62) * mm, "end": v(252.41, 755.9) * mm});
            skArc(sketch, "E2037", {"start": v(253.41, 754.9) * mm, "mid": v(256.93, 746.42) * mm, "end": v(265.41, 742.9) * mm});
            skLineSegment(sketch, "E2038", {"start": v(265.41, 742.9) * mm, "end": v(266.21, 742.9) * mm});
            skArc(sketch, "E2039", {"start": v(267.71, 741.4) * mm, "mid": v(267.27, 742.47) * mm, "end": v(266.21, 742.9) * mm});
            skLineSegment(sketch, "E2040", {"start": v(267.71, 741.4) * mm, "end": v(267.71, 716.9) * mm});
            skArc(sketch, "E2041", {"start": v(266.21, 715.4) * mm, "mid": v(267.27, 715.85) * mm, "end": v(267.71, 716.9) * mm});
            skLineSegment(sketch, "E2042", {"start": v(265.41, 715.4) * mm, "end": v(266.21, 715.4) * mm});
            skArc(sketch, "E2043", {"start": v(265.41, 715.4) * mm, "mid": v(256.93, 711.9) * mm, "end": v(253.41, 703.4) * mm});
            skLineSegment(sketch, "E2044", {"start": v(253.41, 703.4) * mm, "end": v(253.41, 694.9) * mm});
            skArc(sketch, "E2045", {"start": v(251.91, 693.4) * mm, "mid": v(252.97, 693.85) * mm, "end": v(253.41, 694.9) * mm});
            skLineSegment(sketch, "E2046", {"start": v(115.91, 693.4) * mm, "end": v(251.91, 693.4) * mm});
            skLineSegment(sketch, "E2047", {"start": v(115.91, 693.4) * mm, "end": v(115.91, 754.9) * mm});
            skArc(sketch, "E2048", {"start": v(116.91, 755.9) * mm, "mid": v(116.2, 755.62) * mm, "end": v(115.91, 754.9) * mm});
            skCircle(sketch, "E2049", {"center": v(188.91, 677.4) * mm, "radius": 1.6 * mm});
            skCircle(sketch, "E2050", {"center": v(254.91, 677.4) * mm, "radius": 1.6 * mm});
            skCircle(sketch, "E2051", {"center": v(232.91, 677.4) * mm, "radius": 1.6 * mm});
            skCircle(sketch, "E2052", {"center": v(210.91, 677.4) * mm, "radius": 1.6 * mm});
            skCircle(sketch, "E2053", {"center": v(166.91, 677.4) * mm, "radius": 1.6 * mm});
            skCircle(sketch, "E2054", {"center": v(144.91, 677.4) * mm, "radius": 1.6 * mm});
            skCircle(sketch, "E2055", {"center": v(122.91, 677.4) * mm, "radius": 1.6 * mm});
            skCircle(sketch, "E2056", {"center": v(265.41, 703.4) * mm, "radius": 1.6 * mm});
            skCircle(sketch, "E2057", {"center": v(265.41, 754.9) * mm, "radius": 1.6 * mm});
            skCircle(sketch, "E2058", {"center": v(112.41, 754.9) * mm, "radius": 1.6 * mm});
            skCircle(sketch, "E2059", {"center": v(112.41, 703.4) * mm, "radius": 1.6 * mm});
            skLineSegment(sketch, "E2060", {"start": v(-187, -66) * mm, "end": v(-187, -40.3) * mm});
            skLineSegment(sketch, "E2061", {"start": v(-187, -40.3) * mm, "end": v(-179, -40.3) * mm});
            skLineSegment(sketch, "E2062", {"start": v(-179, -40.3) * mm, "end": v(-179, -66) * mm});
            skLineSegment(sketch, "E2063", {"start": v(-179, -66) * mm, "end": v(-187, -66) * mm});
            skCircle(sketch, "E2064", {"center": v(-183, -44.3) * mm, "radius": 1.6 * mm});
            skCircle(sketch, "E2065", {"center": v(-183, -62) * mm, "radius": 1.6 * mm});
            skArc(sketch, "E2066", {"start": v(-44.95, 732.77) * mm, "mid": v(-50.92, 738.2) * mm, "end": v(-56.9, 732.77) * mm});
            skLineSegment(sketch, "E2067", {"start": v(-56.9, 732.77) * mm, "end": v(-58.39, 716.9) * mm});
            skArc(sketch, "E2068", {"start": v(-58.39, 716.9) * mm, "mid": v(-50.92, 708.7) * mm, "end": v(-43.45, 716.9) * mm});
            skLineSegment(sketch, "E2069", {"start": v(-44.95, 732.77) * mm, "end": v(-43.45, 716.9) * mm});
            skCircle(sketch, "E2070", {"center": v(-50.92, 732.2) * mm, "radius": 1.6 * mm});
            skArc(sketch, "E2071", {"start": v(-40.9, 714.14) * mm, "mid": v(-34.92, 708.7) * mm, "end": v(-28.95, 714.14) * mm});
            skLineSegment(sketch, "E2072", {"start": v(-28.95, 714.14) * mm, "end": v(-27.45, 730) * mm});
            skArc(sketch, "E2073", {"start": v(-27.45, 730) * mm, "mid": v(-34.92, 738.2) * mm, "end": v(-42.39, 730) * mm});
            skLineSegment(sketch, "E2074", {"start": v(-40.9, 714.14) * mm, "end": v(-42.39, 730) * mm});
            skCircle(sketch, "E2075", {"center": v(-34.92, 714.7) * mm, "radius": 1.6 * mm});
            skArc(sketch, "E2076", {"start": v(-12.95, 732.77) * mm, "mid": v(-18.92, 738.2) * mm, "end": v(-24.9, 732.77) * mm});
            skLineSegment(sketch, "E2077", {"start": v(-24.9, 732.77) * mm, "end": v(-26.39, 716.9) * mm});
            skArc(sketch, "E2078", {"start": v(-26.39, 716.9) * mm, "mid": v(-18.92, 708.7) * mm, "end": v(-11.45, 716.9) * mm});
            skLineSegment(sketch, "E2079", {"start": v(-12.95, 732.77) * mm, "end": v(-11.45, 716.9) * mm});
            skCircle(sketch, "E2080", {"center": v(-18.92, 732.2) * mm, "radius": 1.6 * mm});
            skArc(sketch, "E2081", {"start": v(-8.9, 714.14) * mm, "mid": v(-2.92, 708.7) * mm, "end": v(3.05, 714.14) * mm});
            skLineSegment(sketch, "E2082", {"start": v(3.05, 714.14) * mm, "end": v(4.55, 730) * mm});
            skArc(sketch, "E2083", {"start": v(4.55, 730) * mm, "mid": v(-2.92, 738.2) * mm, "end": v(-10.39, 730) * mm});
            skLineSegment(sketch, "E2084", {"start": v(-8.9, 714.14) * mm, "end": v(-10.39, 730) * mm});
            skCircle(sketch, "E2085", {"center": v(-2.92, 714.7) * mm, "radius": 1.6 * mm});
            skLineSegment(sketch, "E2086", {"start": v(103.01, -49.7) * mm, "end": v(103.01, -70.2) * mm});
            skArc(sketch, "E2087", {"start": v(103.01, -70.2) * mm, "mid": v(103.6, -71.62) * mm, "end": v(105.01, -72.2) * mm});
            skLineSegment(sketch, "E2088", {"start": v(105.01, -72.2) * mm, "end": v(124.06, -72.2) * mm});
            skArc(sketch, "E2089", {"start": v(124.06, -72.2) * mm, "mid": v(125.48, -71.62) * mm, "end": v(126.06, -70.2) * mm});
            skLineSegment(sketch, "E2090", {"start": v(126.06, -70.2) * mm, "end": v(126.06, -52.2) * mm});
            skLineSegment(sketch, "E2091", {"start": v(126.06, -52.2) * mm, "end": v(122.06, -52.2) * mm});
            skLineSegment(sketch, "E2092", {"start": v(118.56, -52.2) * mm, "end": v(111.48, -52.2) * mm});
            skLineSegment(sketch, "E2093", {"start": v(110.61, -51.34) * mm, "end": v(110.61, -49.7) * mm});
            skLineSegment(sketch, "E2094", {"start": v(110.11, -49.2) * mm, "end": v(103.51, -49.2) * mm});
            skCircle(sketch, "E2095", {"center": v(115.01, -65) * mm, "radius": 1.1 * mm});
            skCircle(sketch, "E2096", {"center": v(105.51, -65) * mm, "radius": 1.1 * mm});
            skLineSegment(sketch, "E2097", {"start": v(-89.28, -54.9) * mm, "end": v(-84.98, -54.9) * mm});
            skLineSegment(sketch, "E2098", {"start": v(-84.98, -54.9) * mm, "end": v(-84.98, -56.16) * mm});
            skLineSegment(sketch, "E2099", {"start": v(-84.98, -56.16) * mm, "end": v(-79.98, -56.16) * mm});
            skLineSegment(sketch, "E2100", {"start": v(-79.98, -56.16) * mm, "end": v(-79.98, -54.9) * mm});
            skLineSegment(sketch, "E2101", {"start": v(-79.98, -54.9) * mm, "end": v(-77.28, -54.9) * mm});
            skLineSegment(sketch, "E2102", {"start": v(-77.28, -54.9) * mm, "end": v(-77.28, -51.4) * mm});
            skLineSegment(sketch, "E2103", {"start": v(-77.28, -51.4) * mm, "end": v(-79.98, -51.4) * mm});
            skLineSegment(sketch, "E2104", {"start": v(-79.98, -51.4) * mm, "end": v(-79.98, -50.16) * mm});
            skLineSegment(sketch, "E2105", {"start": v(-79.98, -50.16) * mm, "end": v(-84.98, -50.16) * mm});
            skLineSegment(sketch, "E2106", {"start": v(-84.98, -50.16) * mm, "end": v(-84.98, -51.4) * mm});
            skLineSegment(sketch, "E2107", {"start": v(-84.98, -51.4) * mm, "end": v(-89.28, -51.4) * mm});
            skArc(sketch, "E2108", {"start": v(-48.08, -75.56) * mm, "mid": v(-46.43, -79.55) * mm, "end": v(-42.43, -81.2) * mm});
            skLineSegment(sketch, "E2109", {"start": v(-42.43, -81.2) * mm, "end": v(2.86, -81.2) * mm});
            skLineSegment(sketch, "E2110", {"start": v(2.86, -73.96) * mm, "end": v(2.86, -81.2) * mm});
            skLineSegment(sketch, "E2111", {"start": v(2.86, -62.48) * mm, "end": v(2.86, -70.46) * mm});
            skLineSegment(sketch, "E2112", {"start": v(5.36, -61.6) * mm, "end": v(3.73, -61.6) * mm});
            skLineSegment(sketch, "E2113", {"start": v(5.86, -50.3) * mm, "end": v(5.86, -61.1) * mm});
            skLineSegment(sketch, "E2114", {"start": v(3.73, -49.8) * mm, "end": v(5.36, -49.8) * mm});
            skLineSegment(sketch, "E2115", {"start": v(2.86, -44.96) * mm, "end": v(2.86, -48.94) * mm});
            skLineSegment(sketch, "E2116", {"start": v(2.86, -41.46) * mm, "end": v(2.86, -27.7) * mm});
            skLineSegment(sketch, "E2117", {"start": v(-2.14, -22.7) * mm, "end": v(-42.44, -22.7) * mm});
            skArc(sketch, "E2118", {"start": v(-42.44, -22.7) * mm, "mid": v(-46.5, -24.44) * mm, "end": v(-48.08, -28.56) * mm});
            skLineSegment(sketch, "E2119", {"start": v(-48.08, -75.57) * mm, "end": v(-48.08, -28.56) * mm});
            skCircle(sketch, "E2120", {"center": v(-26.94, -43.86) * mm, "radius": 11.5 * mm});
            skCircle(sketch, "E2121", {"center": v(-11.44, -28.36) * mm, "radius": 1.6 * mm});
            skCircle(sketch, "E2122", {"center": v(-42.44, -59.36) * mm, "radius": 1.6 * mm});
            skCircle(sketch, "E2123", {"center": v(-42.44, -28.36) * mm, "radius": 1.6 * mm});
            skLineSegment(sketch, "E2124", {"start": v(53.01, -65) * mm, "end": v(33.36, -65) * mm});
            skArc(sketch, "E2125", {"start": v(33.36, -65) * mm, "mid": v(31.6, -65.74) * mm, "end": v(30.86, -67.5) * mm});
            skLineSegment(sketch, "E2126", {"start": v(30.86, -67.5) * mm, "end": v(30.86, -78.7) * mm});
            skArc(sketch, "E2127", {"start": v(30.86, -78.7) * mm, "mid": v(31.6, -80.48) * mm, "end": v(33.36, -81.2) * mm});
            skLineSegment(sketch, "E2128", {"start": v(33.36, -81.2) * mm, "end": v(60.86, -81.2) * mm});
            skLineSegment(sketch, "E2129", {"start": v(60.86, -81.2) * mm, "end": v(60.86, -73.96) * mm});
            skLineSegment(sketch, "E2130", {"start": v(60.86, -70.46) * mm, "end": v(60.86, -65.68) * mm});
            skLineSegment(sketch, "E2131", {"start": v(61.73, -64.8) * mm, "end": v(63.36, -64.8) * mm});
            skLineSegment(sketch, "E2132", {"start": v(63.86, -64.3) * mm, "end": v(63.86, -50.1) * mm});
            skLineSegment(sketch, "E2133", {"start": v(63.36, -49.6) * mm, "end": v(61.73, -49.6) * mm});
            skLineSegment(sketch, "E2134", {"start": v(60.86, -48.74) * mm, "end": v(60.86, -38.2) * mm});
            skLineSegment(sketch, "E2135", {"start": v(60.86, -38.2) * mm, "end": v(56.01, -38.2) * mm});
            skArc(sketch, "E2136", {"start": v(56.01, -38.2) * mm, "mid": v(54.95, -38.65) * mm, "end": v(54.51, -39.7) * mm});
            skLineSegment(sketch, "E2137", {"start": v(54.51, -39.7) * mm, "end": v(54.51, -63.5) * mm});
            skArc(sketch, "E2138", {"start": v(53.01, -65) * mm, "mid": v(54.07, -64.57) * mm, "end": v(54.51, -63.5) * mm});
            skCircle(sketch, "E2139", {"center": v(-24.64, -70.46) * mm, "radius": 7 * mm});
            skCircle(sketch, "E2140", {"center": v(-11.44, -59.36) * mm, "radius": 1.6 * mm});
            skLineSegment(sketch, "E2141", {"start": v(-135.78, -66) * mm, "end": v(-168.28, -66) * mm});
            skLineSegment(sketch, "E2142", {"start": v(-136.65, -58) * mm, "end": v(-168.28, -58) * mm});
            skLineSegment(sketch, "E2143", {"start": v(-168.28, -48.3) * mm, "end": v(-136.65, -48.3) * mm});
            skLineSegment(sketch, "E2144", {"start": v(-168.28, -40.3) * mm, "end": v(-135.78, -40.3) * mm});
            skCircle(sketch, "E2145", {"center": v(-148.78, -44.3) * mm, "radius": 1.6 * mm});
            skCircle(sketch, "E2146", {"center": v(-156.78, -44.3) * mm, "radius": 1.6 * mm});
            skCircle(sketch, "E2147", {"center": v(-148.78, -62) * mm, "radius": 1.6 * mm});
            skCircle(sketch, "E2148", {"center": v(-156.78, -62) * mm, "radius": 1.6 * mm});
            skCircle(sketch, "E2149", {"center": v(-123.78, -43.86) * mm, "radius": 1.6 * mm});
            skPoint(sketch, "E2150", {"position": v(-9.14, -72.2) * mm});
            skLineSegment(sketch, "E2151", {"start": v(-140.39, -86.2) * mm, "end": v(129.83, -86.2) * mm, "construction": true});
            skLineSegment(sketch, "E2152", {"start": v(-168.78, -40.8) * mm, "end": v(-168.78, -47.8) * mm});
            skLineSegment(sketch, "E2153", {"start": v(-135.78, -49.18) * mm, "end": v(-135.78, -57.14) * mm});
            skPoint(sketch, "E2154", {"position": v(-139.43, -43.86) * mm});
            skArc(sketch, "E2155", {"start": v(-135.78, -40.3) * mm, "mid": v(-132.7, -39.94) * mm, "end": v(-129.78, -38.83) * mm});
            skArc(sketch, "E2156", {"start": v(-129.78, -38.83) * mm, "mid": v(-126.87, -37.73) * mm, "end": v(-123.78, -37.36) * mm});
            skArc(sketch, "E2157", {"start": v(-135.78, -65.7) * mm, "mid": v(-122.53, -58.17) * mm, "end": v(-117.28, -43.86) * mm});
            skArc(sketch, "E2158", {"start": v(-117.28, -43.86) * mm, "mid": v(-119.19, -39.26) * mm, "end": v(-123.78, -37.36) * mm});
            skLineSegment(sketch, "E2159", {"start": v(-168.78, -58.5) * mm, "end": v(-168.78, -65.5) * mm});
            skPoint(sketch, "E2160", {"position": v(-135.78, -53.16) * mm});
            skCircle(sketch, "E2161", {"center": v(-164.78, -44.3) * mm, "radius": 1.6 * mm});
            skCircle(sketch, "E2162", {"center": v(-164.78, -62) * mm, "radius": 1.6 * mm});
            skLineSegment(sketch, "E2163", {"start": v(-90.15, -58) * mm, "end": v(-91.78, -58) * mm});
            skLineSegment(sketch, "E2164", {"start": v(-91.78, -48.3) * mm, "end": v(-90.15, -48.3) * mm});
            skLineSegment(sketch, "E2165", {"start": v(-91.78, -40.3) * mm, "end": v(-89.28, -40.3) * mm});
            skCircle(sketch, "E2166", {"center": v(-77.28, -43.86) * mm, "radius": 1.6 * mm});
            skArc(sketch, "E2167", {"start": v(-89.28, -40.3) * mm, "mid": v(-86.2, -39.94) * mm, "end": v(-83.28, -38.83) * mm});
            skArc(sketch, "E2168", {"start": v(-83.28, -38.83) * mm, "mid": v(-80.37, -37.73) * mm, "end": v(-77.28, -37.36) * mm});
            skArc(sketch, "E2169", {"start": v(-70.78, -43.86) * mm, "mid": v(-72.69, -39.26) * mm, "end": v(-77.28, -37.36) * mm});
            skLineSegment(sketch, "E2170", {"start": v(-92.28, -40.8) * mm, "end": v(-92.28, -47.8) * mm});
            skLineSegment(sketch, "E2171", {"start": v(-92.28, -58.5) * mm, "end": v(-92.28, -65.5) * mm});
            skLineSegment(sketch, "E2172.trimOffspring", {"start": v(-89.28, -54.9) * mm, "end": v(-89.28, -57.14) * mm});
            skLineSegment(sketch, "E2173", {"start": v(-89.28, -49.18) * mm, "end": v(-89.28, -51.4) * mm});
            skLineSegment(sketch, "E2174", {"start": v(152.6, -47.93) * mm, "end": v(187.6, -47.93) * mm});
            skArc(sketch, "E2175", {"start": v(193.6, -53.93) * mm, "mid": v(191.83, -49.68) * mm, "end": v(187.6, -47.93) * mm});
            skLineSegment(sketch, "E2176", {"start": v(193.6, -53.93) * mm, "end": v(193.6, -66.93) * mm});
            skArc(sketch, "E2177", {"start": v(187.6, -72.93) * mm, "mid": v(191.83, -71.17) * mm, "end": v(193.6, -66.93) * mm});
            skLineSegment(sketch, "E2178", {"start": v(187.6, -72.93) * mm, "end": v(152.6, -72.93) * mm});
            skArc(sketch, "E2179", {"start": v(146.6, -66.93) * mm, "mid": v(148.35, -71.17) * mm, "end": v(152.6, -72.93) * mm});
            skLineSegment(sketch, "E2180", {"start": v(146.6, -66.93) * mm, "end": v(146.6, -53.93) * mm});
            skArc(sketch, "E2181", {"start": v(152.6, -47.93) * mm, "mid": v(148.35, -49.68) * mm, "end": v(146.6, -53.93) * mm});
            skCircle(sketch, "E2182", {"center": v(152.6, -53.93) * mm, "radius": 1.6 * mm});
            skCircle(sketch, "E2183", {"center": v(187.6, -66.93) * mm, "radius": 1.6 * mm});
            skCircle(sketch, "E2184", {"center": v(174.84, -65.43) * mm, "radius": 1.1 * mm});
            skCircle(sketch, "E2185", {"center": v(165.34, -65.43) * mm, "radius": 1.1 * mm});
            skArc(sketch, "E2186", {"start": v(19.05, 732.77) * mm, "mid": v(13.08, 738.2) * mm, "end": v(7.1, 732.77) * mm});
            skLineSegment(sketch, "E2187", {"start": v(7.1, 732.77) * mm, "end": v(5.61, 716.9) * mm});
            skArc(sketch, "E2188", {"start": v(5.61, 716.9) * mm, "mid": v(13.08, 708.7) * mm, "end": v(20.55, 716.9) * mm});
            skLineSegment(sketch, "E2189", {"start": v(19.05, 732.77) * mm, "end": v(20.55, 716.9) * mm});
            skCircle(sketch, "E2190", {"center": v(13.08, 732.2) * mm, "radius": 1.6 * mm});
            skArc(sketch, "E2191", {"start": v(23.1, 714.14) * mm, "mid": v(29.08, 708.7) * mm, "end": v(35.05, 714.14) * mm});
            skLineSegment(sketch, "E2192", {"start": v(35.05, 714.14) * mm, "end": v(36.55, 730) * mm});
            skArc(sketch, "E2193", {"start": v(36.55, 730) * mm, "mid": v(29.08, 738.2) * mm, "end": v(21.61, 730) * mm});
            skLineSegment(sketch, "E2194", {"start": v(23.1, 714.14) * mm, "end": v(21.61, 730) * mm});
            skCircle(sketch, "E2195", {"center": v(29.08, 714.7) * mm, "radius": 1.6 * mm});
            skArc(sketch, "E2196", {"start": v(-89.03, -48.74) * mm, "mid": v(-89.22, -48.93) * mm, "end": v(-89.28, -49.18) * mm});
            skArc(sketch, "E2197", {"start": v(-89.03, -48.74) * mm, "mid": v(-88.93, -47.96) * mm, "end": v(-89.72, -48.06) * mm});
            skArc(sketch, "E2198", {"start": v(-90.15, -48.3) * mm, "mid": v(-89.9, -48.24) * mm, "end": v(-89.72, -48.06) * mm});
            skArc(sketch, "E2199", {"start": v(-89.72, -58.26) * mm, "mid": v(-89.9, -58.08) * mm, "end": v(-90.15, -58) * mm});
            skArc(sketch, "E2200", {"start": v(-89.72, -58.26) * mm, "mid": v(-88.93, -58.36) * mm, "end": v(-89.03, -57.58) * mm});
            skArc(sketch, "E2201", {"start": v(-89.28, -57.14) * mm, "mid": v(-89.22, -57.4) * mm, "end": v(-89.03, -57.58) * mm});
            skPoint(sketch, "E2202.visualSharp", {"position": v(-92.28, -48.3) * mm});
            skArc(sketch, "E2202.filletArc", {"start": v(-92.28, -47.8) * mm, "mid": v(-92.14, -48.16) * mm, "end": v(-91.78, -48.3) * mm});
            skPoint(sketch, "E2203.visualSharp", {"position": v(-92.28, -40.3) * mm});
            skArc(sketch, "E2203.filletArc", {"start": v(-91.78, -40.3) * mm, "mid": v(-92.14, -40.46) * mm, "end": v(-92.28, -40.8) * mm});
            skArc(sketch, "E2204.filletArc", {"start": v(-91.78, -58) * mm, "mid": v(-92.14, -58.16) * mm, "end": v(-92.28, -58.5) * mm});
            skLineSegment(sketch, "E2205", {"start": v(-89.28, -66) * mm, "end": v(-91.78, -66) * mm});
            skLineSegment(sketch, "E2206", {"start": v(-89.28, -66) * mm, "end": v(-89.28, -65.7) * mm});
            skArc(sketch, "E2207", {"start": v(-89.28, -65.7) * mm, "mid": v(-76.03, -58.17) * mm, "end": v(-70.78, -43.86) * mm});
            skPoint(sketch, "E2208.visualSharp", {"position": v(-92.28, -66) * mm});
            skArc(sketch, "E2208.filletArc", {"start": v(-92.28, -65.5) * mm, "mid": v(-92.14, -65.85) * mm, "end": v(-91.78, -66) * mm});
            skArc(sketch, "E2209", {"start": v(-135.53, -48.74) * mm, "mid": v(-135.72, -48.93) * mm, "end": v(-135.78, -49.18) * mm});
            skArc(sketch, "E2210", {"start": v(-135.53, -48.74) * mm, "mid": v(-135.43, -47.96) * mm, "end": v(-136.22, -48.06) * mm});
            skArc(sketch, "E2211", {"start": v(-136.65, -48.3) * mm, "mid": v(-136.4, -48.24) * mm, "end": v(-136.22, -48.06) * mm});
            skArc(sketch, "E2212", {"start": v(-136.22, -58.26) * mm, "mid": v(-136.4, -58.08) * mm, "end": v(-136.65, -58) * mm});
            skArc(sketch, "E2213", {"start": v(-136.22, -58.26) * mm, "mid": v(-135.43, -58.36) * mm, "end": v(-135.53, -57.58) * mm});
            skArc(sketch, "E2214", {"start": v(-135.78, -57.14) * mm, "mid": v(-135.72, -57.4) * mm, "end": v(-135.53, -57.58) * mm});
            skArc(sketch, "E2215", {"start": v(60.61, -49.18) * mm, "mid": v(60.8, -49) * mm, "end": v(60.86, -48.74) * mm});
            skArc(sketch, "E2216", {"start": v(60.61, -49.18) * mm, "mid": v(60.5, -49.96) * mm, "end": v(61.3, -49.86) * mm});
            skArc(sketch, "E2217", {"start": v(61.73, -49.6) * mm, "mid": v(61.48, -49.68) * mm, "end": v(61.3, -49.86) * mm});
            skPoint(sketch, "E2218.visualSharp", {"position": v(-168.78, -40.3) * mm});
            skArc(sketch, "E2218.filletArc", {"start": v(-168.28, -40.3) * mm, "mid": v(-168.64, -40.46) * mm, "end": v(-168.78, -40.8) * mm});
            skPoint(sketch, "E2219.visualSharp", {"position": v(-168.78, -48.3) * mm});
            skArc(sketch, "E2219.filletArc", {"start": v(-168.78, -47.8) * mm, "mid": v(-168.64, -48.16) * mm, "end": v(-168.28, -48.3) * mm});
            skPoint(sketch, "E2220.visualSharp", {"position": v(-168.78, -66) * mm});
            skArc(sketch, "E2220.filletArc", {"start": v(-168.78, -65.5) * mm, "mid": v(-168.64, -65.86) * mm, "end": v(-168.28, -66) * mm});
            skPoint(sketch, "E2221.visualSharp", {"position": v(-168.78, -58) * mm});
            skArc(sketch, "E2221.filletArc", {"start": v(-168.28, -58) * mm, "mid": v(-168.64, -58.16) * mm, "end": v(-168.78, -58.5) * mm});
            skPoint(sketch, "E2222.visualSharp", {"position": v(5.86, -49.8) * mm});
            skArc(sketch, "E2222.filletArc", {"start": v(5.86, -50.3) * mm, "mid": v(5.72, -49.96) * mm, "end": v(5.36, -49.8) * mm});
            skPoint(sketch, "E2223.visualSharp", {"position": v(63.86, -64.8) * mm});
            skArc(sketch, "E2223.filletArc", {"start": v(63.36, -64.8) * mm, "mid": v(63.72, -64.66) * mm, "end": v(63.86, -64.3) * mm});
            skPoint(sketch, "E2224.visualSharp", {"position": v(5.86, -61.6) * mm});
            skArc(sketch, "E2224.filletArc", {"start": v(5.36, -61.6) * mm, "mid": v(5.72, -61.46) * mm, "end": v(5.86, -61.1) * mm});
            skPoint(sketch, "E2225.visualSharp", {"position": v(63.86, -49.6) * mm});
            skArc(sketch, "E2225.filletArc", {"start": v(63.86, -50.1) * mm, "mid": v(63.72, -49.76) * mm, "end": v(63.36, -49.6) * mm});
            skPoint(sketch, "E2226.visualSharp", {"position": v(103.01, -49.2) * mm});
            skArc(sketch, "E2226.filletArc", {"start": v(103.51, -49.2) * mm, "mid": v(103.16, -49.36) * mm, "end": v(103.01, -49.7) * mm});
            skPoint(sketch, "E2227.visualSharp", {"position": v(110.61, -49.2) * mm});
            skArc(sketch, "E2227.filletArc", {"start": v(110.61, -49.7) * mm, "mid": v(110.47, -49.36) * mm, "end": v(110.11, -49.2) * mm});
            skArc(sketch, "E2228", {"start": v(3.3, -61.36) * mm, "mid": v(3.48, -61.54) * mm, "end": v(3.73, -61.6) * mm});
            skArc(sketch, "E2229", {"start": v(3.3, -61.36) * mm, "mid": v(2.5, -61.26) * mm, "end": v(2.61, -62.04) * mm});
            skArc(sketch, "E2230", {"start": v(2.86, -62.48) * mm, "mid": v(2.8, -62.23) * mm, "end": v(2.61, -62.04) * mm});
            skArc(sketch, "E2231", {"start": v(61.3, -64.56) * mm, "mid": v(61.48, -64.74) * mm, "end": v(61.73, -64.8) * mm});
            skArc(sketch, "E2232", {"start": v(61.3, -64.56) * mm, "mid": v(60.5, -64.46) * mm, "end": v(60.61, -65.24) * mm});
            skArc(sketch, "E2233", {"start": v(60.86, -65.68) * mm, "mid": v(60.8, -65.43) * mm, "end": v(60.61, -65.24) * mm});
            skArc(sketch, "E2234", {"start": v(2.61, -49.38) * mm, "mid": v(2.8, -49.2) * mm, "end": v(2.86, -48.94) * mm});
            skArc(sketch, "E2235", {"start": v(2.61, -49.38) * mm, "mid": v(2.5, -50.16) * mm, "end": v(3.3, -50.06) * mm});
            skArc(sketch, "E2236", {"start": v(3.73, -49.8) * mm, "mid": v(3.48, -49.88) * mm, "end": v(3.3, -50.06) * mm});
            skArc(sketch, "E2237", {"start": v(110.36, -51.78) * mm, "mid": v(110.55, -51.6) * mm, "end": v(110.61, -51.34) * mm});
            skArc(sketch, "E2238", {"start": v(110.36, -51.78) * mm, "mid": v(110.26, -52.56) * mm, "end": v(111.05, -52.46) * mm});
            skArc(sketch, "E2239", {"start": v(111.48, -52.2) * mm, "mid": v(111.23, -52.28) * mm, "end": v(111.05, -52.46) * mm});
            skLineSegment(sketch, "E2240", {"start": v(-135.78, -65.7) * mm, "end": v(-135.78, -66) * mm});
            skPoint(sketch, "E2241.orphan", {"position": v(-135.78, -63.14) * mm});
            skArc(sketch, "E2242.filletArc", {"start": v(2.86, -27.7) * mm, "mid": v(1.4, -24.17) * mm, "end": v(-2.14, -22.7) * mm});
            skLineSegment(sketch, "E2243", {"start": v(2.86, -41.46) * mm, "end": v(-0.89, -41.46) * mm});
            skLineSegment(sketch, "E2244", {"start": v(-0.89, -41.46) * mm, "end": v(-0.89, -40.2) * mm});
            skLineSegment(sketch, "E2245", {"start": v(-0.89, -40.2) * mm, "end": v(-5.89, -40.2) * mm});
            skLineSegment(sketch, "E2246", {"start": v(-5.89, -40.2) * mm, "end": v(-5.89, -41.46) * mm});
            skLineSegment(sketch, "E2247", {"start": v(-5.89, -41.46) * mm, "end": v(-9.14, -41.46) * mm});
            skLineSegment(sketch, "E2248", {"start": v(-9.14, -41.46) * mm, "end": v(-9.14, -44.96) * mm});
            skLineSegment(sketch, "E2249", {"start": v(-9.14, -44.96) * mm, "end": v(-5.89, -44.96) * mm});
            skLineSegment(sketch, "E2250", {"start": v(-5.89, -44.96) * mm, "end": v(-5.89, -46.2) * mm});
            skLineSegment(sketch, "E2251", {"start": v(-5.89, -46.2) * mm, "end": v(-0.89, -46.2) * mm});
            skLineSegment(sketch, "E2252", {"start": v(-0.89, -46.2) * mm, "end": v(-0.89, -44.96) * mm});
            skLineSegment(sketch, "E2253", {"start": v(-0.89, -44.96) * mm, "end": v(2.86, -44.96) * mm});
            skLineSegment(sketch, "E2254", {"start": v(2.86, -70.46) * mm, "end": v(-0.89, -70.46) * mm});
            skLineSegment(sketch, "E2255", {"start": v(-0.89, -70.46) * mm, "end": v(-0.89, -69.2) * mm});
            skLineSegment(sketch, "E2256", {"start": v(-0.89, -69.2) * mm, "end": v(-5.89, -69.2) * mm});
            skLineSegment(sketch, "E2257", {"start": v(-5.89, -69.2) * mm, "end": v(-5.89, -70.46) * mm});
            skLineSegment(sketch, "E2258", {"start": v(-5.89, -70.46) * mm, "end": v(-9.14, -70.46) * mm});
            skLineSegment(sketch, "E2259", {"start": v(-9.14, -70.46) * mm, "end": v(-9.14, -73.96) * mm});
            skLineSegment(sketch, "E2260", {"start": v(-9.14, -73.96) * mm, "end": v(-5.89, -73.96) * mm});
            skLineSegment(sketch, "E2261", {"start": v(-5.89, -73.96) * mm, "end": v(-5.89, -75.2) * mm});
            skLineSegment(sketch, "E2262", {"start": v(-5.89, -75.2) * mm, "end": v(-0.89, -75.2) * mm});
            skLineSegment(sketch, "E2263", {"start": v(-0.89, -75.2) * mm, "end": v(-0.89, -73.96) * mm});
            skLineSegment(sketch, "E2264", {"start": v(-0.89, -73.96) * mm, "end": v(2.86, -73.96) * mm});
            skPoint(sketch, "E2265", {"position": v(-9.14, -43.2) * mm});
            skLineSegment(sketch, "E2266", {"start": v(60.86, -70.46) * mm, "end": v(56.56, -70.46) * mm});
            skLineSegment(sketch, "E2267", {"start": v(56.56, -70.46) * mm, "end": v(56.56, -69.2) * mm});
            skLineSegment(sketch, "E2268", {"start": v(56.56, -69.2) * mm, "end": v(51.56, -69.2) * mm});
            skLineSegment(sketch, "E2269", {"start": v(51.56, -69.2) * mm, "end": v(51.56, -70.46) * mm});
            skLineSegment(sketch, "E2270", {"start": v(51.56, -70.46) * mm, "end": v(48.86, -70.46) * mm});
            skLineSegment(sketch, "E2271", {"start": v(48.86, -70.46) * mm, "end": v(48.86, -73.96) * mm});
            skLineSegment(sketch, "E2272", {"start": v(48.86, -73.96) * mm, "end": v(51.56, -73.96) * mm});
            skLineSegment(sketch, "E2273", {"start": v(51.56, -73.96) * mm, "end": v(51.56, -75.2) * mm});
            skLineSegment(sketch, "E2274", {"start": v(51.56, -75.2) * mm, "end": v(56.56, -75.2) * mm});
            skLineSegment(sketch, "E2275", {"start": v(56.56, -75.2) * mm, "end": v(56.56, -73.96) * mm});
            skLineSegment(sketch, "E2276", {"start": v(56.56, -73.96) * mm, "end": v(60.86, -73.96) * mm});
            skLineSegment(sketch, "E2277", {"start": v(118.56, -52.2) * mm, "end": v(118.56, -56.5) * mm});
            skLineSegment(sketch, "E2278", {"start": v(118.56, -56.5) * mm, "end": v(117.31, -56.5) * mm});
            skLineSegment(sketch, "E2279", {"start": v(117.31, -56.5) * mm, "end": v(117.31, -61.5) * mm});
            skLineSegment(sketch, "E2280", {"start": v(117.31, -61.5) * mm, "end": v(118.56, -61.5) * mm});
            skLineSegment(sketch, "E2281", {"start": v(118.56, -61.5) * mm, "end": v(118.56, -64.2) * mm});
            skLineSegment(sketch, "E2282", {"start": v(118.56, -64.2) * mm, "end": v(122.06, -64.2) * mm});
            skLineSegment(sketch, "E2283", {"start": v(122.06, -64.2) * mm, "end": v(122.06, -61.5) * mm});
            skLineSegment(sketch, "E2284", {"start": v(122.06, -61.5) * mm, "end": v(123.31, -61.5) * mm});
            skLineSegment(sketch, "E2285", {"start": v(123.31, -61.5) * mm, "end": v(123.31, -56.5) * mm});
            skLineSegment(sketch, "E2286", {"start": v(123.31, -56.5) * mm, "end": v(122.06, -56.5) * mm});
            skLineSegment(sketch, "E2287", {"start": v(122.06, -56.5) * mm, "end": v(122.06, -52.2) * mm});
            skLineSegment(sketch, "E2288", {"start": v(-5.79, -28.36) * mm, "end": v(-5.79, -59.36) * mm, "construction": true});
            skPoint(sketch, "E2289", {"position": v(120.31, -64.2) * mm});
            skSolve(sketch);
        }
        {
            var Q0;
            Q0=makeQuery(id+"F8.imprint","IMPRINT",FACE,{"disambiguationData":[TD([[makeQuery(id+"F8.imprint","IMPRINT",EDGE,{"derivedFrom":sQuery(id+"F8.wireOp",EDGE,"E2108")}),1.0]])]});
            extrude(context, id + "F9", {"entities" : qUnion([Q0]), "depth" : 3 * mm, "offsetDistance" : 25 * mm});
        }
        {
            var Q0;
            Q0=makeQuery(id+"F8.imprint","IMPRINT",FACE,{"disambiguationData":[TD([[makeQuery(id+"F8.imprint","IMPRINT",EDGE,{"derivedFrom":sQuery(id+"F8.wireOp",EDGE,"9ec36198-c7e8-470f-a3a4-1dcbc08dc940")}),1.0]])]});
            var Q1;
            Q1=makeQuery(id+"F8.imprint","IMPRINT",FACE,{"disambiguationData":[TD([[makeQuery(id+"F8.imprint","IMPRINT",EDGE,{"derivedFrom":sQuery(id+"F8.wireOp",EDGE,"E2124")}),1.0]])]});
            extrude(context, id + "F10", {"entities" : qUnion([Q0, Q1]), "depth" : 3 * mm, "offsetDistance" : 25 * mm});
        }
        {
            var Q0;
            Q0=makeQuery(id+"F8.imprint","IMPRINT",FACE,{"disambiguationData":[TD([[makeQuery(id+"F8.imprint","IMPRINT",EDGE,{"derivedFrom":sQuery(id+"F8.wireOp",EDGE,"E2066")}),1.0]])]});
            extrude(context, id + "F11", {"entities" : qUnion([Q0]), "depth" : 3 * mm, "offsetDistance" : 25 * mm});
        }
        {
            var Q0;
            Q0=makeQuery(id+"F8.imprint","IMPRINT",FACE,{"disambiguationData":[TD([[makeQuery(id+"F8.imprint","IMPRINT",EDGE,{"derivedFrom":sQuery(id+"F8.wireOp",EDGE,"E2023")}),1.0]])]});
            extrude(context, id + "F12", {"entities" : qUnion([Q0]), "depth" : 3 * mm, "offsetDistance" : 25 * mm});
        }
        {
            var Q0;
            Q0=makeQuery(id+"F8.imprint","IMPRINT",FACE,{"disambiguationData":[TD([[makeQuery(id+"F8.imprint","IMPRINT",EDGE,{"derivedFrom":sQuery(id+"F8.wireOp",EDGE,"E2002")}),1.0]])]});
            extrude(context, id + "F13", {"entities" : qUnion([Q0]), "depth" : 3 * mm, "offsetDistance" : 25 * mm});
        }
        {
            var Q0;
            Q0=makeQuery(id+"F8.imprint","IMPRINT",FACE,{"disambiguationData":[TD([[makeQuery(id+"F8.imprint","IMPRINT",EDGE,{"derivedFrom":sQuery(id+"F8.wireOp",EDGE,"E1982")}),-1.0]])]});
            extrude(context, id + "F14", {"entities" : qUnion([Q0]), "depth" : 3 * mm, "offsetDistance" : 25 * mm});
        }
        {
            var Q0;
            Q0=makeQuery(id+"F8.imprint","IMPRINT",FACE,{"disambiguationData":[TD([[makeQuery(id+"F8.imprint","IMPRINT",EDGE,{"derivedFrom":sQuery(id+"F8.wireOp",EDGE,"E2086")}),1.0]])]});
            extrude(context, id + "F15", {"entities" : qUnion([Q0]), "depth" : 3 * mm, "offsetDistance" : 25 * mm});
        }
        {
            var Q0;
            Q0=makeQuery(id+"F8.imprint","IMPRINT",FACE,{"disambiguationData":[TD([[makeQuery(id+"F8.imprint","IMPRINT",EDGE,{"derivedFrom":sQuery(id+"F8.wireOp",EDGE,"E2141")}),-1.0]])]});
            extrude(context, id + "F16", {"entities" : qUnion([Q0]), "depth" : 3 * mm, "offsetDistance" : 25 * mm});
        }
        {
            var Q0;
            Q0=makeQuery(id+"F8.imprint","IMPRINT",FACE,{"disambiguationData":[TD([[makeQuery(id+"F8.imprint","IMPRINT",EDGE,{"derivedFrom":sQuery(id+"F8.wireOp",EDGE,"E2097")}),-1.0]])]});
            extrude(context, id + "F17", {"entities" : qUnion([Q0]), "depth" : 3 * mm, "offsetDistance" : 25 * mm});
        }
        {
            var Q0;
            Q0=makeQuery(id+"F8.imprint","IMPRINT",FACE,{"disambiguationData":[TD([[makeQuery(id+"F8.imprint","IMPRINT",EDGE,{"derivedFrom":sQuery(id+"F8.wireOp",EDGE,"E2174")}),-1.0]])]});
            extrude(context, id + "F18", {"entities" : qUnion([Q0]), "depth" : 3 * mm, "offsetDistance" : 25 * mm});
        }
    });
